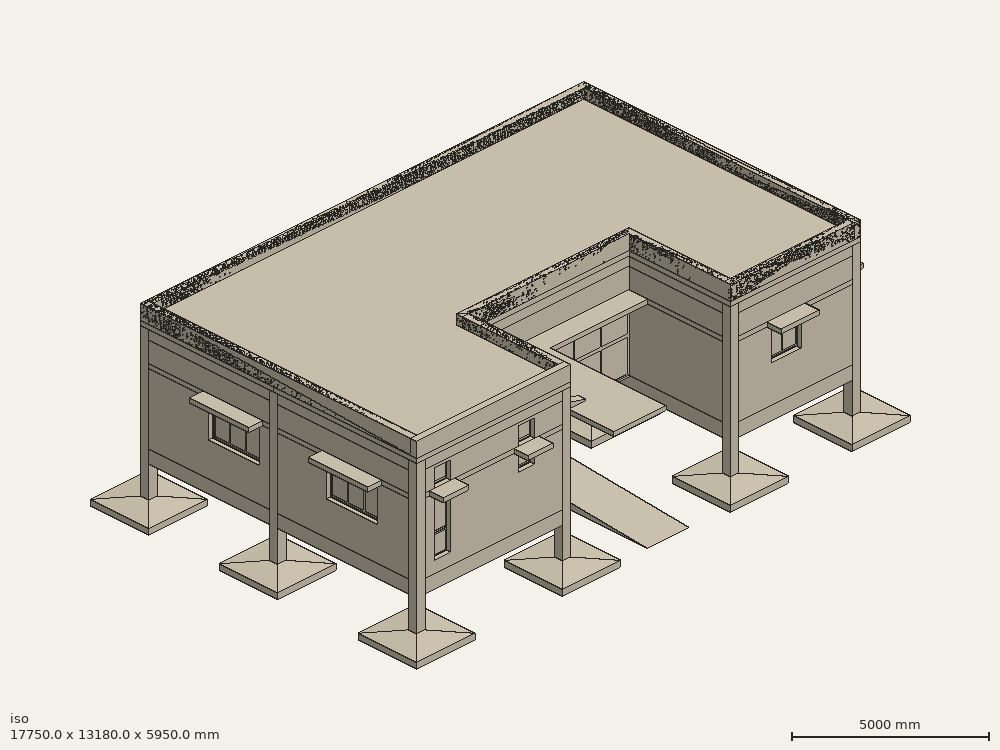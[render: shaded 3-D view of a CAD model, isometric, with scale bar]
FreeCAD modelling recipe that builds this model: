
FCSTD DOCUMENT  (FreeCAD 0.19R19955 (Git))
Label: sLAB sTEEL
License: All rights reserved
LicenseURL: http://en.wikipedia.org/wiki/All_rights_reserved
objects: Part::FeaturePython×230, Sketcher::SketchObject×144, TechDraw::DrawViewDimension×135, TechDraw::DrawViewPart×8, Part::Part2DObjectPython×7, App::FeaturePython×6, App::MaterialObjectPython×6, TechDraw::DrawViewAnnotation×5, TechDraw::DrawViewSymbol×5, App::GeometryPython×4, Spreadsheet::Sheet×3, TechDraw::DrawSVGTemplate×2, TechDraw::DrawPage×2, Part::Wedge×2, Part::Box×2, Part::MultiFuse×2, Part::Feature×1, App::DocumentObjectGroup×1, App::DocumentObjectGroupPython×1
note: 395 computed .brp shape members not serialized (recipe doc carries the construction recipe); baked Part::Feature solids carry a one-line shape summary decoded from their .brp

FEATURE [Part::Feature] Human
  Placement = pos=(500,500,0) rot=(0,0,1;0rad)
  shape: bbox 490.6 x 1.43e-06 x 1712 mm, 1 faces, 0 solids (baked)
FEATURE [Part::Part2DObjectPython] Rectangle  label="Building Outline"  # Draft 2D object (typed FeaturePython)
  Area = 0
  ChamferSize = 0
  Columns = 1
  FilletRadius = 0
  Height = 9930
  Length = 15950
  MakeFace = false
  Rows = 1
FEATURE [App::FeaturePython] Text  label="Building Label"  # WARN: FeaturePython — macro-defined, semantics opaque (R4)
  Placement = pos=(300,-1430,0) rot=(0,0,1;0rad)
  Text = Dispensary
FEATURE [Part::FeaturePython] Axis  label="Vertical Axes"  # WARN: FeaturePython — macro-defined, semantics opaque (R4)
  Angles = [0,0,0,0]
  Distances = [0,5540,5740,4670]
  Length = 10923
  Placement = pos=(0,-546.15,0) rot=(0,0,1;0rad)
  expr: Length = Rectangle.Height * 1.1000000000000001
  expr: .Placement.Base.y = Rectangle.Placement.Base.y - Length * 0.050000000000000003
  expr: .Placement.Base.x = Rectangle.Placement.Base.x
FEATURE [Part::FeaturePython] Axis001  label="Horizontal Axes"  # WARN: FeaturePython — macro-defined, semantics opaque (R4)
  Angles = [0,0,0,0]
  Distances = [0,3650,1500,4780]
  Length = 17545
  Placement = pos=(16580,0,0) rot=(0,0,1;1.5708rad)
  expr: Length = Rectangle.Length * 1.1000000000000001
  expr: .Placement.Base.x = Rectangle.Placement.Base.x + Length * 0.94499999999999995
  expr: .Placement.Base.y = Rectangle.Placement.Base.y
FEATURE [App::FeaturePython] AxisSystem  label="Axes"  # WARN: FeaturePython — macro-defined, semantics opaque (R4)
  Axes = -> [Axis001,Axis]
FEATURE [App::DocumentObjectGroup] App__DocumentObjectGroup  label="Layout"
  Group = -> [Rectangle,Text,Human,AxisSystem]
FEATURE [App::FeaturePython] WPProxy  # WARN: FeaturePython — macro-defined, semantics opaque (R4)
  Placement = pos=(0,0,3500) rot=(0,0,1;0rad)
FEATURE [App::FeaturePython] WPProxy001  # WARN: FeaturePython — macro-defined, semantics opaque (R4)
  Placement = pos=(0,0,3650) rot=(0,0,1;0rad)
FEATURE [App::FeaturePython] WPProxy002  # WARN: FeaturePython — macro-defined, semantics opaque (R4)
  Placement = pos=(0,0,2000) rot=(0,0,1;0rad)
FEATURE [Sketcher::SketchObject] WallTrace
  Placement = pos=(2770,150,0) rot=(0,0,-1;1.5708rad)
  sketch-geometry (1):
    g0: LineSegment StartX=150 StartY=-2470 StartZ=0 EndX=150 EndY=2470 EndZ=0
FEATURE [Sketcher::SketchObject] WallTrace001
  Placement = pos=(2770,150,0) rot=(0,0,-1;1.5708rad)
  sketch-geometry (1):
    g0: LineSegment StartX=150 StartY=8810 StartZ=0 EndX=150 EndY=12880 EndZ=0
FEATURE [Sketcher::SketchObject] WallTrace003
  Placement = pos=(2770,150,0) rot=(0,0,-1;1.5708rad)
  sketch-geometry (1):
    g0: LineSegment StartX=-150 StartY=13180 StartZ=0 EndX=-4850 EndY=13180 EndZ=0
FEATURE [Sketcher::SketchObject] WallTrace004
  Placement = pos=(2770,150,0) rot=(0,0,-1;1.5708rad)
  sketch-geometry (1):
    g0: LineSegment StartX=-5150 StartY=13180 StartZ=0 EndX=-9480 EndY=13180 EndZ=0
FEATURE [Sketcher::SketchObject] WallTrace005
  Placement = pos=(2770,150,0) rot=(0,0,-1;1.5708rad)
  sketch-geometry (1):
    g0: LineSegment StartX=-9780 StartY=12880 StartZ=0 EndX=-9780 EndY=8810 EndZ=0
FEATURE [Sketcher::SketchObject] WallTrace006
  Placement = pos=(2770,150,0) rot=(0,0,-1;1.5708rad)
  sketch-geometry (1):
    g0: LineSegment StartX=-9780 StartY=8510 StartZ=0 EndX=-9780 EndY=2770 EndZ=0
FEATURE [Sketcher::SketchObject] WallTrace007
  Placement = pos=(2770,150,0) rot=(0,0,-1;1.5708rad)
  sketch-geometry (1):
    g0: LineSegment StartX=-9780 StartY=2470 StartZ=0 EndX=-9780 EndY=-2470 EndZ=0
FEATURE [Sketcher::SketchObject] WallTrace008
  Placement = pos=(2770,150,0) rot=(0,0,-1;1.5708rad)
  sketch-geometry (1):
    g0: LineSegment StartX=-9480 StartY=-2770 StartZ=0 EndX=-5150 EndY=-2770 EndZ=0
FEATURE [Sketcher::SketchObject] WallTrace012
  Placement = pos=(5390,2650,0) rot=(0,0,1;0rad)
  sketch-geometry (1):
    g0: LineSegment StartX=150 StartY=-2350 StartZ=0 EndX=150 EndY=1300 EndZ=0
  constraints (2):
    c: DistanceY(g0,g-1) = 2350
    c: DistanceY(g0,g0) = 3650
FEATURE [Sketcher::SketchObject] WallTrace014
  Placement = pos=(11430,2650,0) rot=(0,0,1;0rad)
  sketch-geometry (1):
    g0: LineSegment StartX=-150 StartY=1300 StartZ=0 EndX=-150 EndY=-2350 EndZ=0
  constraints (4):
    c: DistanceX(g0,g-1) = 150
    c: Distance(g0) = 3650
    c: Vertical(g0)
    c: DistanceY(g0,g-1) = 2350
FEATURE [Part::Part2DObjectPython] Rectangle001  # Draft 2D object (typed FeaturePython)
  Area = 2.57642e+07
  ChamferSize = 0
  Columns = 1
  FilletRadius = 0
  Height = 4780
  Length = 5390
  MakeFace = true
  Placement = pos=(5390,9930,3500) rot=(0,0,1;3.14159rad)
  Rows = 1
FEATURE [Part::Part2DObjectPython] Rectangle004  # Draft 2D object (typed FeaturePython)
  Area = 2.88712e+07
  ChamferSize = 0
  Columns = 1
  FilletRadius = 0
  Height = 4780
  Length = 6040
  MakeFace = true
  Placement = pos=(11430,9930,3500) rot=(0,0,1;3.14159rad)
  Rows = 1
FEATURE [Part::Part2DObjectPython] Rectangle005  # Draft 2D object (typed FeaturePython)
  Area = 2.16056e+07
  ChamferSize = 0
  Columns = 1
  FilletRadius = 0
  Height = 4780
  Length = 4520
  MakeFace = true
  Placement = pos=(15950,9930,3500) rot=(0,0,1;3.14159rad)
  Rows = 1
FEATURE [Part::Part2DObjectPython] Rectangle006  # Draft 2D object (typed FeaturePython)
  Area = 2.40505e+07
  ChamferSize = 0
  Columns = 1
  FilletRadius = 0
  Height = 5150
  Length = 4670
  MakeFace = true
  Placement = pos=(15950,5150,3500) rot=(0,0,1;3.14159rad)
  Rows = 1
FEATURE [Part::Part2DObjectPython] Rectangle007  # Draft 2D object (typed FeaturePython)
  Area = 2.8531e+07
  ChamferSize = 0
  Columns = 1
  FilletRadius = 0
  Height = 5150
  Length = 5540
  MakeFace = true
  Placement = pos=(5540,5150,3500) rot=(0,0,1;3.14159rad)
  Rows = 1
FEATURE [Part::Part2DObjectPython] Rectangle008  # Draft 2D object (typed FeaturePython)
  Area = 9.06e+06
  ChamferSize = 0
  Columns = 1
  FilletRadius = 0
  Height = 1500
  Length = 6040
  MakeFace = true
  Placement = pos=(11430,5150,3500) rot=(0,0,1;3.14159rad)
  Rows = 1
FEATURE [Sketcher::SketchObject] Sketch
  Placement = pos=(15950,2650,1600) rot=(0.57735,0.57735,0.57735;2.0944rad)
  sketch-geometry (16):
    g0: LineSegment StartX=-2280 StartY=760 StartZ=0 EndX=-1670 EndY=760 EndZ=0
    g1: LineSegment StartX=-1670 StartY=760 StartZ=0 EndX=-1670 EndY=-1200 EndZ=0
    g2: LineSegment StartX=-1670 StartY=-1200 StartZ=0 EndX=-2280 EndY=-1200 EndZ=0
    g3: LineSegment StartX=-2280 StartY=-1200 StartZ=0 EndX=-2280 EndY=760 EndZ=0
    g4: LineSegment StartX=-2255 StartY=-675 StartZ=0 EndX=-1695 EndY=-675 EndZ=0
    g5: LineSegment StartX=-1695 StartY=-675 StartZ=0 EndX=-1695 EndY=-1175 EndZ=0
    g6: LineSegment StartX=-1695 StartY=-1175 StartZ=0 EndX=-2255 EndY=-1175 EndZ=0
    g7: LineSegment StartX=-2255 StartY=-1175 StartZ=0 EndX=-2255 EndY=-675 EndZ=0
    g8: LineSegment StartX=-2255 StartY=735 StartZ=0 EndX=-1695 EndY=735 EndZ=0
    g9: LineSegment StartX=-1695 StartY=735 StartZ=0 EndX=-1695 EndY=-625 EndZ=0
    g10: LineSegment StartX=-1695 StartY=-625 StartZ=0 EndX=-2255 EndY=-625 EndZ=0
    g11: LineSegment StartX=-2255 StartY=-625 StartZ=0 EndX=-2255 EndY=735 EndZ=0
    g12: LineSegment StartX=-2230 StartY=685 StartZ=0 EndX=-1720 EndY=685 EndZ=0
    g13: LineSegment StartX=-1720 StartY=685 StartZ=0 EndX=-1720 EndY=-575 EndZ=0
    g14: LineSegment StartX=-1720 StartY=-575 StartZ=0 EndX=-2230 EndY=-575 EndZ=0
    g15: LineSegment StartX=-2230 StartY=-575 StartZ=0 EndX=-2230 EndY=685 EndZ=0
  constraints (46):
    c: Coincident(g0,g1)
    c: Coincident(g1,g2)
    c: Coincident(g2,g3)
    c: Coincident(g3,g0)
    c: Horizontal(g0)
    c: Horizontal(g2)
    c: Vertical(g1)
    c: Vertical(g3)
    c: Coincident(g4,g5)
    c: Coincident(g5,g6)
    c: Coincident(g6,g7)
    c: Coincident(g7,g4)
    c: Horizontal(g4)
    c: Horizontal(g6)
    c: Vertical(g5)
    c: Vertical(g7)
    c: Coincident(g8,g9)
    c: Coincident(g9,g10)
    c: Coincident(g10,g11)
    c: Coincident(g11,g8)
    c: Horizontal(g8)
    c: Horizontal(g10)
    c: Vertical(g9)
    c: Vertical(g11)
    c: DistanceY(g1,g5) = 25
    c: DistanceX(g5,g1) = 25
    c: DistanceX(g2,g6) = 25
    c: DistanceY(g1,g1) = 1960
    c: DistanceY(g4,g9) = 50
    c: DistanceX(g4,g10) = 0
    c: DistanceX(g9,g4) = 0
    c: DistanceY(g8,g0) = 25
    c: Coincident(g12,g13)
    c: Coincident(g13,g14)
    c: Coincident(g14,g15)
    c: Coincident(g15,g12)
    c: Horizontal(g12)
    c: Horizontal(g14)
    c: Vertical(g13)
    c: Vertical(g15)
    c: DistanceY(g12,g8) = 50
    c: DistanceY(g9,g13) = 50
    c: DistanceX(g13,g9) = 25
    c: DistanceX(g10,g14) = 25
    c: DistanceX(g0,g0) = 610
    c: DistanceY(g5,g5) = 500
FEATURE [Sketcher::SketchObject] Sketch001
  Placement = pos=(15950,2650,1600) rot=(0.57735,0.57735,0.57735;2.0944rad)
  sketch-geometry (16):
    g0: LineSegment StartX=-2280 StartY=760 StartZ=0 EndX=-1670 EndY=760 EndZ=0
    g1: LineSegment StartX=-1670 StartY=760 StartZ=0 EndX=-1670 EndY=-1200 EndZ=0
    g2: LineSegment StartX=-1670 StartY=-1200 StartZ=0 EndX=-2280 EndY=-1200 EndZ=0
    g3: LineSegment StartX=-2280 StartY=-1200 StartZ=0 EndX=-2280 EndY=760 EndZ=0
    g4: LineSegment StartX=-2255 StartY=-675 StartZ=0 EndX=-1695 EndY=-675 EndZ=0
    g5: LineSegment StartX=-1695 StartY=-675 StartZ=0 EndX=-1695 EndY=-1175 EndZ=0
    g6: LineSegment StartX=-1695 StartY=-1175 StartZ=0 EndX=-2255 EndY=-1175 EndZ=0
    g7: LineSegment StartX=-2255 StartY=-1175 StartZ=0 EndX=-2255 EndY=-675 EndZ=0
    g8: LineSegment StartX=-2255 StartY=735 StartZ=0 EndX=-1695 EndY=735 EndZ=0
    g9: LineSegment StartX=-1695 StartY=735 StartZ=0 EndX=-1695 EndY=-625 EndZ=0
    g10: LineSegment StartX=-1695 StartY=-625 StartZ=0 EndX=-2255 EndY=-625 EndZ=0
    g11: LineSegment StartX=-2255 StartY=-625 StartZ=0 EndX=-2255 EndY=735 EndZ=0
    g12: LineSegment StartX=-2230 StartY=685 StartZ=0 EndX=-1720 EndY=685 EndZ=0
    g13: LineSegment StartX=-1720 StartY=685 StartZ=0 EndX=-1720 EndY=-575 EndZ=0
    g14: LineSegment StartX=-1720 StartY=-575 StartZ=0 EndX=-2230 EndY=-575 EndZ=0
    g15: LineSegment StartX=-2230 StartY=-575 StartZ=0 EndX=-2230 EndY=685 EndZ=0
  constraints (46):
    c: Coincident(g0,g1)
    c: Coincident(g1,g2)
    c: Coincident(g2,g3)
    c: Coincident(g3,g0)
    c: Horizontal(g0)
    c: Horizontal(g2)
    c: Vertical(g1)
    c: Vertical(g3)
    c: Coincident(g4,g5)
    c: Coincident(g5,g6)
    c: Coincident(g6,g7)
    c: Coincident(g7,g4)
    c: Horizontal(g4)
    c: Horizontal(g6)
    c: Vertical(g5)
    c: Vertical(g7)
    c: Coincident(g8,g9)
    c: Coincident(g9,g10)
    c: Coincident(g10,g11)
    c: Coincident(g11,g8)
    c: Horizontal(g8)
    c: Horizontal(g10)
    c: Vertical(g9)
    c: Vertical(g11)
    c: DistanceY(g1,g5) = 25
    c: DistanceX(g5,g1) = 25
    c: DistanceX(g2,g6) = 25
    c: DistanceY(g1,g1) = 1960
    c: DistanceY(g4,g9) = 50
    c: DistanceX(g4,g10) = 0
    c: DistanceX(g9,g4) = 0
    c: DistanceY(g8,g0) = 25
    c: Coincident(g12,g13)
    c: Coincident(g13,g14)
    c: Coincident(g14,g15)
    c: Coincident(g15,g12)
    c: Horizontal(g12)
    c: Horizontal(g14)
    c: Vertical(g13)
    c: Vertical(g15)
    c: DistanceY(g12,g8) = 50
    c: DistanceY(g9,g13) = 50
    c: DistanceX(g13,g9) = 25
    c: DistanceX(g10,g14) = 25
    c: DistanceX(g0,g0) = 610
    c: DistanceY(g5,g5) = 500
FEATURE [Sketcher::SketchObject] Sketch002
  Placement = pos=(15950,2650,1600) rot=(0.57735,0.57735,0.57735;2.0944rad)
  sketch-geometry (16):
    g0: LineSegment StartX=-2280 StartY=760 StartZ=0 EndX=-1670 EndY=760 EndZ=0
    g1: LineSegment StartX=-1670 StartY=760 StartZ=0 EndX=-1670 EndY=-1200 EndZ=0
    g2: LineSegment StartX=-1670 StartY=-1200 StartZ=0 EndX=-2280 EndY=-1200 EndZ=0
    g3: LineSegment StartX=-2280 StartY=-1200 StartZ=0 EndX=-2280 EndY=760 EndZ=0
    g4: LineSegment StartX=-2255 StartY=-675 StartZ=0 EndX=-1695 EndY=-675 EndZ=0
    g5: LineSegment StartX=-1695 StartY=-675 StartZ=0 EndX=-1695 EndY=-1175 EndZ=0
    g6: LineSegment StartX=-1695 StartY=-1175 StartZ=0 EndX=-2255 EndY=-1175 EndZ=0
    g7: LineSegment StartX=-2255 StartY=-1175 StartZ=0 EndX=-2255 EndY=-675 EndZ=0
    g8: LineSegment StartX=-2255 StartY=735 StartZ=0 EndX=-1695 EndY=735 EndZ=0
    g9: LineSegment StartX=-1695 StartY=735 StartZ=0 EndX=-1695 EndY=-625 EndZ=0
    g10: LineSegment StartX=-1695 StartY=-625 StartZ=0 EndX=-2255 EndY=-625 EndZ=0
    g11: LineSegment StartX=-2255 StartY=-625 StartZ=0 EndX=-2255 EndY=735 EndZ=0
    g12: LineSegment StartX=-2230 StartY=685 StartZ=0 EndX=-1720 EndY=685 EndZ=0
    g13: LineSegment StartX=-1720 StartY=685 StartZ=0 EndX=-1720 EndY=-575 EndZ=0
    g14: LineSegment StartX=-1720 StartY=-575 StartZ=0 EndX=-2230 EndY=-575 EndZ=0
    g15: LineSegment StartX=-2230 StartY=-575 StartZ=0 EndX=-2230 EndY=685 EndZ=0
  constraints (46):
    c: Coincident(g0,g1)
    c: Coincident(g1,g2)
    c: Coincident(g2,g3)
    c: Coincident(g3,g0)
    c: Horizontal(g0)
    c: Horizontal(g2)
    c: Vertical(g1)
    c: Vertical(g3)
    c: Coincident(g4,g5)
    c: Coincident(g5,g6)
    c: Coincident(g6,g7)
    c: Coincident(g7,g4)
    c: Horizontal(g4)
    c: Horizontal(g6)
    c: Vertical(g5)
    c: Vertical(g7)
    c: Coincident(g8,g9)
    c: Coincident(g9,g10)
    c: Coincident(g10,g11)
    c: Coincident(g11,g8)
    c: Horizontal(g8)
    c: Horizontal(g10)
    c: Vertical(g9)
    c: Vertical(g11)
    c: DistanceY(g1,g5) = 25
    c: DistanceX(g5,g1) = 25
    c: DistanceX(g2,g6) = 25
    c: DistanceY(g1,g1) = 1960
    c: DistanceY(g4,g9) = 50
    c: DistanceX(g4,g10) = 0
    c: DistanceX(g9,g4) = 0
    c: DistanceY(g8,g0) = 25
    c: Coincident(g12,g13)
    c: Coincident(g13,g14)
    c: Coincident(g14,g15)
    c: Coincident(g15,g12)
    c: Horizontal(g12)
    c: Horizontal(g14)
    c: Vertical(g13)
    c: Vertical(g15)
    c: DistanceY(g12,g8) = 50
    c: DistanceY(g9,g13) = 50
    c: DistanceX(g13,g9) = 25
    c: DistanceX(g10,g14) = 25
    c: DistanceX(g0,g0) = 610
    c: DistanceY(g5,g5) = 500
FEATURE [Sketcher::SketchObject] Sketch003
  Placement = pos=(15950,2650,1600) rot=(0.57735,0.57735,0.57735;2.0944rad)
  sketch-geometry (16):
    g0: LineSegment StartX=-2280 StartY=760 StartZ=0 EndX=-1670 EndY=760 EndZ=0
    g1: LineSegment StartX=-1670 StartY=760 StartZ=0 EndX=-1670 EndY=-1200 EndZ=0
    g2: LineSegment StartX=-1670 StartY=-1200 StartZ=0 EndX=-2280 EndY=-1200 EndZ=0
    g3: LineSegment StartX=-2280 StartY=-1200 StartZ=0 EndX=-2280 EndY=760 EndZ=0
    g4: LineSegment StartX=-2255 StartY=-675 StartZ=0 EndX=-1695 EndY=-675 EndZ=0
    g5: LineSegment StartX=-1695 StartY=-675 StartZ=0 EndX=-1695 EndY=-1175 EndZ=0
    g6: LineSegment StartX=-1695 StartY=-1175 StartZ=0 EndX=-2255 EndY=-1175 EndZ=0
    g7: LineSegment StartX=-2255 StartY=-1175 StartZ=0 EndX=-2255 EndY=-675 EndZ=0
    g8: LineSegment StartX=-2255 StartY=735 StartZ=0 EndX=-1695 EndY=735 EndZ=0
    g9: LineSegment StartX=-1695 StartY=735 StartZ=0 EndX=-1695 EndY=-625 EndZ=0
    g10: LineSegment StartX=-1695 StartY=-625 StartZ=0 EndX=-2255 EndY=-625 EndZ=0
    g11: LineSegment StartX=-2255 StartY=-625 StartZ=0 EndX=-2255 EndY=735 EndZ=0
    g12: LineSegment StartX=-2230 StartY=685 StartZ=0 EndX=-1720 EndY=685 EndZ=0
    g13: LineSegment StartX=-1720 StartY=685 StartZ=0 EndX=-1720 EndY=-575 EndZ=0
    g14: LineSegment StartX=-1720 StartY=-575 StartZ=0 EndX=-2230 EndY=-575 EndZ=0
    g15: LineSegment StartX=-2230 StartY=-575 StartZ=0 EndX=-2230 EndY=685 EndZ=0
  constraints (46):
    c: Coincident(g0,g1)
    c: Coincident(g1,g2)
    c: Coincident(g2,g3)
    c: Coincident(g3,g0)
    c: Horizontal(g0)
    c: Horizontal(g2)
    c: Vertical(g1)
    c: Vertical(g3)
    c: Coincident(g4,g5)
    c: Coincident(g5,g6)
    c: Coincident(g6,g7)
    c: Coincident(g7,g4)
    c: Horizontal(g4)
    c: Horizontal(g6)
    c: Vertical(g5)
    c: Vertical(g7)
    c: Coincident(g8,g9)
    c: Coincident(g9,g10)
    c: Coincident(g10,g11)
    c: Coincident(g11,g8)
    c: Horizontal(g8)
    c: Horizontal(g10)
    c: Vertical(g9)
    c: Vertical(g11)
    c: DistanceY(g1,g5) = 25
    c: DistanceX(g5,g1) = 25
    c: DistanceX(g2,g6) = 25
    c: DistanceY(g1,g1) = 1960
    c: DistanceY(g4,g9) = 50
    c: DistanceX(g4,g10) = 0
    c: DistanceX(g9,g4) = 0
    c: DistanceY(g8,g0) = 25
    c: Coincident(g12,g13)
    c: Coincident(g13,g14)
    c: Coincident(g14,g15)
    c: Coincident(g15,g12)
    c: Horizontal(g12)
    c: Horizontal(g14)
    c: Vertical(g13)
    c: Vertical(g15)
    c: DistanceY(g12,g8) = 50
    c: DistanceY(g9,g13) = 50
    c: DistanceX(g13,g9) = 25
    c: DistanceX(g10,g14) = 25
    c: DistanceX(g0,g0) = 610
    c: DistanceY(g5,g5) = 500
FEATURE [Sketcher::SketchObject] Sketch006
  Placement = pos=(15950,2698.54,1668.9) rot=(0.57735,0.57735,0.57735;2.0944rad)
  sketch-geometry (12):
    g0: LineSegment StartX=-2328.54 StartY=1451.1 StartZ=0 EndX=-1718.54 EndY=1451.1 EndZ=0
    g1: LineSegment StartX=-1718.54 StartY=1451.1 StartZ=0 EndX=-1718.54 EndY=841.103 EndZ=0
    g2: LineSegment StartX=-1718.54 StartY=841.103 StartZ=0 EndX=-2328.54 EndY=841.103 EndZ=0
    g3: LineSegment StartX=-2328.54 StartY=841.103 StartZ=0 EndX=-2328.54 EndY=1451.1 EndZ=0
    g4: LineSegment StartX=-2303.54 StartY=1426.1 StartZ=0 EndX=-1743.54 EndY=1426.1 EndZ=0
    g5: LineSegment StartX=-1743.54 StartY=1426.1 StartZ=0 EndX=-1743.54 EndY=866.103 EndZ=0
    g6: LineSegment StartX=-1743.54 StartY=866.103 StartZ=0 EndX=-2303.54 EndY=866.103 EndZ=0
    g7: LineSegment StartX=-2303.54 StartY=866.103 StartZ=0 EndX=-2303.54 EndY=1426.1 EndZ=0
    g8: LineSegment StartX=-2278.54 StartY=1376.1 StartZ=0 EndX=-1768.54 EndY=1376.1 EndZ=0
    g9: LineSegment StartX=-1768.54 StartY=1376.1 StartZ=0 EndX=-1768.54 EndY=916.103 EndZ=0
    g10: LineSegment StartX=-1768.54 StartY=916.103 StartZ=0 EndX=-2278.54 EndY=916.103 EndZ=0
    g11: LineSegment StartX=-2278.54 StartY=916.103 StartZ=0 EndX=-2278.54 EndY=1376.1 EndZ=0
  constraints (34):
    c: Coincident(g0,g1)
    c: Coincident(g1,g2)
    c: Coincident(g2,g3)
    c: Coincident(g3,g0)
    c: Horizontal(g0)
    c: Horizontal(g2)
    c: Vertical(g1)
    c: Vertical(g3)
    c: Coincident(g4,g5)
    c: Coincident(g5,g6)
    c: Coincident(g6,g7)
    c: Coincident(g7,g4)
    c: Horizontal(g4)
    c: Horizontal(g6)
    c: Vertical(g5)
    c: Vertical(g7)
    c: Coincident(g8,g9)
    c: Coincident(g9,g10)
    c: Coincident(g10,g11)
    c: Coincident(g11,g8)
    c: Horizontal(g8)
    c: Horizontal(g10)
    c: Vertical(g9)
    c: Vertical(g11)
    c: DistanceY(g4,g0) = 25
    c: DistanceY(g1,g5) = 25
    c: DistanceY(g5,g9) = 50
    c: DistanceY(g8,g4) = 50
    c: DistanceY(g1,g1) = 610
    c: DistanceX(g4,g8) = 25
    c: DistanceX(g0,g4) = 25
    c: DistanceX(g8,g4) = 25
    c: DistanceX(g5,g1) = 25
    c: DistanceX(g2,g2) = 610
FEATURE [Sketcher::SketchObject] Sketch007
  Placement = pos=(15950,2698.54,1668.9) rot=(0.57735,0.57735,0.57735;2.0944rad)
  sketch-geometry (12):
    g0: LineSegment StartX=-2328.54 StartY=1451.1 StartZ=0 EndX=-1718.54 EndY=1451.1 EndZ=0
    g1: LineSegment StartX=-1718.54 StartY=1451.1 StartZ=0 EndX=-1718.54 EndY=841.103 EndZ=0
    g2: LineSegment StartX=-1718.54 StartY=841.103 StartZ=0 EndX=-2328.54 EndY=841.103 EndZ=0
    g3: LineSegment StartX=-2328.54 StartY=841.103 StartZ=0 EndX=-2328.54 EndY=1451.1 EndZ=0
    g4: LineSegment StartX=-2303.54 StartY=1426.1 StartZ=0 EndX=-1743.54 EndY=1426.1 EndZ=0
    g5: LineSegment StartX=-1743.54 StartY=1426.1 StartZ=0 EndX=-1743.54 EndY=866.103 EndZ=0
    g6: LineSegment StartX=-1743.54 StartY=866.103 StartZ=0 EndX=-2303.54 EndY=866.103 EndZ=0
    g7: LineSegment StartX=-2303.54 StartY=866.103 StartZ=0 EndX=-2303.54 EndY=1426.1 EndZ=0
    g8: LineSegment StartX=-2278.54 StartY=1376.1 StartZ=0 EndX=-1768.54 EndY=1376.1 EndZ=0
    g9: LineSegment StartX=-1768.54 StartY=1376.1 StartZ=0 EndX=-1768.54 EndY=916.103 EndZ=0
    g10: LineSegment StartX=-1768.54 StartY=916.103 StartZ=0 EndX=-2278.54 EndY=916.103 EndZ=0
    g11: LineSegment StartX=-2278.54 StartY=916.103 StartZ=0 EndX=-2278.54 EndY=1376.1 EndZ=0
  constraints (34):
    c: Coincident(g0,g1)
    c: Coincident(g1,g2)
    c: Coincident(g2,g3)
    c: Coincident(g3,g0)
    c: Horizontal(g0)
    c: Horizontal(g2)
    c: Vertical(g1)
    c: Vertical(g3)
    c: Coincident(g4,g5)
    c: Coincident(g5,g6)
    c: Coincident(g6,g7)
    c: Coincident(g7,g4)
    c: Horizontal(g4)
    c: Horizontal(g6)
    c: Vertical(g5)
    c: Vertical(g7)
    c: Coincident(g8,g9)
    c: Coincident(g9,g10)
    c: Coincident(g10,g11)
    c: Coincident(g11,g8)
    c: Horizontal(g8)
    c: Horizontal(g10)
    c: Vertical(g9)
    c: Vertical(g11)
    c: DistanceY(g4,g0) = 25
    c: DistanceY(g1,g5) = 25
    c: DistanceY(g5,g9) = 50
    c: DistanceY(g8,g4) = 50
    c: DistanceY(g1,g1) = 610
    c: DistanceX(g4,g8) = 25
    c: DistanceX(g0,g4) = 25
    c: DistanceX(g8,g4) = 25
    c: DistanceX(g5,g1) = 25
    c: DistanceX(g2,g2) = 610
FEATURE [Sketcher::SketchObject] Sketch008
  Placement = pos=(15950,2698.54,1668.9) rot=(0.57735,0.57735,0.57735;2.0944rad)
  sketch-geometry (12):
    g0: LineSegment StartX=-2328.54 StartY=1451.1 StartZ=0 EndX=-1718.54 EndY=1451.1 EndZ=0
    g1: LineSegment StartX=-1718.54 StartY=1451.1 StartZ=0 EndX=-1718.54 EndY=841.103 EndZ=0
    g2: LineSegment StartX=-1718.54 StartY=841.103 StartZ=0 EndX=-2328.54 EndY=841.103 EndZ=0
    g3: LineSegment StartX=-2328.54 StartY=841.103 StartZ=0 EndX=-2328.54 EndY=1451.1 EndZ=0
    g4: LineSegment StartX=-2303.54 StartY=1426.1 StartZ=0 EndX=-1743.54 EndY=1426.1 EndZ=0
    g5: LineSegment StartX=-1743.54 StartY=1426.1 StartZ=0 EndX=-1743.54 EndY=866.103 EndZ=0
    g6: LineSegment StartX=-1743.54 StartY=866.103 StartZ=0 EndX=-2303.54 EndY=866.103 EndZ=0
    g7: LineSegment StartX=-2303.54 StartY=866.103 StartZ=0 EndX=-2303.54 EndY=1426.1 EndZ=0
    g8: LineSegment StartX=-2278.54 StartY=1376.1 StartZ=0 EndX=-1768.54 EndY=1376.1 EndZ=0
    g9: LineSegment StartX=-1768.54 StartY=1376.1 StartZ=0 EndX=-1768.54 EndY=916.103 EndZ=0
    g10: LineSegment StartX=-1768.54 StartY=916.103 StartZ=0 EndX=-2278.54 EndY=916.103 EndZ=0
    g11: LineSegment StartX=-2278.54 StartY=916.103 StartZ=0 EndX=-2278.54 EndY=1376.1 EndZ=0
  constraints (34):
    c: Coincident(g0,g1)
    c: Coincident(g1,g2)
    c: Coincident(g2,g3)
    c: Coincident(g3,g0)
    c: Horizontal(g0)
    c: Horizontal(g2)
    c: Vertical(g1)
    c: Vertical(g3)
    c: Coincident(g4,g5)
    c: Coincident(g5,g6)
    c: Coincident(g6,g7)
    c: Coincident(g7,g4)
    c: Horizontal(g4)
    c: Horizontal(g6)
    c: Vertical(g5)
    c: Vertical(g7)
    c: Coincident(g8,g9)
    c: Coincident(g9,g10)
    c: Coincident(g10,g11)
    c: Coincident(g11,g8)
    c: Horizontal(g8)
    c: Horizontal(g10)
    c: Vertical(g9)
    c: Vertical(g11)
    c: DistanceY(g4,g0) = 25
    c: DistanceY(g1,g5) = 25
    c: DistanceY(g5,g9) = 50
    c: DistanceY(g8,g4) = 50
    c: DistanceY(g1,g1) = 610
    c: DistanceX(g4,g8) = 25
    c: DistanceX(g0,g4) = 25
    c: DistanceX(g8,g4) = 25
    c: DistanceX(g5,g1) = 25
    c: DistanceX(g2,g2) = 610
FEATURE [Sketcher::SketchObject] Sketch009
  Placement = pos=(15950,2698.54,1668.9) rot=(0.57735,0.57735,0.57735;2.0944rad)
  sketch-geometry (12):
    g0: LineSegment StartX=-2328.54 StartY=1451.1 StartZ=0 EndX=-1718.54 EndY=1451.1 EndZ=0
    g1: LineSegment StartX=-1718.54 StartY=1451.1 StartZ=0 EndX=-1718.54 EndY=841.103 EndZ=0
    g2: LineSegment StartX=-1718.54 StartY=841.103 StartZ=0 EndX=-2328.54 EndY=841.103 EndZ=0
    g3: LineSegment StartX=-2328.54 StartY=841.103 StartZ=0 EndX=-2328.54 EndY=1451.1 EndZ=0
    g4: LineSegment StartX=-2303.54 StartY=1426.1 StartZ=0 EndX=-1743.54 EndY=1426.1 EndZ=0
    g5: LineSegment StartX=-1743.54 StartY=1426.1 StartZ=0 EndX=-1743.54 EndY=866.103 EndZ=0
    g6: LineSegment StartX=-1743.54 StartY=866.103 StartZ=0 EndX=-2303.54 EndY=866.103 EndZ=0
    g7: LineSegment StartX=-2303.54 StartY=866.103 StartZ=0 EndX=-2303.54 EndY=1426.1 EndZ=0
    g8: LineSegment StartX=-2278.54 StartY=1376.1 StartZ=0 EndX=-1768.54 EndY=1376.1 EndZ=0
    g9: LineSegment StartX=-1768.54 StartY=1376.1 StartZ=0 EndX=-1768.54 EndY=916.103 EndZ=0
    g10: LineSegment StartX=-1768.54 StartY=916.103 StartZ=0 EndX=-2278.54 EndY=916.103 EndZ=0
    g11: LineSegment StartX=-2278.54 StartY=916.103 StartZ=0 EndX=-2278.54 EndY=1376.1 EndZ=0
  constraints (34):
    c: Coincident(g0,g1)
    c: Coincident(g1,g2)
    c: Coincident(g2,g3)
    c: Coincident(g3,g0)
    c: Horizontal(g0)
    c: Horizontal(g2)
    c: Vertical(g1)
    c: Vertical(g3)
    c: Coincident(g4,g5)
    c: Coincident(g5,g6)
    c: Coincident(g6,g7)
    c: Coincident(g7,g4)
    c: Horizontal(g4)
    c: Horizontal(g6)
    c: Vertical(g5)
    c: Vertical(g7)
    c: Coincident(g8,g9)
    c: Coincident(g9,g10)
    c: Coincident(g10,g11)
    c: Coincident(g11,g8)
    c: Horizontal(g8)
    c: Horizontal(g10)
    c: Vertical(g9)
    c: Vertical(g11)
    c: DistanceY(g4,g0) = 25
    c: DistanceY(g1,g5) = 25
    c: DistanceY(g5,g9) = 50
    c: DistanceY(g8,g4) = 50
    c: DistanceY(g1,g1) = 610
    c: DistanceX(g4,g8) = 25
    c: DistanceX(g0,g4) = 25
    c: DistanceX(g8,g4) = 25
    c: DistanceX(g5,g1) = 25
    c: DistanceX(g2,g2) = 610
FEATURE [Sketcher::SketchObject] Sketch011
  Placement = pos=(15950,2724.08,1084.42) rot=(0.57735,0.57735,0.57735;2.0944rad)
  sketch-geometry (4):
    g0: LineSegment StartX=-2504.08 StartY=1425.58 StartZ=0 EndX=-1594.08 EndY=1425.58 EndZ=0
    g1: LineSegment StartX=-1594.08 StartY=1425.58 StartZ=0 EndX=-1594.08 EndY=1275.58 EndZ=0
    g2: LineSegment StartX=-1594.08 StartY=1275.58 StartZ=0 EndX=-2504.08 EndY=1275.58 EndZ=0
    g3: LineSegment StartX=-2504.08 StartY=1275.58 StartZ=0 EndX=-2504.08 EndY=1425.58 EndZ=0
  constraints (10):
    c: Coincident(g0,g1)
    c: Coincident(g1,g2)
    c: Coincident(g2,g3)
    c: Coincident(g3,g0)
    c: Horizontal(g0)
    c: Horizontal(g2)
    c: Vertical(g1)
    c: Vertical(g3)
    c: DistanceY(g1,g1) = 150
    c: DistanceX(g0,g0) = 910
FEATURE [Sketcher::SketchObject] Sketch012
  Placement = pos=(15950,2724.08,1084.42) rot=(0.57735,0.57735,0.57735;2.0944rad)
  sketch-geometry (4):
    g0: LineSegment StartX=-2504.08 StartY=1425.58 StartZ=0 EndX=-1594.08 EndY=1425.58 EndZ=0
    g1: LineSegment StartX=-1594.08 StartY=1425.58 StartZ=0 EndX=-1594.08 EndY=1275.58 EndZ=0
    g2: LineSegment StartX=-1594.08 StartY=1275.58 StartZ=0 EndX=-2504.08 EndY=1275.58 EndZ=0
    g3: LineSegment StartX=-2504.08 StartY=1275.58 StartZ=0 EndX=-2504.08 EndY=1425.58 EndZ=0
  constraints (10):
    c: Coincident(g0,g1)
    c: Coincident(g1,g2)
    c: Coincident(g2,g3)
    c: Coincident(g3,g0)
    c: Horizontal(g0)
    c: Horizontal(g2)
    c: Vertical(g1)
    c: Vertical(g3)
    c: DistanceY(g1,g1) = 150
    c: DistanceX(g0,g0) = 910
FEATURE [Sketcher::SketchObject] Sketch013
  Placement = pos=(15950,2724.08,1084.42) rot=(0.57735,0.57735,0.57735;2.0944rad)
  sketch-geometry (4):
    g0: LineSegment StartX=-2504.08 StartY=1425.58 StartZ=0 EndX=-1594.08 EndY=1425.58 EndZ=0
    g1: LineSegment StartX=-1594.08 StartY=1425.58 StartZ=0 EndX=-1594.08 EndY=1275.58 EndZ=0
    g2: LineSegment StartX=-1594.08 StartY=1275.58 StartZ=0 EndX=-2504.08 EndY=1275.58 EndZ=0
    g3: LineSegment StartX=-2504.08 StartY=1275.58 StartZ=0 EndX=-2504.08 EndY=1425.58 EndZ=0
  constraints (10):
    c: Coincident(g0,g1)
    c: Coincident(g1,g2)
    c: Coincident(g2,g3)
    c: Coincident(g3,g0)
    c: Horizontal(g0)
    c: Horizontal(g2)
    c: Vertical(g1)
    c: Vertical(g3)
    c: DistanceY(g1,g1) = 150
    c: DistanceX(g0,g0) = 910
FEATURE [Sketcher::SketchObject] Sketch014
  Placement = pos=(15950,2724.08,1084.42) rot=(0.57735,0.57735,0.57735;2.0944rad)
  sketch-geometry (4):
    g0: LineSegment StartX=-2504.08 StartY=1425.58 StartZ=0 EndX=-1594.08 EndY=1425.58 EndZ=0
    g1: LineSegment StartX=-1594.08 StartY=1425.58 StartZ=0 EndX=-1594.08 EndY=1275.58 EndZ=0
    g2: LineSegment StartX=-1594.08 StartY=1275.58 StartZ=0 EndX=-2504.08 EndY=1275.58 EndZ=0
    g3: LineSegment StartX=-2504.08 StartY=1275.58 StartZ=0 EndX=-2504.08 EndY=1425.58 EndZ=0
  constraints (10):
    c: Coincident(g0,g1)
    c: Coincident(g1,g2)
    c: Coincident(g2,g3)
    c: Coincident(g3,g0)
    c: Horizontal(g0)
    c: Horizontal(g2)
    c: Vertical(g1)
    c: Vertical(g3)
    c: DistanceY(g1,g1) = 150
    c: DistanceX(g0,g0) = 910
FEATURE [Sketcher::SketchObject] Sketch016
  Placement = pos=(13615,9930,1600) rot=(0,0.707107,0.707107;3.14159rad)
  sketch-geometry (12):
    g0: LineSegment StartX=-1875 StartY=760 StartZ=0 EndX=-1265 EndY=760 EndZ=0
    g1: LineSegment StartX=-1265 StartY=760 StartZ=0 EndX=-1265 EndY=150 EndZ=0
    g2: LineSegment StartX=-1265 StartY=150 StartZ=0 EndX=-1875 EndY=150 EndZ=0
    g3: LineSegment StartX=-1875 StartY=150 StartZ=0 EndX=-1875 EndY=760 EndZ=0
    g4: LineSegment StartX=-1850 StartY=735 StartZ=0 EndX=-1290 EndY=735 EndZ=0
    g5: LineSegment StartX=-1290 StartY=735 StartZ=0 EndX=-1290 EndY=175 EndZ=0
    g6: LineSegment StartX=-1290 StartY=175 StartZ=0 EndX=-1850 EndY=175 EndZ=0
    g7: LineSegment StartX=-1850 StartY=175 StartZ=0 EndX=-1850 EndY=735 EndZ=0
    g8: LineSegment StartX=-1825 StartY=685 StartZ=0 EndX=-1315 EndY=685 EndZ=0
    g9: LineSegment StartX=-1315 StartY=685 StartZ=0 EndX=-1315 EndY=225 EndZ=0
    g10: LineSegment StartX=-1315 StartY=225 StartZ=0 EndX=-1825 EndY=225 EndZ=0
    g11: LineSegment StartX=-1825 StartY=225 StartZ=0 EndX=-1825 EndY=685 EndZ=0
  constraints (34):
    c: Coincident(g0,g1)
    c: Coincident(g1,g2)
    c: Coincident(g2,g3)
    c: Coincident(g3,g0)
    c: Horizontal(g0)
    c: Horizontal(g2)
    c: Vertical(g1)
    c: Vertical(g3)
    c: Coincident(g4,g5)
    c: Coincident(g5,g6)
    c: Coincident(g6,g7)
    c: Coincident(g7,g4)
    c: Horizontal(g4)
    c: Horizontal(g6)
    c: Vertical(g5)
    c: Vertical(g7)
    c: Coincident(g8,g9)
    c: Coincident(g9,g10)
    c: Coincident(g10,g11)
    c: Coincident(g11,g8)
    c: Horizontal(g8)
    c: Horizontal(g10)
    c: Vertical(g9)
    c: Vertical(g11)
    c: DistanceX(g4,g0) = 25
    c: DistanceX(g0,g4) = 25
    c: DistanceX(g4,g8) = 25
    c: DistanceX(g8,g4) = 25
    c: DistanceX(g0,g0) = 610
    c: DistanceY(g4,g0) = 25
    c: DistanceY(g8,g4) = 50
    c: DistanceY(g5,g9) = 50
    c: DistanceY(g1,g5) = 25
    c: DistanceY(g1,g1) = 610
FEATURE [Sketcher::SketchObject] Sketch017
  Placement = pos=(13615,9930,1600) rot=(0,0.707107,0.707107;3.14159rad)
  sketch-geometry (12):
    g0: LineSegment StartX=-1875 StartY=760 StartZ=0 EndX=-1265 EndY=760 EndZ=0
    g1: LineSegment StartX=-1265 StartY=760 StartZ=0 EndX=-1265 EndY=150 EndZ=0
    g2: LineSegment StartX=-1265 StartY=150 StartZ=0 EndX=-1875 EndY=150 EndZ=0
    g3: LineSegment StartX=-1875 StartY=150 StartZ=0 EndX=-1875 EndY=760 EndZ=0
    g4: LineSegment StartX=-1850 StartY=735 StartZ=0 EndX=-1290 EndY=735 EndZ=0
    g5: LineSegment StartX=-1290 StartY=735 StartZ=0 EndX=-1290 EndY=175 EndZ=0
    g6: LineSegment StartX=-1290 StartY=175 StartZ=0 EndX=-1850 EndY=175 EndZ=0
    g7: LineSegment StartX=-1850 StartY=175 StartZ=0 EndX=-1850 EndY=735 EndZ=0
    g8: LineSegment StartX=-1825 StartY=685 StartZ=0 EndX=-1315 EndY=685 EndZ=0
    g9: LineSegment StartX=-1315 StartY=685 StartZ=0 EndX=-1315 EndY=225 EndZ=0
    g10: LineSegment StartX=-1315 StartY=225 StartZ=0 EndX=-1825 EndY=225 EndZ=0
    g11: LineSegment StartX=-1825 StartY=225 StartZ=0 EndX=-1825 EndY=685 EndZ=0
  constraints (34):
    c: Coincident(g0,g1)
    c: Coincident(g1,g2)
    c: Coincident(g2,g3)
    c: Coincident(g3,g0)
    c: Horizontal(g0)
    c: Horizontal(g2)
    c: Vertical(g1)
    c: Vertical(g3)
    c: Coincident(g4,g5)
    c: Coincident(g5,g6)
    c: Coincident(g6,g7)
    c: Coincident(g7,g4)
    c: Horizontal(g4)
    c: Horizontal(g6)
    c: Vertical(g5)
    c: Vertical(g7)
    c: Coincident(g8,g9)
    c: Coincident(g9,g10)
    c: Coincident(g10,g11)
    c: Coincident(g11,g8)
    c: Horizontal(g8)
    c: Horizontal(g10)
    c: Vertical(g9)
    c: Vertical(g11)
    c: DistanceX(g4,g0) = 25
    c: DistanceX(g0,g4) = 25
    c: DistanceX(g4,g8) = 25
    c: DistanceX(g8,g4) = 25
    c: DistanceX(g0,g0) = 610
    c: DistanceY(g4,g0) = 25
    c: DistanceY(g8,g4) = 50
    c: DistanceY(g5,g9) = 50
    c: DistanceY(g1,g5) = 25
    c: DistanceY(g1,g1) = 610
FEATURE [Sketcher::SketchObject] Sketch019
  Placement = pos=(13615.4,9930,1106.51) rot=(-1,0,0;1.5708rad)
  sketch-geometry (12):
    g0: LineSegment StartX=1874.58 StartY=-2013.49 StartZ=0 EndX=1264.58 EndY=-2013.49 EndZ=0
    g1: LineSegment StartX=1264.58 StartY=-2013.49 StartZ=0 EndX=1264.58 EndY=-1403.49 EndZ=0
    g2: LineSegment StartX=1264.58 StartY=-1403.49 StartZ=0 EndX=1874.58 EndY=-1403.49 EndZ=0
    g3: LineSegment StartX=1874.58 StartY=-1403.49 StartZ=0 EndX=1874.58 EndY=-2013.49 EndZ=0
    g4: LineSegment StartX=1849.58 StartY=-1988.49 StartZ=0 EndX=1289.58 EndY=-1988.49 EndZ=0
    g5: LineSegment StartX=1289.58 StartY=-1988.49 StartZ=0 EndX=1289.58 EndY=-1428.49 EndZ=0
    g6: LineSegment StartX=1289.58 StartY=-1428.49 StartZ=0 EndX=1849.58 EndY=-1428.49 EndZ=0
    g7: LineSegment StartX=1849.58 StartY=-1428.49 StartZ=0 EndX=1849.58 EndY=-1988.49 EndZ=0
    g8: LineSegment StartX=1824.58 StartY=-1938.49 StartZ=0 EndX=1314.58 EndY=-1938.49 EndZ=0
    g9: LineSegment StartX=1314.58 StartY=-1938.49 StartZ=0 EndX=1314.58 EndY=-1478.49 EndZ=0
    g10: LineSegment StartX=1314.58 StartY=-1478.49 StartZ=0 EndX=1824.58 EndY=-1478.49 EndZ=0
    g11: LineSegment StartX=1824.58 StartY=-1478.49 StartZ=0 EndX=1824.58 EndY=-1938.49 EndZ=0
  constraints (34):
    c: Coincident(g0,g1)
    c: Coincident(g1,g2)
    c: Coincident(g2,g3)
    c: Coincident(g3,g0)
    c: Horizontal(g0)
    c: Horizontal(g2)
    c: Vertical(g1)
    c: Vertical(g3)
    c: Coincident(g4,g5)
    c: Coincident(g5,g6)
    c: Coincident(g6,g7)
    c: Coincident(g7,g4)
    c: Horizontal(g4)
    c: Horizontal(g6)
    c: Vertical(g5)
    c: Vertical(g7)
    c: Coincident(g8,g9)
    c: Coincident(g9,g10)
    c: Coincident(g10,g11)
    c: Coincident(g11,g8)
    c: Horizontal(g8)
    c: Horizontal(g10)
    c: Vertical(g9)
    c: Vertical(g11)
    c: DistanceY(g1,g1) = 610
    c: DistanceX(g0,g0) = 610
    c: DistanceX(g0,g4) = 25
    c: DistanceX(g6,g2) = 25
    c: DistanceX(g10,g6) = 25
    c: DistanceX(g5,g9) = 25
    c: DistanceY(g9,g5) = 50
    c: DistanceY(g5,g1) = 25
    c: DistanceY(g4,g8) = 50
    c: DistanceY(g0,g4) = 25
FEATURE [Sketcher::SketchObject] Sketch020
  Placement = pos=(13615.4,9930,1106.51) rot=(-1,0,0;1.5708rad)
  sketch-geometry (12):
    g0: LineSegment StartX=1874.58 StartY=-2013.49 StartZ=0 EndX=1264.58 EndY=-2013.49 EndZ=0
    g1: LineSegment StartX=1264.58 StartY=-2013.49 StartZ=0 EndX=1264.58 EndY=-1403.49 EndZ=0
    g2: LineSegment StartX=1264.58 StartY=-1403.49 StartZ=0 EndX=1874.58 EndY=-1403.49 EndZ=0
    g3: LineSegment StartX=1874.58 StartY=-1403.49 StartZ=0 EndX=1874.58 EndY=-2013.49 EndZ=0
    g4: LineSegment StartX=1849.58 StartY=-1988.49 StartZ=0 EndX=1289.58 EndY=-1988.49 EndZ=0
    g5: LineSegment StartX=1289.58 StartY=-1988.49 StartZ=0 EndX=1289.58 EndY=-1428.49 EndZ=0
    g6: LineSegment StartX=1289.58 StartY=-1428.49 StartZ=0 EndX=1849.58 EndY=-1428.49 EndZ=0
    g7: LineSegment StartX=1849.58 StartY=-1428.49 StartZ=0 EndX=1849.58 EndY=-1988.49 EndZ=0
    g8: LineSegment StartX=1824.58 StartY=-1938.49 StartZ=0 EndX=1314.58 EndY=-1938.49 EndZ=0
    g9: LineSegment StartX=1314.58 StartY=-1938.49 StartZ=0 EndX=1314.58 EndY=-1478.49 EndZ=0
    g10: LineSegment StartX=1314.58 StartY=-1478.49 StartZ=0 EndX=1824.58 EndY=-1478.49 EndZ=0
    g11: LineSegment StartX=1824.58 StartY=-1478.49 StartZ=0 EndX=1824.58 EndY=-1938.49 EndZ=0
  constraints (34):
    c: Coincident(g0,g1)
    c: Coincident(g1,g2)
    c: Coincident(g2,g3)
    c: Coincident(g3,g0)
    c: Horizontal(g0)
    c: Horizontal(g2)
    c: Vertical(g1)
    c: Vertical(g3)
    c: Coincident(g4,g5)
    c: Coincident(g5,g6)
    c: Coincident(g6,g7)
    c: Coincident(g7,g4)
    c: Horizontal(g4)
    c: Horizontal(g6)
    c: Vertical(g5)
    c: Vertical(g7)
    c: Coincident(g8,g9)
    c: Coincident(g9,g10)
    c: Coincident(g10,g11)
    c: Coincident(g11,g8)
    c: Horizontal(g8)
    c: Horizontal(g10)
    c: Vertical(g9)
    c: Vertical(g11)
    c: DistanceY(g1,g1) = 610
    c: DistanceX(g0,g0) = 610
    c: DistanceX(g0,g4) = 25
    c: DistanceX(g6,g2) = 25
    c: DistanceX(g10,g6) = 25
    c: DistanceX(g5,g9) = 25
    c: DistanceY(g9,g5) = 50
    c: DistanceY(g5,g1) = 25
    c: DistanceY(g4,g8) = 50
    c: DistanceY(g0,g4) = 25
FEATURE [Sketcher::SketchObject] Sketch022
  Placement = pos=(13615,9930,2435) rot=(0,0.707107,0.707107;3.14159rad)
  sketch-geometry (4):
    g0: LineSegment StartX=-1845 StartY=75 StartZ=0 EndX=-945 EndY=75 EndZ=0
    g1: LineSegment StartX=-945 StartY=75 StartZ=0 EndX=-945 EndY=-75 EndZ=0
    g2: LineSegment StartX=-945 StartY=-75 StartZ=0 EndX=-1845 EndY=-75 EndZ=0
    g3: LineSegment StartX=-1845 StartY=-75 StartZ=0 EndX=-1845 EndY=75 EndZ=0
  constraints (11):
    c: Coincident(g0,g1)
    c: Coincident(g1,g2)
    c: Coincident(g2,g3)
    c: Coincident(g3,g0)
    c: Horizontal(g0)
    c: Horizontal(g2)
    c: Vertical(g1)
    c: Vertical(g3)
    c: DistanceY(g1,g1) = 150
    c: DistanceY(g1,g-1) = 75
    c: DistanceX(g0,g0) = 900
FEATURE [Sketcher::SketchObject] Sketch023
  Placement = pos=(13615,9930,2435) rot=(0,0.707107,0.707107;3.14159rad)
  sketch-geometry (4):
    g0: LineSegment StartX=-1845 StartY=75 StartZ=0 EndX=-945 EndY=75 EndZ=0
    g1: LineSegment StartX=-945 StartY=75 StartZ=0 EndX=-945 EndY=-75 EndZ=0
    g2: LineSegment StartX=-945 StartY=-75 StartZ=0 EndX=-1845 EndY=-75 EndZ=0
    g3: LineSegment StartX=-1845 StartY=-75 StartZ=0 EndX=-1845 EndY=75 EndZ=0
  constraints (11):
    c: Coincident(g0,g1)
    c: Coincident(g1,g2)
    c: Coincident(g2,g3)
    c: Coincident(g3,g0)
    c: Horizontal(g0)
    c: Horizontal(g2)
    c: Vertical(g1)
    c: Vertical(g3)
    c: DistanceY(g1,g1) = 150
    c: DistanceY(g1,g-1) = 75
    c: DistanceX(g0,g0) = 900
FEATURE [Sketcher::SketchObject] WallTrace025
  Placement = pos=(150,2650,0) rot=(0,0,1;0rad)
  sketch-geometry (1):
    g0: LineSegment StartX=-150 StartY=-2350 StartZ=0 EndX=-150 EndY=2350 EndZ=0
FEATURE [Sketcher::SketchObject] Sketch029
  Placement = pos=(-5.71306,2645.54,1600) rot=(-0.576416,0.577817,0.577817;4.18739rad)
  sketch-geometry (4):
    g0: LineSegment StartX=-744.48 StartY=910 StartZ=0 EndX=1395.52 EndY=910 EndZ=0
    g1: LineSegment StartX=1395.52 StartY=910 StartZ=0 EndX=1395.52 EndY=760 EndZ=0
    g2: LineSegment StartX=1395.52 StartY=760 StartZ=0 EndX=-744.48 EndY=760 EndZ=0
    g3: LineSegment StartX=-744.48 StartY=760 StartZ=0 EndX=-744.48 EndY=910 EndZ=0
  constraints (10):
    c: Coincident(g0,g1)
    c: Coincident(g1,g2)
    c: Coincident(g2,g3)
    c: Coincident(g3,g0)
    c: Horizontal(g0)
    c: Horizontal(g2)
    c: Vertical(g1)
    c: Vertical(g3)
    c: DistanceY(g1,g1) = 150
    c: DistanceX(g0,g0) = 2140
FEATURE [Sketcher::SketchObject] Sketch030
  Placement = pos=(-5.71306,2645.54,1600) rot=(-0.576416,0.577817,0.577817;4.18739rad)
  sketch-geometry (20):
    g0: LineSegment StartX=-594.48 StartY=760 StartZ=0 EndX=1245.52 EndY=760 EndZ=0
    g1: LineSegment StartX=1245.52 StartY=760 StartZ=0 EndX=1245.52 EndY=-460 EndZ=0
    g2: LineSegment StartX=1245.52 StartY=-460 StartZ=0 EndX=-594.48 EndY=-460 EndZ=0
    g3: LineSegment StartX=-594.48 StartY=-460 StartZ=0 EndX=-594.48 EndY=760 EndZ=0
    g4: LineSegment StartX=-569.48 StartY=735 StartZ=0 EndX=1220.52 EndY=735 EndZ=0
    g5: LineSegment StartX=1220.52 StartY=735 StartZ=0 EndX=1220.52 EndY=-435 EndZ=0
    g6: LineSegment StartX=1220.52 StartY=-435 StartZ=0 EndX=-569.48 EndY=-435 EndZ=0
    g7: LineSegment StartX=-569.48 StartY=-435 StartZ=0 EndX=-569.48 EndY=735 EndZ=0
    g8: LineSegment StartX=-544.48 StartY=685 StartZ=0 EndX=-6.14714 EndY=685 EndZ=0
    g9: LineSegment StartX=-6.14714 StartY=685 StartZ=0 EndX=-6.14714 EndY=-385 EndZ=0
    g10: LineSegment StartX=-6.14714 StartY=-385 StartZ=0 EndX=-544.48 EndY=-385 EndZ=0
    g11: LineSegment StartX=-544.48 StartY=-385 StartZ=0 EndX=-544.48 EndY=685 EndZ=0
    g12: LineSegment StartX=43.8529 StartY=685 StartZ=0 EndX=582.186 EndY=685 EndZ=0
    g13: LineSegment StartX=582.186 StartY=685 StartZ=0 EndX=582.186 EndY=-385 EndZ=0
    g14: LineSegment StartX=582.186 StartY=-385 StartZ=0 EndX=43.8529 EndY=-385 EndZ=0
    g15: LineSegment StartX=43.8529 StartY=-385 StartZ=0 EndX=43.8529 EndY=685 EndZ=0
    g16: LineSegment StartX=632.186 StartY=685 StartZ=0 EndX=1170.52 EndY=685 EndZ=0
    g17: LineSegment StartX=1170.52 StartY=685 StartZ=0 EndX=1170.52 EndY=-385 EndZ=0
    g18: LineSegment StartX=1170.52 StartY=-385 StartZ=0 EndX=632.186 EndY=-385 EndZ=0
    g19: LineSegment StartX=632.186 StartY=-385 StartZ=0 EndX=632.186 EndY=685 EndZ=0
  constraints (58):
    c: Coincident(g0,g1)
    c: Coincident(g1,g2)
    c: Coincident(g2,g3)
    c: Coincident(g3,g0)
    c: Horizontal(g0)
    c: Horizontal(g2)
    c: Vertical(g1)
    c: Vertical(g3)
    c: DistanceY(g1,g1) = 1220
    c: DistanceX(g0,g0) = 1840
    c: Coincident(g4,g5)
    c: Coincident(g5,g6)
    c: Coincident(g6,g7)
    c: Coincident(g7,g4)
    c: Horizontal(g4)
    c: Horizontal(g6)
    c: Vertical(g5)
    c: Vertical(g7)
    c: Coincident(g8,g9)
    c: Coincident(g9,g10)
    c: Coincident(g10,g11)
    c: Coincident(g11,g8)
    c: Horizontal(g8)
    c: Horizontal(g10)
    c: Vertical(g9)
    c: Vertical(g11)
    c: Coincident(g12,g13)
    c: Coincident(g13,g14)
    c: Coincident(g14,g15)
    c: Coincident(g15,g12)
    c: Horizontal(g12)
    c: Horizontal(g14)
    c: Vertical(g13)
    c: Vertical(g15)
    c: Coincident(g16,g17)
    c: Coincident(g17,g18)
    c: Coincident(g18,g19)
    c: Coincident(g19,g16)
    c: Horizontal(g16)
    c: Horizontal(g18)
    c: Vertical(g17)
    c: Vertical(g19)
    c: DistanceY(g4,g0) = 25
    c: DistanceY(g16,g4) = 50
    c: DistanceY(g16,g12) = 0
    c: DistanceY(g12,g8) = 0
    c: DistanceY(g5,g17) = 50
    c: DistanceY(g1,g5) = 25
    c: Equal(g9,g15)
    c: Equal(g13,g19)
    c: Equal(g16,g12)
    c: Equal(g12,g8)
    c: DistanceX(g0,g4) = 25
    c: DistanceX(g4,g8) = 25
    c: DistanceX(g8,g12) = 50
    c: DistanceX(g12,g16) = 50
    c: DistanceX(g17,g5) = 50
    c: DistanceX(g5,g1) = 25
FEATURE [Sketcher::SketchObject] Sketch043
  Placement = pos=(8410,3650,2435) rot=(1,0,0;1.5708rad)
  expr: Constraints[2] = 5740
  expr: Constraints[3] = 2870
  sketch-geometry (1):
    g0: LineSegment StartX=-2870 StartY=75 StartZ=0 EndX=2870 EndY=75 EndZ=0
  constraints (4):
    c: Horizontal(g0)
    c: DistanceY(g-1,g0) = 75
    c: DistanceX(g0,g0) = 5740
    c: DistanceX(g0,g-1) = 2870
FEATURE [Sketcher::SketchObject] Sketch044
  Placement = pos=(8029.62,4959.98,3650) rot=(1,0,0;3.14159rad)
  sketch-geometry (8):
    g0: LineSegment StartX=-2719.62 StartY=1079.98 StartZ=0 EndX=3480.38 EndY=1079.98 EndZ=0
    g1: LineSegment StartX=3480.38 StartY=1079.98 StartZ=0 EndX=3480.38 EndY=4729.98 EndZ=0
    g2: LineSegment StartX=3480.38 StartY=4729.98 StartZ=0 EndX=7690.38 EndY=4729.98 EndZ=0
    g3: LineSegment StartX=7690.38 StartY=4729.98 StartZ=0 EndX=7690.38 EndY=-4740.02 EndZ=0
    g4: LineSegment StartX=7690.38 StartY=-4740.02 StartZ=0 EndX=-7799.62 EndY=-4740.02 EndZ=0
    g5: LineSegment StartX=-7799.62 StartY=-4740.02 StartZ=0 EndX=-7799.62 EndY=4729.98 EndZ=0
    g6: LineSegment StartX=-7799.62 StartY=4729.98 StartZ=0 EndX=-2719.62 EndY=4729.98 EndZ=0
    g7: LineSegment StartX=-2719.62 StartY=4729.98 StartZ=0 EndX=-2719.62 EndY=1079.98 EndZ=0
  constraints (8):
    c: Coincident(g0,g1)
    c: Coincident(g1,g2)
    c: Coincident(g2,g3)
    c: Coincident(g3,g4)
    c: Coincident(g4,g5)
    c: Coincident(g5,g6)
    c: Coincident(g6,g7)
    c: Coincident(g7,g0)
FEATURE [Sketcher::SketchObject] Sketch046
  Placement = pos=(8029.62,4959.98,3650) rot=(1,0,0;3.14159rad)
  sketch-geometry (8):
    g0: LineSegment StartX=-2719.62 StartY=1079.98 StartZ=0 EndX=3480.38 EndY=1079.98 EndZ=0
    g1: LineSegment StartX=3480.38 StartY=1079.98 StartZ=0 EndX=3480.38 EndY=4729.98 EndZ=0
    g2: LineSegment StartX=3480.38 StartY=4729.98 StartZ=0 EndX=7690.38 EndY=4729.98 EndZ=0
    g3: LineSegment StartX=7690.38 StartY=4729.98 StartZ=0 EndX=7690.38 EndY=-4740.02 EndZ=0
    g4: LineSegment StartX=7690.38 StartY=-4740.02 StartZ=0 EndX=-7799.62 EndY=-4740.02 EndZ=0
    g5: LineSegment StartX=-7799.62 StartY=-4740.02 StartZ=0 EndX=-7799.62 EndY=4729.98 EndZ=0
    g6: LineSegment StartX=-7799.62 StartY=4729.98 StartZ=0 EndX=-2719.62 EndY=4729.98 EndZ=0
    g7: LineSegment StartX=-2719.62 StartY=4729.98 StartZ=0 EndX=-2719.62 EndY=1079.98 EndZ=0
  constraints (8):
    c: Coincident(g0,g1)
    c: Coincident(g1,g2)
    c: Coincident(g2,g3)
    c: Coincident(g3,g4)
    c: Coincident(g4,g5)
    c: Coincident(g5,g6)
    c: Coincident(g6,g7)
    c: Coincident(g7,g0)
FEATURE [Sketcher::SketchObject] Sketch048
  Placement = pos=(8029.62,4959.98,3650) rot=(1,0,0;3.14159rad)
  sketch-geometry (8):
    g0: LineSegment StartX=-2719.62 StartY=1079.98 StartZ=0 EndX=3480.38 EndY=1079.98 EndZ=0
    g1: LineSegment StartX=3480.38 StartY=1079.98 StartZ=0 EndX=3480.38 EndY=4729.98 EndZ=0
    g2: LineSegment StartX=3480.38 StartY=4729.98 StartZ=0 EndX=7690.38 EndY=4729.98 EndZ=0
    g3: LineSegment StartX=7690.38 StartY=4729.98 StartZ=0 EndX=7690.38 EndY=-4740.02 EndZ=0
    g4: LineSegment StartX=7690.38 StartY=-4740.02 StartZ=0 EndX=-7799.62 EndY=-4740.02 EndZ=0
    g5: LineSegment StartX=-7799.62 StartY=-4740.02 StartZ=0 EndX=-7799.62 EndY=4729.98 EndZ=0
    g6: LineSegment StartX=-7799.62 StartY=4729.98 StartZ=0 EndX=-2719.62 EndY=4729.98 EndZ=0
    g7: LineSegment StartX=-2719.62 StartY=4729.98 StartZ=0 EndX=-2719.62 EndY=1079.98 EndZ=0
  constraints (8):
    c: Coincident(g0,g1)
    c: Coincident(g1,g2)
    c: Coincident(g2,g3)
    c: Coincident(g3,g4)
    c: Coincident(g4,g5)
    c: Coincident(g5,g6)
    c: Coincident(g6,g7)
    c: Coincident(g7,g0)
FEATURE [Sketcher::SketchObject] Sketch050
  Placement = pos=(150,7465,0) rot=(0,0,1;0rad)
  sketch-geometry (8):
    g0: LineSegment StartX=150 StartY=2165 StartZ=0 EndX=15500 EndY=2165 EndZ=0
    g1: LineSegment StartX=15500 StartY=2165 StartZ=0 EndX=15500 EndY=-7165 EndZ=0
    g2: LineSegment StartX=15500 StartY=-7165 StartZ=0 EndX=11430 EndY=-7165 EndZ=0
    g3: LineSegment StartX=11430 StartY=-7165 StartZ=0 EndX=11430 EndY=-3815 EndZ=0
    g4: LineSegment StartX=11430 StartY=-3815 StartZ=0 EndX=5090 EndY=-3815 EndZ=0
    g5: LineSegment StartX=5090 StartY=-3815 StartZ=0 EndX=5090 EndY=-7165 EndZ=0
    g6: LineSegment StartX=5090 StartY=-7165 StartZ=0 EndX=150 EndY=-7165 EndZ=0
    g7: LineSegment StartX=150 StartY=-7165 StartZ=0 EndX=150 EndY=2165 EndZ=0
  constraints (10):
    c: Coincident(g0,g1)
    c: Coincident(g1,g2)
    c: Coincident(g2,g3)
    c: Coincident(g3,g4)
    c: Coincident(g4,g5)
    c: Coincident(g5,g6)
    c: Coincident(g6,g7)
    c: Coincident(g7,g0)
    c: Horizontal(g4)
    c: Vertical(g5)
FEATURE [Sketcher::SketchObject] Sketch052
  ExternalGeometry = -> [Axis001]
  Placement = pos=(5540,2125,1180) rot=(0.57735,0.57735,0.57735;2.0944rad)
  sketch-geometry (3):
    g0: LineSegment StartX=-4475 StartY=-1630 StartZ=0 EndX=1525 EndY=-1630 EndZ=0
    g1: LineSegment StartX=1525 StartY=-1630 StartZ=0 EndX=1525 EndY=-1180 EndZ=0
    g2: LineSegment StartX=1525 StartY=-1180 StartZ=0 EndX=-4475 EndY=-1630 EndZ=0
  constraints (8):
    c: Horizontal(g0)
    c: Coincident(g0,g1)
    c: Vertical(g1)
    c: Coincident(g1,g2)
    c: Coincident(g2,g0)
    c: Coincident(g1,g-3)
    c: DistanceY(g1,g1) = 450
    c: DistanceX(g0,g0) = 6000
FEATURE [Sketcher::SketchObject] Sketch057
  Placement = pos=(5447.5,3592.5,100) rot=(0.57735,0.57735,0.57735;2.0944rad)
  sketch-geometry (8):
    g0: LineSegment StartX=-2e-16 StartY=0 StartZ=0 EndX=1000 EndY=0 EndZ=0
    g1: LineSegment StartX=1000 StartY=0 StartZ=0 EndX=1000 EndY=2000 EndZ=0
    g2: LineSegment StartX=1000 StartY=2000 StartZ=0 EndX=0 EndY=2000 EndZ=0
    g3: LineSegment StartX=-2e-16 StartY=2000 StartZ=0 EndX=-2e-16 EndY=0 EndZ=0
    g4: LineSegment StartX=50 StartY=0 StartZ=0 EndX=950 EndY=0 EndZ=0
    g5: LineSegment StartX=950 StartY=0 StartZ=0 EndX=950 EndY=1950 EndZ=0
    g6: LineSegment StartX=950 StartY=1950 StartZ=0 EndX=50 EndY=1950 EndZ=0
    g7: LineSegment StartX=50 StartY=1950 StartZ=0 EndX=50 EndY=0 EndZ=0
  constraints (23):
    c: Coincident(g0,g1)
    c: Coincident(g1,g2)
    c: Coincident(g2,g3)
    c: Coincident(g3,g0)
    c: Horizontal(g0)
    c: Horizontal(g2)
    c: Vertical(g1)
    c: Vertical(g3)
    c: Coincident(g4,g5)
    c: Coincident(g5,g6)
    c: Coincident(g6,g7)
    c: Coincident(g7,g4)
    c: Horizontal(g4)
    c: Horizontal(g6)
    c: Vertical(g5)
    c: Vertical(g7)
    c: DistanceY(g1) = 2000  'Height'
    c: DistanceX(g0) = 1000  'Width'
    c: DistanceY(g6,g2) = 50  'Frame1'
    c: DistanceX(g2,g6) = 50  'Frame2'
    c: DistanceX(g4,g0) = 50  'Frame3'
    c: DistanceY(g0,g4) = 0
    c: Coincident(g0,g-1)
FEATURE [Sketcher::SketchObject] Sketch058
  Placement = pos=(11487.5,3592.5,100) rot=(0.57735,0.57735,0.57735;2.0944rad)
  sketch-geometry (8):
    g0: LineSegment StartX=-2e-16 StartY=0 StartZ=0 EndX=1000 EndY=0 EndZ=0
    g1: LineSegment StartX=1000 StartY=0 StartZ=0 EndX=1000 EndY=2000 EndZ=0
    g2: LineSegment StartX=1000 StartY=2000 StartZ=0 EndX=0 EndY=2000 EndZ=0
    g3: LineSegment StartX=-2e-16 StartY=2000 StartZ=0 EndX=-2e-16 EndY=0 EndZ=0
    g4: LineSegment StartX=50 StartY=0 StartZ=0 EndX=950 EndY=0 EndZ=0
    g5: LineSegment StartX=950 StartY=0 StartZ=0 EndX=950 EndY=1950 EndZ=0
    g6: LineSegment StartX=950 StartY=1950 StartZ=0 EndX=50 EndY=1950 EndZ=0
    g7: LineSegment StartX=50 StartY=1950 StartZ=0 EndX=50 EndY=0 EndZ=0
  constraints (23):
    c: Coincident(g0,g1)
    c: Coincident(g1,g2)
    c: Coincident(g2,g3)
    c: Coincident(g3,g0)
    c: Horizontal(g0)
    c: Horizontal(g2)
    c: Vertical(g1)
    c: Vertical(g3)
    c: Coincident(g4,g5)
    c: Coincident(g5,g6)
    c: Coincident(g6,g7)
    c: Coincident(g7,g4)
    c: Horizontal(g4)
    c: Horizontal(g6)
    c: Vertical(g5)
    c: Vertical(g7)
    c: DistanceY(g1) = 2000  'Height'
    c: DistanceX(g0) = 1000  'Width'
    c: DistanceY(g6,g2) = 50  'Frame1'
    c: DistanceX(g2,g6) = 50  'Frame2'
    c: DistanceX(g4,g0) = 50  'Frame3'
    c: DistanceY(g0,g4) = 0
    c: Coincident(g0,g-1)
FEATURE [Sketcher::SketchObject] Sketch061
  Placement = pos=(5540,5092.5,50) rot=(1,0,0;1.5708rad)
  sketch-geometry (8):
    g0: LineSegment StartX=9e-16 StartY=0 StartZ=0 EndX=1500 EndY=0 EndZ=0
    g1: LineSegment StartX=1500 StartY=0 StartZ=0 EndX=1500 EndY=2000 EndZ=0
    g2: LineSegment StartX=1500 StartY=2000 StartZ=0 EndX=0 EndY=2000 EndZ=0
    g3: LineSegment StartX=9e-16 StartY=2000 StartZ=0 EndX=9e-16 EndY=0 EndZ=0
    g4: LineSegment StartX=50 StartY=-5e-16 StartZ=0 EndX=1450 EndY=-5e-16 EndZ=0
    g5: LineSegment StartX=1450 StartY=-5e-16 StartZ=0 EndX=1450 EndY=1950 EndZ=0
    g6: LineSegment StartX=1450 StartY=1950 StartZ=0 EndX=50 EndY=1950 EndZ=0
    g7: LineSegment StartX=50 StartY=1950 StartZ=0 EndX=50 EndY=0 EndZ=0
  constraints (23):
    c: Coincident(g0,g1)
    c: Coincident(g1,g2)
    c: Coincident(g2,g3)
    c: Coincident(g3,g0)
    c: Horizontal(g0)
    c: Horizontal(g2)
    c: Vertical(g1)
    c: Vertical(g3)
    c: Coincident(g4,g5)
    c: Coincident(g5,g6)
    c: Coincident(g6,g7)
    c: Coincident(g7,g4)
    c: Horizontal(g4)
    c: Horizontal(g6)
    c: Vertical(g5)
    c: Vertical(g7)
    c: DistanceY(g1) = 2000  'Height'
    c: DistanceX(g0) = 1500  'Width'
    c: DistanceY(g6,g2) = 50  'Frame1'
    c: DistanceX(g2,g6) = 50  'Frame2'
    c: DistanceX(g4,g0) = 50  'Frame3'
    c: DistanceY(g0,g4) = 0
    c: Coincident(g0,g-1)
FEATURE [Sketcher::SketchObject] Sketch062
  Placement = pos=(11280,5092.5,50) rot=(1,0,0;1.5708rad)
  sketch-geometry (8):
    g0: LineSegment StartX=7e-16 StartY=0 StartZ=0 EndX=1500 EndY=0 EndZ=0
    g1: LineSegment StartX=1500 StartY=0 StartZ=0 EndX=1500 EndY=2000 EndZ=0
    g2: LineSegment StartX=1500 StartY=2000 StartZ=0 EndX=0 EndY=2000 EndZ=0
    g3: LineSegment StartX=7e-16 StartY=2000 StartZ=0 EndX=7e-16 EndY=0 EndZ=0
    g4: LineSegment StartX=50 StartY=0 StartZ=0 EndX=1450 EndY=0 EndZ=0
    g5: LineSegment StartX=1450 StartY=0 StartZ=0 EndX=1450 EndY=1950 EndZ=0
    g6: LineSegment StartX=1450 StartY=1950 StartZ=0 EndX=50 EndY=1950 EndZ=0
    g7: LineSegment StartX=50 StartY=1950 StartZ=0 EndX=50 EndY=0 EndZ=0
  constraints (23):
    c: Coincident(g0,g1)
    c: Coincident(g1,g2)
    c: Coincident(g2,g3)
    c: Coincident(g3,g0)
    c: Horizontal(g0)
    c: Horizontal(g2)
    c: Vertical(g1)
    c: Vertical(g3)
    c: Coincident(g4,g5)
    c: Coincident(g5,g6)
    c: Coincident(g6,g7)
    c: Coincident(g7,g4)
    c: Horizontal(g4)
    c: Horizontal(g6)
    c: Vertical(g5)
    c: Vertical(g7)
    c: DistanceY(g1) = 2000  'Height'
    c: DistanceX(g0) = 1500  'Width'
    c: DistanceY(g6,g2) = 50  'Frame1'
    c: DistanceX(g2,g6) = 50  'Frame2'
    c: DistanceX(g4,g0) = 50  'Frame3'
    c: DistanceY(g0,g4) = 0
    c: Coincident(g0,g-1)
FEATURE [Sketcher::SketchObject] Sketch063
  Placement = pos=(11430,8280,50) rot=(1,0,0;1.5708rad)
  sketch-geometry (8):
    g0: LineSegment StartX=7e-16 StartY=0 StartZ=0 EndX=1000 EndY=0 EndZ=0
    g1: LineSegment StartX=1000 StartY=0 StartZ=0 EndX=1000 EndY=2000 EndZ=0
    g2: LineSegment StartX=1000 StartY=2000 StartZ=0 EndX=0 EndY=2000 EndZ=0
    g3: LineSegment StartX=7e-16 StartY=2000 StartZ=0 EndX=7e-16 EndY=0 EndZ=0
    g4: LineSegment StartX=50 StartY=0 StartZ=0 EndX=950 EndY=0 EndZ=0
    g5: LineSegment StartX=950 StartY=0 StartZ=0 EndX=950 EndY=1950 EndZ=0
    g6: LineSegment StartX=950 StartY=1950 StartZ=0 EndX=50 EndY=1950 EndZ=0
    g7: LineSegment StartX=50 StartY=1950 StartZ=0 EndX=50 EndY=0 EndZ=0
  constraints (23):
    c: Coincident(g0,g1)
    c: Coincident(g1,g2)
    c: Coincident(g2,g3)
    c: Coincident(g3,g0)
    c: Horizontal(g0)
    c: Horizontal(g2)
    c: Vertical(g1)
    c: Vertical(g3)
    c: Coincident(g4,g5)
    c: Coincident(g5,g6)
    c: Coincident(g6,g7)
    c: Coincident(g7,g4)
    c: Horizontal(g4)
    c: Horizontal(g6)
    c: Vertical(g5)
    c: Vertical(g7)
    c: DistanceY(g1) = 2000  'Height'
    c: DistanceX(g0) = 1000  'Width'
    c: DistanceY(g6,g2) = 50  'Frame1'
    c: DistanceX(g2,g6) = 50  'Frame2'
    c: DistanceX(g4,g0) = 50  'Frame3'
    c: DistanceY(g0,g4) = 0
    c: Coincident(g0,g-1)
FEATURE [Sketcher::SketchObject] Sketch067
  Placement = pos=(11430,8280,50) rot=(1,0,0;1.5708rad)
  sketch-geometry (8):
    g0: LineSegment StartX=0 StartY=0 StartZ=0 EndX=1000 EndY=0 EndZ=0
    g1: LineSegment StartX=1000 StartY=0 StartZ=0 EndX=1000 EndY=2000 EndZ=0
    g2: LineSegment StartX=1000 StartY=2000 StartZ=0 EndX=0 EndY=2000 EndZ=0
    g3: LineSegment StartX=0 StartY=2000 StartZ=0 EndX=0 EndY=0 EndZ=0
    g4: LineSegment StartX=50 StartY=0 StartZ=0 EndX=950 EndY=0 EndZ=0
    g5: LineSegment StartX=950 StartY=0 StartZ=0 EndX=950 EndY=1950 EndZ=0
    g6: LineSegment StartX=950 StartY=1950 StartZ=0 EndX=50 EndY=1950 EndZ=0
    g7: LineSegment StartX=50 StartY=1950 StartZ=0 EndX=50 EndY=0 EndZ=0
  constraints (23):
    c: Coincident(g0,g1)
    c: Coincident(g1,g2)
    c: Coincident(g2,g3)
    c: Coincident(g3,g0)
    c: Horizontal(g0)
    c: Horizontal(g2)
    c: Vertical(g1)
    c: Vertical(g3)
    c: Coincident(g4,g5)
    c: Coincident(g5,g6)
    c: Coincident(g6,g7)
    c: Coincident(g7,g4)
    c: Horizontal(g4)
    c: Horizontal(g6)
    c: Vertical(g5)
    c: Vertical(g7)
    c: DistanceY(g1) = 2000  'Height'
    c: DistanceX(g0) = 1000  'Width'
    c: DistanceY(g6,g2) = 50  'Frame1'
    c: DistanceX(g2,g6) = 50  'Frame2'
    c: DistanceX(g4,g0) = 50  'Frame3'
    c: DistanceY(g0,g4) = 0
    c: Coincident(g0,g-1)
FEATURE [Sketcher::SketchObject] Sketch068
  Placement = pos=(8440,9780,50) rot=(0.57735,-0.57735,-0.57735;2.0944rad)
  sketch-geometry (8):
    g0: LineSegment StartX=0 StartY=0 StartZ=0 EndX=1000 EndY=0 EndZ=0
    g1: LineSegment StartX=1000 StartY=0 StartZ=0 EndX=1000 EndY=2000 EndZ=0
    g2: LineSegment StartX=1000 StartY=2000 StartZ=0 EndX=0 EndY=2000 EndZ=0
    g3: LineSegment StartX=0 StartY=2000 StartZ=0 EndX=0 EndY=0 EndZ=0
    g4: LineSegment StartX=50 StartY=0 StartZ=0 EndX=950 EndY=0 EndZ=0
    g5: LineSegment StartX=950 StartY=0 StartZ=0 EndX=950 EndY=1950 EndZ=0
    g6: LineSegment StartX=950 StartY=1950 StartZ=0 EndX=50 EndY=1950 EndZ=0
    g7: LineSegment StartX=50 StartY=1950 StartZ=0 EndX=50 EndY=0 EndZ=0
  constraints (23):
    c: Coincident(g0,g1)
    c: Coincident(g1,g2)
    c: Coincident(g2,g3)
    c: Coincident(g3,g0)
    c: Horizontal(g0)
    c: Horizontal(g2)
    c: Vertical(g1)
    c: Vertical(g3)
    c: Coincident(g4,g5)
    c: Coincident(g5,g6)
    c: Coincident(g6,g7)
    c: Coincident(g7,g4)
    c: Horizontal(g4)
    c: Horizontal(g6)
    c: Vertical(g5)
    c: Vertical(g7)
    c: DistanceY(g1) = 2000  'Height'
    c: DistanceX(g0) = 1000  'Width'
    c: DistanceY(g6,g2) = 50  'Frame1'
    c: DistanceX(g2,g6) = 50  'Frame2'
    c: DistanceX(g4,g0) = 50  'Frame3'
    c: DistanceY(g0,g4) = 0
    c: Coincident(g0,g-1)
FEATURE [Sketcher::SketchObject] Sketch071
  Placement = pos=(150,7465,50) rot=(1,0,0;1.5708rad)
  sketch-geometry (8):
    g0: LineSegment StartX=0 StartY=0 StartZ=0 EndX=1000 EndY=0 EndZ=0
    g1: LineSegment StartX=1000 StartY=0 StartZ=0 EndX=1000 EndY=2000 EndZ=0
    g2: LineSegment StartX=1000 StartY=2000 StartZ=0 EndX=0 EndY=2000 EndZ=0
    g3: LineSegment StartX=0 StartY=2000 StartZ=0 EndX=0 EndY=0 EndZ=0
    g4: LineSegment StartX=50 StartY=0 StartZ=0 EndX=950 EndY=0 EndZ=0
    g5: LineSegment StartX=950 StartY=0 StartZ=0 EndX=950 EndY=1950 EndZ=0
    g6: LineSegment StartX=950 StartY=1950 StartZ=0 EndX=50 EndY=1950 EndZ=0
    g7: LineSegment StartX=50 StartY=1950 StartZ=0 EndX=50 EndY=0 EndZ=0
  constraints (23):
    c: Coincident(g0,g1)
    c: Coincident(g1,g2)
    c: Coincident(g2,g3)
    c: Coincident(g3,g0)
    c: Horizontal(g0)
    c: Horizontal(g2)
    c: Vertical(g1)
    c: Vertical(g3)
    c: Coincident(g4,g5)
    c: Coincident(g5,g6)
    c: Coincident(g6,g7)
    c: Coincident(g7,g4)
    c: Horizontal(g4)
    c: Horizontal(g6)
    c: Vertical(g5)
    c: Vertical(g7)
    c: DistanceY(g1) = 2000  'Height'
    c: DistanceX(g0) = 1000  'Width'
    c: DistanceY(g6,g2) = 50  'Frame1'
    c: DistanceX(g2,g6) = 50  'Frame2'
    c: DistanceX(g4,g0) = 50  'Frame3'
    c: DistanceY(g0,g4) = 0
    c: Coincident(g0,g-1)
FEATURE [App::MaterialObjectPython] Material  label="Concrete"  # material (typed FeaturePython)
  Description = M25
  Material = AuthorAndLicense=Concrete-Generic,CardName=Concrete-Generic,Color=(0.5137254901960784, 0.5137254901960784, 0.5137254901960784),+12 more (map truncated)
  ProductURL = https://en.wikipedia.org/wiki/Concrete
  StandardCode = IS 456
  Transparency = 0
FEATURE [Part::FeaturePython] Structure  label="C001"  # Arch/BIM 24 (typed FeaturePython)
  FaceMaker = 0
  Height = 5000
  HorizontalArea = 90000
  IfcData = IfcUID=1m_X0nFnDFh8hDn94Hsyc5,+2 more (map truncated)
  IfcType = 24
  Length = 300
  Material = -> Material
  MoveBase = false
  MoveWithHost = false
  Nodes = (2) [(5.55112e-16,1.51582e-15,0),(5.55112e-16,1.51582e-15,5000)]
  NodesOffset = 0
  Normal = (0,0,0)
  PerimeterLength = 1200
  Placement = pos=(150,150,-1500) rot=(0,0,1;0rad)
  PredefinedType = 0
  Tag = MainColumn
  VerticalArea = 6000000
  Width = 300
FEATURE [Part::FeaturePython] Structure002  label="C003"  # Arch/BIM 24 (typed FeaturePython)
  FaceMaker = 0
  Height = 5000
  HorizontalArea = 90000
  IfcData = IfcUID=3w7QIDLsb3bxg5wlayDCsQ,+2 more (map truncated)
  IfcType = 24
  Length = 300
  Material = -> Material
  MoveBase = false
  MoveWithHost = false
  Nodes = (2) [(5.55112e-16,1.51582e-15,0),(5.55112e-16,1.51582e-15,5000)]
  NodesOffset = 0
  Normal = (0,0,0)
  PerimeterLength = 1200
  Placement = pos=(11430,150,-1500) rot=(0,0,1;0rad)
  PredefinedType = 0
  Tag = MainColumn
  VerticalArea = 6000000
  Width = 300
FEATURE [Part::FeaturePython] Structure003  label="C004"  # Arch/BIM 24 (typed FeaturePython)
  FaceMaker = 0
  Height = 5000
  HorizontalArea = 90000
  IfcData = IfcUID=3lkIpvjITA5eDn9n7jCXE$,+2 more (map truncated)
  IfcType = 24
  Length = 300
  Material = -> Material
  MoveBase = false
  MoveWithHost = false
  Nodes = (2) [(5.55112e-16,1.51582e-15,0),(5.55112e-16,1.51582e-15,5000)]
  NodesOffset = 0
  Normal = (0,0,0)
  PerimeterLength = 1200
  Placement = pos=(15800,150,-1500) rot=(0,0,1;0rad)
  PredefinedType = 0
  Tag = MainColumn
  VerticalArea = 6000000
  Width = 300
FEATURE [Part::FeaturePython] Structure004  label="C005"  # Arch/BIM 24 (typed FeaturePython)
  FaceMaker = 0
  Height = 5000
  HorizontalArea = 90000
  IfcData = IfcUID=0fNj7OO3X7FeWjxRgEZT8p,+2 more (map truncated)
  IfcType = 24
  Length = 300
  Material = -> Material
  MoveBase = false
  MoveWithHost = false
  Nodes = (2) [(5.55112e-16,1.51582e-15,0),(5.55112e-16,1.51582e-15,5000)]
  NodesOffset = 0
  Normal = (0,0,0)
  PerimeterLength = 1200
  Placement = pos=(150,5150,-1500) rot=(0,0,1;0rad)
  PredefinedType = 0
  Tag = MainColumn
  VerticalArea = 6000000
  Width = 300
FEATURE [Part::FeaturePython] Structure005  label="C006"  # Arch/BIM 24 (typed FeaturePython)
  FaceMaker = 0
  Height = 5000
  HorizontalArea = 90000
  IfcData = IfcUID=0e1xj0fk522gAtdobQW9WU,+2 more (map truncated)
  IfcType = 24
  Length = 300
  Material = -> Material
  MoveBase = false
  MoveWithHost = false
  Nodes = (2) [(5.55112e-16,1.51582e-15,0),(5.55112e-16,1.51582e-15,5000)]
  NodesOffset = 0
  Normal = (0,0,0)
  PerimeterLength = 1200
  Placement = pos=(5390,5150,-1500) rot=(0,0,1;0rad)
  PredefinedType = 0
  Tag = MainColumn
  VerticalArea = 6000000
  Width = 300
FEATURE [Part::FeaturePython] Structure006  label="C007"  # Arch/BIM 24 (typed FeaturePython)
  FaceMaker = 0
  Height = 5000
  HorizontalArea = 90000
  IfcData = IfcUID=0vmOcy6Lb3MR$eWdCddtfJ,+2 more (map truncated)
  IfcType = 24
  Length = 300
  Material = -> Material
  MoveBase = false
  MoveWithHost = false
  Nodes = (2) [(5.55112e-16,1.51582e-15,0),(5.55112e-16,1.51582e-15,5000)]
  NodesOffset = 0
  Normal = (0,0,0)
  PerimeterLength = 1200
  Placement = pos=(11430,5150,-1500) rot=(0,0,1;0rad)
  PredefinedType = 0
  Tag = MainColumn
  VerticalArea = 6000000
  Width = 300
FEATURE [Part::FeaturePython] Structure007  label="C008"  # Arch/BIM 24 (typed FeaturePython)
  FaceMaker = 0
  Height = 5000
  HorizontalArea = 90000
  IfcData = IfcUID=087WrWsTv19OWhBUrYYNzf,+2 more (map truncated)
  IfcType = 24
  Length = 300
  Material = -> Material
  MoveBase = false
  MoveWithHost = false
  Nodes = (2) [(5.55112e-16,1.51582e-15,0),(5.55112e-16,1.51582e-15,5000)]
  NodesOffset = 0
  Normal = (0,0,0)
  PerimeterLength = 1200
  Placement = pos=(15800,5150,-1500) rot=(0,0,1;0rad)
  PredefinedType = 0
  Tag = MainColumn
  VerticalArea = 6000000
  Width = 300
FEATURE [Part::FeaturePython] Structure008  label="C009"  # Arch/BIM 24 (typed FeaturePython)
  FaceMaker = 0
  Height = 5000
  HorizontalArea = 90000
  IfcData = IfcUID=2ixL7psnH8bOQLPPMpQV2L,+2 more (map truncated)
  IfcType = 24
  Length = 300
  Material = -> Material
  MoveBase = false
  MoveWithHost = false
  Nodes = (2) [(5.55112e-16,1.51582e-15,0),(5.55112e-16,1.51582e-15,5000)]
  NodesOffset = 0
  Normal = (0,0,0)
  PerimeterLength = 1200
  Placement = pos=(150,9780,-1500) rot=(0,0,1;0rad)
  PredefinedType = 0
  Tag = MainColumn
  VerticalArea = 6000000
  Width = 300
FEATURE [Part::FeaturePython] Structure009  label="C010"  # Arch/BIM 24 (typed FeaturePython)
  FaceMaker = 0
  Height = 5000
  HorizontalArea = 90000
  IfcData = IfcUID=19FEiLFFzCWwFLdoHSNORm,+2 more (map truncated)
  IfcType = 24
  Length = 300
  Material = -> Material
  MoveBase = false
  MoveWithHost = false
  Nodes = (2) [(5.55112e-16,1.51582e-15,0),(5.55112e-16,1.51582e-15,5000)]
  NodesOffset = 0
  Normal = (0,0,0)
  PerimeterLength = 1200
  Placement = pos=(5390,9780,-1500) rot=(0,0,1;0rad)
  PredefinedType = 0
  Tag = MainColumn
  VerticalArea = 6000000
  Width = 300
FEATURE [Part::FeaturePython] Structure010  label="C011"  # Arch/BIM 24 (typed FeaturePython)
  FaceMaker = 0
  Height = 5000
  HorizontalArea = 90000
  IfcData = IfcUID=1sU7xLurvC$wLmqRnOk3OG,+2 more (map truncated)
  IfcType = 24
  Length = 300
  Material = -> Material
  MoveBase = false
  MoveWithHost = false
  Nodes = (2) [(5.55112e-16,1.51582e-15,0),(5.55112e-16,1.51582e-15,5000)]
  NodesOffset = 0
  Normal = (0,0,0)
  PerimeterLength = 1200
  Placement = pos=(11430,9780,-1500) rot=(0,0,1;0rad)
  PredefinedType = 0
  Tag = MainColumn
  VerticalArea = 6000000
  Width = 300
FEATURE [Part::FeaturePython] Structure011  label="C012"  # Arch/BIM 24 (typed FeaturePython)
  FaceMaker = 0
  Height = 5000
  HorizontalArea = 90000
  IfcData = IfcUID=2OUNty8YH088kKsCNHqGBU,+2 more (map truncated)
  IfcType = 24
  Length = 300
  Material = -> Material
  MoveBase = false
  MoveWithHost = false
  Nodes = (2) [(5.55112e-16,1.51582e-15,0),(5.55112e-16,1.51582e-15,5000)]
  NodesOffset = 0
  Normal = (0,0,0)
  PerimeterLength = 1200
  Placement = pos=(15800,9780,-1500) rot=(0,0,1;0rad)
  PredefinedType = 0
  Tag = MainColumn
  VerticalArea = 6000000
  Width = 300
FEATURE [Part::FeaturePython] Structure012  label="B001"  # Arch/BIM 7 (typed FeaturePython)
  FaceMaker = 0
  Height = 450
  HorizontalArea = 1.482e+06
  IfcData = IfcUID=1qs2AddGDDi81Uv3uIkJ$M,+2 more (map truncated)
  IfcType = 7
  Length = 4940
  Material = -> Material
  MoveBase = false
  MoveWithHost = false
  Nodes = (2) [(-4.93038e-32,0,-2.22045e-16),(-4.93038e-32,0,4940)]
  NodesOffset = 0
  Normal = (0,0,0)
  PerimeterLength = 10480
  Placement = pos=(300,150,-225) rot=(0,0,1;0rad)
  PredefinedType = 0
  Tag = PlinthBeam
  VerticalArea = 4716000
  Width = 300
FEATURE [Part::FeaturePython] Structure013  label="B002"  # Arch/BIM 7 (typed FeaturePython)
  FaceMaker = 0
  Height = 450
  HorizontalArea = 1.41e+06
  IfcData = IfcUID=1MIi1yvLr8D86B_OSU4zFz,+2 more (map truncated)
  IfcType = 7
  Length = 4700
  Material = -> Material
  MoveBase = false
  MoveWithHost = false
  Nodes = (2) [(-4.93038e-32,0,-2.22045e-16),(-4.93038e-32,0,4700)]
  NodesOffset = 0
  Normal = (0,0,0)
  PerimeterLength = 10000
  Placement = pos=(150,300,-225) rot=(0,0,1;1.5708rad)
  PredefinedType = 0
  Tag = PlinthBeam
  VerticalArea = 4500000
  Width = 300
FEATURE [Part::FeaturePython] Structure014  label="B003"  # Arch/BIM 7 (typed FeaturePython)
  FaceMaker = 0
  Height = 450
  HorizontalArea = 1.299e+06
  IfcData = IfcUID=0QDjfnwT56Buk59xA7narx,+2 more (map truncated)
  IfcType = 7
  Length = 4330
  Material = -> Material
  MoveBase = false
  MoveWithHost = false
  Nodes = (2) [(-4.93038e-32,0,-2.22045e-16),(-4.93038e-32,0,4330)]
  NodesOffset = 0
  Normal = (0,0,0)
  PerimeterLength = 9260
  Placement = pos=(150,5300,-225) rot=(0,0,1;1.5708rad)
  PredefinedType = 0
  Tag = PlinthBeam
  VerticalArea = 4.167e+06
  Width = 300
FEATURE [Part::FeaturePython] Structure015  label="B004"  # Arch/BIM 7 (typed FeaturePython)
  FaceMaker = 0
  Height = 450
  HorizontalArea = 1.482e+06
  IfcData = IfcUID=1zzSxlcRnFzxLAy4e0VxbR,+2 more (map truncated)
  IfcType = 7
  Length = 4940
  Material = -> Material
  MoveBase = false
  MoveWithHost = false
  Nodes = (2) [(-4.93038e-32,0,-2.22045e-16),(-4.93038e-32,0,4940)]
  NodesOffset = 0
  Normal = (0,0,0)
  PerimeterLength = 10480
  Placement = pos=(300,9780,-225) rot=(0,0,1;0rad)
  PredefinedType = 0
  Tag = PlinthBeam
  VerticalArea = 4716000
  Width = 300
FEATURE [Part::FeaturePython] Structure016  label="B005"  # Arch/BIM 7 (typed FeaturePython)
  FaceMaker = 0
  Height = 450
  HorizontalArea = 1.722e+06
  IfcData = IfcUID=2kcY64zRL8tOhsehlhSt3$,+2 more (map truncated)
  IfcType = 7
  Length = 5740
  Material = -> Material
  MoveBase = false
  MoveWithHost = false
  Nodes = (2) [(-4.93038e-32,0,-2.22045e-16),(-4.93038e-32,0,5740)]
  NodesOffset = 0
  Normal = (0,0,0)
  PerimeterLength = 12080
  Placement = pos=(5540,9780,-225) rot=(0,0,1;0rad)
  PredefinedType = 0
  Tag = PlinthBeam
  VerticalArea = 5.436e+06
  Width = 300
FEATURE [Part::FeaturePython] Structure017  label="B006"  # Arch/BIM 7 (typed FeaturePython)
  FaceMaker = 0
  Height = 450
  HorizontalArea = 1.221e+06
  IfcData = IfcUID=0DFc_b7Qz9veay2Hi60C9S,+2 more (map truncated)
  IfcType = 7
  Length = 4070
  Material = -> Material
  MoveBase = false
  MoveWithHost = false
  Nodes = (2) [(-4.93038e-32,0,-2.22045e-16),(-4.93038e-32,0,4070)]
  NodesOffset = 0
  Normal = (0,0,0)
  PerimeterLength = 8740
  Placement = pos=(11580,9780,-225) rot=(0,0,1;0rad)
  PredefinedType = 0
  Tag = PlinthBeam
  VerticalArea = 3.933e+06
  Width = 300
FEATURE [Part::FeaturePython] Structure018  label="B007"  # Arch/BIM 7 (typed FeaturePython)
  FaceMaker = 0
  Height = 450
  HorizontalArea = 1.299e+06
  IfcData = IfcUID=3G$EjQTKfDDv5lsCjURFez,+2 more (map truncated)
  IfcType = 7
  Length = 4330
  Material = -> Material
  MoveBase = false
  MoveWithHost = false
  Nodes = (2) [(-4.93038e-32,0,-2.22045e-16),(-4.93038e-32,0,4330)]
  NodesOffset = 0
  Normal = (0,0,0)
  PerimeterLength = 9260
  Placement = pos=(15800,9630,-225) rot=(0,0,-1;1.5708rad)
  PredefinedType = 0
  Tag = PlinthBeam
  VerticalArea = 4.167e+06
  Width = 300
FEATURE [Part::FeaturePython] Structure019  label="B008"  # Arch/BIM 7 (typed FeaturePython)
  FaceMaker = 0
  Height = 450
  HorizontalArea = 1.41e+06
  IfcData = IfcUID=3NUbyKniPE7Q$iR7$t5lXc,+2 more (map truncated)
  IfcType = 7
  Length = 4700
  Material = -> Material
  MoveBase = false
  MoveWithHost = false
  Nodes = (2) [(-4.93038e-32,0,-2.22045e-16),(-4.93038e-32,0,4700)]
  NodesOffset = 0
  Normal = (0,0,0)
  PerimeterLength = 10000
  Placement = pos=(15800,5000,-225) rot=(0,0,-1;1.5708rad)
  PredefinedType = 0
  Tag = PlinthBeam
  VerticalArea = 4500000
  Width = 300
FEATURE [Part::FeaturePython] Structure020  label="B009"  # Arch/BIM 7 (typed FeaturePython)
  FaceMaker = 0
  Height = 450
  HorizontalArea = 1.221e+06
  IfcData = IfcUID=0j3QRqLE12vRaNSgcwHSKg,+2 more (map truncated)
  IfcType = 7
  Length = 4070
  Material = -> Material
  MoveBase = false
  MoveWithHost = false
  Nodes = (2) [(-4.93038e-32,0,-2.22045e-16),(-4.93038e-32,0,4070)]
  NodesOffset = 0
  Normal = (0,0,0)
  PerimeterLength = 8740
  Placement = pos=(15650,150,-225) rot=(0,0,1;3.14159rad)
  PredefinedType = 0
  Tag = PlinthBeam
  VerticalArea = 3.933e+06
  Width = 300
FEATURE [Part::FeaturePython] Structure021  label="B010"  # Arch/BIM 7 (typed FeaturePython)
  FaceMaker = 0
  Height = 450
  HorizontalArea = 1.41e+06
  IfcData = IfcUID=0eo3ECMEz4yOnEn2LJYkmH,+2 more (map truncated)
  IfcType = 7
  Length = 4700
  Material = -> Material
  MoveBase = false
  MoveWithHost = false
  Nodes = (2) [(-4.93038e-32,0,-2.22045e-16),(-4.93038e-32,0,4700)]
  NodesOffset = 0
  Normal = (0,0,0)
  PerimeterLength = 10000
  Placement = pos=(11430,300,-225) rot=(0,0,1;1.5708rad)
  PredefinedType = 0
  Tag = PlinthBeam
  VerticalArea = 4500000
  Width = 300
FEATURE [Part::FeaturePython] Structure022  label="B011"  # Arch/BIM 7 (typed FeaturePython)
  FaceMaker = 0
  Height = 450
  HorizontalArea = 1.41e+06
  IfcData = IfcUID=1dj5_9RyLCWxh7UwfjgK2G,+2 more (map truncated)
  IfcType = 7
  Length = 4700
  Material = -> Material
  MoveBase = false
  MoveWithHost = false
  Nodes = (2) [(-4.93038e-32,0,-2.22045e-16),(-4.93038e-32,0,4700)]
  NodesOffset = 0
  Normal = (0,0,0)
  PerimeterLength = 10000
  Placement = pos=(5390,300,-225) rot=(0,0,1;1.5708rad)
  PredefinedType = 0
  Tag = PlinthBeam
  VerticalArea = 4500000
  Width = 300
FEATURE [Part::FeaturePython] Structure024  label="B013"  # Arch/BIM 7 (typed FeaturePython)
  FaceMaker = 0
  Height = 450
  HorizontalArea = 1.482e+06
  IfcData = IfcUID=2riZ2vtyL6GxfEjAGlC8Sx,+2 more (map truncated)
  IfcType = 7
  Length = 4940
  Material = -> Material
  MoveBase = false
  MoveWithHost = false
  Nodes = (2) [(-4.93038e-32,0,-2.22045e-16),(-4.93038e-32,0,4940)]
  NodesOffset = 0
  Normal = (0,0,0)
  PerimeterLength = 10480
  Placement = pos=(300,5150,-225) rot=(0,0,1;0rad)
  PredefinedType = 0
  Tag = PlinthBeam
  VerticalArea = 4716000
  Width = 300
FEATURE [Part::FeaturePython] Structure025  label="B014"  # Arch/BIM 7 (typed FeaturePython)
  FaceMaker = 0
  Height = 450
  HorizontalArea = 1.299e+06
  IfcData = IfcUID=1EYFQhewf5qPdCEF2yUPTq,+2 more (map truncated)
  IfcType = 7
  Length = 4330
  Material = -> Material
  MoveBase = false
  MoveWithHost = false
  Nodes = (2) [(-4.93038e-32,0,-2.22045e-16),(-4.93038e-32,0,4330)]
  NodesOffset = 0
  Normal = (0,0,0)
  PerimeterLength = 9260
  Placement = pos=(5390,9630,-225) rot=(0,0,-1;1.5708rad)
  PredefinedType = 0
  Tag = PlinthBeam
  VerticalArea = 4.167e+06
  Width = 300
FEATURE [Part::FeaturePython] Structure026  label="B015"  # Arch/BIM 7 (typed FeaturePython)
  FaceMaker = 0
  Height = 450
  HorizontalArea = 1.299e+06
  IfcData = IfcUID=1zVd09HBv2UuaciIbFChvD,+2 more (map truncated)
  IfcType = 7
  Length = 4330
  Material = -> Material
  MoveBase = false
  MoveWithHost = false
  Nodes = (2) [(-4.93038e-32,0,-2.22045e-16),(-4.93038e-32,0,4330)]
  NodesOffset = 0
  Normal = (0,0,0)
  PerimeterLength = 9260
  Placement = pos=(11430,9630,-225) rot=(0,0,-1;1.5708rad)
  PredefinedType = 0
  Tag = PlinthBeam
  VerticalArea = 4.167e+06
  Width = 300
FEATURE [Part::FeaturePython] Structure027  label="B016"  # Arch/BIM 7 (typed FeaturePython)
  FaceMaker = 0
  Height = 450
  HorizontalArea = 1.221e+06
  IfcData = IfcUID=0$aVNt64r6wge39pnK5Rxy,+2 more (map truncated)
  IfcType = 7
  Length = 4070
  Material = -> Material
  MoveBase = false
  MoveWithHost = false
  Nodes = (2) [(-4.93038e-32,0,-2.22045e-16),(-4.93038e-32,0,4070)]
  NodesOffset = 0
  Normal = (0,0,0)
  PerimeterLength = 8740
  Placement = pos=(11580,5150,-225) rot=(0,0,1;0rad)
  PredefinedType = 0
  Tag = PlinthBeam
  VerticalArea = 3.933e+06
  Width = 300
FEATURE [Part::FeaturePython] Structure028  label="B101"  # Arch/BIM 7 (typed FeaturePython)
  FaceMaker = 0
  Height = 300
  HorizontalArea = 1.482e+06
  IfcData = IfcUID=3TRDrQVU58qQ5uO9Mp4rVE,+2 more (map truncated)
  IfcType = 7
  Length = 4940
  Material = -> Material
  MoveBase = false
  MoveWithHost = false
  Nodes = (2) [(1.2326e-31,-1.51582e-15,5.55112e-16),(1.2326e-31,-1.51582e-15,4940)]
  NodesOffset = 0
  Normal = (0,0,0)
  PerimeterLength = 10480
  Placement = pos=(300,150,3350) rot=(0,0,1;0rad)
  PredefinedType = 0
  Tag = RoofBeam
  VerticalArea = 3.144e+06
  Width = 300
FEATURE [Part::FeaturePython] Structure029  label="B102"  # Arch/BIM 7 (typed FeaturePython)
  FaceMaker = 0
  Height = 300
  HorizontalArea = 1.41e+06
  IfcData = IfcUID=0jZjxhYcrAxu1$8xtpmGLn,+2 more (map truncated)
  IfcType = 7
  Length = 4700
  Material = -> Material
  MoveBase = false
  MoveWithHost = false
  Nodes = (2) [(1.2326e-31,-1.51582e-15,5.55112e-16),(1.2326e-31,-1.51582e-15,4700)]
  NodesOffset = 0
  Normal = (0,0,0)
  PerimeterLength = 10000
  Placement = pos=(5390,300,3350) rot=(0,0,1;1.5708rad)
  PredefinedType = 0
  Tag = RoofBeam
  VerticalArea = 3000000
  Width = 300
FEATURE [Part::FeaturePython] Structure030  label="B103"  # Arch/BIM 7 (typed FeaturePython)
  FaceMaker = 0
  Height = 300
  HorizontalArea = 1.722e+06
  IfcData = IfcUID=3P00ZggMvD_Rb2srvlo6J3,+2 more (map truncated)
  IfcType = 7
  Length = 5740
  Material = -> Material
  MoveBase = false
  MoveWithHost = false
  Nodes = (2) [(1.2326e-31,-1.51582e-15,5.55112e-16),(1.2326e-31,-1.51582e-15,5740)]
  NodesOffset = 0
  Normal = (0,0,0)
  PerimeterLength = 12080
  Placement = pos=(5540,5150,3350) rot=(0,0,1;0rad)
  PredefinedType = 0
  Tag = RoofBeam
  VerticalArea = 3624000
  Width = 300
FEATURE [Part::FeaturePython] Structure031  label="B104"  # Arch/BIM 7 (typed FeaturePython)
  FaceMaker = 0
  Height = 300
  HorizontalArea = 1.41e+06
  IfcData = IfcUID=1RrkA2d2P0Uf4wevZIInFn,+2 more (map truncated)
  IfcType = 7
  Length = 4700
  Material = -> Material
  MoveBase = false
  MoveWithHost = false
  Nodes = (2) [(1.2326e-31,-1.51582e-15,5.55112e-16),(1.2326e-31,-1.51582e-15,4700)]
  NodesOffset = 0
  Normal = (0,0,0)
  PerimeterLength = 10000
  Placement = pos=(11430,5000,3350) rot=(0,0,-1;1.5708rad)
  PredefinedType = 0
  Tag = RoofBeam
  VerticalArea = 3000000
  Width = 300
FEATURE [Part::FeaturePython] Structure032  label="B105"  # Arch/BIM 7 (typed FeaturePython)
  FaceMaker = 0
  Height = 300
  HorizontalArea = 1.221e+06
  IfcData = IfcUID=06lwKBMgf1NAxtCpxb8mVZ,+2 more (map truncated)
  IfcType = 7
  Length = 4070
  Material = -> Material
  MoveBase = false
  MoveWithHost = false
  Nodes = (2) [(1.2326e-31,-1.51582e-15,5.55112e-16),(1.2326e-31,-1.51582e-15,4070)]
  NodesOffset = 0
  Normal = (0,0,0)
  PerimeterLength = 8740
  Placement = pos=(11580,150,3350) rot=(0,0,1;0rad)
  PredefinedType = 0
  Tag = RoofBeam
  VerticalArea = 2.622e+06
  Width = 300
FEATURE [Part::FeaturePython] Structure033  label="B106"  # Arch/BIM 7 (typed FeaturePython)
  FaceMaker = 0
  Height = 300
  HorizontalArea = 1.41e+06
  IfcData = IfcUID=3m2drC2Cj3T9e_05ymUP7m,+2 more (map truncated)
  IfcType = 7
  Length = 4700
  Material = -> Material
  MoveBase = false
  MoveWithHost = false
  Nodes = (2) [(1.2326e-31,-1.51582e-15,5.55112e-16),(1.2326e-31,-1.51582e-15,4700)]
  NodesOffset = 0
  Normal = (0,0,0)
  PerimeterLength = 10000
  Placement = pos=(15800,300,3350) rot=(0,0,1;1.5708rad)
  PredefinedType = 0
  Tag = RoofBeam
  VerticalArea = 3000000
  Width = 300
FEATURE [Part::FeaturePython] Structure034  label="B107"  # Arch/BIM 7 (typed FeaturePython)
  FaceMaker = 0
  Height = 300
  HorizontalArea = 1.299e+06
  IfcData = IfcUID=2kD2r2rHnDrhJQHHYXML8F,+2 more (map truncated)
  IfcType = 7
  Length = 4330
  Material = -> Material
  MoveBase = false
  MoveWithHost = false
  Nodes = (2) [(1.2326e-31,-1.51582e-15,5.55112e-16),(1.2326e-31,-1.51582e-15,4330)]
  NodesOffset = 0
  Normal = (0,0,0)
  PerimeterLength = 9260
  Placement = pos=(15800,5300,3350) rot=(0,0,1;1.5708rad)
  PredefinedType = 0
  Tag = RoofBeam
  VerticalArea = 2.778e+06
  Width = 300
FEATURE [Part::FeaturePython] Structure035  label="B108"  # Arch/BIM 7 (typed FeaturePython)
  FaceMaker = 0
  Height = 300
  HorizontalArea = 1.221e+06
  IfcData = IfcUID=0HBAcwwFL9BfhTFOQm_0_v,+2 more (map truncated)
  IfcType = 7
  Length = 4070
  Material = -> Material
  MoveBase = false
  MoveWithHost = false
  Nodes = (2) [(1.2326e-31,-1.51582e-15,5.55112e-16),(1.2326e-31,-1.51582e-15,4070)]
  NodesOffset = 0
  Normal = (0,0,0)
  PerimeterLength = 8740
  Placement = pos=(15650,9780,3350) rot=(0,0,1;3.14159rad)
  PredefinedType = 0
  Tag = RoofBeam
  VerticalArea = 2.622e+06
  Width = 300
FEATURE [Part::FeaturePython] Structure036  label="B109"  # Arch/BIM 7 (typed FeaturePython)
  FaceMaker = 0
  Height = 300
  HorizontalArea = 1.722e+06
  IfcData = IfcUID=2hcQ$JzFbAHex9o2qXS0XD,+2 more (map truncated)
  IfcType = 7
  Length = 5740
  Material = -> Material
  MoveBase = false
  MoveWithHost = false
  Nodes = (2) [(1.2326e-31,-1.51582e-15,5.55112e-16),(1.2326e-31,-1.51582e-15,5740)]
  NodesOffset = 0
  Normal = (0,0,0)
  PerimeterLength = 12080
  Placement = pos=(11280,9780,3350) rot=(0,0,1;3.14159rad)
  PredefinedType = 0
  Tag = RoofBeam
  VerticalArea = 3624000
  Width = 300
FEATURE [Part::FeaturePython] Structure037  label="B110"  # Arch/BIM 7 (typed FeaturePython)
  FaceMaker = 0
  Height = 300
  HorizontalArea = 1.482e+06
  IfcData = IfcUID=1fMbdgu8v6J9OBZvKdVImw,+2 more (map truncated)
  IfcType = 7
  Length = 4940
  Material = -> Material
  MoveBase = false
  MoveWithHost = false
  Nodes = (2) [(1.2326e-31,-1.51582e-15,5.55112e-16),(1.2326e-31,-1.51582e-15,4940)]
  NodesOffset = 0
  Normal = (0,0,0)
  PerimeterLength = 10480
  Placement = pos=(5240,9780,3350) rot=(0,0,1;3.14159rad)
  PredefinedType = 0
  Tag = RoofBeam
  VerticalArea = 3.144e+06
  Width = 300
FEATURE [Part::FeaturePython] Structure038  label="B111"  # Arch/BIM 7 (typed FeaturePython)
  FaceMaker = 0
  Height = 300
  HorizontalArea = 1.299e+06
  IfcData = IfcUID=0Jt3HB3kPEYvg1Hsle9OVr,+2 more (map truncated)
  IfcType = 7
  Length = 4330
  Material = -> Material
  MoveBase = false
  MoveWithHost = false
  Nodes = (2) [(1.2326e-31,-1.51582e-15,5.55112e-16),(1.2326e-31,-1.51582e-15,4330)]
  NodesOffset = 0
  Normal = (0,0,0)
  PerimeterLength = 9260
  Placement = pos=(150,9630,3350) rot=(0,0,-1;1.5708rad)
  PredefinedType = 0
  Tag = RoofBeam
  VerticalArea = 2.778e+06
  Width = 300
FEATURE [Part::FeaturePython] Structure040  label="B113"  # Arch/BIM 7 (typed FeaturePython)
  FaceMaker = 0
  Height = 300
  HorizontalArea = 1.482e+06
  IfcData = IfcUID=3DXtJ3EtfEvw0Rg_v3Fvas,+2 more (map truncated)
  IfcType = 7
  Length = 4940
  Material = -> Material
  MoveBase = false
  MoveWithHost = false
  Nodes = (2) [(1.2326e-31,-1.51582e-15,5.55112e-16),(1.2326e-31,-1.51582e-15,4940)]
  NodesOffset = 0
  Normal = (0,0,0)
  PerimeterLength = 10480
  Placement = pos=(5240,5150,3350) rot=(0,0,1;3.14159rad)
  PredefinedType = 0
  Tag = RoofBeam
  VerticalArea = 3.144e+06
  Width = 300
FEATURE [Part::FeaturePython] Structure041  label="B114"  # Arch/BIM 7 (typed FeaturePython)
  FaceMaker = 0
  Height = 300
  HorizontalArea = 1.299e+06
  IfcData = IfcUID=0TT7eXFAHBMBDn7_QOjYQh,+2 more (map truncated)
  IfcType = 7
  Length = 4330
  Material = -> Material
  MoveBase = false
  MoveWithHost = false
  Nodes = (2) [(1.2326e-31,-1.51582e-15,5.55112e-16),(1.2326e-31,-1.51582e-15,4330)]
  NodesOffset = 0
  Normal = (0,0,0)
  PerimeterLength = 9260
  Placement = pos=(5390,9630,3350) rot=(0,0,-1;1.5708rad)
  PredefinedType = 0
  Tag = RoofBeam
  VerticalArea = 2.778e+06
  Width = 300
FEATURE [Part::FeaturePython] Structure042  label="B115"  # Arch/BIM 7 (typed FeaturePython)
  FaceMaker = 0
  Height = 300
  HorizontalArea = 1.299e+06
  IfcData = IfcUID=1s$V0cw1P89xbMo$aSzw$q,+2 more (map truncated)
  IfcType = 7
  Length = 4330
  Material = -> Material
  MoveBase = false
  MoveWithHost = false
  Nodes = (2) [(1.2326e-31,-1.51582e-15,5.55112e-16),(1.2326e-31,-1.51582e-15,4330)]
  NodesOffset = 0
  Normal = (0,0,0)
  PerimeterLength = 9260
  Placement = pos=(11430,9630,3350) rot=(0,0,-1;1.5708rad)
  PredefinedType = 0
  Tag = RoofBeam
  VerticalArea = 2.778e+06
  Width = 300
FEATURE [Part::FeaturePython] Structure043  label="B116"  # Arch/BIM 7 (typed FeaturePython)
  FaceMaker = 0
  Height = 300
  HorizontalArea = 1.221e+06
  IfcData = IfcUID=2rXbw$CbX6IhQvw70gj5Uq,+2 more (map truncated)
  IfcType = 7
  Length = 4070
  Material = -> Material
  MoveBase = false
  MoveWithHost = false
  Nodes = (2) [(1.2326e-31,-1.51582e-15,5.55112e-16),(1.2326e-31,-1.51582e-15,4070)]
  NodesOffset = 0
  Normal = (0,0,0)
  PerimeterLength = 8740
  Placement = pos=(15650,5150,3350) rot=(0,0,1;3.14159rad)
  PredefinedType = 0
  Tag = RoofBeam
  VerticalArea = 2.622e+06
  Width = 300
FEATURE [Part::FeaturePython] Structure044  label="B117"  # Arch/BIM 7 (typed FeaturePython)
  FaceMaker = 0
  Height = 300
  HorizontalArea = 1.722e+06
  IfcData = IfcUID=37PX4aN5DCPeqNQOwXE6yW,+2 more (map truncated)
  IfcType = 7
  Length = 5740
  Material = -> Material
  MoveBase = false
  MoveWithHost = false
  Nodes = (2) [(1.2326e-31,-1.51582e-15,5.55112e-16),(1.2326e-31,-1.51582e-15,5740)]
  NodesOffset = 0
  Normal = (0,0,0)
  PerimeterLength = 12080
  Placement = pos=(5540,3800,3350) rot=(0,0,1;0rad)
  PredefinedType = 0
  Tag = RoofBeam
  VerticalArea = 3624000
  Width = 300
FEATURE [Part::FeaturePython] Structure045  label="B017"  # Arch/BIM 7 (typed FeaturePython)
  FaceMaker = 0
  Height = 450
  HorizontalArea = 1.722e+06
  IfcData = IfcUID=0F8Fga21r0bwVCANd$Q5o6,+2 more (map truncated)
  IfcType = 7
  Length = 5740
  Material = -> Material
  MoveBase = false
  MoveWithHost = false
  Nodes = (2) [(-4.93038e-32,0,-2.22045e-16),(-4.93038e-32,0,5740)]
  NodesOffset = 0
  Normal = (0,0,0)
  PerimeterLength = 12080
  Placement = pos=(5540,5150,-225) rot=(0,0,1;0rad)
  PredefinedType = 0
  Tag = PlinthBeam
  VerticalArea = 5.436e+06
  Width = 300
FEATURE [Part::FeaturePython] Structure046  label="BL001"  # Arch/BIM 7 (typed FeaturePython)
  FaceMaker = 0
  Height = 150
  HorizontalArea = 1.482e+06
  IfcData = IfcUID=1MidrtGLj4qAdk8efhrE$X,+2 more (map truncated)
  IfcType = 7
  Length = 4940
  Material = -> Material
  MoveBase = false
  MoveWithHost = false
  Nodes = (2) [(6.16298e-32,-1.51582e-15,2.77556e-16),(6.16298e-32,-1.51582e-15,4940)]
  NodesOffset = 0
  Normal = (0,0,0)
  PerimeterLength = 10480
  Placement = pos=(300,150,2435) rot=(0,0,1;0rad)
  PredefinedType = 3
  Tag = LintelBeam
  VerticalArea = 1.572e+06
  Width = 300
FEATURE [Part::FeaturePython] Structure047  label="BL002"  # Arch/BIM 7 (typed FeaturePython)
  FaceMaker = 0
  Height = 150
  HorizontalArea = 1.221e+06
  IfcData = IfcUID=1zAQlwqor0QgIjsD5lTylX,+2 more (map truncated)
  IfcType = 7
  Length = 4070
  Material = -> Material
  MoveBase = false
  MoveWithHost = false
  Nodes = (2) [(6.16298e-32,-1.51582e-15,2.77556e-16),(6.16298e-32,-1.51582e-15,4070)]
  NodesOffset = 0
  Normal = (0,0,0)
  PerimeterLength = 8740
  Placement = pos=(11580,150,2435) rot=(0,0,1;0rad)
  PredefinedType = 3
  Tag = LintelBeam
  VerticalArea = 1.311e+06
  Width = 300
FEATURE [Part::FeaturePython] Structure048  label="BL003"  # Arch/BIM 7 (typed FeaturePython)
  FaceMaker = 0
  Height = 150
  HorizontalArea = 1.41e+06
  IfcData = IfcUID=1buFuNJwPBTvz$5KGdvSQt,+2 more (map truncated)
  IfcType = 7
  Length = 4700
  Material = -> Material
  MoveBase = false
  MoveWithHost = false
  Nodes = (2) [(6.16298e-32,-1.51582e-15,2.77556e-16),(6.16298e-32,-1.51582e-15,4700)]
  NodesOffset = 0
  Normal = (0,0,0)
  PerimeterLength = 10000
  Placement = pos=(15800,300,2435) rot=(0,0,1;1.5708rad)
  PredefinedType = 3
  Tag = LintelBeam
  VerticalArea = 1.5e+06
  Width = 300
FEATURE [Part::FeaturePython] Structure049  label="BL004"  # Arch/BIM 7 (typed FeaturePython)
  FaceMaker = 0
  Height = 150
  HorizontalArea = 1.299e+06
  IfcData = IfcUID=1jDGUEr$D3fvP4J36OiVo_,+2 more (map truncated)
  IfcType = 7
  Length = 4330
  Material = -> Material
  MoveBase = false
  MoveWithHost = false
  Nodes = (2) [(6.16298e-32,-1.51582e-15,2.77556e-16),(6.16298e-32,-1.51582e-15,4330)]
  NodesOffset = 0
  Normal = (0,0,0)
  PerimeterLength = 9260
  Placement = pos=(15800,5300,2435) rot=(0,0,1;1.5708rad)
  PredefinedType = 3
  Tag = LintelBeam
  VerticalArea = 1389000
  Width = 300
FEATURE [Part::FeaturePython] Structure050  label="BL005"  # Arch/BIM 7 (typed FeaturePython)
  FaceMaker = 0
  Height = 150
  HorizontalArea = 1.221e+06
  IfcData = IfcUID=3QM1scwiv2s88bUJMVvsyY,+2 more (map truncated)
  IfcType = 7
  Length = 4070
  Material = -> Material
  MoveBase = false
  MoveWithHost = false
  Nodes = (2) [(6.16298e-32,-1.51582e-15,2.77556e-16),(6.16298e-32,-1.51582e-15,4070)]
  NodesOffset = 0
  Normal = (0,0,0)
  PerimeterLength = 8740
  Placement = pos=(15650,9780,2435) rot=(0,0,1;3.14159rad)
  PredefinedType = 3
  Tag = LintelBeam
  VerticalArea = 1.311e+06
  Width = 300
FEATURE [Part::FeaturePython] Structure051  label="BL006"  # Arch/BIM 7 (typed FeaturePython)
  FaceMaker = 0
  Height = 150
  HorizontalArea = 1.722e+06
  IfcData = IfcUID=18MBPuoXbAhBu$W6MtE_n0,+2 more (map truncated)
  IfcType = 7
  Length = 5740
  Material = -> Material
  MoveBase = false
  MoveWithHost = false
  Nodes = (2) [(6.16298e-32,-1.51582e-15,2.77556e-16),(6.16298e-32,-1.51582e-15,5740)]
  NodesOffset = 0
  Normal = (0,0,0)
  PerimeterLength = 12080
  Placement = pos=(11280,9780,2435) rot=(0,0,1;3.14159rad)
  PredefinedType = 3
  Tag = LintelBeam
  VerticalArea = 1.812e+06
  Width = 300
FEATURE [Part::FeaturePython] Structure052  label="BL007"  # Arch/BIM 7 (typed FeaturePython)
  FaceMaker = 0
  Height = 150
  HorizontalArea = 1.482e+06
  IfcData = IfcUID=3I4nRSbmbCKArvivUJ03Md,+2 more (map truncated)
  IfcType = 7
  Length = 4940
  Material = -> Material
  MoveBase = false
  MoveWithHost = false
  Nodes = (2) [(6.16298e-32,-1.51582e-15,2.77556e-16),(6.16298e-32,-1.51582e-15,4940)]
  NodesOffset = 0
  Normal = (0,0,0)
  PerimeterLength = 10480
  Placement = pos=(5240,9780,2435) rot=(0,0,1;3.14159rad)
  PredefinedType = 3
  Tag = LintelBeam
  VerticalArea = 1.572e+06
  Width = 300
FEATURE [Part::FeaturePython] Structure053  label="BL008"  # Arch/BIM 7 (typed FeaturePython)
  FaceMaker = 0
  Height = 150
  HorizontalArea = 1.299e+06
  IfcData = IfcUID=0VLmkA1F9AJhCwRJSUpmFd,+2 more (map truncated)
  IfcType = 7
  Length = 4330
  Material = -> Material
  MoveBase = false
  MoveWithHost = false
  Nodes = (2) [(6.16298e-32,-1.51582e-15,2.77556e-16),(6.16298e-32,-1.51582e-15,4330)]
  NodesOffset = 0
  Normal = (0,0,0)
  PerimeterLength = 9260
  Placement = pos=(150,9630,2435) rot=(0,0,-1;1.5708rad)
  PredefinedType = 3
  Tag = LintelBeam
  VerticalArea = 1389000
  Width = 300
FEATURE [Part::FeaturePython] Structure054  label="BL009"  # Arch/BIM 7 (typed FeaturePython)
  FaceMaker = 0
  Height = 150
  HorizontalArea = 1.41e+06
  IfcData = IfcUID=0uxjtJjx10vQzqxgh$pQ2y,+2 more (map truncated)
  IfcType = 7
  Length = 4700
  Material = -> Material
  MoveBase = false
  MoveWithHost = false
  Nodes = (2) [(6.16298e-32,-1.51582e-15,2.77556e-16),(6.16298e-32,-1.51582e-15,4700)]
  NodesOffset = 0
  Normal = (0,0,0)
  PerimeterLength = 10000
  Placement = pos=(150,5000,2435) rot=(0,0,-1;1.5708rad)
  PredefinedType = 3
  Tag = LintelBeam
  VerticalArea = 1.5e+06
  Width = 300
FEATURE [Part::FeaturePython] Structure055  label="BL010"  # Arch/BIM 7 (typed FeaturePython)
  FaceMaker = 0
  Height = 150
  HorizontalArea = 1.005e+06
  IfcData = IfcUID=1vMLdgOPfBEf0j9kRCz2WW,+2 more (map truncated)
  IfcType = 7
  Length = 3350
  Material = -> Material
  MoveBase = false
  MoveWithHost = false
  Nodes = (2) [(6.16298e-32,-1.51582e-15,2.77556e-16),(6.16298e-32,-1.51582e-15,3350)]
  NodesOffset = 0
  Normal = (0,0,0)
  PerimeterLength = 7300
  Placement = pos=(5390,300,2435) rot=(0,0,1;1.5708rad)
  PredefinedType = 3
  Tag = LintelBeam
  VerticalArea = 1.095e+06
  Width = 300
FEATURE [Part::FeaturePython] Structure056  label="BL011"  # Arch/BIM 7 (typed FeaturePython)
  FaceMaker = 0
  Height = 150
  HorizontalArea = 1.005e+06
  IfcData = IfcUID=0S7v0cW3n9zv9sehygqIl7,+2 more (map truncated)
  IfcType = 7
  Length = 3350
  Material = -> Material
  MoveBase = false
  MoveWithHost = false
  Nodes = (2) [(6.16298e-32,-1.51582e-15,2.77556e-16),(6.16298e-32,-1.51582e-15,3350)]
  NodesOffset = 0
  Normal = (0,0,0)
  PerimeterLength = 7300
  Placement = pos=(11430,300,2435) rot=(0,0,1;1.5708rad)
  PredefinedType = 3
  Tag = LintelBeam
  VerticalArea = 1.095e+06
  Width = 300
FEATURE [Part::FeaturePython] Structure057  label="BL012"  # Arch/BIM 7 (typed FeaturePython)
  FaceMaker = 0
  Height = 150
  HorizontalArea = 1.902e+06
  IfcData = IfcUID=3cvUSY2HX6q8aklW9w6X9y,+2 more (map truncated)
  IfcType = 7
  Length = 6340
  Material = -> Material
  MoveBase = false
  MoveWithHost = false
  Nodes = (2) [(6.16298e-32,-1.51582e-15,2.77556e-16),(6.16298e-32,-1.51582e-15,6340)]
  NodesOffset = 0
  Normal = (0,0,0)
  PerimeterLength = 13280
  Placement = pos=(11580,3800,2435) rot=(0,0,1;3.14159rad)
  PredefinedType = 3
  Tag = LintelBeam
  VerticalArea = 1.992e+06
  Width = 300
FEATURE [Part::FeaturePython] Structure001  label="C002"  # Arch/BIM 24 (typed FeaturePython)
  FaceMaker = 0
  Height = 5000
  HorizontalArea = 90000
  IfcData = IfcUID=2nTSQfP357fPcX7VKl91nF,+2 more (map truncated)
  IfcType = 24
  Length = 300
  Material = -> Material
  MoveBase = false
  MoveWithHost = false
  Nodes = (2) [(5.55112e-16,1.51582e-15,0),(5.55112e-16,1.51582e-15,5000)]
  NodesOffset = 0
  Normal = (0,0,0)
  PerimeterLength = 1200
  Placement = pos=(5390,150,-1500) rot=(0,0,1;0rad)
  PredefinedType = 0
  Tag = MainColumn
  VerticalArea = 6000000
  Width = 300
FEATURE [Part::FeaturePython] Structure058  label="S101"  # Arch/BIM 118 (typed FeaturePython)
  Base = -> Rectangle001
  FaceMaker = 0
  Height = 150
  HorizontalArea = 2.57642e+07
  IfcData = IfcUID=2joUZhKTr2kBb8aWqJxzTH,+2 more (map truncated)
  IfcType = 118
  Length = 0
  Material = -> Material
  MoveBase = false
  MoveWithHost = false
  Nodes = (4) [(9.09495e-13,-5150,3500),(-5390,-5150,3500),(-5390,-9930,3500),(1.81899e-12,-9930,3500)]
  NodesOffset = 0
  Normal = (0,0,0)
  PerimeterLength = 20340
  PredefinedType = 1
  Tag = MainSlab
  VerticalArea = 3.051e+06
  Width = 300
FEATURE [Part::FeaturePython] Structure060  label="S102"  # Arch/BIM 118 (typed FeaturePython)
  Base = -> Rectangle004
  FaceMaker = 0
  Height = 150
  HorizontalArea = 2.88712e+07
  IfcData = IfcUID=3DUgepDbf5QBtaB9OqMqNx,+2 more (map truncated)
  IfcType = 118
  Length = 0
  Material = -> Material
  MoveBase = false
  MoveWithHost = false
  Nodes = (4) [(-5390,-5150,3500),(-11430,-5150,3500),(-11430,-9930,3500),(-5390,-9930,3500)]
  NodesOffset = 0
  Normal = (0,0,0)
  PerimeterLength = 21640
  PredefinedType = 1
  Tag = MainSlab
  VerticalArea = 3.246e+06
  Width = 300
FEATURE [Part::FeaturePython] Structure063  label="S104"  # Arch/BIM 118 (typed FeaturePython)
  Base = -> Rectangle005
  FaceMaker = 0
  Height = 150
  HorizontalArea = 2.16056e+07
  IfcData = IfcUID=1KTD9ZuxLENQbuf$6R5_eC,+2 more (map truncated)
  IfcType = 118
  Length = 0
  Material = -> Material
  MoveBase = false
  MoveWithHost = false
  Nodes = (4) [(-11430,-5150,3500),(-15950,-5150,3500),(-15950,-9930,3500),(-11430,-9930,3500)]
  NodesOffset = 0
  Normal = (0,0,0)
  PerimeterLength = 18600
  PredefinedType = 1
  Tag = MainSlab
  VerticalArea = 2.79e+06
  Width = 300
FEATURE [Part::FeaturePython] Structure065  label="S106"  # Arch/BIM 118 (typed FeaturePython)
  Base = -> Rectangle008
  FaceMaker = 0
  Height = 150
  HorizontalArea = 9.06e+06
  IfcData = IfcUID=3G6ln4CwrFJ9VBS8sB2oUE,+2 more (map truncated)
  IfcType = 118
  Length = 0
  Material = -> Material
  MoveBase = false
  MoveWithHost = false
  Nodes = (4) [(-5390,-3650,3500),(-11430,-3650,3500),(-11430,-5150,3500),(-5390,-5150,3500)]
  NodesOffset = 0
  Normal = (0,0,0)
  PerimeterLength = 15080
  PredefinedType = 1
  Tag = MainSlab
  VerticalArea = 2262000
  Width = 300
FEATURE [Part::FeaturePython] Structure062  label="S103"  # Arch/BIM 118 (typed FeaturePython)
  Base = -> Rectangle006
  FaceMaker = 0
  Height = 150
  HorizontalArea = 2.38255e+07
  IfcData = IfcUID=2aj0EV4jT3G8rBuLo_V_OR,+2 more (map truncated)
  IfcType = 118
  Length = 0
  Material = -> Material
  MoveBase = false
  MoveWithHost = false
  Nodes = (4) [(-11280,2.72848e-12,3500),(-15950,1.81899e-12,3500),(-15950,-5150,3500),(-11280,-5150,3500)]
  NodesOffset = 0
  Normal = (0,0,0)
  PerimeterLength = 19640
  PredefinedType = 1
  Subtractions = -> [Structure065]
  Tag = MainSlab
  VerticalArea = 2.946e+06
  Width = 300
FEATURE [Part::FeaturePython] Structure064  label="S105"  # Arch/BIM 118 (typed FeaturePython)
  Base = -> Rectangle007
  FaceMaker = 0
  Height = 150
  HorizontalArea = 2.8306e+07
  IfcData = IfcUID=3rzNMi0c574fSXV4DFg_H9,+2 more (map truncated)
  IfcType = 118
  Length = 0
  Material = -> Material
  MoveBase = false
  MoveWithHost = false
  Nodes = (4) [(-9.09495e-13,2.72848e-12,3500),(-5540,1.81899e-12,3500),(-5540,-5150,3500),(0,-5150,3500)]
  NodesOffset = 0
  Normal = (0,0,0)
  PerimeterLength = 21380
  PredefinedType = 1
  Subtractions = -> [Structure065]
  Tag = MainSlab
  VerticalArea = 3.207e+06
  Width = 300
FEATURE [Part::FeaturePython] Structure066  label="B112"  # Arch/BIM 7 (typed FeaturePython)
  FaceMaker = 0
  Height = 300
  HorizontalArea = 1.41e+06
  IfcData = IfcUID=07qgcpkHr4QBmNRWrOP1j7,+2 more (map truncated)
  IfcType = 7
  Length = 4700
  Material = -> Material
  MoveBase = false
  MoveWithHost = false
  Nodes = (2) [(1.2326e-31,-1.51582e-15,5.55112e-16),(1.2326e-31,-1.51582e-15,4700)]
  NodesOffset = 0
  Normal = (0,0,0)
  PerimeterLength = 10000
  Placement = pos=(150,300,3350) rot=(0,0,1;1.5708rad)
  PredefinedType = 0
  Tag = RoofBeam
  VerticalArea = 3000000
  Width = 300
FEATURE [Sketcher::SketchObject] Sketch005
  ExternalGeometry = -> [Structure048]
  Placement = pos=(15950,2698.54,1668.9) rot=(0.57735,0.57735,0.57735;2.0944rad)
  sketch-geometry (12):
    g0: LineSegment StartX=-2328.54 StartY=1451.1 StartZ=0 EndX=-1718.54 EndY=1451.1 EndZ=0
    g1: LineSegment StartX=-1718.54 StartY=1451.1 StartZ=0 EndX=-1718.54 EndY=841.103 EndZ=0
    g2: LineSegment StartX=-1718.54 StartY=841.103 StartZ=0 EndX=-2328.54 EndY=841.103 EndZ=0
    g3: LineSegment StartX=-2328.54 StartY=841.103 StartZ=0 EndX=-2328.54 EndY=1451.1 EndZ=0
    g4: LineSegment StartX=-2303.54 StartY=1426.1 StartZ=0 EndX=-1743.54 EndY=1426.1 EndZ=0
    g5: LineSegment StartX=-1743.54 StartY=1426.1 StartZ=0 EndX=-1743.54 EndY=866.103 EndZ=0
    g6: LineSegment StartX=-1743.54 StartY=866.103 StartZ=0 EndX=-2303.54 EndY=866.103 EndZ=0
    g7: LineSegment StartX=-2303.54 StartY=866.103 StartZ=0 EndX=-2303.54 EndY=1426.1 EndZ=0
    g8: LineSegment StartX=-2278.54 StartY=1376.1 StartZ=0 EndX=-1768.54 EndY=1376.1 EndZ=0
    g9: LineSegment StartX=-1768.54 StartY=1376.1 StartZ=0 EndX=-1768.54 EndY=916.103 EndZ=0
    g10: LineSegment StartX=-1768.54 StartY=916.103 StartZ=0 EndX=-2278.54 EndY=916.103 EndZ=0
    g11: LineSegment StartX=-2278.54 StartY=916.103 StartZ=0 EndX=-2278.54 EndY=1376.1 EndZ=0
  constraints (36):
    c: Coincident(g0,g1)
    c: Coincident(g1,g2)
    c: Coincident(g2,g3)
    c: Coincident(g3,g0)
    c: Horizontal(g0)
    c: Horizontal(g2)
    c: Vertical(g1)
    c: Vertical(g3)
    c: Coincident(g4,g5)
    c: Coincident(g5,g6)
    c: Coincident(g6,g7)
    c: Coincident(g7,g4)
    c: Horizontal(g4)
    c: Horizontal(g6)
    c: Vertical(g5)
    c: Vertical(g7)
    c: Coincident(g8,g9)
    c: Coincident(g9,g10)
    c: Coincident(g10,g11)
    c: Coincident(g11,g8)
    c: Horizontal(g8)
    c: Horizontal(g10)
    c: Vertical(g9)
    c: Vertical(g11)
    c: DistanceY(g4,g0) = 25
    c: DistanceY(g1,g5) = 25
    c: DistanceY(g5,g9) = 50
    c: DistanceY(g8,g4) = 50
    c: DistanceY(g1,g1) = 610
    c: DistanceX(g4,g8) = 25
    c: DistanceX(g0,g4) = 25
    c: DistanceX(g8,g4) = 25
    c: DistanceX(g5,g1) = 25
    c: DistanceX(g2,g2) = 610
    c: DistanceX(g-3,g2) = 70
    c: DistanceY(g2,g-3) = 0
FEATURE [Sketcher::SketchObject] Sketch010
  ExternalGeometry = -> [Structure048]
  Placement = pos=(15950,2724.08,1084.42) rot=(0.57735,0.57735,0.57735;2.0944rad)
  sketch-geometry (4):
    g0: LineSegment StartX=-2504.08 StartY=1425.58 StartZ=0 EndX=-1594.08 EndY=1425.58 EndZ=0
    g1: LineSegment StartX=-1594.08 StartY=1425.58 StartZ=0 EndX=-1594.08 EndY=1275.58 EndZ=0
    g2: LineSegment StartX=-1594.08 StartY=1275.58 StartZ=0 EndX=-2504.08 EndY=1275.58 EndZ=0
    g3: LineSegment StartX=-2504.08 StartY=1275.58 StartZ=0 EndX=-2504.08 EndY=1425.58 EndZ=0
  constraints (12):
    c: Coincident(g0,g1)
    c: Coincident(g1,g2)
    c: Coincident(g2,g3)
    c: Coincident(g3,g0)
    c: Horizontal(g0)
    c: Horizontal(g2)
    c: Vertical(g1)
    c: Vertical(g3)
    c: DistanceY(g1,g1) = 150
    c: DistanceX(g0,g0) = 910
    c: DistanceX(g0,g-3) = 80
    c: DistanceY(g-3,g0) = 0
FEATURE [Part::FeaturePython] Structure067  label="SS001"  # Arch/BIM 118 (typed FeaturePython)
  Base = -> Sketch010
  FaceMaker = 0
  Height = 500
  HorizontalArea = 455000
  IfcData = IfcUID=3BAwbaasf3AeWGpSjQgSAF,+2 more (map truncated)
  IfcType = 118
  Length = 0
  Material = -> Material
  MoveBase = false
  MoveWithHost = false
  Nodes = (2) [(15950,675,2435),(15950,675,2945)]
  NodesOffset = 0
  Normal = (0,0,0)
  PerimeterLength = 2820
  Placement = pos=(500,170,0) rot=(0,0,1;0rad)
  PredefinedType = 4
  Tag = SunShades
  VerticalArea = 423000
  Width = 300
FEATURE [Part::FeaturePython] Structure068  label="SS002"  # Arch/BIM 118 (typed FeaturePython)
  Base = -> Sketch011
  FaceMaker = 0
  Height = 500
  HorizontalArea = 455000
  IfcData = IfcUID=1UMxU8C0T0igiPK1lg6w7i,+2 more (map truncated)
  IfcType = 118
  Length = 0
  Material = -> Material
  MoveBase = false
  MoveWithHost = false
  Nodes = (2) [(15950,675,2435),(15950,675,2945)]
  NodesOffset = 0
  Normal = (0,0,0)
  PerimeterLength = 2820
  Placement = pos=(500,1810,0) rot=(0,0,1;0rad)
  PredefinedType = 4
  Tag = SunShades
  VerticalArea = 423000
  Width = 300
FEATURE [Part::FeaturePython] Structure070  label="SS003"  # Arch/BIM 118 (typed FeaturePython)
  Base = -> Sketch012
  FaceMaker = 0
  Height = 500
  HorizontalArea = 455000
  IfcData = IfcUID=2ClYmNpIz8ruWcqY5KIBJs,+2 more (map truncated)
  IfcType = 118
  Length = 0
  Material = -> Material
  MoveBase = false
  MoveWithHost = false
  Nodes = (2) [(15950,675,2435),(15950,675,2945)]
  NodesOffset = 0
  Normal = (0,0,0)
  PerimeterLength = 2820
  Placement = pos=(500,3650,0) rot=(0,0,1;0rad)
  PredefinedType = 4
  Tag = SunShades
  VerticalArea = 423000
  Width = 300
FEATURE [Part::FeaturePython] Structure072  label="SS004"  # Arch/BIM 118 (typed FeaturePython)
  Base = -> Sketch013
  FaceMaker = 0
  Height = 500
  HorizontalArea = 455000
  IfcData = IfcUID=0dHyzsZyj2$RfebVbj05j8,+2 more (map truncated)
  IfcType = 118
  Length = 0
  Material = -> Material
  MoveBase = false
  MoveWithHost = false
  Nodes = (2) [(15950,675,2435),(15950,675,2945)]
  NodesOffset = 0
  Normal = (0,0,0)
  PerimeterLength = 2820
  Placement = pos=(500,5440,0) rot=(0,0,1;0rad)
  PredefinedType = 4
  Tag = SunShades
  VerticalArea = 423000
  Width = 300
FEATURE [Part::FeaturePython] Structure074  label="SS005"  # Arch/BIM 118 (typed FeaturePython)
  Base = -> Sketch014
  FaceMaker = 0
  Height = 500
  HorizontalArea = 455000
  IfcData = IfcUID=3HZ3SaWTTADuYAnxVIg4KS,+2 more (map truncated)
  IfcType = 118
  Length = 0
  Material = -> Material
  MoveBase = false
  MoveWithHost = false
  Nodes = (2) [(15950,675,2435),(15950,675,2935)]
  NodesOffset = 0
  Normal = (0,0,0)
  PerimeterLength = 2820
  Placement = pos=(500,7200,1) rot=(0,0,1;0rad)
  PredefinedType = 4
  Tag = SunShades
  VerticalArea = 423000
  Width = 300
FEATURE [Sketcher::SketchObject] Sketch015
  ExternalGeometry = -> [Structure017]
  Placement = pos=(13615,9930,1600) rot=(0,0.707107,0.707107;3.14159rad)
  sketch-geometry (12):
    g0: LineSegment StartX=-1875 StartY=760 StartZ=0 EndX=-1265 EndY=760 EndZ=0
    g1: LineSegment StartX=-1265 StartY=760 StartZ=0 EndX=-1265 EndY=150 EndZ=0
    g2: LineSegment StartX=-1265 StartY=150 StartZ=0 EndX=-1875 EndY=150 EndZ=0
    g3: LineSegment StartX=-1875 StartY=150 StartZ=0 EndX=-1875 EndY=760 EndZ=0
    g4: LineSegment StartX=-1850 StartY=735 StartZ=0 EndX=-1290 EndY=735 EndZ=0
    g5: LineSegment StartX=-1290 StartY=735 StartZ=0 EndX=-1290 EndY=175 EndZ=0
    g6: LineSegment StartX=-1290 StartY=175 StartZ=0 EndX=-1850 EndY=175 EndZ=0
    g7: LineSegment StartX=-1850 StartY=175 StartZ=0 EndX=-1850 EndY=735 EndZ=0
    g8: LineSegment StartX=-1825 StartY=685 StartZ=0 EndX=-1315 EndY=685 EndZ=0
    g9: LineSegment StartX=-1315 StartY=685 StartZ=0 EndX=-1315 EndY=225 EndZ=0
    g10: LineSegment StartX=-1315 StartY=225 StartZ=0 EndX=-1825 EndY=225 EndZ=0
    g11: LineSegment StartX=-1825 StartY=225 StartZ=0 EndX=-1825 EndY=685 EndZ=0
  constraints (36):
    c: Coincident(g0,g1)
    c: Coincident(g1,g2)
    c: Coincident(g2,g3)
    c: Coincident(g3,g0)
    c: Horizontal(g0)
    c: Horizontal(g2)
    c: Vertical(g1)
    c: Vertical(g3)
    c: Coincident(g4,g5)
    c: Coincident(g5,g6)
    c: Coincident(g6,g7)
    c: Coincident(g7,g4)
    c: Horizontal(g4)
    c: Horizontal(g6)
    c: Vertical(g5)
    c: Vertical(g7)
    c: Coincident(g8,g9)
    c: Coincident(g9,g10)
    c: Coincident(g10,g11)
    c: Coincident(g11,g8)
    c: Horizontal(g8)
    c: Horizontal(g10)
    c: Vertical(g9)
    c: Vertical(g11)
    c: DistanceX(g4,g0) = 25
    c: DistanceX(g0,g4) = 25
    c: DistanceX(g4,g8) = 25
    c: DistanceX(g8,g4) = 25
    c: DistanceX(g0,g0) = 610
    c: DistanceY(g4,g0) = 25
    c: DistanceY(g8,g4) = 50
    c: DistanceY(g5,g9) = 50
    c: DistanceY(g1,g5) = 25
    c: DistanceY(g1,g1) = 610
    c: DistanceY(g-3,g2) = 1750
    c: DistanceX(g-3,g2) = 160
FEATURE [Sketcher::SketchObject] Sketch018
  ExternalGeometry = -> [Structure050]
  Placement = pos=(13615.4,9930,1106.51) rot=(-1,0,0;1.5708rad)
  sketch-geometry (12):
    g0: LineSegment StartX=1874.58 StartY=-2013.49 StartZ=0 EndX=1264.58 EndY=-2013.49 EndZ=0
    g1: LineSegment StartX=1264.58 StartY=-2013.49 StartZ=0 EndX=1264.58 EndY=-1403.49 EndZ=0
    g2: LineSegment StartX=1264.58 StartY=-1403.49 StartZ=0 EndX=1874.58 EndY=-1403.49 EndZ=0
    g3: LineSegment StartX=1874.58 StartY=-1403.49 StartZ=0 EndX=1874.58 EndY=-2013.49 EndZ=0
    g4: LineSegment StartX=1849.58 StartY=-1988.49 StartZ=0 EndX=1289.58 EndY=-1988.49 EndZ=0
    g5: LineSegment StartX=1289.58 StartY=-1988.49 StartZ=0 EndX=1289.58 EndY=-1428.49 EndZ=0
    g6: LineSegment StartX=1289.58 StartY=-1428.49 StartZ=0 EndX=1849.58 EndY=-1428.49 EndZ=0
    g7: LineSegment StartX=1849.58 StartY=-1428.49 StartZ=0 EndX=1849.58 EndY=-1988.49 EndZ=0
    g8: LineSegment StartX=1824.58 StartY=-1938.49 StartZ=0 EndX=1314.58 EndY=-1938.49 EndZ=0
    g9: LineSegment StartX=1314.58 StartY=-1938.49 StartZ=0 EndX=1314.58 EndY=-1478.49 EndZ=0
    g10: LineSegment StartX=1314.58 StartY=-1478.49 StartZ=0 EndX=1824.58 EndY=-1478.49 EndZ=0
    g11: LineSegment StartX=1824.58 StartY=-1478.49 StartZ=0 EndX=1824.58 EndY=-1938.49 EndZ=0
  constraints (36):
    c: Coincident(g0,g1)
    c: Coincident(g1,g2)
    c: Coincident(g2,g3)
    c: Coincident(g3,g0)
    c: Horizontal(g0)
    c: Horizontal(g2)
    c: Vertical(g1)
    c: Vertical(g3)
    c: Coincident(g4,g5)
    c: Coincident(g5,g6)
    c: Coincident(g6,g7)
    c: Coincident(g7,g4)
    c: Horizontal(g4)
    c: Horizontal(g6)
    c: Vertical(g5)
    c: Vertical(g7)
    c: Coincident(g8,g9)
    c: Coincident(g9,g10)
    c: Coincident(g10,g11)
    c: Coincident(g11,g8)
    c: Horizontal(g8)
    c: Horizontal(g10)
    c: Vertical(g9)
    c: Vertical(g11)
    c: DistanceY(g1,g1) = 610
    c: DistanceX(g0,g0) = 610
    c: DistanceX(g0,g4) = 25
    c: DistanceX(g6,g2) = 25
    c: DistanceX(g10,g6) = 25
    c: DistanceX(g5,g9) = 25
    c: DistanceY(g9,g5) = 50
    c: DistanceY(g5,g1) = 25
    c: DistanceY(g4,g8) = 50
    c: DistanceY(g0,g4) = 25
    c: DistanceY(g2,g-3) = 0
    c: DistanceX(g2,g-3) = 160
FEATURE [Sketcher::SketchObject] Sketch021
  ExternalGeometry = -> [Structure035]
  Placement = pos=(13615,9930,2435) rot=(0,0.707107,0.707107;3.14159rad)
  sketch-geometry (4):
    g0: LineSegment StartX=-1845 StartY=75 StartZ=0 EndX=-945 EndY=75 EndZ=0
    g1: LineSegment StartX=-945 StartY=75 StartZ=0 EndX=-945 EndY=-75 EndZ=0
    g2: LineSegment StartX=-945 StartY=-75 StartZ=0 EndX=-1845 EndY=-75 EndZ=0
    g3: LineSegment StartX=-1845 StartY=-75 StartZ=0 EndX=-1845 EndY=75 EndZ=0
  constraints (12):
    c: Coincident(g0,g1)
    c: Coincident(g1,g2)
    c: Coincident(g2,g3)
    c: Coincident(g3,g0)
    c: Horizontal(g0)
    c: Horizontal(g2)
    c: Vertical(g1)
    c: Vertical(g3)
    c: DistanceY(g1,g1) = 150
    c: DistanceY(g1,g-1) = 75
    c: DistanceX(g0,g0) = 900
    c: DistanceX(g-3,g0) = 190
FEATURE [Part::FeaturePython] Structure075  label="SS006"  # Arch/BIM 118 (typed FeaturePython)
  Base = -> Sketch021
  FaceMaker = 0
  Height = 500
  HorizontalArea = 450000
  IfcData = IfcUID=1gH9DugarELuvCiCYF$vS9,+2 more (map truncated)
  IfcType = 118
  Length = 0
  Material = -> Material
  MoveBase = false
  MoveWithHost = false
  Nodes = (2) [(15010,9930,2435),(15010,9930,1935)]
  NodesOffset = 0
  Normal = (0,0,0)
  PerimeterLength = 2800
  Placement = pos=(1,500,0) rot=(0,0,1;0rad)
  PredefinedType = 4
  Tag = SunShades
  VerticalArea = 420000
  Width = 300
FEATURE [Part::FeaturePython] Structure076  label="SS007"  # Arch/BIM 118 (typed FeaturePython)
  Base = -> Sketch022
  FaceMaker = 0
  Height = 500
  HorizontalArea = 450000
  IfcData = IfcUID=3GgPqCG_X1PhCb7zkX2iYh,+2 more (map truncated)
  IfcType = 118
  Length = 0
  Material = -> Material
  MoveBase = false
  MoveWithHost = false
  Nodes = (2) [(15010,9930,2435),(15010,9930,1935)]
  NodesOffset = 0
  Normal = (0,0,0)
  PerimeterLength = 2800
  Placement = pos=(-2980,500,0) rot=(0,0,1;0rad)
  PredefinedType = 4
  Tag = SunShades
  VerticalArea = 420000
  Width = 300
FEATURE [Part::FeaturePython] Structure078  label="SS008"  # Arch/BIM 118 (typed FeaturePython)
  Base = -> Sketch023
  FaceMaker = 0
  Height = 500
  HorizontalArea = 450000
  IfcData = IfcUID=2ICFRbnSPFcAExe8xEBq45,+2 more (map truncated)
  IfcType = 118
  Length = 0
  Material = -> Material
  MoveBase = false
  MoveWithHost = false
  Nodes = (2) [(15010,9930,2435),(15010,9930,2935)]
  NodesOffset = 0
  Normal = (0,0,0)
  PerimeterLength = 2800
  Placement = pos=(-12780,500,0) rot=(0,0,1;0rad)
  PredefinedType = 4
  Tag = SunShades
  VerticalArea = 420000
  Width = 300
FEATURE [Sketcher::SketchObject] Sketch024
  ExternalGeometry = -> [Axis001,Structure051]
  Placement = pos=(8410,9930,1180) rot=(0,0.707107,0.707107;3.14159rad)
  sketch-geometry (20):
    g0: LineSegment StartX=-1970 StartY=1180 StartZ=0 EndX=-150 EndY=1180 EndZ=0
    g1: LineSegment StartX=-150 StartY=1180 StartZ=0 EndX=-150 EndY=70 EndZ=0
    g2: LineSegment StartX=-150 StartY=70 StartZ=0 EndX=-1970 EndY=70 EndZ=0
    g3: LineSegment StartX=-1970 StartY=70 StartZ=0 EndX=-1970 EndY=1180 EndZ=0
    g4: LineSegment StartX=-1945 StartY=1155 StartZ=0 EndX=-200 EndY=1155 EndZ=0
    g5: LineSegment StartX=-200 StartY=1155 StartZ=0 EndX=-200 EndY=95 EndZ=0
    g6: LineSegment StartX=-200 StartY=95 StartZ=0 EndX=-1945 EndY=95 EndZ=0
    g7: LineSegment StartX=-1945 StartY=95 StartZ=0 EndX=-1945 EndY=1155 EndZ=0
    g8: LineSegment StartX=-1920 StartY=1105 StartZ=0 EndX=-1388.33 EndY=1105 EndZ=0
    g9: LineSegment StartX=-1388.33 StartY=1105 StartZ=0 EndX=-1388.33 EndY=145 EndZ=0
    g10: LineSegment StartX=-1388.33 StartY=145 StartZ=0 EndX=-1920 EndY=145 EndZ=0
    g11: LineSegment StartX=-1920 StartY=145 StartZ=0 EndX=-1920 EndY=1105 EndZ=0
    g12: LineSegment StartX=-1338.33 StartY=1105 StartZ=0 EndX=-806.667 EndY=1105 EndZ=0
    g13: LineSegment StartX=-806.667 StartY=1105 StartZ=0 EndX=-806.667 EndY=145 EndZ=0
    g14: LineSegment StartX=-806.667 StartY=145 StartZ=0 EndX=-1338.33 EndY=145 EndZ=0
    g15: LineSegment StartX=-1338.33 StartY=145 StartZ=0 EndX=-1338.33 EndY=1105 EndZ=0
    g16: LineSegment StartX=-756.667 StartY=1105 StartZ=0 EndX=-225 EndY=1105 EndZ=0
    g17: LineSegment StartX=-225 StartY=1105 StartZ=0 EndX=-225 EndY=145 EndZ=0
    g18: LineSegment StartX=-225 StartY=145 StartZ=0 EndX=-756.667 EndY=145 EndZ=0
    g19: LineSegment StartX=-756.667 StartY=145 StartZ=0 EndX=-756.667 EndY=1105 EndZ=0
  constraints (60):
    c: Coincident(g0,g1)
    c: Coincident(g1,g2)
    c: Coincident(g2,g3)
    c: Coincident(g3,g0)
    c: Horizontal(g0)
    c: Horizontal(g2)
    c: Vertical(g1)
    c: Vertical(g3)
    c: Coincident(g4,g5)
    c: Coincident(g5,g6)
    c: Coincident(g6,g7)
    c: Coincident(g7,g4)
    c: Horizontal(g4)
    c: Horizontal(g6)
    c: Vertical(g5)
    c: Vertical(g7)
    c: Coincident(g8,g9)
    c: Coincident(g9,g10)
    c: Coincident(g10,g11)
    c: Coincident(g11,g8)
    c: Horizontal(g8)
    c: Horizontal(g10)
    c: Vertical(g9)
    c: Vertical(g11)
    c: Coincident(g12,g13)
    c: Coincident(g13,g14)
    c: Coincident(g14,g15)
    c: Coincident(g15,g12)
    c: Horizontal(g12)
    c: Horizontal(g14)
    c: Vertical(g13)
    c: Vertical(g15)
    c: Coincident(g16,g17)
    c: Coincident(g17,g18)
    c: Coincident(g18,g19)
    c: Coincident(g19,g16)
    c: Horizontal(g16)
    c: Horizontal(g18)
    c: Vertical(g17)
    c: Vertical(g19)
    c: Equal(g8,g12)
    c: Equal(g12,g16)
    c: Equal(g19,g13)
    c: Equal(g15,g9)
    c: DistanceY(g4,g0) = 25
    c: DistanceY(g1,g5) = 25
    c: DistanceY(g5,g17) = 50
    c: DistanceY(g16,g4) = 50
    c: DistanceX(g0,g4) = 25
    c: DistanceX(g6,g10) = 25
    c: DistanceX(g9,g14) = 50
    c: DistanceX(g13,g18) = 50
    c: DistanceY(g18,g13) = 0
    c: DistanceY(g14,g9) = 0
    c: DistanceX(g17,g5) = 25
    c: DistanceX(g5,g1) = 50
    c: DistanceX(g0,g0) = 1820
    c: DistanceX(g-4,g0) = 900
    c: DistanceY(g0,g-4) = 0
    c: DistanceY(g3,g3) = 1110
FEATURE [Sketcher::SketchObject] Sketch025
  ExternalGeometry = -> [Structure051]
  Placement = pos=(8410,9930,1180) rot=(0,0.707107,0.707107;3.14159rad)
  sketch-geometry (24):
    g0: LineSegment StartX=80 StartY=1180 StartZ=0 EndX=2530 EndY=1180 EndZ=0
    g1: LineSegment StartX=2530 StartY=1180 StartZ=0 EndX=2530 EndY=70 EndZ=0
    g2: LineSegment StartX=2530 StartY=70 StartZ=0 EndX=80 EndY=70 EndZ=0
    g3: LineSegment StartX=80 StartY=70 StartZ=0 EndX=80 EndY=1180 EndZ=0
    g4: LineSegment StartX=105 StartY=1155 StartZ=0 EndX=2505 EndY=1155 EndZ=0
    g5: LineSegment StartX=2505 StartY=1155 StartZ=0 EndX=2505 EndY=95 EndZ=0
    g6: LineSegment StartX=2505 StartY=95 StartZ=0 EndX=105 EndY=95 EndZ=0
    g7: LineSegment StartX=105 StartY=95 StartZ=0 EndX=105 EndY=1155 EndZ=0
    g8: LineSegment StartX=130 StartY=1105 StartZ=0 EndX=680 EndY=1105 EndZ=0
    g9: LineSegment StartX=680 StartY=1105 StartZ=0 EndX=680 EndY=145 EndZ=0
    g10: LineSegment StartX=680 StartY=145 StartZ=0 EndX=130 EndY=145 EndZ=0
    g11: LineSegment StartX=130 StartY=145 StartZ=0 EndX=130 EndY=1105 EndZ=0
    g12: LineSegment StartX=730 StartY=1105 StartZ=0 EndX=1280 EndY=1105 EndZ=0
    g13: LineSegment StartX=1280 StartY=1105 StartZ=0 EndX=1280 EndY=145 EndZ=0
    g14: LineSegment StartX=1280 StartY=145 StartZ=0 EndX=730 EndY=145 EndZ=0
    g15: LineSegment StartX=730 StartY=145 StartZ=0 EndX=730 EndY=1105 EndZ=0
    g16: LineSegment StartX=1330 StartY=1105 StartZ=0 EndX=1880 EndY=1105 EndZ=0
    g17: LineSegment StartX=1880 StartY=1105 StartZ=0 EndX=1880 EndY=145 EndZ=0
    g18: LineSegment StartX=1880 StartY=145 StartZ=0 EndX=1330 EndY=145 EndZ=0
    g19: LineSegment StartX=1330 StartY=145 StartZ=0 EndX=1330 EndY=1105 EndZ=0
    g20: LineSegment StartX=1930 StartY=1105 StartZ=0 EndX=2480 EndY=1105 EndZ=0
    g21: LineSegment StartX=2480 StartY=1105 StartZ=0 EndX=2480 EndY=145 EndZ=0
    g22: LineSegment StartX=2480 StartY=145 StartZ=0 EndX=1930 EndY=145 EndZ=0
    g23: LineSegment StartX=1930 StartY=145 StartZ=0 EndX=1930 EndY=1105 EndZ=0
  constraints (72):
    c: Coincident(g0,g1)
    c: Coincident(g1,g2)
    c: Coincident(g2,g3)
    c: Coincident(g3,g0)
    c: Horizontal(g0)
    c: Horizontal(g2)
    c: Vertical(g1)
    c: Vertical(g3)
    c: DistanceY(g-3,g0) = 0
    c: DistanceX(g-3,g0) = 2950
    c: Coincident(g4,g5)
    c: Coincident(g5,g6)
    c: Coincident(g6,g7)
    c: Coincident(g7,g4)
    c: Horizontal(g4)
    c: Horizontal(g6)
    c: Vertical(g5)
    c: Vertical(g7)
    c: Coincident(g8,g9)
    c: Coincident(g9,g10)
    c: Coincident(g10,g11)
    c: Coincident(g11,g8)
    c: Horizontal(g8)
    c: Horizontal(g10)
    c: Vertical(g9)
    c: Vertical(g11)
    c: Coincident(g12,g13)
    c: Coincident(g13,g14)
    c: Coincident(g14,g15)
    c: Coincident(g15,g12)
    c: Horizontal(g12)
    c: Horizontal(g14)
    c: Vertical(g13)
    c: Vertical(g15)
    c: Coincident(g16,g17)
    c: Coincident(g17,g18)
    c: Coincident(g18,g19)
    c: Coincident(g19,g16)
    c: Horizontal(g16)
    c: Horizontal(g18)
    c: Vertical(g17)
    c: Vertical(g19)
    c: Coincident(g20,g21)
    c: Coincident(g21,g22)
    c: Coincident(g22,g23)
    c: Coincident(g23,g20)
    c: Horizontal(g20)
    c: Horizontal(g22)
    c: Vertical(g21)
    c: Vertical(g23)
    c: Equal(g8,g12)
    c: Equal(g12,g16)
    c: Equal(g16,g20)
    c: Equal(g23,g17)
    c: Equal(g19,g13)
    c: Equal(g15,g9)
    c: DistanceY(g4,g0) = 25
    c: DistanceY(g8,g4) = 50
    c: DistanceY(g12,g8) = 0
    c: DistanceY(g16,g12) = 0
    c: DistanceY(g20,g16) = 0
    c: DistanceY(g2,g6) = 25
    c: DistanceY(g6,g10) = 50
    c: DistanceY(g3,g3) = 1110
    c: DistanceX(g2,g6) = 25
    c: DistanceX(g6,g10) = 25
    c: DistanceX(g2,g2) = 2450
    c: DistanceX(g21,g5) = 25
    c: DistanceX(g5,g1) = 25
    c: DistanceX(g17,g22) = 50
    c: DistanceX(g13,g18) = 50
    c: DistanceX(g9,g14) = 50
FEATURE [Sketcher::SketchObject] Sketch026
  ExternalGeometry = -> [Structure051]
  Placement = pos=(8410,9930,1180) rot=(0,0.707107,0.707107;3.14159rad)
  sketch-geometry (4):
    g0: LineSegment StartX=-2120 StartY=1330 StartZ=0 EndX=2680 EndY=1330 EndZ=0
    g1: LineSegment StartX=2680 StartY=1330 StartZ=0 EndX=2680 EndY=1180 EndZ=0
    g2: LineSegment StartX=2680 StartY=1180 StartZ=0 EndX=-2120 EndY=1180 EndZ=0
    g3: LineSegment StartX=-2120 StartY=1180 StartZ=0 EndX=-2120 EndY=1330 EndZ=0
  constraints (12):
    c: Coincident(g0,g1)
    c: Coincident(g1,g2)
    c: Coincident(g2,g3)
    c: Coincident(g3,g0)
    c: Horizontal(g0)
    c: Horizontal(g2)
    c: Vertical(g1)
    c: Vertical(g3)
    c: DistanceY(g3,g3) = 150
    c: DistanceY(g-3,g0) = 150
    c: DistanceX(g0,g0) = 4800
    c: DistanceX(g-3,g2) = 750
FEATURE [Part::FeaturePython] Structure080  label="SS009"  # Arch/BIM 118 (typed FeaturePython)
  Base = -> Sketch026
  FaceMaker = 0
  Height = 500
  HorizontalArea = 2.4e+06
  IfcData = IfcUID=0zLJdpvaH33utOc$yvoD5A,+2 more (map truncated)
  IfcType = 118
  Length = 0
  Material = -> Material
  MoveBase = false
  MoveWithHost = false
  Nodes = (2) [(8130,9930,2435),(8130,9930,1935)]
  NodesOffset = 0
  Normal = (0,0,0)
  PerimeterLength = 10600
  Placement = pos=(0,500,0) rot=(0,0,1;0rad)
  PredefinedType = 4
  Tag = SunShades
  VerticalArea = 1590000
  Width = 300
FEATURE [Sketcher::SketchObject] Sketch027
  ExternalGeometry = -> [Structure013]
  Placement = pos=(-5.71306,2645.54,1600) rot=(-0.576416,0.577817,0.577817;4.18739rad)
  sketch-geometry (20):
    g0: LineSegment StartX=-594.48 StartY=760 StartZ=0 EndX=1245.52 EndY=760 EndZ=0
    g1: LineSegment StartX=1245.52 StartY=760 StartZ=0 EndX=1245.52 EndY=-460 EndZ=0
    g2: LineSegment StartX=1245.52 StartY=-460 StartZ=0 EndX=-594.48 EndY=-460 EndZ=0
    g3: LineSegment StartX=-594.48 StartY=-460 StartZ=0 EndX=-594.48 EndY=760 EndZ=0
    g4: LineSegment StartX=-569.48 StartY=735 StartZ=0 EndX=1220.52 EndY=735 EndZ=0
    g5: LineSegment StartX=1220.52 StartY=735 StartZ=0 EndX=1220.52 EndY=-435 EndZ=0
    g6: LineSegment StartX=1220.52 StartY=-435 StartZ=0 EndX=-569.48 EndY=-435 EndZ=0
    g7: LineSegment StartX=-569.48 StartY=-435 StartZ=0 EndX=-569.48 EndY=735 EndZ=0
    g8: LineSegment StartX=-544.48 StartY=685 StartZ=0 EndX=-6.14714 EndY=685 EndZ=0
    g9: LineSegment StartX=-6.14714 StartY=685 StartZ=0 EndX=-6.14714 EndY=-385 EndZ=0
    g10: LineSegment StartX=-6.14714 StartY=-385 StartZ=0 EndX=-544.48 EndY=-385 EndZ=0
    g11: LineSegment StartX=-544.48 StartY=-385 StartZ=0 EndX=-544.48 EndY=685 EndZ=0
    g12: LineSegment StartX=43.8529 StartY=685 StartZ=0 EndX=582.186 EndY=685 EndZ=0
    g13: LineSegment StartX=582.186 StartY=685 StartZ=0 EndX=582.186 EndY=-385 EndZ=0
    g14: LineSegment StartX=582.186 StartY=-385 StartZ=0 EndX=43.8529 EndY=-385 EndZ=0
    g15: LineSegment StartX=43.8529 StartY=-385 StartZ=0 EndX=43.8529 EndY=685 EndZ=0
    g16: LineSegment StartX=632.186 StartY=685 StartZ=0 EndX=1170.52 EndY=685 EndZ=0
    g17: LineSegment StartX=1170.52 StartY=685 StartZ=0 EndX=1170.52 EndY=-385 EndZ=0
    g18: LineSegment StartX=1170.52 StartY=-385 StartZ=0 EndX=632.186 EndY=-385 EndZ=0
    g19: LineSegment StartX=632.186 StartY=-385 StartZ=0 EndX=632.186 EndY=685 EndZ=0
  constraints (60):
    c: Coincident(g0,g1)
    c: Coincident(g1,g2)
    c: Coincident(g2,g3)
    c: Coincident(g3,g0)
    c: Horizontal(g0)
    c: Horizontal(g2)
    c: Vertical(g1)
    c: Vertical(g3)
    c: DistanceY(g-3,g0) = 2360
    c: DistanceY(g1,g1) = 1220
    c: DistanceX(g1,g-3) = 1100
    c: DistanceX(g0,g0) = 1840
    c: Coincident(g4,g5)
    c: Coincident(g5,g6)
    c: Coincident(g6,g7)
    c: Coincident(g7,g4)
    c: Horizontal(g4)
    c: Horizontal(g6)
    c: Vertical(g5)
    c: Vertical(g7)
    c: Coincident(g8,g9)
    c: Coincident(g9,g10)
    c: Coincident(g10,g11)
    c: Coincident(g11,g8)
    c: Horizontal(g8)
    c: Horizontal(g10)
    c: Vertical(g9)
    c: Vertical(g11)
    c: Coincident(g12,g13)
    c: Coincident(g13,g14)
    c: Coincident(g14,g15)
    c: Coincident(g15,g12)
    c: Horizontal(g12)
    c: Horizontal(g14)
    c: Vertical(g13)
    c: Vertical(g15)
    c: Coincident(g16,g17)
    c: Coincident(g17,g18)
    c: Coincident(g18,g19)
    c: Coincident(g19,g16)
    c: Horizontal(g16)
    c: Horizontal(g18)
    c: Vertical(g17)
    c: Vertical(g19)
    c: DistanceY(g4,g0) = 25
    c: DistanceY(g16,g4) = 50
    c: DistanceY(g16,g12) = 0
    c: DistanceY(g12,g8) = 0
    c: DistanceY(g5,g17) = 50
    c: DistanceY(g1,g5) = 25
    c: Equal(g9,g15)
    c: Equal(g13,g19)
    c: Equal(g16,g12)
    c: Equal(g12,g8)
    c: DistanceX(g0,g4) = 25
    c: DistanceX(g4,g8) = 25
    c: DistanceX(g8,g12) = 50
    c: DistanceX(g12,g16) = 50
    c: DistanceX(g17,g5) = 50
    c: DistanceX(g5,g1) = 25
FEATURE [Sketcher::SketchObject] Sketch028
  ExternalGeometry = -> [Structure013]
  Placement = pos=(-5.71306,2645.54,1600) rot=(-0.576416,0.577817,0.577817;4.18739rad)
  sketch-geometry (4):
    g0: LineSegment StartX=-744.48 StartY=910 StartZ=0 EndX=1395.52 EndY=910 EndZ=0
    g1: LineSegment StartX=1395.52 StartY=910 StartZ=0 EndX=1395.52 EndY=760 EndZ=0
    g2: LineSegment StartX=1395.52 StartY=760 StartZ=0 EndX=-744.48 EndY=760 EndZ=0
    g3: LineSegment StartX=-744.48 StartY=760 StartZ=0 EndX=-744.48 EndY=910 EndZ=0
  constraints (12):
    c: Coincident(g0,g1)
    c: Coincident(g1,g2)
    c: Coincident(g2,g3)
    c: Coincident(g3,g0)
    c: Horizontal(g0)
    c: Horizontal(g2)
    c: Vertical(g1)
    c: Vertical(g3)
    c: DistanceY(g1,g1) = 150
    c: DistanceX(g0,g0) = 2140
    c: DistanceX(g2,g-3) = 3090
    c: DistanceY(g-3,g1) = 2360
FEATURE [Part::FeaturePython] Structure081  label="SS010"  # Arch/BIM 118 (typed FeaturePython)
  Base = -> Sketch028
  FaceMaker = 0
  Height = 500
  HorizontalArea = 1.07e+06
  IfcData = IfcUID=2$0ClTCO94QBRuUQ9$PwwG,+2 more (map truncated)
  IfcType = 118
  Length = 0
  Material = -> Material
  MoveBase = false
  MoveWithHost = false
  Nodes = (2) [(-6.50293,2320.02,2435),(-6.50293,2320.02,1935)]
  NodesOffset = 0
  Normal = (0,0,0)
  PerimeterLength = 5280
  Placement = pos=(-500,0,0) rot=(0,0,1;0rad)
  PredefinedType = 4
  Tag = SunShades
  VerticalArea = 792000
  Width = 300
FEATURE [Part::FeaturePython] Structure083  label="SS011"  # Arch/BIM 118 (typed FeaturePython)
  Base = -> Sketch029
  FaceMaker = 0
  Height = 500
  HorizontalArea = 1.07e+06
  IfcData = IfcUID=1O45g0yN94UxK1slbtZn0g,+2 more (map truncated)
  IfcType = 118
  Length = 0
  Material = -> Material
  MoveBase = false
  MoveWithHost = false
  Nodes = (2) [(-6.50293,2320.02,2435),(-6.50293,2320.02,1935)]
  NodesOffset = 0
  Normal = (0,0,0)
  PerimeterLength = 5280
  Placement = pos=(-500,4280,0) rot=(0,0,1;0rad)
  PredefinedType = 4
  Tag = SunShades
  VerticalArea = 792000
  Width = 300
FEATURE [Sketcher::SketchObject] Sketch031
  ExternalGeometry = -> [Structure012]
  Placement = pos=(2770,3.07e-12,1600) rot=(1,0,0;1.5708rad)
  sketch-geometry (16):
    g0: LineSegment StartX=-2310 StartY=760 StartZ=0 EndX=-1700 EndY=760 EndZ=0
    g1: LineSegment StartX=-1700 StartY=760 StartZ=0 EndX=-1700 EndY=-1200 EndZ=0
    g2: LineSegment StartX=-1700 StartY=-1200 StartZ=0 EndX=-2310 EndY=-1200 EndZ=0
    g3: LineSegment StartX=-2310 StartY=-1200 StartZ=0 EndX=-2310 EndY=760 EndZ=0
    g4: LineSegment StartX=-2285 StartY=735 StartZ=0 EndX=-1725 EndY=735 EndZ=0
    g5: LineSegment StartX=-1725 StartY=735 StartZ=0 EndX=-1725 EndY=-525 EndZ=0
    g6: LineSegment StartX=-1725 StartY=-525 StartZ=0 EndX=-2285 EndY=-525 EndZ=0
    g7: LineSegment StartX=-2285 StartY=-525 StartZ=0 EndX=-2285 EndY=735 EndZ=0
    g8: LineSegment StartX=-2285 StartY=-575 StartZ=0 EndX=-1725 EndY=-575 EndZ=0
    g9: LineSegment StartX=-1725 StartY=-575 StartZ=0 EndX=-1725 EndY=-1175 EndZ=0
    g10: LineSegment StartX=-1725 StartY=-1175 StartZ=0 EndX=-2285 EndY=-1175 EndZ=0
    g11: LineSegment StartX=-2285 StartY=-1175 StartZ=0 EndX=-2285 EndY=-575 EndZ=0
    g12: LineSegment StartX=-2260 StartY=685 StartZ=0 EndX=-1750 EndY=685 EndZ=0
    g13: LineSegment StartX=-1750 StartY=685 StartZ=0 EndX=-1750 EndY=-475 EndZ=0
    g14: LineSegment StartX=-1750 StartY=-475 StartZ=0 EndX=-2260 EndY=-475 EndZ=0
    g15: LineSegment StartX=-2260 StartY=-475 StartZ=0 EndX=-2260 EndY=685 EndZ=0
  constraints (48):
    c: Coincident(g0,g1)
    c: Coincident(g1,g2)
    c: Coincident(g2,g3)
    c: Coincident(g3,g0)
    c: Horizontal(g0)
    c: Horizontal(g2)
    c: Vertical(g1)
    c: Vertical(g3)
    c: Coincident(g4,g5)
    c: Coincident(g5,g6)
    c: Coincident(g6,g7)
    c: Coincident(g7,g4)
    c: Horizontal(g4)
    c: Horizontal(g6)
    c: Vertical(g5)
    c: Vertical(g7)
    c: Coincident(g8,g9)
    c: Coincident(g9,g10)
    c: Coincident(g10,g11)
    c: Coincident(g11,g8)
    c: Horizontal(g8)
    c: Horizontal(g10)
    c: Vertical(g9)
    c: Vertical(g11)
    c: Coincident(g12,g13)
    c: Coincident(g13,g14)
    c: Coincident(g14,g15)
    c: Coincident(g15,g12)
    c: Horizontal(g12)
    c: Horizontal(g14)
    c: Vertical(g13)
    c: Vertical(g15)
    c: DistanceY(g1,g1) = 1960
    c: DistanceY(g12,g4) = 50
    c: DistanceY(g5,g13) = 50
    c: DistanceY(g8,g5) = 50
    c: DistanceY(g1,g9) = 25
    c: DistanceX(g9,g1) = 25
    c: DistanceX(g5,g8) = 0
    c: DistanceX(g13,g5) = 25
    c: DistanceX(g2,g10) = 25
    c: DistanceX(g8,g6) = 0
    c: DistanceX(g6,g14) = 25
    c: DistanceX(g0,g0) = 610
    c: DistanceY(g9,g9) = 600
    c: DistanceY(g4,g0) = 25
    c: DistanceX(g-3,g2) = 160
    c: DistanceY(g-3,g2) = 400
FEATURE [Sketcher::SketchObject] Sketch032
  ExternalGeometry = -> [Structure046]
  Placement = pos=(2770,3.07e-12,1600) rot=(1,0,0;1.5708rad)
  sketch-geometry (12):
    g0: LineSegment StartX=-2310 StartY=1520 StartZ=0 EndX=-1700 EndY=1520 EndZ=0
    g1: LineSegment StartX=-1700 StartY=1520 StartZ=0 EndX=-1700 EndY=910 EndZ=0
    g2: LineSegment StartX=-1700 StartY=910 StartZ=0 EndX=-2310 EndY=910 EndZ=0
    g3: LineSegment StartX=-2310 StartY=910 StartZ=0 EndX=-2310 EndY=1520 EndZ=0
    g4: LineSegment StartX=-2285 StartY=1495 StartZ=0 EndX=-1725 EndY=1495 EndZ=0
    g5: LineSegment StartX=-1725 StartY=1495 StartZ=0 EndX=-1725 EndY=935 EndZ=0
    g6: LineSegment StartX=-1725 StartY=935 StartZ=0 EndX=-2285 EndY=935 EndZ=0
    g7: LineSegment StartX=-2285 StartY=935 StartZ=0 EndX=-2285 EndY=1495 EndZ=0
    g8: LineSegment StartX=-2260 StartY=1445 StartZ=0 EndX=-1750 EndY=1445 EndZ=0
    g9: LineSegment StartX=-1750 StartY=1445 StartZ=0 EndX=-1750 EndY=985 EndZ=0
    g10: LineSegment StartX=-1750 StartY=985 StartZ=0 EndX=-2260 EndY=985 EndZ=0
    g11: LineSegment StartX=-2260 StartY=985 StartZ=0 EndX=-2260 EndY=1445 EndZ=0
  constraints (36):
    c: Coincident(g0,g1)
    c: Coincident(g1,g2)
    c: Coincident(g2,g3)
    c: Coincident(g3,g0)
    c: Horizontal(g0)
    c: Horizontal(g2)
    c: Vertical(g1)
    c: Vertical(g3)
    c: Coincident(g4,g5)
    c: Coincident(g5,g6)
    c: Coincident(g6,g7)
    c: Coincident(g7,g4)
    c: Horizontal(g4)
    c: Horizontal(g6)
    c: Vertical(g5)
    c: Vertical(g7)
    c: Coincident(g8,g9)
    c: Coincident(g9,g10)
    c: Coincident(g10,g11)
    c: Coincident(g11,g8)
    c: Horizontal(g8)
    c: Horizontal(g10)
    c: Vertical(g9)
    c: Vertical(g11)
    c: DistanceX(g0,g0) = 610
    c: DistanceY(g1,g1) = 610
    c: DistanceY(g4,g0) = 25
    c: DistanceY(g2,g6) = 25
    c: DistanceY(g6,g10) = 50
    c: DistanceY(g8,g4) = 50
    c: DistanceX(g4,g8) = 25
    c: DistanceX(g0,g4) = 25
    c: DistanceX(g5,g1) = 25
    c: DistanceX(g9,g5) = 25
    c: DistanceX(g-3,g2) = 160
    c: DistanceY(g-3,g2) = 0
FEATURE [Sketcher::SketchObject] Sketch033
  ExternalGeometry = -> [Structure046]
  Placement = pos=(2770,3.07e-12,1600) rot=(1,0,0;1.5708rad)
  sketch-geometry (4):
    g0: LineSegment StartX=-2460 StartY=910 StartZ=0 EndX=-1560 EndY=910 EndZ=0
    g1: LineSegment StartX=-1560 StartY=910 StartZ=0 EndX=-1560 EndY=760 EndZ=0
    g2: LineSegment StartX=-1560 StartY=760 StartZ=0 EndX=-2460 EndY=760 EndZ=0
    g3: LineSegment StartX=-2460 StartY=760 StartZ=0 EndX=-2460 EndY=910 EndZ=0
  constraints (12):
    c: Coincident(g0,g1)
    c: Coincident(g1,g2)
    c: Coincident(g2,g3)
    c: Coincident(g3,g0)
    c: Horizontal(g0)
    c: Horizontal(g2)
    c: Vertical(g1)
    c: Vertical(g3)
    c: DistanceY(g1,g1) = 150
    c: DistanceX(g2,g2) = 900
    c: DistanceX(g-3,g2) = 10
    c: DistanceY(g-3,g0) = 0
FEATURE [Sketcher::SketchObject] Sketch034
  ExternalGeometry = -> [Structure046]
  Placement = pos=(2770,3.07e-12,1600) rot=(1,0,0;1.5708rad)
  sketch-geometry (12):
    g0: LineSegment StartX=870 StartY=760 StartZ=0 EndX=1480 EndY=760 EndZ=0
    g1: LineSegment StartX=1480 StartY=760 StartZ=0 EndX=1480 EndY=150 EndZ=0
    g2: LineSegment StartX=1480 StartY=150 StartZ=0 EndX=870 EndY=150 EndZ=0
    g3: LineSegment StartX=870 StartY=150 StartZ=0 EndX=870 EndY=760 EndZ=0
    g4: LineSegment StartX=895 StartY=735 StartZ=0 EndX=1455 EndY=735 EndZ=0
    g5: LineSegment StartX=1455 StartY=735 StartZ=0 EndX=1455 EndY=175 EndZ=0
    g6: LineSegment StartX=1455 StartY=175 StartZ=0 EndX=895 EndY=175 EndZ=0
    g7: LineSegment StartX=895 StartY=175 StartZ=0 EndX=895 EndY=735 EndZ=0
    g8: LineSegment StartX=920 StartY=685 StartZ=0 EndX=1430 EndY=685 EndZ=0
    g9: LineSegment StartX=1430 StartY=685 StartZ=0 EndX=1430 EndY=225 EndZ=0
    g10: LineSegment StartX=1430 StartY=225 StartZ=0 EndX=920 EndY=225 EndZ=0
    g11: LineSegment StartX=920 StartY=225 StartZ=0 EndX=920 EndY=685 EndZ=0
  constraints (36):
    c: Coincident(g0,g1)
    c: Coincident(g1,g2)
    c: Coincident(g2,g3)
    c: Coincident(g3,g0)
    c: Horizontal(g0)
    c: Horizontal(g2)
    c: Vertical(g1)
    c: Vertical(g3)
    c: Coincident(g4,g5)
    c: Coincident(g5,g6)
    c: Coincident(g6,g7)
    c: Coincident(g7,g4)
    c: Horizontal(g4)
    c: Horizontal(g6)
    c: Vertical(g5)
    c: Vertical(g7)
    c: Coincident(g8,g9)
    c: Coincident(g9,g10)
    c: Coincident(g10,g11)
    c: Coincident(g11,g8)
    c: Horizontal(g8)
    c: Horizontal(g10)
    c: Vertical(g9)
    c: Vertical(g11)
    c: DistanceX(g4,g0) = 25
    c: DistanceX(g2,g6) = 25
    c: DistanceX(g6,g10) = 25
    c: DistanceX(g9,g5) = 25
    c: DistanceX(g0,g0) = 610
    c: DistanceY(g4,g0) = 25
    c: DistanceY(g8,g4) = 50
    c: DistanceY(g5,g9) = 50
    c: DistanceY(g1,g5) = 25
    c: DistanceY(g1,g1) = 610
    c: DistanceY(g0,g-3) = 150
    c: DistanceX(g0,g-3) = 990
FEATURE [Sketcher::SketchObject] Sketch035
  ExternalGeometry = -> [Structure046]
  Placement = pos=(2770,3.07e-12,1600) rot=(1,0,0;1.5708rad)
  sketch-geometry (12):
    g0: LineSegment StartX=870 StartY=1520 StartZ=0 EndX=1480 EndY=1520 EndZ=0
    g1: LineSegment StartX=1480 StartY=1520 StartZ=0 EndX=1480 EndY=910 EndZ=0
    g2: LineSegment StartX=1480 StartY=910 StartZ=0 EndX=870 EndY=910 EndZ=0
    g3: LineSegment StartX=870 StartY=910 StartZ=0 EndX=870 EndY=1520 EndZ=0
    g4: LineSegment StartX=895 StartY=1495 StartZ=0 EndX=1455 EndY=1495 EndZ=0
    g5: LineSegment StartX=1455 StartY=1495 StartZ=0 EndX=1455 EndY=935 EndZ=0
    g6: LineSegment StartX=1455 StartY=935 StartZ=0 EndX=895 EndY=935 EndZ=0
    g7: LineSegment StartX=895 StartY=935 StartZ=0 EndX=895 EndY=1495 EndZ=0
    g8: LineSegment StartX=920 StartY=1445 StartZ=0 EndX=1430 EndY=1445 EndZ=0
    g9: LineSegment StartX=1430 StartY=1445 StartZ=0 EndX=1430 EndY=985 EndZ=0
    g10: LineSegment StartX=1430 StartY=985 StartZ=0 EndX=920 EndY=985 EndZ=0
    g11: LineSegment StartX=920 StartY=985 StartZ=0 EndX=920 EndY=1445 EndZ=0
  constraints (36):
    c: Coincident(g0,g1)
    c: Coincident(g1,g2)
    c: Coincident(g2,g3)
    c: Coincident(g3,g0)
    c: Horizontal(g0)
    c: Horizontal(g2)
    c: Vertical(g1)
    c: Vertical(g3)
    c: Coincident(g4,g5)
    c: Coincident(g5,g6)
    c: Coincident(g6,g7)
    c: Coincident(g7,g4)
    c: Horizontal(g4)
    c: Horizontal(g6)
    c: Vertical(g5)
    c: Vertical(g7)
    c: Coincident(g8,g9)
    c: Coincident(g9,g10)
    c: Coincident(g10,g11)
    c: Coincident(g11,g8)
    c: Horizontal(g8)
    c: Horizontal(g10)
    c: Vertical(g9)
    c: Vertical(g11)
    c: DistanceY(g4,g0) = 25
    c: DistanceY(g8,g4) = 50
    c: DistanceY(g5,g9) = 50
    c: DistanceY(g1,g5) = 25
    c: DistanceY(g1,g1) = 610
    c: DistanceX(g2,g6) = 25
    c: DistanceX(g6,g10) = 25
    c: DistanceX(g8,g4) = 25
    c: DistanceX(g4,g0) = 25
    c: DistanceX(g0,g0) = 610
    c: DistanceX(g1,g-3) = 990
    c: DistanceY(g-3,g1) = 0
FEATURE [Sketcher::SketchObject] Sketch036
  ExternalGeometry = -> [Structure046]
  Placement = pos=(2770,3.07e-12,1600) rot=(1,0,0;1.5708rad)
  sketch-geometry (4):
    g0: LineSegment StartX=730 StartY=910 StartZ=0 EndX=1630 EndY=910 EndZ=0
    g1: LineSegment StartX=1630 StartY=910 StartZ=0 EndX=1630 EndY=760 EndZ=0
    g2: LineSegment StartX=1630 StartY=760 StartZ=0 EndX=730 EndY=760 EndZ=0
    g3: LineSegment StartX=730 StartY=760 StartZ=0 EndX=730 EndY=910 EndZ=0
  constraints (12):
    c: Coincident(g0,g1)
    c: Coincident(g1,g2)
    c: Coincident(g2,g3)
    c: Coincident(g3,g0)
    c: Horizontal(g0)
    c: Horizontal(g2)
    c: Vertical(g1)
    c: Vertical(g3)
    c: DistanceY(g1,g1) = 150
    c: DistanceX(g0,g0) = 900
    c: DistanceY(g0,g-3) = 0
    c: DistanceX(g0,g-3) = 840
FEATURE [Part::FeaturePython] Structure084  label="SS012"  # Arch/BIM 118 (typed FeaturePython)
  Base = -> Sketch033
  FaceMaker = 0
  Height = 500
  HorizontalArea = 450000
  IfcData = IfcUID=3agCsdrxXCnO0NjdYCMPSd,+2 more (map truncated)
  IfcType = 118
  Length = 0
  Material = -> Material
  MoveBase = false
  MoveWithHost = false
  Nodes = (2) [(760,2.72017e-12,2435),(760,2.77568e-12,1935)]
  NodesOffset = 0
  Normal = (0,0,0)
  PerimeterLength = 2800
  Placement = pos=(160,-500,0) rot=(0,0,1;0rad)
  PredefinedType = 4
  Tag = SunShades
  VerticalArea = 420000
  Width = 300
FEATURE [Part::FeaturePython] Structure085  label="SS013"  # Arch/BIM 118 (typed FeaturePython)
  Base = -> Sketch036
  FaceMaker = 0
  Height = 500
  HorizontalArea = 450000
  IfcData = IfcUID=2or7rOazr5I8EMWRv_2NlN,+2 more (map truncated)
  IfcType = 118
  Length = 0
  Material = -> Material
  MoveBase = false
  MoveWithHost = false
  Nodes = (2) [(3950,2.71081e-12,2435),(3950,2.76632e-12,1935)]
  NodesOffset = 0
  Normal = (0,0,0)
  PerimeterLength = 2800
  Placement = pos=(0,-500,0) rot=(0,0,1;0rad)
  PredefinedType = 4
  Tag = SunShades
  VerticalArea = 420000
  Width = 300
FEATURE [Sketcher::SketchObject] Sketch037
  ExternalGeometry = -> [Structure020]
  Placement = pos=(13615,2.531e-12,1600) rot=(1,0,0;1.5708rad)
  sketch-geometry (16):
    g0: LineSegment StartX=-865 StartY=760 StartZ=0 EndX=205 EndY=760 EndZ=0
    g1: LineSegment StartX=205 StartY=760 StartZ=0 EndX=205 EndY=-350 EndZ=0
    g2: LineSegment StartX=205 StartY=-350 StartZ=0 EndX=-865 EndY=-350 EndZ=0
    g3: LineSegment StartX=-865 StartY=-350 StartZ=0 EndX=-865 EndY=760 EndZ=0
    g4: LineSegment StartX=-840 StartY=735 StartZ=0 EndX=180 EndY=735 EndZ=0
    g5: LineSegment StartX=180 StartY=735 StartZ=0 EndX=180 EndY=-325 EndZ=0
    g6: LineSegment StartX=180 StartY=-325 StartZ=0 EndX=-840 EndY=-325 EndZ=0
    g7: LineSegment StartX=-840 StartY=-325 StartZ=0 EndX=-840 EndY=735 EndZ=0
    g8: LineSegment StartX=-815 StartY=685 StartZ=0 EndX=-355 EndY=685 EndZ=0
    g9: LineSegment StartX=-355 StartY=685 StartZ=0 EndX=-355 EndY=-275 EndZ=0
    g10: LineSegment StartX=-355 StartY=-275 StartZ=0 EndX=-815 EndY=-275 EndZ=0
    g11: LineSegment StartX=-815 StartY=-275 StartZ=0 EndX=-815 EndY=685 EndZ=0
    g12: LineSegment StartX=-305 StartY=685 StartZ=0 EndX=155 EndY=685 EndZ=0
    g13: LineSegment StartX=155 StartY=685 StartZ=0 EndX=155 EndY=-275 EndZ=0
    g14: LineSegment StartX=155 StartY=-275 StartZ=0 EndX=-305 EndY=-275 EndZ=0
    g15: LineSegment StartX=-305 StartY=-275 StartZ=0 EndX=-305 EndY=685 EndZ=0
  constraints (48):
    c: Coincident(g0,g1)
    c: Coincident(g1,g2)
    c: Coincident(g2,g3)
    c: Coincident(g3,g0)
    c: Horizontal(g0)
    c: Horizontal(g2)
    c: Vertical(g1)
    c: Vertical(g3)
    c: Coincident(g4,g5)
    c: Coincident(g5,g6)
    c: Coincident(g6,g7)
    c: Coincident(g7,g4)
    c: Horizontal(g4)
    c: Horizontal(g6)
    c: Vertical(g5)
    c: Vertical(g7)
    c: Coincident(g8,g9)
    c: Coincident(g9,g10)
    c: Coincident(g10,g11)
    c: Coincident(g11,g8)
    c: Horizontal(g8)
    c: Horizontal(g10)
    c: Vertical(g9)
    c: Vertical(g11)
    c: Coincident(g12,g13)
    c: Coincident(g13,g14)
    c: Coincident(g14,g15)
    c: Coincident(g15,g12)
    c: Horizontal(g12)
    c: Horizontal(g14)
    c: Vertical(g13)
    c: Vertical(g15)
    c: DistanceX(g0,g0) = 1070
    c: DistanceX(g4,g8) = 25
    c: DistanceX(g12,g4) = 25
    c: DistanceY(g8,g4) = 50
    c: DistanceY(g6,g10) = 50
    c: DistanceY(g9,g14) = 0
    c: Equal(g10,g14)
    c: DistanceX(g9,g14) = 50
    c: DistanceX(g5,g1) = 25
    c: DistanceX(g2,g6) = 25
    c: DistanceY(g4,g0) = 25
    c: DistanceY(g12,g4) = 50
    c: DistanceY(g1,g5) = 25
    c: DistanceX(g1,g-3) = 1830
    c: DistanceY(g-3,g0) = 2360
    c: DistanceY(g1,g1) = 1110
FEATURE [Sketcher::SketchObject] Sketch038
  ExternalGeometry = -> [Structure047]
  Placement = pos=(13615,2.531e-12,1600) rot=(1,0,0;1.5708rad)
  sketch-geometry (4):
    g0: LineSegment StartX=-1015 StartY=910 StartZ=0 EndX=355 EndY=910 EndZ=0
    g1: LineSegment StartX=355 StartY=910 StartZ=0 EndX=355 EndY=760 EndZ=0
    g2: LineSegment StartX=355 StartY=760 StartZ=0 EndX=-1015 EndY=760 EndZ=0
    g3: LineSegment StartX=-1015 StartY=760 StartZ=0 EndX=-1015 EndY=910 EndZ=0
  constraints (12):
    c: Coincident(g0,g1)
    c: Coincident(g1,g2)
    c: Coincident(g2,g3)
    c: Coincident(g3,g0)
    c: Horizontal(g0)
    c: Horizontal(g2)
    c: Vertical(g1)
    c: Vertical(g3)
    c: DistanceY(g3,g3) = 150
    c: DistanceX(g0,g0) = 1370
    c: DistanceY(g-3,g0) = 0
    c: DistanceX(g-3,g0) = 1020
FEATURE [Part::FeaturePython] Structure086  label="SS014"  # Arch/BIM 118 (typed FeaturePython)
  Base = -> Sketch038
  FaceMaker = 0
  Height = 500
  HorizontalArea = 685000
  IfcData = IfcUID=00CE6mkCjDpQ_ZuKUMeKs0,+2 more (map truncated)
  IfcType = 118
  Length = 0
  Material = -> Material
  MoveBase = false
  MoveWithHost = false
  Nodes = (2) [(13285,2.17573e-12,2435),(13285,2.23124e-12,1935)]
  NodesOffset = 0
  Normal = (0,0,0)
  PerimeterLength = 3740
  Placement = pos=(0,-500,0) rot=(0,0,1;0rad)
  PredefinedType = 4
  Tag = SunShades
  VerticalArea = 561000
  Width = 300
FEATURE [Sketcher::SketchObject] Sketch040
  ExternalGeometry = -> [Structure045]
  Placement = pos=(8410,3650,2435) rot=(1,0,0;1.5708rad)
  sketch-geometry (12):
    g0: LineSegment StartX=-2870 StartY=-75 StartZ=0 EndX=-2370 EndY=-75 EndZ=0
    g1: LineSegment StartX=-2370 StartY=-75 StartZ=0 EndX=-2370 EndY=-2435 EndZ=0
    g2: LineSegment StartX=-2370 StartY=-2435 StartZ=0 EndX=-2870 EndY=-2435 EndZ=0
    g3: LineSegment StartX=-2870 StartY=-2435 StartZ=0 EndX=-2870 EndY=-75 EndZ=0
    g4: LineSegment StartX=-2820 StartY=-125 StartZ=0 EndX=-2420 EndY=-125 EndZ=0
    g5: LineSegment StartX=-2420 StartY=-125 StartZ=0 EndX=-2420 EndY=-1205 EndZ=0
    g6: LineSegment StartX=-2420 StartY=-1205 StartZ=0 EndX=-2820 EndY=-1205 EndZ=0
    g7: LineSegment StartX=-2820 StartY=-1205 StartZ=0 EndX=-2820 EndY=-125 EndZ=0
    g8: LineSegment StartX=-2820 StartY=-1305 StartZ=0 EndX=-2420 EndY=-1305 EndZ=0
    g9: LineSegment StartX=-2420 StartY=-1305 StartZ=0 EndX=-2420 EndY=-2385 EndZ=0
    g10: LineSegment StartX=-2420 StartY=-2385 StartZ=0 EndX=-2820 EndY=-2385 EndZ=0
    g11: LineSegment StartX=-2820 StartY=-2385 StartZ=0 EndX=-2820 EndY=-1305 EndZ=0
  constraints (35):
    c: Coincident(g0,g1)
    c: Coincident(g1,g2)
    c: Coincident(g2,g3)
    c: Coincident(g3,g0)
    c: Horizontal(g0)
    c: Horizontal(g2)
    c: Vertical(g1)
    c: Vertical(g3)
    c: Coincident(g4,g5)
    c: Coincident(g5,g6)
    c: Coincident(g6,g7)
    c: Coincident(g7,g4)
    c: Horizontal(g4)
    c: Horizontal(g6)
    c: Vertical(g5)
    c: Vertical(g7)
    c: Coincident(g8,g9)
    c: Coincident(g9,g10)
    c: Coincident(g10,g11)
    c: Coincident(g11,g8)
    c: Horizontal(g8)
    c: Vertical(g9)
    c: Vertical(g11)
    c: Equal(g5,g9)
    c: Equal(g8,g6)
    c: DistanceX(g4,g0) = 50
    c: DistanceX(g2,g10) = 50
    c: DistanceX(g8,g5) = 0
    c: DistanceY(g4,g0) = 50
    c: DistanceY(g1,g1) = 2360
    c: DistanceY(g8,g6) = 100
    c: DistanceY(g1,g9) = 50
    c: Equal(g7,g11)
    c: Coincident(g2,g-3)
    c: DistanceX(g2,g2) = 500
FEATURE [Sketcher::SketchObject] Sketch041
  ExternalGeometry = -> [Structure045]
  Placement = pos=(8410,3650,2435) rot=(1,0,0;1.5708rad)
  sketch-geometry (24):
    g0: LineSegment StartX=-2370 StartY=-75 StartZ=0 EndX=-1070 EndY=-75 EndZ=0
    g1: LineSegment StartX=-1070 StartY=-75 StartZ=0 EndX=-1070 EndY=-2435 EndZ=0
    g2: LineSegment StartX=-1070 StartY=-2435 StartZ=0 EndX=-2370 EndY=-2435 EndZ=0
    g3: LineSegment StartX=-2370 StartY=-2435 StartZ=0 EndX=-2370 EndY=-75 EndZ=0
    g4: LineSegment StartX=-2320 StartY=-125 StartZ=0 EndX=-1120 EndY=-125 EndZ=0
    g5: LineSegment StartX=-1120 StartY=-125 StartZ=0 EndX=-1120 EndY=-2435 EndZ=0
    g6: LineSegment StartX=-1120 StartY=-2435 StartZ=0 EndX=-2320 EndY=-2435 EndZ=0
    g7: LineSegment StartX=-2320 StartY=-2435 StartZ=0 EndX=-2320 EndY=-125 EndZ=0
    g8: LineSegment StartX=-2270 StartY=-225 StartZ=0 EndX=-1770 EndY=-225 EndZ=0
    g9: LineSegment StartX=-1770 StartY=-225 StartZ=0 EndX=-1770 EndY=-1230 EndZ=0
    g10: LineSegment StartX=-1770 StartY=-1230 StartZ=0 EndX=-2270 EndY=-1230 EndZ=0
    g11: LineSegment StartX=-2270 StartY=-1230 StartZ=0 EndX=-2270 EndY=-225 EndZ=0
    g12: LineSegment StartX=-2270 StartY=-1330 StartZ=0 EndX=-1770 EndY=-1330 EndZ=0
    g13: LineSegment StartX=-1770 StartY=-1330 StartZ=0 EndX=-1770 EndY=-2335 EndZ=0
    g14: LineSegment StartX=-1770 StartY=-2335 StartZ=0 EndX=-2270 EndY=-2335 EndZ=0
    g15: LineSegment StartX=-2270 StartY=-2335 StartZ=0 EndX=-2270 EndY=-1330 EndZ=0
    g16: LineSegment StartX=-1670 StartY=-1330 StartZ=0 EndX=-1170 EndY=-1330 EndZ=0
    g17: LineSegment StartX=-1170 StartY=-1330 StartZ=0 EndX=-1170 EndY=-2335 EndZ=0
    g18: LineSegment StartX=-1170 StartY=-2335 StartZ=0 EndX=-1670 EndY=-2335 EndZ=0
    g19: LineSegment StartX=-1670 StartY=-2335 StartZ=0 EndX=-1670 EndY=-1330 EndZ=0
    g20: LineSegment StartX=-1670 StartY=-225 StartZ=0 EndX=-1170 EndY=-225 EndZ=0
    g21: LineSegment StartX=-1170 StartY=-225 StartZ=0 EndX=-1170 EndY=-1230 EndZ=0
    g22: LineSegment StartX=-1170 StartY=-1230 StartZ=0 EndX=-1670 EndY=-1230 EndZ=0
    g23: LineSegment StartX=-1670 StartY=-1230 StartZ=0 EndX=-1670 EndY=-225 EndZ=0
  constraints (72):
    c: Coincident(g0,g1)
    c: Coincident(g1,g2)
    c: Coincident(g2,g3)
    c: Coincident(g3,g0)
    c: Horizontal(g0)
    c: Horizontal(g2)
    c: Vertical(g1)
    c: Vertical(g3)
    c: Coincident(g4,g5)
    c: Coincident(g5,g6)
    c: Coincident(g6,g7)
    c: Coincident(g7,g4)
    c: Horizontal(g4)
    c: Horizontal(g6)
    c: Vertical(g5)
    c: Vertical(g7)
    c: Coincident(g8,g9)
    c: Coincident(g9,g10)
    c: Coincident(g10,g11)
    c: Coincident(g11,g8)
    c: Horizontal(g8)
    c: Horizontal(g10)
    c: Vertical(g9)
    c: Vertical(g11)
    c: Coincident(g12,g13)
    c: Coincident(g13,g14)
    c: Coincident(g14,g15)
    c: Coincident(g15,g12)
    c: Horizontal(g12)
    c: Horizontal(g14)
    c: Vertical(g13)
    c: Vertical(g15)
    c: Coincident(g16,g17)
    c: Coincident(g17,g18)
    c: Coincident(g18,g19)
    c: Coincident(g19,g16)
    c: Horizontal(g16)
    c: Horizontal(g18)
    c: Vertical(g17)
    c: Vertical(g19)
    c: Coincident(g20,g21)
    c: Coincident(g21,g22)
    c: Coincident(g22,g23)
    c: Coincident(g23,g20)
    c: Horizontal(g20)
    c: Horizontal(g22)
    c: Vertical(g21)
    c: Vertical(g23)
    c: DistanceY(g8,g4) = 100
    c: DistanceY(g4,g0) = 50
    c: DistanceY(g20,g4) = 100
    c: DistanceY(g2,g6) = 0
    c: DistanceY(g6,g14) = 100
    c: DistanceY(g13,g18) = 0
    c: DistanceY(g12,g10) = 100
    c: Equal(g9,g23)
    c: Equal(g13,g19)
    c: Equal(g19,g23)
    c: Equal(g10,g12)
    c: Equal(g22,g12)
    c: DistanceX(g9,g22) = 100
    c: DistanceX(g12,g9) = 0
    c: DistanceX(g22,g16) = 0
    c: DistanceX(g6,g14) = 50
    c: DistanceX(g2,g6) = 50
    c: DistanceX(g17,g5) = 50
    c: DistanceX(g5,g1) = 50
    c: DistanceX(g21,g16) = 0
    c: DistanceY(g1,g1) = 2360
    c: DistanceY(g2,g-3) = 0
    c: DistanceX(g-3,g2) = 500
    c: DistanceX(g0,g0) = 1300
FEATURE [Part::FeaturePython] Structure101  label="C013"  # Arch/BIM 24 (typed FeaturePython)
  FaceMaker = 0
  Height = 5000
  HorizontalArea = 90000
  IfcData = IfcUID=2F5ytiBMf8sxp0X56oiqUB,+2 more (map truncated)
  IfcType = 24
  Length = 300
  Material = -> Material
  MoveBase = false
  MoveWithHost = false
  Nodes = (2) [(5.55112e-16,1.51582e-15,0),(5.55112e-16,1.51582e-15,5000)]
  NodesOffset = 0
  Normal = (0,0,0)
  PerimeterLength = 1200
  Placement = pos=(11430,5150,-1500) rot=(0,0,1;0rad)
  PredefinedType = 0
  VerticalArea = 6000000
  Width = 300
FEATURE [Part::FeaturePython] Structure102  label="C014"  # Arch/BIM 24 (typed FeaturePython)
  FaceMaker = 0
  Height = 5000
  HorizontalArea = 90000
  IfcData = IfcUID=2UlXUGwxrE$hzs8VWFkPi_,+2 more (map truncated)
  IfcType = 24
  Length = 300
  Material = -> Material
  MoveBase = false
  MoveWithHost = false
  Nodes = (2) [(5.55112e-16,1.51582e-15,0),(5.55112e-16,1.51582e-15,5000)]
  NodesOffset = 0
  Normal = (0,0,0)
  PerimeterLength = 1200
  Placement = pos=(5390,5150,-1500) rot=(0,0,1;0rad)
  PredefinedType = 0
  VerticalArea = 6000000
  Width = 300
FEATURE [Part::FeaturePython] Structure104  label="B119"  # Arch/BIM 7 (typed FeaturePython)
  FaceMaker = 0
  Height = 450
  HorizontalArea = 1.41e+06
  IfcData = IfcUID=26egLidy9FXA8fIYYZf8F2,+2 more (map truncated)
  IfcType = 7
  Length = 4700
  Material = -> Material
  MoveBase = false
  MoveWithHost = false
  Nodes = (2) [(-4.93038e-32,0,-2.22045e-16),(-4.93038e-32,0,4700)]
  NodesOffset = 0
  Normal = (0,0,0)
  PerimeterLength = 10000
  Placement = pos=(11430,300,-225) rot=(0,0,1;1.5708rad)
  PredefinedType = 0
  VerticalArea = 4500000
  Width = 300
FEATURE [Part::FeaturePython] Structure107  label="B122"  # Arch/BIM 7 (typed FeaturePython)
  FaceMaker = 0
  Height = 450
  HorizontalArea = 1.41e+06
  IfcData = IfcUID=0O4HMTYL9E0OuSUfEDbJYr,+2 more (map truncated)
  IfcType = 7
  Length = 4700
  Material = -> Material
  MoveBase = false
  MoveWithHost = false
  Nodes = (2) [(-4.93038e-32,0,-2.22045e-16),(-4.93038e-32,0,4700)]
  NodesOffset = 0
  Normal = (0,0,0)
  PerimeterLength = 10000
  Placement = pos=(5390,300,-225) rot=(0,0,1;1.5708rad)
  PredefinedType = 0
  VerticalArea = 4500000
  Width = 300
FEATURE [Part::FeaturePython] Structure108  label="B123"  # Arch/BIM 7 (typed FeaturePython)
  FaceMaker = 0
  Height = 450
  HorizontalArea = 1.482e+06
  IfcData = IfcUID=1ga8oLsDr2fw1lmAxqPDj4,+2 more (map truncated)
  IfcType = 7
  Length = 4940
  Material = -> Material
  MoveBase = false
  MoveWithHost = false
  Nodes = (2) [(-4.93038e-32,0,-2.22045e-16),(-4.93038e-32,0,4940)]
  NodesOffset = 0
  Normal = (0,0,0)
  PerimeterLength = 10480
  Placement = pos=(300,5150,-225) rot=(0,0,1;0rad)
  PredefinedType = 0
  VerticalArea = 4716000
  Width = 300
FEATURE [Part::FeaturePython] Structure110  label="B125"  # Arch/BIM 7 (typed FeaturePython)
  FaceMaker = 0
  Height = 450
  HorizontalArea = 1.299e+06
  IfcData = IfcUID=0h6Joy0l52POMmYk4hvn2h,+2 more (map truncated)
  IfcType = 7
  Length = 4330
  Material = -> Material
  MoveBase = false
  MoveWithHost = false
  Nodes = (2) [(-4.93038e-32,0,-2.22045e-16),(-4.93038e-32,0,4330)]
  NodesOffset = 0
  Normal = (0,0,0)
  PerimeterLength = 9260
  Placement = pos=(11430,9630,-225) rot=(0,0,-1;1.5708rad)
  PredefinedType = 0
  VerticalArea = 4.167e+06
  Width = 300
FEATURE [Part::FeaturePython] Structure111  label="B126"  # Arch/BIM 7 (typed FeaturePython)
  FaceMaker = 0
  Height = 450
  HorizontalArea = 1.221e+06
  IfcData = IfcUID=2$HofyK1b85RcR1Q6RpbOM,+2 more (map truncated)
  IfcType = 7
  Length = 4070
  Material = -> Material
  MoveBase = false
  MoveWithHost = false
  Nodes = (2) [(-4.93038e-32,0,-2.22045e-16),(-4.93038e-32,0,4070)]
  NodesOffset = 0
  Normal = (0,0,0)
  PerimeterLength = 8740
  Placement = pos=(11580,5150,-225) rot=(0,0,1;0rad)
  PredefinedType = 0
  VerticalArea = 3.933e+06
  Width = 300
FEATURE [Part::FeaturePython] Structure112  label="B127"  # Arch/BIM 7 (typed FeaturePython)
  FaceMaker = 0
  Height = 450
  HorizontalArea = 1.299e+06
  IfcData = IfcUID=2DsWzYmn10JBJaBx2iY9mU,+2 more (map truncated)
  IfcType = 7
  Length = 4330
  Material = -> Material
  MoveBase = false
  MoveWithHost = false
  Nodes = (2) [(-4.93038e-32,0,-2.22045e-16),(-4.93038e-32,0,4330)]
  NodesOffset = 0
  Normal = (0,0,0)
  PerimeterLength = 9260
  Placement = pos=(5390,9630,-225) rot=(0,0,-1;1.5708rad)
  PredefinedType = 0
  VerticalArea = 4.167e+06
  Width = 300
FEATURE [Part::FeaturePython] Structure113  label="B128"  # Arch/BIM 7 (typed FeaturePython)
  FaceMaker = 0
  Height = 450
  HorizontalArea = 1.722e+06
  IfcData = IfcUID=1gZYNi6KX3curW$XNQj7mG,+2 more (map truncated)
  IfcType = 7
  Length = 5740
  Material = -> Material
  MoveBase = false
  MoveWithHost = false
  Nodes = (2) [(-4.93038e-32,0,-2.22045e-16),(-4.93038e-32,0,5740)]
  NodesOffset = 0
  Normal = (0,0,0)
  PerimeterLength = 12080
  Placement = pos=(5540,5150,-225) rot=(0,0,1;0rad)
  PredefinedType = 0
  VerticalArea = 5.436e+06
  Width = 300
FEATURE [Part::FeaturePython] Structure119  label="Ramp"  # Arch/BIM 108 (typed FeaturePython)
  Base = -> Sketch052
  FaceMaker = 0
  Height = 1500
  HorizontalArea = 0
  IfcData = IfcUID=24Yg8xy$n6KxfLENMuftgK,+2 more (map truncated)
  IfcType = 108
  Length = 0
  Material = -> Material
  MoveBase = false
  MoveWithHost = false
  Nodes = (2) [(5540,1650,-300),(5540,1650,1200)]
  NodesOffset = 0
  Normal = (0,0,0)
  PerimeterLength = 13500
  Placement = pos=(400,0,0) rot=(0,0,1;0rad)
  PredefinedType = 0
  VerticalArea = 3375000
  Width = 300
FEATURE [Sketcher::SketchObject] Sketch054
  ExternalGeometry = -> [Structure001]
  Placement = pos=(5390,0,1000) rot=(1,0,0;1.5708rad)
  sketch-geometry (4):
    g0: LineSegment StartX=-80 StartY=1360 StartZ=0 EndX=-80 EndY=1860 EndZ=0
    g1: LineSegment StartX=-80 StartY=1860 StartZ=0 EndX=1120 EndY=1560 EndZ=0
    g2: LineSegment StartX=1120 StartY=1560 StartZ=0 EndX=1120 EndY=1360 EndZ=0
    g3: LineSegment StartX=1120 StartY=1360 StartZ=0 EndX=-80 EndY=1360 EndZ=0
  constraints (12):
    c: Vertical(g0)
    c: Coincident(g0,g1)
    c: Coincident(g1,g2)
    c: Coincident(g2,g3)
    c: Coincident(g3,g0)
    c: Horizontal(g3)
    c: Vertical(g2)
    c: DistanceY(g2,g2) = 200
    c: DistanceX(g3,g3) = 1200
    c: DistanceY(g0,g0) = 500
    c: DistanceY(g-3,g0) = 3860
    c: DistanceX(g-3,g0) = -230
FEATURE [Part::FeaturePython] Structure121  label="Cantilever Beam"  # Arch/BIM 7 (typed FeaturePython)
  Base = -> Sketch054
  FaceMaker = 0
  Height = 260
  HorizontalArea = 0
  IfcData = IfcUID=3lVKRYntH4rvVg$ixQQYMQ,+2 more (map truncated)
  IfcType = 7
  Length = 0
  Material = -> Material
  MoveBase = false
  MoveWithHost = false
  Nodes = (2) [(5824.29,-2.22045e-13,2545.71),(5824.29,-1.93179e-13,2285.71)]
  NodesOffset = 0
  Normal = (0,0,0)
  PerimeterLength = 2660
  Placement = pos=(0,430,0) rot=(0,0,1;0rad)
  PredefinedType = 0
  Subtractions = -> [Structure055]
  Tag = Cantilever
  VerticalArea = 1022000
  Width = 300
FEATURE [Sketcher::SketchObject] Sketch056
  ExternalGeometry = -> [Structure022,Structure013,Structure016,Structure017]
  Placement = pos=(5390,7465,0) rot=(0,0,1;3.14159rad)
  sketch-geometry (9):
    g0: LineSegment StartX=0 StartY=3872.5 StartZ=0 EndX=4090 EndY=3872.5 EndZ=0
    g1: LineSegment StartX=0 StartY=0 StartZ=0 EndX=5240 EndY=0 EndZ=0
    g2: LineSegment StartX=-3050 StartY=2315 StartZ=0 EndX=-3050 EndY=-2315 EndZ=0
    g3: LineSegment StartX=-10410 StartY=-815 StartZ=0 EndX=-6040 EndY=-815 EndZ=0
    g4: LineSegment StartX=0 StartY=3872.5 StartZ=0 EndX=0 EndY=-2315 EndZ=0
    g5: LineSegment StartX=2500 StartY=6165 StartZ=0 EndX=2500 EndY=3872.5 EndZ=0
    g6: LineSegment StartX=-8225 StartY=-815 StartZ=0 EndX=-8225 EndY=-2315 EndZ=0
    g7: LineSegment StartX=-10410 StartY=2315 StartZ=0 EndX=0 EndY=2315 EndZ=0
    g8: LineSegment StartX=-6040 StartY=-2315 StartZ=0 EndX=-6040 EndY=3872.5 EndZ=0
  constraints (34):
    c: Horizontal(g0)
    c: DistanceX(g0,g-3) = 150
    c: DistanceY(g-3,g0) = 1407.5
    c: Coincident(g1,g-1)
    c: PointOnObject(g1,g-1)
    c: DistanceX(g-4,g1) = 150
    c: Vertical(g2)
    c: DistanceX(g2,g-3) = 2900
    c: DistanceY(g1,g2) = 2315
    c: DistanceY(g2,g1) = 2315
    c: Horizontal(g3)
    c: DistanceX(g3,g-5) = 150
    c: DistanceX(g3,g-6) = 150
    c: DistanceY(g-5,g3) = 1350
    c: Coincident(g4,g0)
    c: PointOnObject(g4,g-2)
    c: PointOnObject(g5,g0)
    c: Vertical(g5)
    c: PointOnObject(g6,g3)
    c: Vertical(g6)
    c: PointOnObject(g7,g4)
    c: Horizontal(g7)
    c: Vertical(g8)
    c: DistanceX(g7,g3) = 0
    c: DistanceY(g0,g8) = 0
    c: DistanceX(g0,g5) = 2500
    c: DistanceY(g7,g-3) = 150
    c: DistanceY(g4,g8) = 0
    c: DistanceY(g6,g8) = 0
    c: DistanceY(g8,g-5) = 150
    c: DistanceX(g6,g3) = 2185
    c: DistanceX(g8,g-5) = 150
    c: DistanceY(g5,g-7) = 1000
    c: DistanceX(g0,g-4) = 1000
FEATURE [App::MaterialObjectPython] Material001  label="Wood"  # material (typed FeaturePython)
  Description = A standard construction wood
  Material = AuthorAndLicense=Wood-Generic,CardName=Wood-Generic,Color=(0.5058823529411764, 0.25098039215686274, 0.0),Density=700 kg/m^3,+9 more (map truncated)
  ProductURL = https://en.wikipedia.org/wiki/Wood
  Transparency = 0
FEATURE [Part::FeaturePython] Window026  # Arch/BIM 170 (typed FeaturePython)
  Area = 0
  Base = -> Sketch040
  Frame = 0
  Height = 0
  HoleDepth = 0
  HoleWire = 0
  HorizontalArea = 0
  IfcData = IfcUID=21FxfVf9j1EgtyFw_5Mlb0,+2 more (map truncated)
  IfcType = 170
  LouvreSpacing = 0
  LouvreWidth = 0
  Material = -> Material001
  MoveBase = false
  MoveWithHost = true
  Normal = (0,1,-2e-16)
  Opening = 0
  OverallHeight = 0
  OverallWidth = 0
  PartitioningType = 0
  PerimeterLength = 0
  PredefinedType = 0
  Preset = 0
  SymbolElevation = false
  SymbolPlan = false
  VerticalArea = 0
  Width = 0
  WindowParts = Default | Frame | Wire0,Wire1,Wire2 | 50.0 | 0.0 | g1 | Glass panel | Wire1 | 5.0 | 10.0 | g2 | Glass panel | Wire2 | 5.0 | 10.0
  expr: OverallHeight = .Height.Value
  expr: OverallWidth = .Width.Value
FEATURE [Part::FeaturePython] Window027  label="Door_Main"  # Arch/BIM 41 (typed FeaturePython)
  Area = 0
  Base = -> Sketch041
  Frame = 0
  Height = 0
  HoleDepth = 0
  HoleWire = 0
  HorizontalArea = 0
  IfcData = IfcUID=01zPN4nnf1JfsNShT9JZzB,+2 more (map truncated)
  IfcType = 41
  LouvreSpacing = 0
  LouvreWidth = 0
  Material = -> Material001
  MoveBase = false
  MoveWithHost = true
  Normal = (0,1,-2e-16)
  Opening = 0
  OperationType = 7
  OverallHeight = 0
  OverallWidth = 0
  PerimeterLength = 0
  PredefinedType = 0
  Preset = 0
  SymbolElevation = false
  SymbolPlan = false
  VerticalArea = 0
  Width = 0
  WindowParts = f1 | Frame | Wire0,Wire1 | 50.0 | 0.0 | f2 | Frame | Wire1,Wire2,Wire3,Wire4,Wire5 | 30.0 | 10.0 | g1 | Glass panel | Wire2 | 5.0 | 15.0 | g2 | Glass panel | Wire3 | 5.0 | 15.0 | g3 | Glass panel | Wire4 | 5.0 | 15.0 | g4 | Glass panel | Wire5 | 5.0 | 15.0
  expr: OverallHeight = .Height.Value
  expr: OverallWidth = .Width.Value
FEATURE [Part::FeaturePython] Window030  label="Door002"  # Arch/BIM 41 (typed FeaturePython)
  Area = 3000000
  Base = -> Sketch061
  Frame = 50
  Height = 2000
  HoleDepth = 0
  HoleWire = 0
  HorizontalArea = 0
  Hosts = -> [Structure025]
  IfcData = IfcUID=3txhQ965zBkPHs6$wknd$W,+2 more (map truncated)
  IfcType = 41
  LouvreSpacing = 0
  LouvreWidth = 0
  Material = -> Material001
  MoveBase = false
  MoveWithHost = true
  Normal = (-1e-16,1,2e-16)
  Opening = 0
  OperationType = 0
  OverallHeight = 2000
  OverallWidth = 1500
  PerimeterLength = 0
  Placement = pos=(500,0,0) rot=(0,0,1;0rad)
  PredefinedType = 0
  Preset = 6
  SymbolElevation = false
  SymbolPlan = false
  VerticalArea = 0
  Width = 1500
  WindowParts = OuterFrame | Frame | Wire0,Wire1 | 50.0+V | 0.0+V | Door | Glass panel | Wire1 | 5.0 | 10.0+V
  expr: OverallHeight = .Height.Value
  expr: OverallWidth = .Width.Value
FEATURE [Part::FeaturePython] Window034  label="Door006"  # Arch/BIM 41 (typed FeaturePython)
  Area = 2000000
  Base = -> Sketch067
  Frame = 50
  Height = 2000
  HoleDepth = 0
  HoleWire = 0
  HorizontalArea = 0
  IfcData = IfcUID=2HTdm2dJX4jBVrvwG0awmP,+2 more (map truncated)
  IfcType = 41
  LouvreSpacing = 0
  LouvreWidth = 0
  Material = -> Material001
  MoveBase = false
  MoveWithHost = true
  Normal = (0,1,-2e-16)
  Opening = 0
  OperationType = 0
  OverallHeight = 2000
  OverallWidth = 1000
  PerimeterLength = 0
  Placement = pos=(3000,-50,0) rot=(0,0,1;0rad)
  PredefinedType = 0
  Preset = 6
  SymbolElevation = false
  SymbolPlan = false
  VerticalArea = 0
  Width = 1000
  WindowParts = OuterFrame | Frame | Wire0,Wire1 | 50.0+V | 0.0+V | Door | Solid panel | Wire1 | 5.0 | 10.0+V
  expr: OverallWidth = .Width.Value
  expr: OverallHeight = .Height.Value
FEATURE [App::MaterialObjectPython] Material002  label="Brick Massonary"  # material (typed FeaturePython)
  Description = Reinforcement inside concrete for reinforcement material examples, from fib examples, 0.84 x 0.75 x 500 MPa = 315 MPa (https://forum.freecadweb.org/viewtopic.php?f=18&t=33106&start=200#p311705)
  Material = AuthorAndLicense=Reinforcement-FIB-B500,CardName=Reinforcement-FIB-B500,Color=(0.8313725490196079, 0.0392156862745098, 0.0392156862745098),+10 more (map truncated)
  Transparency = 0
FEATURE [Part::FeaturePython] Wall  label="W001"  # Arch/BIM 166 (typed FeaturePython)
  Align = 1
  Area = 15808000
  Base = -> WallTrace
  BlockHeight = 76
  BlockLength = 228
  CountBroken = 215
  CountEntire = 508
  Face = 0
  Height = 3200
  HorizontalArea = 0
  IfcData = IfcUID=0Iuc33rj5CDhXNsDZVpb$k,+2 more (map truncated)
  IfcType = 166
  Joint = 10
  Length = 4940
  MakeBlocks = false
  Material = -> Material002
  MoveBase = false
  MoveWithHost = false
  Normal = (0,0,1)
  OffsetFirst = 114
  OffsetSecond = 0
  PerimeterLength = 0
  PredefinedType = 0
  Subtractions = -> [Structure046]
  VerticalArea = 0
  Width = 230
FEATURE [Part::FeaturePython] Wall001  label="W002"  # Arch/BIM 166 (typed FeaturePython)
  Align = 1
  Area = 13024000
  Base = -> WallTrace001
  BlockHeight = 76
  BlockLength = 228
  CountBroken = 147
  CountEntire = 473
  Face = 0
  Height = 3200
  HorizontalArea = 1.8722e+06
  IfcData = IfcUID=05vapYtHbFN96aaLN5kylk,+2 more (map truncated)
  IfcType = 166
  Joint = 10
  Length = 4070
  MakeBlocks = false
  Material = -> Material002
  MoveBase = false
  MoveWithHost = false
  Normal = (0,0,1)
  OffsetFirst = 114
  OffsetSecond = 0
  PerimeterLength = 0
  PredefinedType = 0
  Subtractions = -> [Structure047]
  VerticalArea = 24365200
  Width = 230
FEATURE [Part::FeaturePython] Wall002  label="W003"  # Arch/BIM 166 (typed FeaturePython)
  Align = 1
  Area = 15040000
  Base = -> WallTrace003
  BlockHeight = 76
  BlockLength = 228
  CountBroken = 290
  CountEntire = 316
  Face = 0
  Height = 3200
  HorizontalArea = 0
  IfcData = IfcUID=2MccvPPwf32u1LM8zJLOkZ,+2 more (map truncated)
  IfcType = 166
  Joint = 10
  Length = 4700
  MakeBlocks = false
  Material = -> Material002
  MoveBase = false
  MoveWithHost = false
  Normal = (0,0,1)
  OffsetFirst = 114
  OffsetSecond = 0
  PerimeterLength = 0
  PredefinedType = 0
  Subtractions = -> [Structure048]
  VerticalArea = 0
  Width = 230
FEATURE [Part::FeaturePython] Wall003  label="W004"  # Arch/BIM 166 (typed FeaturePython)
  Align = 1
  Area = 13856000
  Base = -> WallTrace004
  BlockHeight = 76
  BlockLength = 228
  CountBroken = 200
  CountEntire = 448
  Face = 0
  Height = 3200
  HorizontalArea = 0
  IfcData = IfcUID=0SEP4GGi17PxyzPFV7UtYJ,+2 more (map truncated)
  IfcType = 166
  Joint = 10
  Length = 4330
  MakeBlocks = false
  Material = -> Material002
  MoveBase = false
  MoveWithHost = false
  Normal = (0,0,1)
  OffsetFirst = 114
  OffsetSecond = 0
  PerimeterLength = 0
  PredefinedType = 0
  Subtractions = -> [Structure049]
  VerticalArea = 0
  Width = 230
FEATURE [Part::FeaturePython] Wall005  label="W006"  # Arch/BIM 166 (typed FeaturePython)
  Align = 1
  Area = 18368000
  Base = -> WallTrace006
  BlockHeight = 76
  BlockLength = 228
  CountBroken = 195
  CountEntire = 522
  Face = 0
  Height = 3200
  HorizontalArea = 2.6404e+06
  IfcData = IfcUID=35kFBDyj51k9$CSriaklV9,+2 more (map truncated)
  IfcType = 166
  Joint = 10
  Length = 5740
  MakeBlocks = false
  Material = -> Material002
  MoveBase = false
  MoveWithHost = false
  Normal = (0,0,1)
  OffsetFirst = 114
  OffsetSecond = 0
  PerimeterLength = 0
  PredefinedType = 0
  Subtractions = -> [Structure051]
  VerticalArea = 27958800
  Width = 230
FEATURE [Part::FeaturePython] Wall006  label="W007"  # Arch/BIM 166 (typed FeaturePython)
  Align = 1
  Area = 1.5808e+07
  Base = -> WallTrace007
  BlockHeight = 76
  BlockLength = 228
  CountBroken = 161
  CountEntire = 614
  Face = 0
  Height = 3200
  HorizontalArea = 2.2724e+06
  IfcData = IfcUID=1cWHg871jEtgY0EttTH$We,+2 more (map truncated)
  IfcType = 166
  Joint = 10
  Length = 4940
  MakeBlocks = false
  Material = -> Material002
  MoveBase = false
  MoveWithHost = false
  Normal = (0,0,1)
  OffsetFirst = 114
  OffsetSecond = 0
  PerimeterLength = 0
  PredefinedType = 0
  Subtractions = -> [Structure052]
  VerticalArea = 3.06098e+07
  Width = 230
FEATURE [Part::FeaturePython] Wall007  label="W008"  # Arch/BIM 166 (typed FeaturePython)
  Align = 1
  Area = 13856000
  Base = -> WallTrace008
  BlockHeight = 76
  BlockLength = 228
  CountBroken = 153
  CountEntire = 452
  Face = 0
  Height = 3200
  HorizontalArea = 1.9918e+06
  IfcData = IfcUID=3rSJteeYz4KvHn7D_3AGMp,+2 more (map truncated)
  IfcType = 166
  Joint = 10
  Length = 4330
  MakeBlocks = false
  Material = -> Material002
  MoveBase = false
  MoveWithHost = false
  Normal = (0,0,1)
  OffsetFirst = 114
  OffsetSecond = 0
  PerimeterLength = 0
  PredefinedType = 0
  Subtractions = -> [Structure053]
  VerticalArea = 2.38876e+07
  Width = 230
FEATURE [Part::FeaturePython] Wall009  label="W010"  # Arch/BIM 166 (typed FeaturePython)
  Align = 1
  Area = 11680000
  Base = -> WallTrace012
  BlockHeight = 76
  BlockLength = 228
  CountBroken = 122
  CountEntire = 470
  Face = 0
  Height = 3200
  HorizontalArea = 1679000
  IfcData = IfcUID=1ksKarJwr3if1ua0A02gqY,+2 more (map truncated)
  IfcType = 166
  Joint = 10
  Length = 3650
  MakeBlocks = false
  Material = -> Material002
  MoveBase = false
  MoveWithHost = false
  Normal = (0,0,1)
  OffsetFirst = 114
  OffsetSecond = 0
  PerimeterLength = 0
  PredefinedType = 0
  Subtractions = -> [Structure055,Structure057,Structure121]
  VerticalArea = 2.36487e+07
  Width = 230
FEATURE [Part::FeaturePython] Wall011  label="W011"  # Arch/BIM 166 (typed FeaturePython)
  Align = 1
  Area = 11680000
  Base = -> WallTrace014
  BlockHeight = 76
  BlockLength = 228
  CountBroken = 116
  CountEntire = 476
  Face = 0
  Height = 3200
  HorizontalArea = 1.679e+06
  IfcData = IfcUID=3FvVaLwef90fDN$sGXz$KF,+2 more (map truncated)
  IfcType = 166
  Joint = 10
  Length = 3650
  MakeBlocks = false
  Material = -> Material002
  MoveBase = false
  MoveWithHost = false
  Normal = (0,0,1)
  OffsetFirst = 114
  OffsetSecond = 0
  PerimeterLength = 0
  PredefinedType = 0
  Subtractions = -> [Structure056,Structure057]
  VerticalArea = 2.3668e+07
  Width = 230
FEATURE [Part::FeaturePython] Window  label="W1"  # Arch/BIM 170 (typed FeaturePython)
  Area = 0
  Base = -> Sketch
  Frame = 0
  Height = 0
  HoleDepth = 0
  HoleWire = 0
  HorizontalArea = 0
  Hosts = -> [Wall002]
  IfcData = IfcUID=1zRywYm0z3PB1t2DguVqE3,+2 more (map truncated)
  IfcType = 170
  LouvreSpacing = 0
  LouvreWidth = 0
  Material = -> Material001
  MoveBase = false
  MoveWithHost = true
  Normal = (-1,-2e-16,2e-16)
  Opening = 0
  OverallHeight = 0
  OverallWidth = 0
  PartitioningType = 0
  PerimeterLength = 0
  Placement = pos=(0,160,0) rot=(0,0,1;0rad)
  PredefinedType = 0
  Preset = 0
  SymbolElevation = false
  SymbolPlan = false
  VerticalArea = 0
  Width = 0
  WindowParts = w1 | Frame | Wire0,Wire1,Wire2 | 50.0 | 150.0 | W2 | Frame | Wire3,Wire2 | 30.0 | 160.0 | g1 | Glass panel | Wire3 | 5.0 | 165.0 | g2 | Glass panel | Wire1 | 5.0 | 165.0
  expr: OverallHeight = .Height.Value
  expr: OverallWidth = .Width.Value
FEATURE [Part::FeaturePython] Window001  label="W2"  # Arch/BIM 170 (typed FeaturePython)
  Area = 0
  Base = -> Sketch001
  Frame = 0
  Height = 0
  HoleDepth = 0
  HoleWire = 0
  HorizontalArea = 0
  Hosts = -> [Wall002]
  IfcData = IfcUID=2PgqGHWm93GvTqmF3H4ub9,+2 more (map truncated)
  IfcType = 170
  LouvreSpacing = 0
  LouvreWidth = 0
  Material = -> Material001
  MoveBase = false
  MoveWithHost = true
  Normal = (-1,-2e-16,2e-16)
  Opening = 0
  OverallHeight = 0
  OverallWidth = 0
  PartitioningType = 0
  PerimeterLength = 0
  Placement = pos=(0,1810,0) rot=(0,0,1;0rad)
  PredefinedType = 0
  Preset = 0
  SymbolElevation = false
  SymbolPlan = false
  VerticalArea = 0
  Width = 0
  WindowParts = w1 | Frame | Wire0,Wire1,Wire2 | 50.0 | 150.0 | W2 | Frame | Wire3,Wire2 | 30.0 | 160.0 | g1 | Glass panel | Wire3 | 5.0 | 165.0 | g2 | Glass panel | Wire1 | 5.0 | 165.0
  expr: OverallWidth = .Width.Value
  expr: OverallHeight = .Height.Value
FEATURE [Part::FeaturePython] Window002  label="W3"  # Arch/BIM 170 (typed FeaturePython)
  Area = 0
  Base = -> Sketch002
  Frame = 0
  Height = 0
  HoleDepth = 0
  HoleWire = 0
  HorizontalArea = 0
  Hosts = -> [Wall002]
  IfcData = IfcUID=398FkjKQX3uQ1xmljl8ZPI,+2 more (map truncated)
  IfcType = 170
  LouvreSpacing = 0
  LouvreWidth = 0
  Material = -> Material001
  MoveBase = false
  MoveWithHost = true
  Normal = (-1,-2e-16,2e-16)
  Opening = 0
  OverallHeight = 0
  OverallWidth = 0
  PartitioningType = 0
  PerimeterLength = 0
  Placement = pos=(0,3650,0) rot=(0,0,1;0rad)
  PredefinedType = 0
  Preset = 0
  SymbolElevation = false
  SymbolPlan = false
  VerticalArea = 0
  Width = 0
  WindowParts = w1 | Frame | Wire0,Wire1,Wire2 | 50.0 | 150.0 | W2 | Frame | Wire3,Wire2 | 30.0 | 160.0 | g1 | Glass panel | Wire3 | 5.0 | 165.0 | g2 | Glass panel | Wire1 | 5.0 | 165.0
  expr: OverallWidth = .Width.Value
  expr: OverallHeight = .Height.Value
FEATURE [Part::FeaturePython] Window003  label="W4"  # Arch/BIM 170 (typed FeaturePython)
  Area = 0
  Base = -> Sketch003
  Frame = 0
  Height = 0
  HoleDepth = 0
  HoleWire = 0
  HorizontalArea = 0
  Hosts = -> [Wall003]
  IfcData = IfcUID=2uTSPhbrTEMxMwdwP$cYH9,+2 more (map truncated)
  IfcType = 170
  LouvreSpacing = 0
  LouvreWidth = 0
  Material = -> Material001
  MoveBase = false
  MoveWithHost = true
  Normal = (-1,-2e-16,2e-16)
  Opening = 0
  OverallHeight = 0
  OverallWidth = 0
  PartitioningType = 0
  PerimeterLength = 0
  Placement = pos=(0,5440,0) rot=(0,0,1;0rad)
  PredefinedType = 0
  Preset = 0
  SymbolElevation = false
  SymbolPlan = false
  VerticalArea = 0
  Width = 0
  WindowParts = w1 | Frame | Wire0,Wire1,Wire2 | 50.0 | 150.0 | W2 | Frame | Wire3,Wire2 | 30.0 | 160.0 | g1 | Glass panel | Wire3 | 5.0 | 165.0 | g2 | Glass panel | Wire1 | 5.0 | 165.0
  expr: OverallWidth = .Width.Value
  expr: OverallHeight = .Height.Value
FEATURE [Sketcher::SketchObject] Sketch004
  ExternalGeometry = -> [Wall002]
  Placement = pos=(15950,2650,1600) rot=(0.57735,0.57735,0.57735;2.0944rad)
  sketch-geometry (12):
    g0: LineSegment StartX=4920 StartY=760 StartZ=0 EndX=5530 EndY=760 EndZ=0
    g1: LineSegment StartX=5530 StartY=760 StartZ=0 EndX=5530 EndY=150 EndZ=0
    g2: LineSegment StartX=5530 StartY=150 StartZ=0 EndX=4920 EndY=150 EndZ=0
    g3: LineSegment StartX=4920 StartY=150 StartZ=0 EndX=4920 EndY=760 EndZ=0
    g4: LineSegment StartX=4945 StartY=735 StartZ=0 EndX=5505 EndY=735 EndZ=0
    g5: LineSegment StartX=5505 StartY=735 StartZ=0 EndX=5505 EndY=175 EndZ=0
    g6: LineSegment StartX=5505 StartY=175 StartZ=0 EndX=4945 EndY=175 EndZ=0
    g7: LineSegment StartX=4945 StartY=175 StartZ=0 EndX=4945 EndY=735 EndZ=0
    g8: LineSegment StartX=4970 StartY=685 StartZ=0 EndX=5480 EndY=685 EndZ=0
    g9: LineSegment StartX=5480 StartY=685 StartZ=0 EndX=5480 EndY=225 EndZ=0
    g10: LineSegment StartX=5480 StartY=225 StartZ=0 EndX=4970 EndY=225 EndZ=0
    g11: LineSegment StartX=4970 StartY=225 StartZ=0 EndX=4970 EndY=685 EndZ=0
  constraints (36):
    c: Coincident(g0,g1)
    c: Coincident(g1,g2)
    c: Coincident(g2,g3)
    c: Coincident(g3,g0)
    c: Horizontal(g0)
    c: Horizontal(g2)
    c: Vertical(g1)
    c: Vertical(g3)
    c: Coincident(g4,g5)
    c: Coincident(g5,g6)
    c: Coincident(g6,g7)
    c: Coincident(g7,g4)
    c: Horizontal(g4)
    c: Horizontal(g6)
    c: Vertical(g5)
    c: Vertical(g7)
    c: Coincident(g8,g9)
    c: Coincident(g9,g10)
    c: Coincident(g10,g11)
    c: Coincident(g11,g8)
    c: Horizontal(g8)
    c: Horizontal(g10)
    c: Vertical(g9)
    c: Vertical(g11)
    c: DistanceX(g0,g4) = 25
    c: DistanceX(g4,g0) = 25
    c: DistanceX(g8,g4) = 25
    c: DistanceX(g6,g10) = 25
    c: DistanceX(g2,g2) = 610
    c: DistanceY(g8,g4) = 50
    c: DistanceY(g4,g0) = 25
    c: DistanceY(g5,g9) = 50
    c: DistanceY(g1,g5) = 25
    c: DistanceY(g1,g1) = 610
    c: DistanceY(g-4,g2) = 1750
    c: DistanceX(g-3,g2) = 2940
FEATURE [Part::FeaturePython] Window004  label="W5"  # Arch/BIM 170 (typed FeaturePython)
  Area = 0
  Base = -> Sketch004
  Frame = 0
  Height = 0
  HoleDepth = 0
  HoleWire = 0
  HorizontalArea = 0
  Hosts = -> [Wall003]
  IfcData = IfcUID=21VaAW3m53hBiCXBpSxfnO,+2 more (map truncated)
  IfcType = 170
  LouvreSpacing = 0
  LouvreWidth = 0
  Material = -> Material001
  MoveBase = false
  MoveWithHost = true
  Normal = (-1,-2e-16,2e-16)
  Opening = 0
  OverallHeight = 0
  OverallWidth = 0
  PartitioningType = 0
  PerimeterLength = 0
  Placement = pos=(0,0,1) rot=(0,0,1;0rad)
  PredefinedType = 0
  Preset = 0
  SymbolElevation = false
  SymbolPlan = false
  VerticalArea = 0
  Width = 0
  WindowParts = f1 | Frame | Wire0,Wire1 | 50.0 | 150.0 | f2 | Frame | Wire1,Wire2 | 30.0 | 160.0 | g | Glass panel | Wire2 | 5.0 | 165.0
  expr: OverallHeight = .Height.Value
  expr: OverallWidth = .Width.Value
FEATURE [Part::FeaturePython] Window005  label="W6"  # Arch/BIM 170 (typed FeaturePython)
  Area = 0
  Base = -> Sketch005
  Frame = 0
  Height = 0
  HoleDepth = 0
  HoleWire = 0
  HorizontalArea = 0
  Hosts = -> [Wall002]
  IfcData = IfcUID=34ZSqvoNH6FQuXlkQ2PM_x,+2 more (map truncated)
  IfcType = 170
  LouvreSpacing = 0
  LouvreWidth = 0
  Material = -> Material001
  MoveBase = false
  MoveWithHost = true
  Normal = (-1,0,0)
  Opening = 0
  OverallHeight = 0
  OverallWidth = 0
  PartitioningType = 0
  PerimeterLength = 0
  Placement = pos=(0,170,0) rot=(0,0,1;0rad)
  PredefinedType = 0
  Preset = 0
  SymbolElevation = false
  SymbolPlan = false
  VerticalArea = 0
  Width = 0
  WindowParts = f1 | Frame | Wire0,Wire1 | 50.0 | 150.0 | f2 | Frame | Wire1,Wire2 | 30.0 | 160.0 | g | Glass panel | Wire2 | 5.0 | 165.0
  expr: OverallHeight = .Height.Value
  expr: OverallWidth = .Width.Value
FEATURE [Part::FeaturePython] Window006  label="W7"  # Arch/BIM 170 (typed FeaturePython)
  Area = 0
  Base = -> Sketch006
  Frame = 0
  Height = 0
  HoleDepth = 0
  HoleWire = 0
  HorizontalArea = 0
  Hosts = -> [Wall002]
  IfcData = IfcUID=0fexrAN3f9suWX40s0ms7O,+2 more (map truncated)
  IfcType = 170
  LouvreSpacing = 0
  LouvreWidth = 0
  Material = -> Material001
  MoveBase = false
  MoveWithHost = true
  Normal = (-1,0,0)
  Opening = 0
  OverallHeight = 0
  OverallWidth = 0
  PartitioningType = 0
  PerimeterLength = 0
  Placement = pos=(0,1810,0) rot=(0,0,1;0rad)
  PredefinedType = 0
  Preset = 0
  SymbolElevation = false
  SymbolPlan = false
  VerticalArea = 0
  Width = 0
  WindowParts = f1 | Frame | Wire0,Wire1 | 50.0 | 150.0 | f2 | Frame | Wire1,Wire2 | 30.0 | 160.0 | g | Glass panel | Wire2 | 5.0 | 165.0
  expr: OverallWidth = .Width.Value
  expr: OverallHeight = .Height.Value
FEATURE [Part::FeaturePython] Window007  label="W8"  # Arch/BIM 170 (typed FeaturePython)
  Area = 0
  Base = -> Sketch007
  Frame = 0
  Height = 0
  HoleDepth = 0
  HoleWire = 0
  HorizontalArea = 0
  Hosts = -> [Wall002]
  IfcData = IfcUID=1$oxyoNTbFnPgu5866942o,+2 more (map truncated)
  IfcType = 170
  LouvreSpacing = 0
  LouvreWidth = 0
  Material = -> Material001
  MoveBase = false
  MoveWithHost = true
  Normal = (-1,0,0)
  Opening = 0
  OverallHeight = 0
  OverallWidth = 0
  PartitioningType = 0
  PerimeterLength = 0
  Placement = pos=(0,3650,0) rot=(0,0,1;0rad)
  PredefinedType = 0
  Preset = 0
  SymbolElevation = false
  SymbolPlan = false
  VerticalArea = 0
  Width = 0
  WindowParts = f1 | Frame | Wire0,Wire1 | 50.0 | 150.0 | f2 | Frame | Wire1,Wire2 | 30.0 | 160.0 | g | Glass panel | Wire2 | 5.0 | 165.0
  expr: OverallWidth = .Width.Value
  expr: OverallHeight = .Height.Value
FEATURE [Part::FeaturePython] Window008  label="W9"  # Arch/BIM 170 (typed FeaturePython)
  Area = 0
  Base = -> Sketch008
  Frame = 0
  Height = 0
  HoleDepth = 0
  HoleWire = 0
  HorizontalArea = 0
  Hosts = -> [Wall003]
  IfcData = IfcUID=3AL2uB76T7dvjXNTAVk3ye,+2 more (map truncated)
  IfcType = 170
  LouvreSpacing = 0
  LouvreWidth = 0
  Material = -> Material001
  MoveBase = false
  MoveWithHost = true
  Normal = (-1,0,0)
  Opening = 0
  OverallHeight = 0
  OverallWidth = 0
  PartitioningType = 0
  PerimeterLength = 0
  Placement = pos=(0,5440,0) rot=(0,0,1;0rad)
  PredefinedType = 0
  Preset = 0
  SymbolElevation = false
  SymbolPlan = false
  VerticalArea = 0
  Width = 0
  WindowParts = f1 | Frame | Wire0,Wire1 | 50.0 | 150.0 | f2 | Frame | Wire1,Wire2 | 30.0 | 160.0 | g | Glass panel | Wire2 | 5.0 | 165.0
  expr: OverallWidth = .Width.Value
  expr: OverallHeight = .Height.Value
FEATURE [Part::FeaturePython] Window009  label="W10"  # Arch/BIM 170 (typed FeaturePython)
  Area = 0
  Base = -> Sketch009
  Frame = 0
  Height = 0
  HoleDepth = 0
  HoleWire = 0
  HorizontalArea = 0
  Hosts = -> [Wall003]
  IfcData = IfcUID=2EcN_tIeL0NgLO93hgdrKW,+2 more (map truncated)
  IfcType = 170
  LouvreSpacing = 0
  LouvreWidth = 0
  Material = -> Material001
  MoveBase = false
  MoveWithHost = true
  Normal = (-1,0,0)
  Opening = 0
  OverallHeight = 0
  OverallWidth = 0
  PartitioningType = 0
  PerimeterLength = 0
  Placement = pos=(0,7200,0) rot=(0,0,1;0rad)
  PredefinedType = 0
  Preset = 0
  SymbolElevation = false
  SymbolPlan = false
  VerticalArea = 0
  Width = 0
  WindowParts = f1 | Frame | Wire0,Wire1 | 50.0 | 150.0 | f2 | Frame | Wire1,Wire2 | 30.0 | 160.0 | g | Glass panel | Wire2 | 5.0 | 165.0
  expr: OverallWidth = .Width.Value
  expr: OverallHeight = .Height.Value
FEATURE [Part::FeaturePython] Window012  # Arch/BIM 170 (typed FeaturePython)
  Area = 0
  Base = -> Sketch017
  Frame = 0
  Height = 0
  HoleDepth = 0
  HoleWire = 0
  HorizontalArea = 0
  Hosts = -> [Wall006]
  IfcData = IfcUID=1KJC8ckAn1dvsPDybGtpcJ,+2 more (map truncated)
  IfcType = 170
  LouvreSpacing = 0
  LouvreWidth = 0
  Material = -> Material001
  MoveBase = false
  MoveWithHost = true
  Normal = (3e-16,-1,2e-16)
  Opening = 0
  OverallHeight = 0
  OverallWidth = 0
  PartitioningType = 0
  PerimeterLength = 0
  Placement = pos=(-12960,0,0) rot=(0,0,1;0rad)
  PredefinedType = 0
  Preset = 0
  SymbolElevation = false
  SymbolPlan = false
  VerticalArea = 0
  Width = 0
  WindowParts = f1 | Frame | Wire0,Wire1 | 50.0 | 150.0 | f2 | Frame | Wire1,Wire2 | 30.0 | 160.0 | g1 | Glass panel | Wire2 | 5.0 | 165.0
  expr: OverallHeight = .Height.Value
  expr: OverallWidth = .Width.Value
FEATURE [Part::FeaturePython] Window015  # Arch/BIM 170 (typed FeaturePython)
  Area = 0
  Base = -> Sketch020
  Frame = 0
  Height = 0
  HoleDepth = 0
  HoleWire = 0
  HorizontalArea = 0
  Hosts = -> [Wall006]
  IfcData = IfcUID=2VkMOxZ9L4ORedmuo0nIe_,+2 more (map truncated)
  IfcType = 170
  LouvreSpacing = 0
  LouvreWidth = 0
  Material = -> Material001
  MoveBase = false
  MoveWithHost = true
  Normal = (2e-16,-1,-2e-16)
  Opening = 0
  OverallHeight = 0
  OverallWidth = 0
  PartitioningType = 0
  PerimeterLength = 0
  Placement = pos=(-12960,0,0) rot=(0,0,1;0rad)
  PredefinedType = 0
  Preset = 0
  SymbolElevation = false
  SymbolPlan = false
  VerticalArea = 0
  Width = 0
  WindowParts = f1 | Frame | Wire0,Wire1 | 50.0 | 150.0 | f2 | Frame | Wire1,Wire2 | 30.0 | 160.0 | g1 | Glass panel | Wire2 | 5.0 | 165.0
  expr: OverallWidth = .Width.Value
  expr: OverallHeight = .Height.Value
FEATURE [Part::FeaturePython] Wall004  label="W005"  # Arch/BIM 166 (typed FeaturePython)
  Align = 1
  Area = 13024000
  Base = -> WallTrace005
  BlockHeight = 76
  BlockLength = 228
  CountBroken = 178
  CountEntire = 446
  Face = 0
  Height = 3200
  HorizontalArea = 0
  IfcData = IfcUID=3w4By6$qX4sO9zr26qYiW4,+2 more (map truncated)
  IfcType = 166
  Joint = 10
  Length = 4070
  MakeBlocks = false
  Material = -> Material002
  MoveBase = false
  MoveWithHost = false
  Normal = (0,0,1)
  OffsetFirst = 114
  OffsetSecond = 0
  PerimeterLength = 0
  PredefinedType = 0
  Subtractions = -> [Structure050]
  VerticalArea = 0
  Width = 230
FEATURE [Part::FeaturePython] Window010  label="Window"  # Arch/BIM 170 (typed FeaturePython)
  Area = 0
  Base = -> Sketch015
  Frame = 0
  Height = 0
  HoleDepth = 0
  HoleWire = 0
  HorizontalArea = 0
  Hosts = -> [Wall004]
  IfcData = IfcUID=1WldOLUfnDFR$v_hoqhyHx,+2 more (map truncated)
  IfcType = 170
  LouvreSpacing = 0
  LouvreWidth = 0
  Material = -> Material001
  MoveBase = false
  MoveWithHost = true
  Normal = (3e-16,-1,2e-16)
  Opening = 0
  OverallHeight = 0
  OverallWidth = 0
  PartitioningType = 0
  PerimeterLength = 0
  Placement = pos=(-170,0,0) rot=(0,0,1;0rad)
  PredefinedType = 0
  Preset = 0
  SymbolElevation = false
  SymbolPlan = false
  VerticalArea = 0
  Width = 0
  WindowParts = f1 | Frame | Wire0,Wire1 | 50.0 | 150.0 | f2 | Frame | Wire1,Wire2 | 30.0 | 160.0 | g1 | Glass panel | Wire2 | 5.0 | 165.0
  expr: OverallWidth = .Width.Value
  expr: OverallHeight = .Height.Value
FEATURE [Part::FeaturePython] Window011  # Arch/BIM 170 (typed FeaturePython)
  Area = 0
  Base = -> Sketch016
  Frame = 0
  Height = 0
  HoleDepth = 0
  HoleWire = 0
  HorizontalArea = 0
  Hosts = -> [Wall004]
  IfcData = IfcUID=2vP0x8ghn46wIpjJ6zkW$A,+2 more (map truncated)
  IfcType = 170
  LouvreSpacing = 0
  LouvreWidth = 0
  Material = -> Material001
  MoveBase = false
  MoveWithHost = true
  Normal = (3e-16,-1,2e-16)
  Opening = 0
  OverallHeight = 0
  OverallWidth = 0
  PartitioningType = 0
  PerimeterLength = 0
  Placement = pos=(-3150,0,0) rot=(0,0,1;0rad)
  PredefinedType = 0
  Preset = 0
  SymbolElevation = false
  SymbolPlan = false
  VerticalArea = 0
  Width = 0
  WindowParts = f1 | Frame | Wire0,Wire1 | 50.0 | 150.0 | f2 | Frame | Wire1,Wire2 | 30.0 | 160.0 | g1 | Glass panel | Wire2 | 5.0 | 165.0
  expr: OverallHeight = .Height.Value
  expr: OverallWidth = .Width.Value
FEATURE [Part::FeaturePython] Window013  # Arch/BIM 170 (typed FeaturePython)
  Area = 0
  Base = -> Sketch018
  Frame = 0
  Height = 0
  HoleDepth = 0
  HoleWire = 0
  HorizontalArea = 0
  Hosts = -> [Wall004]
  IfcData = IfcUID=2zGq_SVs58s8EskkEZvdql,+2 more (map truncated)
  IfcType = 170
  LouvreSpacing = 0
  LouvreWidth = 0
  Material = -> Material001
  MoveBase = false
  MoveWithHost = true
  Normal = (2e-16,-1,-2e-16)
  Opening = 0
  OverallHeight = 0
  OverallWidth = 0
  PartitioningType = 0
  PerimeterLength = 0
  Placement = pos=(-170,0,0) rot=(0,0,1;0rad)
  PredefinedType = 0
  Preset = 0
  SymbolElevation = false
  SymbolPlan = false
  VerticalArea = 0
  Width = 0
  WindowParts = f1 | Frame | Wire0,Wire1 | 50.0 | 150.0 | f2 | Frame | Wire1,Wire2 | 30.0 | 160.0 | g1 | Glass panel | Wire2 | 5.0 | 165.0
  expr: OverallHeight = .Height.Value
  expr: OverallWidth = .Width.Value
FEATURE [Part::FeaturePython] Window014  # Arch/BIM 170 (typed FeaturePython)
  Area = 0
  Base = -> Sketch019
  Frame = 0
  Height = 0
  HoleDepth = 0
  HoleWire = 0
  HorizontalArea = 0
  Hosts = -> [Wall004]
  IfcData = IfcUID=0WPmzYGfXCUgvvMuO5E0pA,+2 more (map truncated)
  IfcType = 170
  LouvreSpacing = 0
  LouvreWidth = 0
  Material = -> Material001
  MoveBase = false
  MoveWithHost = true
  Normal = (2e-16,-1,-2e-16)
  Opening = 0
  OverallHeight = 0
  OverallWidth = 0
  PartitioningType = 0
  PerimeterLength = 0
  Placement = pos=(-3150,0,0) rot=(0,0,1;0rad)
  PredefinedType = 0
  Preset = 0
  SymbolElevation = false
  SymbolPlan = false
  VerticalArea = 0
  Width = 0
  WindowParts = f1 | Frame | Wire0,Wire1 | 50.0 | 150.0 | f2 | Frame | Wire1,Wire2 | 30.0 | 160.0 | g1 | Glass panel | Wire2 | 5.0 | 165.0
  expr: OverallWidth = .Width.Value
  expr: OverallHeight = .Height.Value
FEATURE [Part::FeaturePython] Window016  # Arch/BIM 170 (typed FeaturePython)
  Area = 0
  Base = -> Sketch024
  Frame = 0
  Height = 0
  HoleDepth = 0
  HoleWire = 0
  HorizontalArea = 0
  Hosts = -> [Wall005]
  IfcData = IfcUID=3s1v0SRT13PO5wVlq9Ck7I,+2 more (map truncated)
  IfcType = 170
  LouvreSpacing = 0
  LouvreWidth = 0
  Material = -> Material001
  MoveBase = false
  MoveWithHost = true
  Normal = (1e-16,-1,2e-16)
  Opening = 0
  OverallHeight = 0
  OverallWidth = 0
  PartitioningType = 0
  PerimeterLength = 0
  PredefinedType = 0
  Preset = 0
  SymbolElevation = false
  SymbolPlan = false
  VerticalArea = 0
  Width = 0
  WindowParts = f1 | Frame | Wire0,Wire1 | 50.0 | 150.0 | f2 | Frame | Wire1,Wire2,Wire3,Wire4 | 30.0 | 160.0 | g1 | Glass panel | Wire2 | 5.0 | 165.0 | g2 | Glass panel | Wire3 | 5.0 | 165.0 | g3 | Glass panel | Wire4 | 5.0 | 165.0
  expr: OverallWidth = .Width.Value
  expr: OverallHeight = .Height.Value
FEATURE [Part::FeaturePython] Window017  # Arch/BIM 170 (typed FeaturePython)
  Area = 0
  Base = -> Sketch025
  Frame = 0
  Height = 0
  HoleDepth = 0
  HoleWire = 0
  HorizontalArea = 0
  Hosts = -> [Wall005]
  IfcData = IfcUID=0JR6JKINv9lB5PTD0QwM2r,+2 more (map truncated)
  IfcType = 170
  LouvreSpacing = 0
  LouvreWidth = 0
  Material = -> Material001
  MoveBase = false
  MoveWithHost = true
  Normal = (1e-16,-1,2e-16)
  Opening = 0
  OverallHeight = 0
  OverallWidth = 0
  PartitioningType = 0
  PerimeterLength = 0
  PredefinedType = 0
  Preset = 0
  SymbolElevation = false
  SymbolPlan = false
  VerticalArea = 0
  Width = 0
  WindowParts = f1 | Frame | Wire0,Wire1 | 50.0 | 150.0 | f2 | Frame | Wire1,Wire2,Wire3,Wire4,Wire5 | 30.0 | 160.0 | g1 | Glass panel | Wire2 | 5.0 | 165.0 | g2 | Glass panel | Wire3 | 5.0 | 165.0 | g3 | Glass panel | Wire4 | 5.0 | 165.0 | g4 | Glass panel | Wire5 | 5.0 | 165.0
  expr: OverallWidth = .Width.Value
  expr: OverallHeight = .Height.Value
FEATURE [Part::FeaturePython] Wall020  label="W009"  # Arch/BIM 166 (typed FeaturePython)
  Align = 0
  Area = 15040000
  Base = -> WallTrace025
  BlockHeight = 76
  BlockLength = 228
  CountBroken = 156
  CountEntire = 511
  Face = 0
  Height = 3200
  HorizontalArea = 2.162e+06
  IfcData = IfcUID=1jTVARHb1Cj9Dwtbb90rKD,+2 more (map truncated)
  IfcType = 166
  Joint = 10
  Length = 4700
  MakeBlocks = false
  Material = -> Material002
  MoveBase = false
  MoveWithHost = false
  Normal = (0,0,1)
  OffsetFirst = 114
  OffsetSecond = 0
  PerimeterLength = 0
  PredefinedType = 0
  Subtractions = -> [Structure054]
  VerticalArea = 2.61446e+07
  Width = 230
FEATURE [Part::FeaturePython] Window018  # Arch/BIM 170 (typed FeaturePython)
  Area = 0
  Base = -> Sketch027
  Frame = 0
  Height = 0
  HoleDepth = 0
  HoleWire = 0
  HorizontalArea = 0
  Hosts = -> [Wall020]
  IfcData = IfcUID=3nG0_jSKTBi943alEXYSuR,+2 more (map truncated)
  IfcType = 170
  LouvreSpacing = 0
  LouvreWidth = 0
  Material = -> Material001
  MoveBase = false
  MoveWithHost = true
  Normal = (0.999997,-0.00242648,-1e-16)
  Opening = 0
  OverallHeight = 0
  OverallWidth = 0
  PartitioningType = 0
  PerimeterLength = 0
  PredefinedType = 0
  Preset = 0
  SymbolElevation = false
  SymbolPlan = false
  VerticalArea = 0
  Width = 0
  WindowParts = <same value as first occurrence — deduplicated (x3 in doc)>
  expr: OverallWidth = .Width.Value
  expr: OverallHeight = .Height.Value
FEATURE [Part::FeaturePython] Window019  # Arch/BIM 170 (typed FeaturePython)
  Area = 0
  Base = -> Sketch030
  Frame = 0
  Height = 0
  HoleDepth = 0
  HoleWire = 0
  HorizontalArea = 0
  Hosts = -> [Wall007]
  IfcData = IfcUID=2iDCtfe9L6ue4WzkUab12F,+2 more (map truncated)
  IfcType = 170
  LouvreSpacing = 0
  LouvreWidth = 0
  Material = -> Material001
  MoveBase = false
  MoveWithHost = true
  Normal = (0.999997,-0.00242648,-1e-16)
  Opening = 0
  OverallHeight = 0
  OverallWidth = 0
  PartitioningType = 0
  PerimeterLength = 0
  Placement = pos=(0,4250,0) rot=(0,0,1;0rad)
  PredefinedType = 0
  Preset = 0
  SymbolElevation = false
  SymbolPlan = false
  VerticalArea = 0
  Width = 0
  WindowParts = <same value as first occurrence — deduplicated (x3 in doc)>
  expr: OverallHeight = .Height.Value
  expr: OverallWidth = .Width.Value
FEATURE [Part::FeaturePython] Window020  # Arch/BIM 170 (typed FeaturePython)
  Area = 0
  Base = -> Sketch035
  Frame = 0
  Height = 0
  HoleDepth = 0
  HoleWire = 0
  HorizontalArea = 0
  Hosts = -> [Wall]
  IfcData = IfcUID=0Sy_E0t1n3eAyV1eD$_I8p,+2 more (map truncated)
  IfcType = 170
  LouvreSpacing = 0
  LouvreWidth = 0
  Material = -> Material001
  MoveBase = false
  MoveWithHost = true
  Normal = (0,1,-2e-16)
  Opening = 0
  OverallHeight = 0
  OverallWidth = 0
  PartitioningType = 0
  PerimeterLength = 0
  PredefinedType = 0
  Preset = 0
  SymbolElevation = false
  SymbolPlan = false
  VerticalArea = 0
  Width = 0
  WindowParts = f1 | Frame | Wire0,Wire1 | 50.0 | 150.0 | f2 | Frame | Wire1,Wire2 | 30.0 | 160.0 | g1 | Glass panel | Wire2 | 5.0 | 165.0
  expr: OverallWidth = .Width.Value
  expr: OverallHeight = .Height.Value
FEATURE [Part::FeaturePython] Window021  # Arch/BIM 170 (typed FeaturePython)
  Area = 0
  Base = -> Sketch031
  Frame = 0
  Height = 0
  HoleDepth = 0
  HoleWire = 0
  HorizontalArea = 0
  Hosts = -> [Wall]
  IfcData = IfcUID=0E4929nITBjerxpPftKP4Y,+2 more (map truncated)
  IfcType = 170
  LouvreSpacing = 0
  LouvreWidth = 0
  Material = -> Material001
  MoveBase = false
  MoveWithHost = true
  Normal = (0,1,-2e-16)
  Opening = 0
  OverallHeight = 0
  OverallWidth = 0
  PartitioningType = 0
  PerimeterLength = 0
  Placement = pos=(160,0,0) rot=(0,0,1;0rad)
  PredefinedType = 0
  Preset = 0
  SymbolElevation = false
  SymbolPlan = false
  VerticalArea = 0
  Width = 0
  WindowParts = f1 | Frame | Wire1,Wire0,Wire2 | 50.0 | 150.0 | g1 | Glass panel | Wire2 | 5.0 | 165.0 | f2 | Solid panel | Wire1,Wire3 | 30.0 | 160.0 | g2 | Glass panel | Wire3 | 5.0 | 165.0
  expr: OverallWidth = .Width.Value
  expr: OverallHeight = .Height.Value
FEATURE [Part::FeaturePython] Window022  # Arch/BIM 170 (typed FeaturePython)
  Area = 0
  Base = -> Sketch032
  Frame = 0
  Height = 0
  HoleDepth = 0
  HoleWire = 0
  HorizontalArea = 0
  Hosts = -> [Wall]
  IfcData = IfcUID=0kPftwJun1ygH$Mc8a1lti,+2 more (map truncated)
  IfcType = 170
  LouvreSpacing = 0
  LouvreWidth = 0
  Material = -> Material001
  MoveBase = false
  MoveWithHost = true
  Normal = (0,1,-2e-16)
  Opening = 0
  OverallHeight = 0
  OverallWidth = 0
  PartitioningType = 0
  PerimeterLength = 0
  Placement = pos=(160,0,0) rot=(0,0,1;0rad)
  PredefinedType = 0
  Preset = 0
  SymbolElevation = false
  SymbolPlan = false
  VerticalArea = 0
  Width = 0
  WindowParts = f1 | Frame | Wire0,Wire1 | 50.0 | 150.0 | f2 | Frame | Wire1,Wire2 | 30.0 | 160.0 | g1 | Glass panel | Wire2 | 5.0 | 165.0
  expr: OverallWidth = .Width.Value
  expr: OverallHeight = .Height.Value
FEATURE [Part::FeaturePython] Window023  # Arch/BIM 170 (typed FeaturePython)
  Area = 0
  Base = -> Sketch034
  Frame = 0
  Height = 0
  HoleDepth = 0
  HoleWire = 0
  HorizontalArea = 0
  Hosts = -> [Wall]
  IfcData = IfcUID=2upP021Qz1Qx7VQVns5myl,+2 more (map truncated)
  IfcType = 170
  LouvreSpacing = 0
  LouvreWidth = 0
  Material = -> Material001
  MoveBase = false
  MoveWithHost = true
  Normal = (0,1,-2e-16)
  Opening = 0
  OverallHeight = 0
  OverallWidth = 0
  PartitioningType = 0
  PerimeterLength = 0
  PredefinedType = 0
  Preset = 0
  SymbolElevation = false
  SymbolPlan = false
  VerticalArea = 0
  Width = 0
  WindowParts = f1 | Frame | Wire0,Wire1 | 50.0 | 150.0 | f2 | Frame | Wire1,Wire2 | 30.0 | 160.0 | g1 | Glass panel | Wire2 | 5.0 | 165.0
  expr: OverallWidth = .Width.Value
  expr: OverallHeight = .Height.Value
FEATURE [Part::FeaturePython] Window024  # Arch/BIM 170 (typed FeaturePython)
  Area = 0
  Base = -> Sketch037
  Frame = 0
  Height = 0
  HoleDepth = 0
  HoleWire = 0
  HorizontalArea = 0
  Hosts = -> [Wall001]
  IfcData = IfcUID=11nSfX0ZvChQj0zQR5$gdv,+2 more (map truncated)
  IfcType = 170
  LouvreSpacing = 0
  LouvreWidth = 0
  Material = -> Material001
  MoveBase = false
  MoveWithHost = true
  Normal = (0,1,-2e-16)
  Opening = 0
  OverallHeight = 0
  OverallWidth = 0
  PartitioningType = 0
  PerimeterLength = 0
  PredefinedType = 0
  Preset = 0
  SymbolElevation = false
  SymbolPlan = false
  VerticalArea = 0
  Width = 0
  WindowParts = f1 | Frame | Wire0,Wire1 | 50.0 | 150.0 | f2 | Frame | Wire1,Wire2,Wire3 | 30.0 | 160.0 | g1 | Glass panel | Wire3 | 5.0 | 165.0 | g2 | Glass panel | Wire2 | 5.0 | 165.0
  expr: OverallWidth = .Width.Value
  expr: OverallHeight = .Height.Value
FEATURE [Sketcher::SketchObject] Sketch039
  ExternalGeometry = -> [Structure045,Structure056,Wall009]
  Placement = pos=(8410,3650,2435) rot=(1,0,0;1.5708rad)
  sketch-geometry (36):
    g0: LineSegment StartX=-1070 StartY=-75 StartZ=0 EndX=2870 EndY=-75 EndZ=0
    g1: LineSegment StartX=2870 StartY=-75 StartZ=0 EndX=2870 EndY=-2435 EndZ=0
    g2: LineSegment StartX=2870 StartY=-2435 StartZ=0 EndX=-1070 EndY=-2435 EndZ=0
    g3: LineSegment StartX=-1070 StartY=-2435 StartZ=0 EndX=-1070 EndY=-75 EndZ=0
    g4: LineSegment StartX=-1020 StartY=-125 StartZ=0 EndX=-97.5 EndY=-125 EndZ=0
    g5: LineSegment StartX=-97.5 StartY=-125 StartZ=0 EndX=-97.5 EndY=-1205 EndZ=0
    g6: LineSegment StartX=-97.5 StartY=-1205 StartZ=0 EndX=-1020 EndY=-1205 EndZ=0
    g7: LineSegment StartX=-1020 StartY=-1205 StartZ=0 EndX=-1020 EndY=-125 EndZ=0
    g8: LineSegment StartX=-1020 StartY=-1305 StartZ=0 EndX=-97.5 EndY=-1305 EndZ=0
    g9: LineSegment StartX=-97.5 StartY=-1305 StartZ=0 EndX=-97.5 EndY=-2385 EndZ=0
    g10: LineSegment StartX=-97.5 StartY=-2385 StartZ=0 EndX=-1020 EndY=-2385 EndZ=0
    g11: LineSegment StartX=-1020 StartY=-2385 StartZ=0 EndX=-1020 EndY=-1305 EndZ=0
    g12: LineSegment StartX=-47.5 StartY=-125 StartZ=0 EndX=875 EndY=-125 EndZ=0
    g13: LineSegment StartX=875 StartY=-125 StartZ=0 EndX=875 EndY=-1205 EndZ=0
    g14: LineSegment StartX=875 StartY=-1205 StartZ=0 EndX=-47.5 EndY=-1205 EndZ=0
    g15: LineSegment StartX=-47.5 StartY=-1205 StartZ=0 EndX=-47.5 EndY=-125 EndZ=0
    g16: LineSegment StartX=-47.5 StartY=-1305 StartZ=0 EndX=875 EndY=-1305 EndZ=0
    g17: LineSegment StartX=875 StartY=-1305 StartZ=0 EndX=875 EndY=-2385 EndZ=0
    g18: LineSegment StartX=875 StartY=-2385 StartZ=0 EndX=-47.5 EndY=-2385 EndZ=0
    g19: LineSegment StartX=-47.5 StartY=-2385 StartZ=0 EndX=-47.5 EndY=-1305 EndZ=0
    g20: LineSegment StartX=925 StartY=-125 StartZ=0 EndX=1847.5 EndY=-125 EndZ=0
    g21: LineSegment StartX=1847.5 StartY=-125 StartZ=0 EndX=1847.5 EndY=-1205 EndZ=0
    g22: LineSegment StartX=1847.5 StartY=-1205 StartZ=0 EndX=925 EndY=-1205 EndZ=0
    g23: LineSegment StartX=925 StartY=-1205 StartZ=0 EndX=925 EndY=-125 EndZ=0
    g24: LineSegment StartX=1897.5 StartY=-125 StartZ=0 EndX=2820 EndY=-125 EndZ=0
    g25: LineSegment StartX=2820 StartY=-125 StartZ=0 EndX=2820 EndY=-1205 EndZ=0
    g26: LineSegment StartX=2820 StartY=-1205 StartZ=0 EndX=1897.5 EndY=-1205 EndZ=0
    g27: LineSegment StartX=1897.5 StartY=-1205 StartZ=0 EndX=1897.5 EndY=-125 EndZ=0
    g28: LineSegment StartX=925 StartY=-1305 StartZ=0 EndX=1847.5 EndY=-1305 EndZ=0
    g29: LineSegment StartX=1847.5 StartY=-1305 StartZ=0 EndX=1847.5 EndY=-2385 EndZ=0
    g30: LineSegment StartX=1847.5 StartY=-2385 StartZ=0 EndX=925 EndY=-2385 EndZ=0
    g31: LineSegment StartX=925 StartY=-2385 StartZ=0 EndX=925 EndY=-1305 EndZ=0
    g32: LineSegment StartX=1897.5 StartY=-1305 StartZ=0 EndX=2820 EndY=-1305 EndZ=0
    g33: LineSegment StartX=2820 StartY=-1305 StartZ=0 EndX=2820 EndY=-2385 EndZ=0
    g34: LineSegment StartX=2820 StartY=-2385 StartZ=0 EndX=1897.5 EndY=-2385 EndZ=0
    g35: LineSegment StartX=1897.5 StartY=-2385 StartZ=0 EndX=1897.5 EndY=-1305 EndZ=0
  constraints (107):
    c: Coincident(g0,g1)
    c: Coincident(g1,g2)
    c: Coincident(g2,g3)
    c: Coincident(g3,g0)
    c: Horizontal(g0)
    c: Horizontal(g2)
    c: Vertical(g1)
    c: Vertical(g3)
    c: Coincident(g4,g5)
    c: Coincident(g5,g6)
    c: Coincident(g6,g7)
    c: Coincident(g7,g4)
    c: Horizontal(g4)
    c: Horizontal(g6)
    c: Vertical(g5)
    c: Vertical(g7)
    c: Coincident(g8,g9)
    c: Coincident(g9,g10)
    c: Coincident(g10,g11)
    c: Coincident(g11,g8)
    c: Horizontal(g8)
    c: Horizontal(g10)
    c: Vertical(g9)
    c: Vertical(g11)
    c: Coincident(g12,g13)
    c: Coincident(g13,g14)
    c: Coincident(g14,g15)
    c: Coincident(g15,g12)
    c: Horizontal(g12)
    c: Horizontal(g14)
    c: Vertical(g13)
    c: Vertical(g15)
    c: Coincident(g16,g17)
    c: Coincident(g17,g18)
    c: Coincident(g18,g19)
    c: Coincident(g19,g16)
    c: Horizontal(g16)
    c: Horizontal(g18)
    c: Vertical(g17)
    c: Vertical(g19)
    c: Coincident(g20,g21)
    c: Coincident(g21,g22)
    c: Coincident(g22,g23)
    c: Coincident(g23,g20)
    c: Horizontal(g20)
    c: Horizontal(g22)
    c: Vertical(g21)
    c: Vertical(g23)
    c: Coincident(g24,g25)
    c: Coincident(g25,g26)
    c: Coincident(g26,g27)
    c: Coincident(g27,g24)
    c: Horizontal(g24)
    c: Horizontal(g26)
    c: Vertical(g25)
    c: Vertical(g27)
    c: Coincident(g28,g29)
    c: Coincident(g29,g30)
    c: Coincident(g30,g31)
    c: Coincident(g31,g28)
    c: Horizontal(g28)
    c: Horizontal(g30)
    c: Vertical(g29)
    c: Vertical(g31)
    c: Coincident(g32,g33)
    c: Coincident(g33,g34)
    c: Coincident(g34,g35)
    c: Coincident(g35,g32)
    c: Horizontal(g32)
    c: Horizontal(g34)
    c: Vertical(g33)
    c: Vertical(g35)
    c: Equal(g21,g27)
    c: Equal(g27,g35)
    c: Equal(g31,g17)
    c: Equal(g9,g19)
    c: Equal(g29,g35)
    c: Equal(g6,g8)
    c: Equal(g16,g14)
    c: Equal(g22,g28)
    c: Equal(g26,g32)
    c: Equal(g32,g28)
    c: Equal(g28,g16)
    c: Equal(g8,g16)
    c: DistanceY(g12,g4) = 0
    c: DistanceY(g12,g20) = 0
    c: DistanceY(g20,g24) = 0
    c: DistanceY(g8,g5) = 100
    c: DistanceY(g8,g16) = 0
    c: DistanceY(g28,g16) = 0
    c: DistanceY(g28,g32) = 0
    c: DistanceX(g28,g21) = 0
    c: DistanceX(g32,g26) = 0
    c: DistanceX(g16,g13) = 0
    c: DistanceX(g8,g5) = 0
    c: DistanceY(g5,g14) = 0
    c: DistanceY(g13,g22) = 0
    c: DistanceY(g1,g1) = 2360
    c: DistanceX(g2,g2) = 3940
    c: DistanceX(g33,g1) = 50
    c: DistanceX(g2,g10) = 50
    c: DistanceY(g4,g0) = 50
    c: DistanceY(g2,g10) = 50
    c: DistanceX(g17,g30) = 50
    c: DistanceX(g29,g34) = 50
    c: DistanceX(g9,g18) = 50
    c: Coincident(g1,g-3)
FEATURE [Part::FeaturePython] Window025  # Arch/BIM 170 (typed FeaturePython)
  Area = 0
  Base = -> Sketch039
  Frame = 0
  Height = 0
  HoleDepth = 0
  HoleWire = 0
  HorizontalArea = 0
  IfcData = IfcUID=0Au5zBddr5xBdKOpKCrvuN,+2 more (map truncated)
  IfcType = 170
  LouvreSpacing = 0
  LouvreWidth = 0
  Material = -> Material001
  MoveBase = false
  MoveWithHost = true
  Normal = (0,1,-2e-16)
  Opening = 0
  OverallHeight = 0
  OverallWidth = 0
  PartitioningType = 0
  PerimeterLength = 0
  PredefinedType = 0
  Preset = 0
  SymbolElevation = false
  SymbolPlan = false
  VerticalArea = 0
  Width = 0
  WindowParts = Default | Frame | Wire0,Wire1,Wire2,Wire3,Wire4,Wire5,Wire6,Wire7,Wire8 | 50.0 | 0.0 | g1 | Glass panel | Wire1 | 10.0 | 5.0 | g2 | Glass panel | Wire2 | 5.0 | 10.0 | g3 | Glass panel | Wire3 | 5.0 | 10.0 | g4 | Glass panel | Wire4 | 5.0 | 10.0 | g5 | Glass panel | Wire5 | 5.0 | 10.0 | g6 | Glass panel | Wire6 | 5.0 | 10.0 | g7 | Glass panel | Wire7 | 5.0 | 10.0 | g8 | Glass panel | Wire8 | 5.0 | 10.0
  expr: OverallWidth = .Width.Value
  expr: OverallHeight = .Height.Value
FEATURE [Part::FeaturePython] Wall022  label="W012"  # Arch/BIM 166 (typed FeaturePython)
  Align = 1
  Area = 3960600
  Base = -> Sketch043
  BlockHeight = 76
  BlockLength = 228
  CountBroken = 41
  CountEntire = 184
  Face = 0
  Height = 690
  HorizontalArea = 1320200
  IfcData = IfcUID=3ihu4mZA15n9c8oTGvR1WD,+2 more (map truncated)
  IfcType = 166
  Joint = 10
  Length = 5740
  MakeBlocks = false
  Material = -> Material002
  MoveBase = false
  MoveWithHost = false
  Normal = (0,0,0)
  OffsetFirst = 114
  OffsetSecond = 0
  PerimeterLength = 11940
  PredefinedType = 0
  VerticalArea = 8238600
  Width = 230
  expr: Height = 3500 - 2360 - 150 - 300
FEATURE [Sketcher::SketchObject] Sketch049
  ExternalGeometry = -> [Structure015,Structure017,Structure012,Structure020,Wall009,Wall011]
  Placement = pos=(150,7465,0) rot=(0,0,1;0rad)
  sketch-geometry (8):
    g0: LineSegment StartX=150 StartY=2165 StartZ=0 EndX=15500 EndY=2165 EndZ=0
    g1: LineSegment StartX=15500 StartY=2165 StartZ=0 EndX=15500 EndY=-7165 EndZ=0
    g2: LineSegment StartX=15500 StartY=-7165 StartZ=0 EndX=11430 EndY=-7165 EndZ=0
    g3: LineSegment StartX=11430 StartY=-7165 StartZ=0 EndX=11430 EndY=-3457.5 EndZ=0
    g4: LineSegment StartX=11430 StartY=-3457.5 StartZ=0 EndX=5090 EndY=-3457.5 EndZ=0
    g5: LineSegment StartX=5090 StartY=-3457.5 StartZ=0 EndX=5090 EndY=-7165 EndZ=0
    g6: LineSegment StartX=5090 StartY=-7165 StartZ=0 EndX=150 EndY=-7165 EndZ=0
    g7: LineSegment StartX=150 StartY=-7165 StartZ=0 EndX=150 EndY=2165 EndZ=0
  constraints (18):
    c: Coincident(g-3,g0)
    c: Coincident(g0,g-4)
    c: Coincident(g0,g1)
    c: Coincident(g1,g-6)
    c: Coincident(g1,g2)
    c: Coincident(g2,g-6)
    c: Coincident(g2,g3)
    c: Coincident(g3,g4)
    c: Coincident(g4,g5)
    c: Coincident(g5,g-5)
    c: Coincident(g5,g6)
    c: Coincident(g6,g-5)
    c: Coincident(g6,g7)
    c: Coincident(g7,g0)
    c: Horizontal(g4)
    c: Vertical(g5)
    c: DistanceX(g-8,g3) = 70
    c: DistanceY(g-7,g4) = 57.5
FEATURE [Sketcher::SketchObject] Sketch051
  ExternalGeometry = -> [Wall007,Wall020,Wall009,Wall011,Wall002,Wall004]
  Placement = pos=(13615,9815,0) rot=(0.707107,-0.707107,0;3.14159rad)
  sketch-geometry (8):
    g0: LineSegment StartX=115 StartY=-2105 StartZ=0 EndX=115 EndY=13385 EndZ=0
    g1: LineSegment StartX=115 StartY=13385 StartZ=0 EndX=9585 EndY=13385 EndZ=0
    g2: LineSegment StartX=9585 StartY=13385 StartZ=0 EndX=9585 EndY=8305 EndZ=0
    g3: LineSegment StartX=9585 StartY=8305 StartZ=0 EndX=6165 EndY=8305 EndZ=0
    g4: LineSegment StartX=6165 StartY=8305 StartZ=0 EndX=6165 EndY=2105 EndZ=0
    g5: LineSegment StartX=6165 StartY=2105 StartZ=0 EndX=9585 EndY=2105 EndZ=0
    g6: LineSegment StartX=9585 StartY=2105 StartZ=0 EndX=9585 EndY=-2105 EndZ=0
    g7: LineSegment StartX=9585 StartY=-2105 StartZ=0 EndX=115 EndY=-2105 EndZ=0
  constraints (24):
    c: Vertical(g0)
    c: Coincident(g0,g1)
    c: Horizontal(g1)
    c: Coincident(g1,g2)
    c: Vertical(g2)
    c: Coincident(g2,g3)
    c: Horizontal(g3)
    c: Coincident(g3,g4)
    c: Vertical(g4)
    c: Coincident(g4,g5)
    c: Horizontal(g5)
    c: Coincident(g5,g6)
    c: Vertical(g6)
    c: Coincident(g6,g7)
    c: Coincident(g7,g0)
    c: Horizontal(g7)
    c: DistanceX(g0,g-8) = 0
    c: DistanceY(g0,g-8) = 70
    c: DistanceX(g-6,g5) = 70
    c: DistanceY(g-6,g5) = 0
    c: DistanceX(g-6,g4) = 300
    c: DistanceY(g3,g-5) = 0
    c: DistanceX(g-5,g2) = 70
    c: DistanceY(g-4,g1) = 0
FEATURE [Sketcher::SketchObject] Sketch053
  ExternalGeometry = -> [Structure057,Wall009]
  Placement = pos=(5390,1975,2360) rot=(0,1,0;3.14159rad)
  sketch-geometry (8):
    g0: LineSegment StartX=-150 StartY=1675 StartZ=0 EndX=-5890 EndY=1675 EndZ=0
    g1: LineSegment StartX=-5890 StartY=1675 StartZ=0 EndX=-5890 EndY=995 EndZ=0
    g2: LineSegment StartX=-5890 StartY=995 StartZ=0 EndX=-2390 EndY=995 EndZ=0
    g3: LineSegment StartX=-2390 StartY=995 StartZ=0 EndX=-2390 EndY=-3155 EndZ=0
    g4: LineSegment StartX=-2390 StartY=-3155 StartZ=0 EndX=-520 EndY=-3155 EndZ=0
    g5: LineSegment StartX=-520 StartY=-3155 StartZ=0 EndX=-520 EndY=995 EndZ=0
    g6: LineSegment StartX=-520 StartY=995 StartZ=0 EndX=-150 EndY=995 EndZ=0
    g7: LineSegment StartX=-150 StartY=995 StartZ=0 EndX=-150 EndY=1675 EndZ=0
  constraints (24):
    c: Horizontal(g0)
    c: Coincident(g0,g1)
    c: Vertical(g1)
    c: Coincident(g1,g2)
    c: Horizontal(g2)
    c: Coincident(g2,g3)
    c: Vertical(g3)
    c: Coincident(g3,g4)
    c: Horizontal(g4)
    c: Coincident(g4,g5)
    c: Vertical(g5)
    c: Coincident(g5,g6)
    c: Coincident(g6,g7)
    c: Coincident(g7,g0)
    c: Vertical(g7)
    c: Equal(g7,g1)
    c: Equal(g3,g5)
    c: DistanceY(g7,g7) = 680
    c: DistanceY(g5,g5) = 4150
    c: DistanceX(g2,g2) = 3500
    c: DistanceX(g4,g4) = 1870
    c: DistanceX(g0,g0) = 5740
    c: DistanceX(g0,g-4) = 0
    c: DistanceY(g-4,g0) = 3350
FEATURE [Part::FeaturePython] Structure120  label="OuterBeamCumSlab"  # Arch/BIM 118 (typed FeaturePython)
  Base = -> Sketch053
  FaceMaker = 0
  Height = 150
  HorizontalArea = 11663700
  IfcData = IfcUID=2EOo39T3990fX3YSUNgM9o,+2 more (map truncated)
  IfcType = 118
  Length = 0
  Material = -> Material
  MoveBase = false
  MoveWithHost = false
  Nodes = (8) [(5540,3650,2360),(11280,3650,2360),(11280,2970,2360),(7780,2970,2360),(7780,-1180,2360),(5910,-1180,2360),(5910,2970,2360),(5540,2970,2360)]
  NodesOffset = 0
  Normal = (0,0,0)
  PerimeterLength = 21140
  Placement = pos=(9.09e-13,9.09e-13,150) rot=(0,0,1;0rad)
  PredefinedType = 4
  Tag = Archi
  VerticalArea = 3171000
  Width = 300
FEATURE [Part::FeaturePython] Wall023  label="Partition_walls"  # Arch/BIM 166 (typed FeaturePython)
  Align = 2
  Area = 157176250
  Base = -> Sketch056
  BlockHeight = 0
  BlockLength = 0
  CountBroken = 0
  CountEntire = 0
  Face = 0
  Height = 3500
  HorizontalArea = 0
  IfcData = IfcUID=0AozOKA5v99uvgwsZASWNS,+2 more (map truncated)
  IfcType = 166
  Joint = 0
  Length = 44907.5
  MakeBlocks = false
  Material = -> Material002
  MoveBase = false
  MoveWithHost = false
  Normal = (0,0,0)
  OffsetFirst = 0
  OffsetSecond = 0
  PerimeterLength = 0
  PredefinedType = 0
  Subtractions = -> [Structure029,Structure055,Structure005,Structure041,Structure038,Structure053,Structure009,Structure051,Structure036,Structure030,Structure006,Structure035,Structure010,Structure050,Structure034,Structure049,Structure007,Structure048,Structure031,Structure043,Structure042,Structure057,Structure056,Window030,Window034]
  VerticalArea = 0
  Width = 115
FEATURE [App::GeometryPython] BuildingPart001  label="Level 0"  # Arch/BIM 14 (typed FeaturePython)
  Area = 318320850
  CompositionType = 0
  Elevation = 0
  Group = -> [Structure028,Structure029,Structure030,Structure031,Structure032,Structure033,Structure034,Structure035,Structure036,Structure037,Structure038,Structure066,Structure040,Structure041,Structure042,Structure043,Structure044,Structure046,Structure047,Structure048,Structure049,Structure050,Structure051,Structure052,Structure053,Structure054,Structure055,Structure056,Structure057,Structure,Structure001,+42 more]
  Height = 3500
  HeightPropagate = true
  IfcData = IfcUID=2$8jNcgnr3VvLHJeePoEF$,+2 more (map truncated)
  IfcType = 14
  LevelOffset = 0
  LongName = Floor
  expr: Elevation = .Placement.Base.z
FEATURE [Part::FeaturePython] Window028  label="Door"  # Arch/BIM 41 (typed FeaturePython)
  Area = 2000000
  Base = -> Sketch057
  Frame = 50
  Height = 2000
  HoleDepth = 0
  HoleWire = 0
  HorizontalArea = 0
  Hosts = -> [Wall023]
  IfcData = IfcUID=2uW1r6xjnCxB4Zasa2OEhv,+2 more (map truncated)
  IfcType = 41
  LouvreSpacing = 0
  LouvreWidth = 0
  Material = -> Material001
  MoveBase = false
  MoveWithHost = true
  Normal = (-1,0,0)
  Opening = 0
  OperationType = 0
  OverallHeight = 2000
  OverallWidth = 1000
  PerimeterLength = 0
  Placement = pos=(0,350,0) rot=(0,0,1;0rad)
  PredefinedType = 0
  Preset = 6
  SymbolElevation = false
  SymbolPlan = false
  VerticalArea = 0
  Width = 1000
  WindowParts = OuterFrame | Frame | Wire0,Wire1 | 50.0+V | 0.0+V | Door | Glass panel | Wire1 | 5.0 | 10.0+V
  expr: OverallHeight = .Height.Value
  expr: OverallWidth = .Width.Value
FEATURE [Part::FeaturePython] Window029  label="Door001"  # Arch/BIM 41 (typed FeaturePython)
  Area = 2000000
  Base = -> Sketch058
  Frame = 50
  Height = 2000
  HoleDepth = 0
  HoleWire = 0
  HorizontalArea = 0
  Hosts = -> [Wall023]
  IfcData = IfcUID=2P_eaBFNzD4QRUdIN4kvHx,+2 more (map truncated)
  IfcType = 41
  LouvreSpacing = 0
  LouvreWidth = 0
  Material = -> Material001
  MoveBase = false
  MoveWithHost = true
  Normal = (-1,0,0)
  Opening = 0
  OperationType = 0
  OverallHeight = 2000
  OverallWidth = 1000
  PerimeterLength = 0
  Placement = pos=(0,350,0) rot=(0,0,1;0rad)
  PredefinedType = 0
  Preset = 6
  SymbolElevation = false
  SymbolPlan = false
  VerticalArea = 0
  Width = 1000
  WindowParts = OuterFrame | Frame | Wire0,Wire1 | 50.0+V | 0.0+V | Door | Glass panel | Wire1 | 5.0 | 10.0+V
  expr: OverallHeight = .Height.Value
  expr: OverallWidth = .Width.Value
FEATURE [Part::FeaturePython] Window031  label="Door003"  # Arch/BIM 41 (typed FeaturePython)
  Area = 3000000
  Base = -> Sketch062
  Frame = 50
  Height = 2000
  HoleDepth = 0
  HoleWire = 0
  HorizontalArea = 0
  Hosts = -> [Wall023]
  IfcData = IfcUID=1Ba8QdpKT9xREZOjDP1rxY,+2 more (map truncated)
  IfcType = 41
  LouvreSpacing = 0
  LouvreWidth = 0
  Material = -> Material001
  MoveBase = false
  MoveWithHost = true
  Normal = (0,1,-2e-16)
  Opening = 0
  OperationType = 0
  OverallHeight = 2000
  OverallWidth = 1500
  PerimeterLength = 0
  Placement = pos=(500,0,0) rot=(0,0,1;0rad)
  PredefinedType = 0
  Preset = 6
  SymbolElevation = false
  SymbolPlan = false
  VerticalArea = 0
  Width = 1500
  WindowParts = OuterFrame | Frame | Wire0,Wire1 | 50.0+V | 0.0+V | Door | Glass panel | Wire1 | 5.0 | 10.0+V
  expr: OverallHeight = .Height.Value
  expr: OverallWidth = .Width.Value
FEATURE [Part::FeaturePython] Window032  label="Door004"  # Arch/BIM 41 (typed FeaturePython)
  Area = 2000000
  Base = -> Sketch063
  Frame = 50
  Height = 2000
  HoleDepth = 0
  HoleWire = 0
  HorizontalArea = 0
  Hosts = -> [Wall023]
  IfcData = IfcUID=18xaHiOGDDtOafn_7s4cj$,+2 more (map truncated)
  IfcType = 41
  LouvreSpacing = 0
  LouvreWidth = 0
  Material = -> Material001
  MoveBase = false
  MoveWithHost = true
  Normal = (0,1,-2e-16)
  Opening = 0
  OperationType = 0
  OverallHeight = 2000
  OverallWidth = 1000
  PerimeterLength = 0
  Placement = pos=(150,0,0) rot=(0,0,1;0rad)
  PredefinedType = 0
  Preset = 6
  SymbolElevation = false
  SymbolPlan = false
  VerticalArea = 0
  Width = 1000
  WindowParts = OuterFrame | Frame | Wire0,Wire1 | 50.0+V | 0.0+V | Door | Solid panel | Wire1 | 5.0 | 10.0+V
  expr: OverallHeight = .Height.Value
  expr: OverallWidth = .Width.Value
FEATURE [Part::FeaturePython] Window035  label="Door007"  # Arch/BIM 41 (typed FeaturePython)
  Area = 2000000
  Base = -> Sketch068
  Frame = 50
  Height = 2000
  HoleDepth = 0
  HoleWire = 0
  HorizontalArea = 0
  Hosts = -> [Wall023]
  IfcData = IfcUID=2_AvIQfW50CAmwKQc5pWJ7,+2 more (map truncated)
  IfcType = 41
  LouvreSpacing = 0
  LouvreWidth = 0
  Material = -> Material001
  MoveBase = false
  MoveWithHost = true
  Normal = (1,0,0)
  Opening = 0
  OperationType = 0
  OverallHeight = 2000
  OverallWidth = 1000
  PerimeterLength = 0
  Placement = pos=(0,-3400,0) rot=(0,0,1;0rad)
  PredefinedType = 0
  Preset = 6
  SymbolElevation = false
  SymbolPlan = false
  VerticalArea = 0
  Width = 1000
  WindowParts = OuterFrame | Frame | Wire0,Wire1 | 50.0+V | 0.0+V | Door | Glass panel | Wire1 | 5.0 | 10.0+V
  expr: OverallWidth = .Width.Value
  expr: OverallHeight = .Height.Value
FEATURE [Part::FeaturePython] Window036  label="Door008"  # Arch/BIM 41 (typed FeaturePython)
  Area = 2000000
  Base = -> Sketch071
  Frame = 50
  Height = 2000
  HoleDepth = 0
  HoleWire = 0
  HorizontalArea = 0
  Hosts = -> [Wall023]
  IfcData = IfcUID=3HAS_VHP90SR2hZvpO_iQs,+2 more (map truncated)
  IfcType = 41
  LouvreSpacing = 0
  LouvreWidth = 0
  Material = -> Material001
  MoveBase = false
  MoveWithHost = true
  Normal = (0,1,-2e-16)
  Opening = 0
  OperationType = 0
  OverallHeight = 2000
  OverallWidth = 1000
  PerimeterLength = 0
  Placement = pos=(150,-50,0) rot=(0,0,1;0rad)
  PredefinedType = 0
  Preset = 6
  SymbolElevation = false
  SymbolPlan = false
  VerticalArea = 0
  Width = 1000
  WindowParts = OuterFrame | Frame | Wire0,Wire1 | 40.0+V | 0.0+V | Door | Glass panel | Wire1 | 5.0 | 10.0+V
  expr: OverallHeight = .Height.Value
  expr: OverallWidth = .Width.Value
FEATURE [App::MaterialObjectPython] Material003  label="Ceramic Tiles"  # material (typed FeaturePython)
  Description = Floor Finishes
  Material = Color=(0.9568627450980393, 0.9568627450980393, 0.9568627450980393),Description=Floor Finishes,+5 more (map truncated)
  Transparency = 0
FEATURE [Part::FeaturePython] Structure099  label="Roof_Floor_Finish"  # Arch/BIM 118 (typed FeaturePython)
  Base = -> Sketch048
  FaceMaker = 0
  Height = 50
  HorizontalArea = 124060300
  IfcData = IfcUID=1aQsbPTjb6nf_w6LDeNGdM,+2 more (map truncated)
  IfcType = 118
  Length = 0
  Material = -> Material003
  MoveBase = false
  MoveWithHost = false
  Nodes = (8) [(5310,3880,3650),(11510,3880,3650),(11510,230,3650),(15720,230,3650),(15720,9700,3650),(230,9700,3650),(230,230,3650),(5310,230,3650)]
  NodesOffset = 0
  Normal = (0,0,0)
  PerimeterLength = 57220
  Placement = pos=(0,0,125) rot=(0,0,1;0rad)
  PredefinedType = 0
  Tag = Roof
  VerticalArea = 2861000
  Width = 300
FEATURE [Part::FeaturePython] Structure118  label="Floor_Floor_Finish"  # Arch/BIM 118 (typed FeaturePython)
  Base = -> Sketch051
  FaceMaker = 0
  Height = 50
  HorizontalArea = 0
  IfcData = IfcUID=0eOSciMx1BuQl10YBUzhUa,+2 more (map truncated)
  IfcType = 118
  Length = 0
  Material = -> Material003
  MoveBase = false
  MoveWithHost = false
  Nodes = (8) [(15720,9700,0),(230,9700,0),(230,230,0),(5310,230,0),(5310,3650,0),(11510,3650,0),(11510,230,0),(15720,230,0)]
  NodesOffset = 0
  Normal = (0,0,0)
  PerimeterLength = 0
  PredefinedType = 0
  Subtractions = -> [Wall009,Wall011,Structure005,Structure009,Structure010,Structure006,Structure008,Structure007,Structure,Structure002,Structure003,Structure004,Structure011]
  Tag = FloorLayers
  VerticalArea = 0
  Width = 300
FEATURE [App::MaterialObjectPython] Material004  label="Lean Concrete"  # material (typed FeaturePython)
  Description = Lean Concrete
  Material = AuthorAndLicense=Concrete-Generic,CardName=Concrete-Generic,Color=(0.20392156862745098, 0.20392156862745098, 0.20392156862745098),+11 more (map truncated)
  ProductURL = https://en.wikipedia.org/wiki/Concrete
  Transparency = 0
FEATURE [Part::FeaturePython] Structure093  label="Roof_Lean_Conc"  # Arch/BIM 118 (typed FeaturePython)
  Base = -> Sketch046
  FaceMaker = 0
  Height = 50
  HorizontalArea = 124060300
  IfcData = IfcUID=0msAnLerHFBvQPrJzmGYCR,+2 more (map truncated)
  IfcType = 118
  Length = 0
  Material = -> Material004
  MoveBase = false
  MoveWithHost = false
  Nodes = (8) [(5310,3880,3650),(11510,3880,3650),(11510,230,3650),(15720,230,3650),(15720,9700,3650),(230,9700,3650),(230,230,3650),(5310,230,3650)]
  NodesOffset = 0
  Normal = (0,0,0)
  PerimeterLength = 57220
  Placement = pos=(0,0,75) rot=(0,0,1;0rad)
  PredefinedType = 0
  Tag = Roof
  VerticalArea = 2861000
  Width = 300
FEATURE [Part::FeaturePython] Structure117  label="Floor_Lean_Conc"  # Arch/BIM 118 (typed FeaturePython)
  Base = -> Sketch050
  FaceMaker = 0
  Height = 50
  HorizontalArea = 0
  IfcData = IfcUID=1JAsfsU$b6dAxgO5DMs1IZ,+2 more (map truncated)
  IfcType = 118
  Length = 0
  Material = -> Material004
  MoveBase = false
  MoveWithHost = false
  Nodes = (2) [(7899.26,5485.63,0),(7899.26,5485.63,-75)]
  NodesOffset = 0
  Normal = (0,0,0)
  PerimeterLength = 0
  PredefinedType = 0
  Subtractions = -> [Structure102,Structure101,Structure107,Structure108,Structure112,Structure104,Structure111,Structure110,Structure113]
  Tag = FloorLayers
  VerticalArea = 0
  Width = 300
FEATURE [App::MaterialObjectPython] Material005  label="Brick Blast"  # material (typed FeaturePython)
  Description = Brick Blast
  Material = Color=(0.5607843137254902, 0.023529411764705882, 0.023529411764705882),Description=Brick Blast,+4 more (map truncated)
  Transparency = 0
FEATURE [Part::FeaturePython] Structure087  label="Roof_Brick_Bast"  # Arch/BIM 118 (typed FeaturePython)
  Base = -> Sketch044
  FaceMaker = 0
  Height = 75
  HorizontalArea = 124060300
  IfcData = IfcUID=2gluSVvwrFSg4cLgdUTff_,+2 more (map truncated)
  IfcType = 118
  Length = 0
  Material = -> Material005
  MoveBase = false
  MoveWithHost = false
  Nodes = (8) [(5310,3880,3650),(11510,3880,3650),(11510,230,3650),(15720,230,3650),(15720,9700,3650),(230,9700,3650),(230,230,3650),(5310,230,3650)]
  NodesOffset = 0
  Normal = (0,0,0)
  PerimeterLength = 57220
  PredefinedType = 0
  Tag = Roof
  VerticalArea = 4291500
  Width = 300
FEATURE [Part::FeaturePython] Structure100  label="Floor_Brick_Blast"  # Arch/BIM 118 (typed FeaturePython)
  Base = -> Sketch049
  FaceMaker = 0
  Height = 75
  HorizontalArea = 0
  IfcData = IfcUID=1r47atV9973QAexYuabytB,+2 more (map truncated)
  IfcType = 118
  Length = 0
  Material = -> Material005
  MoveBase = false
  MoveWithHost = false
  Nodes = (2) [(7899.26,5485.63,0),(7899.26,5485.63,-75)]
  NodesOffset = 0
  Normal = (0,0,0)
  PerimeterLength = 0
  Placement = pos=(0,0,-50) rot=(0,0,1;0rad)
  PredefinedType = 0
  Subtractions = -> [Structure005,Structure006,Structure022,Structure024,Structure025,Structure021,Structure027,Structure026,Structure045]
  Tag = FloorLayers
  VerticalArea = 0
  Width = 300
FEATURE [App::DocumentObjectGroupPython] MaterialContainer  label="Materials"  # scripted group (container) (typed FeaturePython)
  Group = -> [Material,Material001,Material002,Material003,Material004,Material005]
FEATURE [Spreadsheet::Sheet] Result
  cells = A1=Walls; A2=Label; B2=Height; C2=Width; D2=Length; E2=Area; F2=BlockHeight; G2=BlockLength; H2=($CountEntire * 2); I2=($CountBroken * 2); A3=W001; B3=3200.00 mm; C3=230.00 mm; D3=4940.00 mm; E3=15.81 m^2; F3=76.00 mm; G3=228.00 mm; H3='1016; I3='430; A4=W002; B4=3200.00 mm; C4=230.00 mm; D4=4070.00 mm; E4=13.02 m^2; F4=76.00 mm; G4=228.00 mm; H4='946; I4='294; A5=W003; B5=3200.00 mm; C5=230.00 mm; D5=4700.00 mm; E5=15.04 m^2; F5=76.00 mm; G5=228.00 mm; H5='632; I5='580; A6=W004; B6=3200.00 mm; C6=230.00 mm; D6=4330.00 mm; E6=13.86 m^2; F6=76.00 mm; G6=228.00 mm; H6='896; I6='400; A7=W006; B7=3200.00 mm; C7=230.00 mm; D7=5740.00 mm; E7=18.37 m^2; F7=76.00 mm; G7=228.00 mm; H7='1044; I7='390; A8=W007; B8=3200.00 mm; C8=230.00 mm; D8=4940.00 mm; E8=15.81 m^2; F8=76.00 mm; G8=228.00 mm; H8='1228; I8='322; A9=W008; B9=3200.00 mm; C9=230.00 mm; D9=4330.00 mm; E9=13.86 m^2; F9=76.00 mm; G9=228.00 mm; H9='904; I9='306; A10=W010; B10=3200.00 mm; C10=230.00 mm; D10=3650.00 mm; E10=11.68 m^2; F10=76.00 mm; G10=228.00 mm; H10='940; I10='244; A11=W011; B11=3200.00 mm; C11=230.00 mm; D11=3650.00 mm; E11=11.68 m^2; F11=76.00 mm; G11=228.00 mm; H11='952; I11='232; A12=W005; B12=3200.00 mm; C12=230.00 mm; D12=4070.00 mm; E12=13.02 m^2; F12=76.00 mm; G12=228.00 mm; H12='892; I12='356; A13=W009; B13=3200.00 mm; C13=230.00 mm; D13=4700.00 mm; E13=15.04 m^2; F13=76.00 mm; G13=228.00 mm; H13='1022; I13='312; A14=W012; B14=690.00 mm; C14=230.00 mm; D14=5740.00 mm; E14=3.96 m^2; F14=76.00 mm; G14=228.00 mm; H14='368; I14='82; A15=Partition_walls; B15=3500.00 mm; C15=115.00 mm; D15=44.91 m; E15=157.18 m^2; F15=0.00 mm; G15=0.00 mm; H15='0; I15='0; A16=Perapit_W101; B16=500.00 mm; C16=230.00 mm; D16=5540.00 mm; E16=2.77 m^2; F16=76.00 mm; G16=228.00 mm; H16='590; I16='144; A17=Perapit_W102; B17=500.00 mm; C17=230.00 mm; D17=9700.00 mm; E17=4.85 m^2; F17=76.00 mm; G17=228.00 mm; H17='390; I17='102; A18=Perapit_W103; B18=500.00 mm; C18=230.00 mm; D18=15.72 m; E18=7.86 m^2; F18=76.00 mm; G18=228.00 mm; H18='650; I18='154; A19=Perapit_W104; B19=500.00 mm; C19=230.00 mm; D19=9700.00 mm; E19=4.85 m^2; F19=76.00 mm; G19=228.00 mm; H19='390; I19='102; A20=Perapit_W105; B20=500.00 mm; C20=230.00 mm; D20=4440.00 mm; E20=2.22 m^2; F20=76.00 mm; G20=228.00 mm; H20='170; I20='58; A21=Perapit_W106; B21=500.00 mm; C21=230.00 mm; D21=3420.00 mm; E21=1.71 m^2; F21=76.00 mm; G21=228.00 mm; H21='130; I21='50; A22=Perapit_W107; B22=500.00 mm; C22=230.00 mm; D22=3420.00 mm; E22=1.71 m^2; F22=76.00 mm; G22=228.00 mm; H22='130; I22='50; A23=Perapit_W108; B23=500.00 mm; C23=230.00 mm; D23=6200.00 mm; E23=3.10 m^2; F23=76.00 mm; G23=228.00 mm; H23='250; I23='74; A26=Total walls area and Brick Count; +443 more cells
FEATURE [App::FeaturePython] Report  # WARN: FeaturePython — macro-defined, semantics opaque (R4)
  Result = -> Result
  SkipComputing = false
FEATURE [Sketcher::SketchObject] WallTrace026
  Placement = pos=(0,0,3650) rot=(0,0,1;0rad)
  sketch-geometry (1):
    g0: LineSegment StartX=5540 StartY=0 StartZ=0 EndX=0 EndY=0 EndZ=0
FEATURE [Sketcher::SketchObject] WallTrace027
  Placement = pos=(0,0,3650) rot=(0,0,1;0rad)
  sketch-geometry (1):
    g0: LineSegment StartX=0 StartY=230 StartZ=0 EndX=0 EndY=9930 EndZ=0
FEATURE [Part::FeaturePython] Wall026  label="Perapit_W102"  # Arch/BIM 166 (typed FeaturePython)
  Align = 0
  Area = 4850000
  Base = -> WallTrace027
  BlockHeight = 76
  BlockLength = 228
  CountBroken = 51
  CountEntire = 195
  Face = 0
  Height = 500
  HorizontalArea = 2231000
  IfcData = IfcUID=2Q1jTEa293xPozuet5qOHJ,+2 more (map truncated)
  IfcType = 166
  Joint = 10
  Length = 9700
  MakeBlocks = false
  Material = -> Material002
  MoveBase = false
  MoveWithHost = false
  Normal = (0,0,1)
  OffsetFirst = 0
  OffsetSecond = 0
  PerimeterLength = 19860
  PredefinedType = 0
  VerticalArea = 9930000
  Width = 230
FEATURE [Sketcher::SketchObject] WallTrace028
  Placement = pos=(0,0,3650) rot=(0,0,1;0rad)
  sketch-geometry (1):
    g0: LineSegment StartX=230 StartY=9930 StartZ=0 EndX=15950 EndY=9930 EndZ=0
FEATURE [Part::FeaturePython] Wall027  label="Perapit_W103"  # Arch/BIM 166 (typed FeaturePython)
  Align = 0
  Area = 7860000
  Base = -> WallTrace028
  BlockHeight = 76
  BlockLength = 228
  CountBroken = 77
  CountEntire = 325
  Face = 0
  Height = 500
  HorizontalArea = 3.6156e+06
  IfcData = IfcUID=1zkIF0_fvCORJMTXvOMfvv,+2 more (map truncated)
  IfcType = 166
  Joint = 10
  Length = 15720
  MakeBlocks = false
  Material = -> Material002
  MoveBase = false
  MoveWithHost = false
  Normal = (0,0,1)
  OffsetFirst = 0
  OffsetSecond = 0
  PerimeterLength = 31900
  PredefinedType = 0
  VerticalArea = 1.595e+07
  Width = 230
FEATURE [Sketcher::SketchObject] WallTrace029
  Placement = pos=(0,0,3650) rot=(0,0,1;0rad)
  sketch-geometry (1):
    g0: LineSegment StartX=15950 StartY=9700 StartZ=0 EndX=15950 EndY=0 EndZ=0
FEATURE [Part::FeaturePython] Wall028  label="Perapit_W104"  # Arch/BIM 166 (typed FeaturePython)
  Align = 0
  Area = 4850000
  Base = -> WallTrace029
  BlockHeight = 76
  BlockLength = 228
  CountBroken = 51
  CountEntire = 195
  Face = 0
  Height = 500
  HorizontalArea = 2231000
  IfcData = IfcUID=3fAjNsZTzC4vMYj3t3cYjj,+2 more (map truncated)
  IfcType = 166
  Joint = 10
  Length = 9700
  MakeBlocks = false
  Material = -> Material002
  MoveBase = false
  MoveWithHost = false
  Normal = (0,0,1)
  OffsetFirst = 0
  OffsetSecond = 0
  PerimeterLength = 19860
  PredefinedType = 0
  VerticalArea = 9930000
  Width = 230
FEATURE [Sketcher::SketchObject] WallTrace030
  Placement = pos=(0,0,3650) rot=(0,0,1;0rad)
  sketch-geometry (1):
    g0: LineSegment StartX=15720 StartY=0 StartZ=0 EndX=11280 EndY=0 EndZ=0
FEATURE [Part::FeaturePython] Wall029  label="Perapit_W105"  # Arch/BIM 166 (typed FeaturePython)
  Align = 0
  Area = 2220000
  Base = -> WallTrace030
  BlockHeight = 76
  BlockLength = 228
  CountBroken = 29
  CountEntire = 85
  Face = 0
  Height = 500
  HorizontalArea = 1021200
  IfcData = IfcUID=1k75SJIvH8NwHh5wPnW_BG,+2 more (map truncated)
  IfcType = 166
  Joint = 10
  Length = 4440
  MakeBlocks = false
  Material = -> Material002
  MoveBase = false
  MoveWithHost = false
  Normal = (0,0,1)
  OffsetFirst = 0
  OffsetSecond = 0
  PerimeterLength = 9340
  PredefinedType = 0
  VerticalArea = 4670000
  Width = 230
FEATURE [Sketcher::SketchObject] WallTrace031
  Placement = pos=(0,0,3650) rot=(0,0,1;0rad)
  sketch-geometry (1):
    g0: LineSegment StartX=11280 StartY=230 StartZ=0 EndX=11280 EndY=3650 EndZ=0
FEATURE [Part::FeaturePython] Wall030  label="Perapit_W106"  # Arch/BIM 166 (typed FeaturePython)
  Align = 0
  Area = 1710000
  Base = -> WallTrace031
  BlockHeight = 76
  BlockLength = 228
  CountBroken = 25
  CountEntire = 65
  Face = 0
  Height = 500
  HorizontalArea = 786600
  IfcData = IfcUID=3EMluLc6HFM9HE4NiRRg2y,+2 more (map truncated)
  IfcType = 166
  Joint = 10
  Length = 3420
  MakeBlocks = false
  Material = -> Material002
  MoveBase = false
  MoveWithHost = false
  Normal = (0,0,1)
  OffsetFirst = 0
  OffsetSecond = 0
  PerimeterLength = 7300
  PredefinedType = 0
  VerticalArea = 3.65e+06
  Width = 230
FEATURE [Sketcher::SketchObject] WallTrace032
  Placement = pos=(0,0,3650) rot=(0,0,1;0rad)
  sketch-geometry (1):
    g0: LineSegment StartX=5540 StartY=230 StartZ=0 EndX=5540 EndY=3650 EndZ=0
FEATURE [Part::FeaturePython] Wall031  label="Perapit_W107"  # Arch/BIM 166 (typed FeaturePython)
  Align = 1
  Area = 1710000
  Base = -> WallTrace032
  BlockHeight = 76
  BlockLength = 228
  CountBroken = 25
  CountEntire = 65
  Face = 0
  Height = 500
  HorizontalArea = 786600
  IfcData = IfcUID=0xSpMgRU16_BfXwxCfoehY,+2 more (map truncated)
  IfcType = 166
  Joint = 10
  Length = 3420
  MakeBlocks = false
  Material = -> Material002
  MoveBase = false
  MoveWithHost = false
  Normal = (0,0,1)
  OffsetFirst = 0
  OffsetSecond = 0
  PerimeterLength = 7300
  PredefinedType = 0
  VerticalArea = 3.65e+06
  Width = 230
FEATURE [Sketcher::SketchObject] WallTrace033
  Placement = pos=(0,0,3650) rot=(0,0,1;0rad)
  sketch-geometry (1):
    g0: LineSegment StartX=11510 StartY=3650 StartZ=0 EndX=5310 EndY=3650 EndZ=0
FEATURE [Part::FeaturePython] Wall032  label="Perapit_W108"  # Arch/BIM 166 (typed FeaturePython)
  Align = 0
  Area = 3100000
  Base = -> WallTrace033
  BlockHeight = 76
  BlockLength = 228
  CountBroken = 37
  CountEntire = 125
  Face = 0
  Height = 500
  HorizontalArea = 1.426e+06
  IfcData = IfcUID=0YVWsHcw50qvpe87eWxs7r,+2 more (map truncated)
  IfcType = 166
  Joint = 10
  Length = 6200
  MakeBlocks = false
  Material = -> Material002
  MoveBase = false
  MoveWithHost = false
  Normal = (0,0,1)
  OffsetFirst = 0
  OffsetSecond = 0
  PerimeterLength = 12860
  PredefinedType = 0
  VerticalArea = 6.43e+06
  Width = 230
FEATURE [Part::FeaturePython] Wall024  label="Perapit_W101"  # Arch/BIM 166 (typed FeaturePython)
  Additions = -> [Wall026,Wall027,Wall028,Wall029,Wall030,Wall031,Wall032]
  Align = 0
  Area = 2770000
  Base = -> WallTrace026
  BlockHeight = 76
  BlockLength = 228
  CountBroken = 72
  CountEntire = 295
  Face = 0
  Height = 500
  HorizontalArea = 1.33722e+07
  IfcData = IfcUID=3iamIUEvXCMPLsst43VFoZ,+2 more (map truncated)
  IfcType = 166
  Joint = 10
  Length = 5540
  MakeBlocks = false
  Material = -> Material002
  MoveBase = false
  MoveWithHost = false
  Normal = (0,0,1)
  OffsetFirst = 0
  OffsetSecond = 0
  PerimeterLength = 59060
  PredefinedType = 0
  VerticalArea = 58140000
  Width = 230
FEATURE [App::GeometryPython] BuildingPart002  label="Level 1"  # Arch/BIM 14 (typed FeaturePython)
  Area = 2770000
  CompositionType = 0
  Elevation = 3500
  Group = -> [Wall024,Structure087,Structure099,Structure093,Structure058,Structure060,Structure062,Structure063,Structure064,WPProxy001,Structure065]
  Height = 3500
  HeightPropagate = true
  IfcData = IfcUID=1EfhMSwu582AAWXj9gamfu,+2 more (map truncated)
  IfcType = 14
  LevelOffset = 0
  LongName = Floor
  Placement = pos=(0,0,3500) rot=(0,0,1;0rad)
  expr: Elevation = .Placement.Base.z
FEATURE [TechDraw::DrawSVGTemplate] Template
  EditableTexts = AUTHOR_NAME=Karanvir Singh Sohal,DN=1,DRAWING_TITLE=GNDEC dispensary,FC-DATE=30/03/2020,FC-REV=REV A,FC-SC=1:0.02,FC-SH=1,FC-SI=A0,+6 more (map truncated)
  Height = 841
  Orientation = 1
  Width = 1189
FEATURE [TechDraw::DrawViewPart] View004  label="top"
  CoarseView = true
  Direction = (0,0,1)
  Focus = 100
  HardHidden = false
  IsoCount = 0
  IsoHidden = false
  IsoVisible = false
  LockPosition = true
  Perspective = false
  Rotation = 180
  Scale = 0.02
  ScaleType = 0
  SeamHidden = false
  SeamVisible = true
  SmoothHidden = false
  SmoothVisible = true
  Source = -> [Wall024,Structure087,Structure099,Structure083,Structure081,Structure084,Structure085,Structure120,Structure121,Structure086,Structure067,Structure068,Structure070,Structure072,Structure074,Structure075,Structure076,Structure080,Structure078]
  X = 600
  XDirection = (-1,0,0)
  Y = 650
FEATURE [TechDraw::DrawViewDimension] Dimension
  Arbitrary = false
  FormatSpec = %.2f
  Inverted = false
  LockPosition = true
  MeasureType = 1
  OverTolerance = 0
  References2D = -> [View004]
  Rotation = 0
  ScaleType = 0
  TheoreticalExact = false
  Type = 1
  UnderTolerance = 0
  X = 4.28358
  Y = 140
FEATURE [TechDraw::DrawViewDimension] Dimension001
  Arbitrary = false
  FormatSpec = %.2f
  Inverted = false
  LockPosition = true
  MeasureType = 1
  OverTolerance = 0
  References2D = -> [View004]
  Rotation = 0
  ScaleType = 0
  TheoreticalExact = false
  Type = 2
  UnderTolerance = 0
  X = -190
  Y = 1.4201
FEATURE [TechDraw::DrawViewDimension] Dimension002
  Arbitrary = false
  FormatSpec = %.2f
  Inverted = false
  LockPosition = true
  MeasureType = 1
  OverTolerance = 0
  References2D = -> [View004]
  Rotation = 0
  ScaleType = 0
  TheoreticalExact = false
  Type = 2
  UnderTolerance = 0
  X = 56.3217
  Y = -64.2244
FEATURE [TechDraw::DrawViewDimension] Dimension003
  Arbitrary = false
  FormatSpec = %.2f
  Inverted = false
  LockPosition = true
  MeasureType = 1
  OverTolerance = 0
  References2D = -> [View004]
  Rotation = 0
  ScaleType = 0
  TheoreticalExact = false
  Type = 1
  UnderTolerance = 0
  X = 31.191
  Y = -24.8756
FEATURE [TechDraw::DrawViewDimension] Dimension004
  Arbitrary = false
  FormatSpec = %.2f
  Inverted = false
  LockPosition = true
  MeasureType = 1
  OverTolerance = 0
  References2D = -> [View004]
  Rotation = 0
  ScaleType = 0
  TheoreticalExact = false
  Type = 2
  UnderTolerance = 0
  X = 0.577364
  Y = -74.0517
FEATURE [TechDraw::DrawViewDimension] Dimension005
  Arbitrary = false
  FormatSpec = %.2f
  Inverted = false
  LockPosition = true
  MeasureType = 1
  OverTolerance = 0
  References2D = -> [View004]
  Rotation = 0
  ScaleType = 0
  TheoreticalExact = false
  Type = 1
  UnderTolerance = 0
  X = -22.509
  Y = -108
FEATURE [TechDraw::DrawViewDimension] Dimension006
  Arbitrary = false
  FormatSpec = %.2f
  Inverted = false
  LockPosition = true
  MeasureType = 1
  OverTolerance = 0
  References2D = -> [View004]
  Rotation = 0
  ScaleType = 0
  TheoreticalExact = false
  Type = 2
  UnderTolerance = 0
  X = -36.2743
  Y = -55.3517
FEATURE [TechDraw::DrawViewDimension] Dimension007
  Arbitrary = false
  FormatSpec = %.2f
  Inverted = false
  LockPosition = true
  MeasureType = 1
  OverTolerance = 0
  References2D = -> [View004]
  Rotation = 0
  ScaleType = 0
  TheoreticalExact = false
  Type = 2
  UnderTolerance = 0
  X = -27.5641
  Y = -68.6892
FEATURE [TechDraw::DrawViewDimension] Dimension008
  Arbitrary = false
  FormatSpec = %.2f
  Inverted = false
  LockPosition = true
  MeasureType = 1
  OverTolerance = 0
  References2D = -> [View004]
  Rotation = 0
  ScaleType = 0
  TheoreticalExact = false
  Type = 1
  UnderTolerance = 0
  X = -13.6874
  Y = -86.0932
FEATURE [TechDraw::DrawViewDimension] Dimension009
  Arbitrary = false
  FormatSpec = %.2f
  Inverted = false
  LockPosition = true
  MeasureType = 1
  OverTolerance = 0
  References2D = -> [View004]
  Rotation = 0
  ScaleType = 0
  TheoreticalExact = false
  Type = 1
  UnderTolerance = 0
  X = -62.4545
  Y = -38.0347
FEATURE [TechDraw::DrawViewDimension] Dimension010
  Arbitrary = false
  FormatSpec = %.2f
  Inverted = false
  LockPosition = true
  MeasureType = 1
  OverTolerance = 0
  References2D = -> [View004]
  Rotation = 0
  ScaleType = 0
  TheoreticalExact = false
  Type = 2
  UnderTolerance = 0
  X = -65.0579
  Y = -26.3
FEATURE [TechDraw::DrawViewDimension] Dimension011
  Arbitrary = false
  FormatSpec = %.2f
  Inverted = false
  LockPosition = true
  MeasureType = 1
  OverTolerance = 0
  References2D = -> [View004]
  Rotation = 0
  ScaleType = 0
  TheoreticalExact = false
  Type = 2
  UnderTolerance = 0
  X = 144.664
  Y = -110.659
FEATURE [TechDraw::DrawViewDimension] Dimension012
  Arbitrary = false
  FormatSpec = %.2f
  Inverted = false
  LockPosition = true
  MeasureType = 1
  OverTolerance = 0
  References2D = -> [View004]
  Rotation = 0
  ScaleType = 0
  TheoreticalExact = false
  Type = 1
  UnderTolerance = 0
  X = 177.622
  Y = -98.1802
FEATURE [TechDraw::DrawViewDimension] Dimension014
  Arbitrary = false
  FormatSpec = %.2f
  Inverted = false
  LockPosition = true
  MeasureType = 1
  OverTolerance = 0
  References2D = -> [View004]
  Rotation = 0
  ScaleType = 0
  TheoreticalExact = false
  Type = 1
  UnderTolerance = 0
  X = 106.291
  Y = -108
FEATURE [TechDraw::DrawViewDimension] Dimension015
  Arbitrary = false
  FormatSpec = %.2f
  Inverted = false
  LockPosition = true
  MeasureType = 1
  OverTolerance = 0
  References2D = -> [View004]
  Rotation = 0
  ScaleType = 0
  TheoreticalExact = false
  Type = 1
  UnderTolerance = 0
  X = 5
  Y = 130
FEATURE [TechDraw::DrawViewDimension] Dimension016
  Arbitrary = false
  FormatSpec = %.2f
  Inverted = false
  LockPosition = true
  MeasureType = 1
  OverTolerance = 0
  References2D = -> [View004]
  Rotation = 0
  ScaleType = 0
  TheoreticalExact = false
  Type = 2
  UnderTolerance = 0
  X = 176.248
  Y = -42.0787
FEATURE [TechDraw::DrawViewDimension] Dimension017
  Arbitrary = false
  FormatSpec = %.2f
  Inverted = false
  LockPosition = true
  MeasureType = 1
  OverTolerance = 0
  References2D = -> [View004]
  Rotation = 0
  ScaleType = 0
  TheoreticalExact = false
  Type = 0
  UnderTolerance = 0
  X = -99.9784
  Y = -125
FEATURE [TechDraw::DrawViewDimension] Dimension018
  Arbitrary = false
  FormatSpec = %.2f
  Inverted = false
  LockPosition = true
  MeasureType = 1
  OverTolerance = 0
  References2D = -> [View004]
  Rotation = 0
  ScaleType = 0
  TheoreticalExact = false
  Type = 1
  UnderTolerance = 0
  X = 116.058
  Y = -125
FEATURE [TechDraw::DrawViewDimension] Dimension019
  Arbitrary = false
  FormatSpec = %.2f
  Inverted = false
  LockPosition = true
  MeasureType = 1
  OverTolerance = 0
  References2D = -> [View004]
  Rotation = 0
  ScaleType = 0
  TheoreticalExact = false
  Type = 1
  UnderTolerance = 0
  X = 10.5184
  Y = -125
FEATURE [TechDraw::DrawViewDimension] Dimension020
  Arbitrary = false
  FormatSpec = %.2f
  Inverted = false
  LockPosition = true
  MeasureType = 1
  OverTolerance = 0
  References2D = -> [View004]
  Rotation = 0
  ScaleType = 0
  TheoreticalExact = false
  Type = 2
  UnderTolerance = 0
  X = -180
  Y = 39.5004
FEATURE [TechDraw::DrawViewDimension] Dimension021
  Arbitrary = false
  FormatSpec = %.2f
  Inverted = false
  LockPosition = true
  MeasureType = 1
  OverTolerance = 0
  References2D = -> [View004]
  Rotation = 0
  ScaleType = 0
  TheoreticalExact = false
  Type = 2
  UnderTolerance = 0
  X = -180
  Y = -44.5865
FEATURE [TechDraw::DrawViewAnnotation] Annotation
  Font = MS Shell Dlg 2
  LineSpace = 80
  LockPosition = false
  MaxWidth = -1
  Rotation = 0
  ScaleType = 0
  Text = Top Plan
  TextSize = 5
  TextStyle = 0
  X = 608.442
  Y = 509.766
FEATURE [TechDraw::DrawViewAnnotation] Annotation001
  Font = MS Shell Dlg 2
  LineSpace = 80
  LockPosition = false
  MaxWidth = -1
  Rotation = 0
  ScaleType = 0
  Text = Right Elevation(Hostel Side)
  TextSize = 5
  TextStyle = 0
  X = 1022.19
  Y = 326.511
FEATURE [TechDraw::DrawViewAnnotation] Annotation002
  Font = MS Shell Dlg 2
  LineSpace = 80
  LockPosition = false
  MaxWidth = -1
  Rotation = 0
  ScaleType = 0
  Text = Front Elevation
  TextSize = 5
  TextStyle = 0
  X = 614.332
  Y = 327.374
FEATURE [TechDraw::DrawViewAnnotation] Annotation003
  Font = MS Shell Dlg 2
  LineSpace = 80
  LockPosition = false
  MaxWidth = -1
  Rotation = 0
  ScaleType = 0
  Text = Back Elevation
  TextSize = 5
  TextStyle = 0
  X = 608.139
  Y = 128.625
FEATURE [TechDraw::DrawViewAnnotation] Annotation004
  Font = MS Shell Dlg 2
  LineSpace = 80
  LockPosition = false
  MaxWidth = -1
  Rotation = 0
  ScaleType = 0
  Text = Left Elevation(Basket Ball Court Side
  TextSize = 5
  TextStyle = 0
  X = 191.118
  Y = 323.978
FEATURE [TechDraw::DrawViewSymbol] ActiveView
  LockPosition = false
  Rotation = 0
  ScaleType = 2
  Symbol = <blob: 1147200 chars omitted>
  X = 1005.68
  Y = 206.459
FEATURE [TechDraw::DrawViewSymbol] ActiveView001
  LockPosition = false
  Rotation = 0
  ScaleType = 2
  Symbol = <blob: 1031860 chars omitted>
  X = 202.091
  Y = 202.704
FEATURE [TechDraw::DrawViewSymbol] ActiveView002
  LockPosition = false
  Rotation = 0
  Scale = 1.3
  ScaleType = 2
  Symbol = <blob: 1103573 chars omitted>
  X = 1033.85
  Y = 664.582
FEATURE [TechDraw::DrawViewSymbol] ActiveView003
  LockPosition = false
  Rotation = 0
  Scale = 1.1
  ScaleType = 2
  Symbol = <blob: 1146448 chars omitted>
  X = 611.398
  Y = 76.9077
FEATURE [TechDraw::DrawViewSymbol] ActiveView004
  LockPosition = false
  Rotation = 0
  Scale = 1.3
  ScaleType = 2
  Symbol = <blob: 1102418 chars omitted>
  X = 224.622
  Y = 673.97
FEATURE [TechDraw::DrawSVGTemplate] Template001
  EditableTexts = AUTHOR_NAME=Karanvir Singh Sohal,DN=2,DRAWING_TITLE=GNDEC dispensary,FC-DATE=30/03/2020,FC-REV=REV A,FC-SC=1:0.02,FC-SH=1,FC-SI=A0,PN=1,+2 more (map truncated)
  Height = 841
  Orientation = 1
  Width = 1189
FEATURE [TechDraw::DrawViewPart] View005
  CoarseView = true
  Direction = (0,0,1)
  Focus = 100
  HardHidden = false
  IsoCount = 0
  IsoHidden = false
  IsoVisible = false
  LockPosition = true
  Perspective = false
  Rotation = 0
  Scale = 0.03
  ScaleType = 2
  SeamHidden = false
  SeamVisible = false
  SmoothHidden = false
  SmoothVisible = true
  Source = -> [Structure009,Structure011,Structure010,Structure008,Structure007,Structure006,Structure005,Structure004,Structure003,Structure002,Structure,Structure001]
  X = 450
  XDirection = (1,0,0)
  Y = 500
FEATURE [TechDraw::DrawViewPart] View006
  CoarseView = true
  Direction = (0,-1,0)
  Focus = 100
  HardHidden = false
  IsoCount = 0
  IsoHidden = false
  IsoVisible = false
  LockPosition = true
  Perspective = false
  Rotation = 0
  Scale = 0.03
  ScaleType = 0
  SeamHidden = false
  SeamVisible = false
  SmoothHidden = false
  SmoothVisible = true
  Source = -> [Structure001,Structure002,Structure003,Structure004,Structure005,Structure006,Structure007,Structure008,Structure009,Structure010,Structure011,Structure028,Structure029,Structure030,Structure031,Structure032,Structure033,Structure034,Structure035,Structure037,Structure036,Structure038,Structure066,Structure040,Structure041,Structure042,Structure043,Structure044,Structure047,Structure046,+27 more]
  X = 450
  XDirection = (1,0,0)
  Y = 150
FEATURE [TechDraw::DrawViewPart] View007
  CoarseView = true
  Direction = (1,0,0)
  Focus = 100
  HardHidden = false
  IsoCount = 0
  IsoHidden = false
  IsoVisible = false
  LockPosition = true
  Perspective = false
  Rotation = 90
  Scale = 0.03
  ScaleType = 0
  SeamHidden = false
  SeamVisible = false
  SmoothHidden = false
  SmoothVisible = true
  Source = -> [Structure001,Structure002,Structure003,Structure004,Structure005,Structure006,Structure007,Structure008,Structure009,Structure010,Structure011,Structure028,Structure029,Structure030,Structure031,Structure032,Structure033,Structure034,Structure035,Structure037,Structure036,Structure038,Structure066,Structure040,Structure041,Structure042,Structure043,Structure044,Structure047,Structure046,+27 more]
  X = 900
  XDirection = (0,1,0)
  Y = 500
FEATURE [TechDraw::DrawViewDimension] Dimension101
  Arbitrary = true
  FormatSpec = 2400
  Inverted = false
  LockPosition = true
  MeasureType = 1
  OverTolerance = 0
  References2D = -> [View005]
  Rotation = 0
  ScaleType = 0
  TheoreticalExact = false
  Type = 1
  UnderTolerance = 0
  X = -233.879
  Y = -96.4718
FEATURE [TechDraw::DrawViewDimension] Dimension102
  Arbitrary = false
  FormatSpec = %.2f
  Inverted = false
  LockPosition = true
  MeasureType = 1
  OverTolerance = 0
  References2D = -> [View005]
  Rotation = 0
  ScaleType = 0
  TheoreticalExact = false
  Type = 2
  UnderTolerance = 0
  X = -194.9
  Y = -145.306
FEATURE [TechDraw::DrawViewDimension] Dimension103
  Arbitrary = false
  FormatSpec = %.2f
  Inverted = false
  LockPosition = true
  MeasureType = 1
  OverTolerance = 0
  References2D = -> [View005]
  Rotation = 0
  ScaleType = 0
  TheoreticalExact = false
  Type = 1
  UnderTolerance = 0
  X = -77.55
  Y = -41.5503
FEATURE [TechDraw::DrawViewDimension] Dimension104
  Arbitrary = false
  FormatSpec = %.2f
  Inverted = false
  LockPosition = true
  MeasureType = 1
  OverTolerance = 0
  References2D = -> [View005]
  Rotation = 0
  ScaleType = 0
  TheoreticalExact = false
  Type = 2
  UnderTolerance = 0
  X = -30.9133
  Y = 6.01367
FEATURE [TechDraw::DrawViewDimension] Dimension105
  Arbitrary = false
  FormatSpec = %.2f
  Inverted = false
  LockPosition = true
  MeasureType = 1
  OverTolerance = 0
  References2D = -> [View006]
  Rotation = 0
  ScaleType = 0
  TheoreticalExact = false
  Type = 1
  UnderTolerance = 0
  X = -234.75
  Y = -87
FEATURE [TechDraw::DrawViewDimension] Dimension106
  Arbitrary = false
  FormatSpec = %.2f
  Inverted = false
  LockPosition = true
  MeasureType = 1
  OverTolerance = 0
  References2D = -> [View006]
  Rotation = 0
  ScaleType = 0
  TheoreticalExact = false
  Type = 1
  UnderTolerance = 0
  X = -77.55
  Y = -87
FEATURE [TechDraw::DrawViewDimension] Dimension107
  Arbitrary = false
  FormatSpec = %.2f
  Inverted = false
  LockPosition = true
  MeasureType = 1
  OverTolerance = 0
  References2D = -> [View006]
  Rotation = 0
  ScaleType = 0
  TheoreticalExact = false
  Type = 1
  UnderTolerance = 0
  X = 103.65
  Y = -87
FEATURE [TechDraw::DrawViewDimension] Dimension108
  Arbitrary = false
  FormatSpec = %.2f
  Inverted = false
  LockPosition = true
  MeasureType = 1
  OverTolerance = 0
  References2D = -> [View006]
  Rotation = 0
  ScaleType = 0
  TheoreticalExact = false
  Type = 1
  UnderTolerance = 0
  X = 234.75
  Y = -87
FEATURE [TechDraw::DrawViewDimension] Dimension109
  Arbitrary = false
  FormatSpec = %.2f
  Inverted = false
  LockPosition = true
  MeasureType = 1
  OverTolerance = 0
  References2D = -> [View006]
  Rotation = 0
  ScaleType = 0
  TheoreticalExact = false
  Type = 2
  UnderTolerance = 0
  X = -280
  Y = 10.5245
FEATURE [TechDraw::DrawViewDimension] Dimension110
  Arbitrary = false
  FormatSpec = %.2f
  Inverted = false
  LockPosition = true
  MeasureType = 1
  OverTolerance = 0
  References2D = -> [View006]
  Rotation = 0
  ScaleType = 0
  TheoreticalExact = false
  Type = 2
  UnderTolerance = 0
  X = -280
  Y = -75
FEATURE [TechDraw::DrawViewDimension] Dimension111
  Arbitrary = false
  FormatSpec = %.2f
  Inverted = false
  LockPosition = true
  MeasureType = 1
  OverTolerance = 0
  References2D = -> [View006]
  Rotation = 0
  ScaleType = 0
  TheoreticalExact = false
  Type = 2
  UnderTolerance = 0
  X = -190
  Y = -70.5303
FEATURE [TechDraw::DrawViewDimension] Dimension112
  Arbitrary = false
  FormatSpec = %.2f
  Inverted = false
  LockPosition = true
  MeasureType = 1
  OverTolerance = 0
  References2D = -> [View006]
  Rotation = 0
  ScaleType = 0
  TheoreticalExact = false
  Type = 2
  UnderTolerance = 0
  X = -190
  Y = -50.8601
FEATURE [TechDraw::DrawViewDimension] Dimension113
  Arbitrary = false
  FormatSpec = %.2f
  Inverted = false
  LockPosition = true
  MeasureType = 1
  OverTolerance = 0
  References2D = -> [View006]
  Rotation = 0
  ScaleType = 0
  TheoreticalExact = false
  Type = 2
  UnderTolerance = 0
  X = -190
  Y = -28.6567
FEATURE [TechDraw::DrawViewDimension] Dimension114
  Arbitrary = false
  FormatSpec = %.2f
  Inverted = false
  LockPosition = true
  MeasureType = 1
  OverTolerance = 0
  References2D = -> [View006]
  Rotation = 0
  ScaleType = 0
  TheoreticalExact = false
  Type = 2
  UnderTolerance = 0
  X = -190
  Y = 12.9
FEATURE [TechDraw::DrawViewDimension] Dimension115
  Arbitrary = false
  FormatSpec = %.2f
  Inverted = false
  LockPosition = true
  MeasureType = 1
  OverTolerance = 0
  References2D = -> [View006]
  Rotation = 0
  ScaleType = 0
  TheoreticalExact = false
  Type = 2
  UnderTolerance = 0
  X = -200.784
  Y = 41.0499
FEATURE [TechDraw::DrawViewDimension] Dimension116
  Arbitrary = false
  FormatSpec = %.2f
  Inverted = false
  LockPosition = true
  MeasureType = 1
  OverTolerance = 0
  References2D = -> [View006]
  Rotation = 0
  ScaleType = 0
  TheoreticalExact = false
  Type = 2
  UnderTolerance = 0
  X = -190.257
  Y = 63.9203
FEATURE [TechDraw::DrawViewDimension] Dimension117
  Arbitrary = false
  FormatSpec = %.2f
  Inverted = false
  LockPosition = true
  MeasureType = 1
  OverTolerance = 0
  References2D = -> [View006]
  Rotation = 0
  ScaleType = 0
  TheoreticalExact = false
  Type = 2
  UnderTolerance = 0
  X = -201.297
  Y = 91.0944
FEATURE [TechDraw::DrawViewDimension] Dimension118
  Arbitrary = false
  FormatSpec = %.2f
  Inverted = false
  LockPosition = true
  MeasureType = 1
  OverTolerance = 0
  References2D = -> [View006]
  Rotation = 0
  ScaleType = 0
  TheoreticalExact = false
  Type = 2
  UnderTolerance = 0
  X = -190
  Y = -87.8576
FEATURE [TechDraw::DrawViewDimension] Dimension119
  Arbitrary = false
  FormatSpec = %.2f
  Inverted = false
  LockPosition = true
  MeasureType = 1
  OverTolerance = 0
  References2D = -> [View007]
  Rotation = 0
  ScaleType = 0
  TheoreticalExact = false
  Type = 2
  UnderTolerance = 0
  X = 87
  Y = -144.45
FEATURE [TechDraw::DrawViewDimension] Dimension120
  Arbitrary = false
  FormatSpec = %.2f
  Inverted = false
  LockPosition = true
  MeasureType = 1
  OverTolerance = 0
  References2D = -> [View007]
  Rotation = 0
  ScaleType = 0
  TheoreticalExact = false
  Type = 2
  UnderTolerance = 0
  X = 87
  Y = 5.55
FEATURE [TechDraw::DrawViewDimension] Dimension121
  Arbitrary = false
  FormatSpec = %.2f
  Inverted = false
  LockPosition = true
  MeasureType = 1
  OverTolerance = 0
  References2D = -> [View007]
  Rotation = 0
  ScaleType = 0
  TheoreticalExact = false
  Type = 2
  UnderTolerance = 0
  X = 87
  Y = 144.45
FEATURE [TechDraw::DrawViewDimension] Dimension122
  Arbitrary = false
  FormatSpec = %.2f
  Inverted = false
  LockPosition = true
  MeasureType = 1
  OverTolerance = 0
  References2D = -> [View007]
  Rotation = 0
  ScaleType = 0
  TheoreticalExact = false
  Type = 2
  UnderTolerance = 0
  X = -29.5262
  Y = 132.368
FEATURE [TechDraw::DrawViewDimension] Dimension123
  Arbitrary = false
  FormatSpec = %.2f
  Inverted = false
  LockPosition = true
  MeasureType = 1
  OverTolerance = 0
  References2D = -> [View007]
  Rotation = 0
  ScaleType = 0
  TheoreticalExact = false
  Type = 2
  UnderTolerance = 0
  X = -29.7631
  Y = -7.24234
FEATURE [TechDraw::DrawViewDimension] Dimension124
  Arbitrary = false
  FormatSpec = %.2f
  Inverted = false
  LockPosition = true
  MeasureType = 1
  OverTolerance = 0
  References2D = -> [View007]
  Rotation = 0
  ScaleType = 0
  TheoreticalExact = false
  Type = 2
  UnderTolerance = 0
  X = -30
  Y = -156.283
FEATURE [TechDraw::DrawViewDimension] Dimension125
  Arbitrary = false
  FormatSpec = %.2f
  Inverted = false
  LockPosition = true
  MeasureType = 1
  OverTolerance = 0
  References2D = -> [View005]
  Rotation = 0
  ScaleType = 0
  TheoreticalExact = false
  Type = 1
  UnderTolerance = 0
  X = -231.219
  Y = 200
FEATURE [TechDraw::DrawViewDimension] Dimension126
  Arbitrary = false
  FormatSpec = %.2f
  Inverted = false
  LockPosition = true
  MeasureType = 1
  OverTolerance = 0
  References2D = -> [View005]
  Rotation = 0
  ScaleType = 0
  TheoreticalExact = false
  Type = 1
  UnderTolerance = 0
  X = -156.15
  Y = 200
FEATURE [TechDraw::DrawViewDimension] Dimension127
  Arbitrary = false
  FormatSpec = %.2f
  Inverted = false
  LockPosition = true
  MeasureType = 1
  OverTolerance = 0
  References2D = -> [View005]
  Rotation = 0
  ScaleType = 0
  TheoreticalExact = false
  Type = 1
  UnderTolerance = 0
  X = 13.05
  Y = 200
FEATURE [TechDraw::DrawViewDimension] Dimension128
  Arbitrary = false
  FormatSpec = %.2f
  Inverted = false
  LockPosition = true
  MeasureType = 1
  OverTolerance = 0
  References2D = -> [View005]
  Rotation = 0
  ScaleType = 0
  TheoreticalExact = false
  Type = 1
  UnderTolerance = 0
  X = 169.2
  Y = 200
FEATURE [TechDraw::DrawViewDimension] Dimension129
  Arbitrary = false
  FormatSpec = %.2f
  Inverted = false
  LockPosition = true
  MeasureType = 1
  OverTolerance = 0
  References2D = -> [View005]
  Rotation = 0
  ScaleType = 0
  TheoreticalExact = false
  Type = 1
  UnderTolerance = 0
  X = -77.55
  Y = 200
FEATURE [TechDraw::DrawViewDimension] Dimension130
  Arbitrary = false
  FormatSpec = %.2f
  Inverted = false
  LockPosition = true
  MeasureType = 1
  OverTolerance = 0
  References2D = -> [View005]
  Rotation = 0
  ScaleType = 0
  TheoreticalExact = false
  Type = 1
  UnderTolerance = 0
  X = 103.65
  Y = 200
FEATURE [TechDraw::DrawViewDimension] Dimension131
  Arbitrary = false
  FormatSpec = %.2f
  Inverted = false
  LockPosition = true
  MeasureType = 1
  OverTolerance = 0
  References2D = -> [View005]
  Rotation = 0
  ScaleType = 0
  TheoreticalExact = false
  Type = 1
  UnderTolerance = 0
  X = 234.75
  Y = 200
FEATURE [TechDraw::DrawViewDimension] Dimension132
  Arbitrary = false
  FormatSpec = %.2f
  Inverted = false
  LockPosition = true
  MeasureType = 1
  OverTolerance = 0
  References2D = -> [View005]
  Rotation = 0
  ScaleType = 0
  TheoreticalExact = false
  Type = 2
  UnderTolerance = 0
  X = 151.813
  Y = 5.55
FEATURE [TechDraw::DrawViewDimension] Dimension133
  Arbitrary = false
  FormatSpec = %.2f
  Inverted = false
  LockPosition = true
  MeasureType = 1
  OverTolerance = 0
  References2D = -> [View005]
  Rotation = 0
  ScaleType = 0
  TheoreticalExact = false
  Type = 1
  UnderTolerance = 0
  X = 103.65
  Y = -41.7322
FEATURE [TechDraw::DrawViewDimension] Dimension134
  Arbitrary = false
  FormatSpec = %.2f
  Inverted = false
  LockPosition = true
  MeasureType = 1
  OverTolerance = 0
  References2D = -> [View005]
  Rotation = 0
  ScaleType = 0
  TheoreticalExact = false
  Type = 2
  UnderTolerance = 0
  X = 285
  Y = 144.45
FEATURE [TechDraw::DrawViewDimension] Dimension135
  Arbitrary = false
  FormatSpec = %.2f
  Inverted = false
  LockPosition = true
  MeasureType = 1
  OverTolerance = 0
  References2D = -> [View005]
  Rotation = 0
  ScaleType = 0
  TheoreticalExact = false
  Type = 2
  UnderTolerance = 0
  X = 285
  Y = 75
FEATURE [TechDraw::DrawViewDimension] Dimension136
  Arbitrary = false
  FormatSpec = %.2f
  Inverted = false
  LockPosition = true
  MeasureType = 1
  OverTolerance = 0
  References2D = -> [View005]
  Rotation = 0
  ScaleType = 0
  TheoreticalExact = false
  Type = 2
  UnderTolerance = 0
  X = 285
  Y = 5.55
FEATURE [TechDraw::DrawViewDimension] Dimension137
  Arbitrary = false
  FormatSpec = %.2f
  Inverted = false
  LockPosition = true
  MeasureType = 1
  OverTolerance = 0
  References2D = -> [View005]
  Rotation = 0
  ScaleType = 0
  TheoreticalExact = false
  Type = 2
  UnderTolerance = 0
  X = 285
  Y = -69.45
FEATURE [TechDraw::DrawViewDimension] Dimension138
  Arbitrary = false
  FormatSpec = %.2f
  Inverted = false
  LockPosition = true
  MeasureType = 1
  OverTolerance = 0
  References2D = -> [View005]
  Rotation = 0
  ScaleType = 0
  TheoreticalExact = false
  Type = 2
  UnderTolerance = 0
  X = 285
  Y = -144.45
FEATURE [TechDraw::DrawPage] Page001  label="Footing"
  KeepUpdated = true
  NextBalloonIndex = 1
  ProjectionType = 1
  Template = -> Template001
  Views = -> [View005,View006,View007,Dimension101,Dimension102,Dimension103,Dimension104,Dimension105,Dimension106,Dimension107,Dimension108,Dimension109,Dimension110,Dimension111,Dimension112,Dimension113,Dimension114,Dimension115,Dimension116,Dimension117,Dimension118,Dimension119,Dimension120,Dimension121,Dimension122,Dimension123,Dimension124,Dimension125,Dimension126,Dimension127,Dimension128,+10 more]
FEATURE [Part::Wedge] Wedge001
  AttacherType = Attacher::AttachEngine3D
  Placement = pos=(-900,1200,-1600) rot=(1,0,0;1.5708rad)
  X2max = 1200
  X2min = 900
  Xmax = 2100
  Xmin = 0
  Ymax = 100
  Ymin = 0
  Z2max = 1200
  Z2min = 900
  Zmax = 2100
  Zmin = 0
FEATURE [Part::Box] Box  label="Cube"
  AttacherType = Attacher::AttachEngine3D
  Height = 200
  Length = 2100
  Placement = pos=(-900,-900,-1800) rot=(0,0,1;0rad)
  Width = 2100
FEATURE [Part::MultiFuse] Fusion
  Shapes = -> [Wedge001,Box]
FEATURE [Part::FeaturePython] Structure122  label="Footing001"  # Arch/BIM 77 (typed FeaturePython)
  Base = -> Fusion
  FaceMaker = 0
  Height = 200
  HorizontalArea = 4.41e+06
  IfcData = attributes={"GlobalId": {"name": "GlobalId", "type": "IfcGloballyUniqueId", "is_enum": false, "enum_values": []}, "Description": {"... (+532 chars omitted),+1 more (map truncated)
  IfcType = 77
  Length = 0
  Material = -> Material
  MoveBase = false
  MoveWithHost = false
  NodesOffset = 0
  Normal = (0,0,0)
  PerimeterLength = 0
  PredefinedType = 5
  Tag = IsolatedFooting
  VerticalArea = 1680000
  Width = 100
FEATURE [Part::FeaturePython] Structure123  label="Footing002"  # Arch/BIM 77 (typed FeaturePython)
  Base = -> Fusion
  FaceMaker = 0
  Height = 200
  HorizontalArea = 4410000
  IfcData = attributes={"GlobalId": {"name": "GlobalId", "type": "IfcGloballyUniqueId", "is_enum": false, "enum_values": []}, "Description": {"... (+532 chars omitted),+1 more (map truncated)
  IfcType = 77
  Length = 0
  Material = -> Material
  MoveBase = false
  MoveWithHost = false
  NodesOffset = 0
  Normal = (0,0,0)
  PerimeterLength = 0
  Placement = pos=(0,5000,1.1369e-12) rot=(0,0,1;0rad)
  PredefinedType = 5
  Tag = IsolatedFooting
  VerticalArea = 1.68e+06
  Width = 100
FEATURE [Part::FeaturePython] Structure124  label="Footing003"  # Arch/BIM 77 (typed FeaturePython)
  Base = -> Fusion
  FaceMaker = 0
  Height = 200
  HorizontalArea = 4410000
  IfcData = attributes={"GlobalId": {"name": "GlobalId", "type": "IfcGloballyUniqueId", "is_enum": false, "enum_values": []}, "Description": {"... (+532 chars omitted),+1 more (map truncated)
  IfcType = 77
  Length = 0
  Material = -> Material
  MoveBase = false
  MoveWithHost = false
  NodesOffset = 0
  Normal = (0,0,0)
  PerimeterLength = 0
  Placement = pos=(0,9630,2.046e-12) rot=(0,0,1;0rad)
  PredefinedType = 5
  Tag = IsolatedFooting
  VerticalArea = 1.68e+06
  Width = 100
FEATURE [Part::FeaturePython] Structure125  label="Footing004"  # Arch/BIM 77 (typed FeaturePython)
  Base = -> Fusion
  FaceMaker = 0
  Height = 200
  HorizontalArea = 4410000
  IfcData = attributes={"GlobalId": {"name": "GlobalId", "type": "IfcGloballyUniqueId", "is_enum": false, "enum_values": []}, "Description": {"... (+532 chars omitted),+1 more (map truncated)
  IfcType = 77
  Length = 0
  Material = -> Material
  MoveBase = false
  MoveWithHost = false
  NodesOffset = 0
  Normal = (0,0,0)
  PerimeterLength = 0
  Placement = pos=(5240,0,0) rot=(0,0,1;0rad)
  PredefinedType = 5
  Tag = IsolatedFooting
  VerticalArea = 1.68e+06
  Width = 100
FEATURE [Part::FeaturePython] Structure126  label="Footing005"  # Arch/BIM 77 (typed FeaturePython)
  Base = -> Fusion
  FaceMaker = 0
  Height = 200
  HorizontalArea = 4410000
  IfcData = attributes={"GlobalId": {"name": "GlobalId", "type": "IfcGloballyUniqueId", "is_enum": false, "enum_values": []}, "Description": {"... (+532 chars omitted),+1 more (map truncated)
  IfcType = 77
  Length = 0
  Material = -> Material
  MoveBase = false
  MoveWithHost = false
  NodesOffset = 0
  Normal = (0,0,0)
  PerimeterLength = 0
  Placement = pos=(5240,9630,2.046e-12) rot=(0,0,1;0rad)
  PredefinedType = 5
  Tag = IsolatedFooting
  VerticalArea = 1.68e+06
  Width = 100
FEATURE [Part::FeaturePython] Structure127  label="Footing006"  # Arch/BIM 77 (typed FeaturePython)
  Base = -> Fusion
  FaceMaker = 0
  Height = 200
  HorizontalArea = 4410000
  IfcData = attributes={"GlobalId": {"name": "GlobalId", "type": "IfcGloballyUniqueId", "is_enum": false, "enum_values": []}, "Description": {"... (+532 chars omitted),+1 more (map truncated)
  IfcType = 77
  Length = 0
  Material = -> Material
  MoveBase = false
  MoveWithHost = false
  NodesOffset = 0
  Normal = (0,0,0)
  PerimeterLength = 0
  Placement = pos=(11280,0,0) rot=(0,0,1;0rad)
  PredefinedType = 5
  Tag = IsolatedFooting
  VerticalArea = 1.68e+06
  Width = 100
FEATURE [Part::FeaturePython] Structure128  label="Footing007"  # Arch/BIM 77 (typed FeaturePython)
  Base = -> Fusion
  FaceMaker = 0
  Height = 200
  HorizontalArea = 4410000
  IfcData = attributes={"GlobalId": {"name": "GlobalId", "type": "IfcGloballyUniqueId", "is_enum": false, "enum_values": []}, "Description": {"... (+532 chars omitted),+1 more (map truncated)
  IfcType = 77
  Length = 0
  Material = -> Material
  MoveBase = false
  MoveWithHost = false
  NodesOffset = 0
  Normal = (0,0,0)
  PerimeterLength = 0
  Placement = pos=(11280,9630,2.046e-12) rot=(0,0,1;0rad)
  PredefinedType = 5
  Tag = IsolatedFooting
  VerticalArea = 1.68e+06
  Width = 100
FEATURE [Part::FeaturePython] Structure129  label="Footing008"  # Arch/BIM 77 (typed FeaturePython)
  Base = -> Fusion
  FaceMaker = 0
  Height = 200
  HorizontalArea = 4410000
  IfcData = attributes={"GlobalId": {"name": "GlobalId", "type": "IfcGloballyUniqueId", "is_enum": false, "enum_values": []}, "Description": {"... (+532 chars omitted),+1 more (map truncated)
  IfcType = 77
  Length = 0
  Material = -> Material
  MoveBase = false
  MoveWithHost = false
  NodesOffset = 0
  Normal = (0,0,0)
  PerimeterLength = 0
  Placement = pos=(15650,-1.08e-12,0) rot=(0,0,1;0rad)
  PredefinedType = 5
  Tag = IsolatedFooting
  VerticalArea = 1.68e+06
  Width = 100
FEATURE [Part::FeaturePython] Structure130  label="Footing009"  # Arch/BIM 77 (typed FeaturePython)
  Base = -> Fusion
  FaceMaker = 0
  Height = 200
  HorizontalArea = 4410000
  IfcData = attributes={"GlobalId": {"name": "GlobalId", "type": "IfcGloballyUniqueId", "is_enum": false, "enum_values": []}, "Description": {"... (+532 chars omitted),+1 more (map truncated)
  IfcType = 77
  Length = 0
  Material = -> Material
  MoveBase = false
  MoveWithHost = false
  NodesOffset = 0
  Normal = (0,0,0)
  PerimeterLength = 0
  Placement = pos=(15650,5000,1.1369e-12) rot=(0,0,1;0rad)
  PredefinedType = 5
  Tag = IsolatedFooting
  VerticalArea = 1.68e+06
  Width = 100
FEATURE [Part::FeaturePython] Structure131  label="Footing010"  # Arch/BIM 77 (typed FeaturePython)
  Base = -> Fusion
  FaceMaker = 0
  Height = 200
  HorizontalArea = 4410000
  IfcData = attributes={"GlobalId": {"name": "GlobalId", "type": "IfcGloballyUniqueId", "is_enum": false, "enum_values": []}, "Description": {"... (+532 chars omitted),+1 more (map truncated)
  IfcType = 77
  Length = 0
  Material = -> Material
  MoveBase = false
  MoveWithHost = false
  NodesOffset = 0
  Normal = (0,0,0)
  PerimeterLength = 0
  Placement = pos=(15650,9630,2.046e-12) rot=(0,0,1;0rad)
  PredefinedType = 5
  Tag = IsolatedFooting
  VerticalArea = 1.68e+06
  Width = 100
FEATURE [Part::Wedge] Wedge
  AttacherType = Attacher::AttachEngine3D
  Placement = pos=(4140,6400,-1600) rot=(1,0,0;1.5708rad)
  X2max = 1400
  X2min = 1100
  Xmax = 2500
  Xmin = 0
  Ymax = 100
  Ymin = 0
  Z2max = 1400
  Z2min = 1100
  Zmax = 2500
  Zmin = 0
FEATURE [Part::Box] Box001  label="Cube001"
  AttacherType = Attacher::AttachEngine3D
  Height = 200
  Length = 2500
  Placement = pos=(4140,3900,-1800) rot=(0,0,1;0rad)
  Width = 2500
FEATURE [Part::MultiFuse] Fusion001
  Shapes = -> [Wedge,Box001]
FEATURE [Part::FeaturePython] Structure132  label="Footing011"  # Arch/BIM 77 (typed FeaturePython)
  Base = -> Fusion001
  FaceMaker = 0
  Height = 200
  HorizontalArea = 6250000
  IfcData = attributes={"GlobalId": {"name": "GlobalId", "type": "IfcGloballyUniqueId", "is_enum": false, "enum_values": []}, "Description": {"... (+532 chars omitted),+1 more (map truncated)
  IfcType = 77
  Length = 0
  Material = -> Material
  MoveBase = false
  MoveWithHost = false
  NodesOffset = 0
  Normal = (0,0,0)
  PerimeterLength = 0
  PredefinedType = 5
  Tag = IsolatedFooting
  VerticalArea = 2e+06
  Width = 100
FEATURE [Part::FeaturePython] Structure133  label="Footing012"  # Arch/BIM 77 (typed FeaturePython)
  Base = -> Fusion001
  FaceMaker = 0
  Height = 200
  HorizontalArea = 6250000
  IfcData = attributes={"GlobalId": {"name": "GlobalId", "type": "IfcGloballyUniqueId", "is_enum": false, "enum_values": []}, "Description": {"... (+532 chars omitted),+1 more (map truncated)
  IfcType = 77
  Length = 0
  Material = -> Material
  MoveBase = false
  MoveWithHost = false
  NodesOffset = 0
  Normal = (0,0,0)
  PerimeterLength = 0
  Placement = pos=(6040,0,0) rot=(0,0,1;0rad)
  PredefinedType = 5
  Tag = IsolatedFooting
  VerticalArea = 2e+06
  Width = 100
FEATURE [App::GeometryPython] BuildingPart003  label="Level -1"  # Arch/BIM 14 (typed FeaturePython)
  Area = 0
  CompositionType = 0
  Elevation = -1500
  Group = -> [Structure012,Structure013,Structure014,Structure015,Structure016,Structure017,Structure018,Structure019,Structure020,Structure021,Structure022,Structure024,Structure025,Structure026,Structure027,Structure045,Structure100,Structure118,Structure117,Structure119,WPProxy002,Structure122,Structure123,Structure124,Structure125,Structure126,Structure127,Structure128,Structure129,Structure130,+3 more]
  Height = 3500
  HeightPropagate = true
  IfcData = IfcUID=3bCgYqOxHFHwDNueoVtF$4,+2 more (map truncated)
  IfcType = 14
  LevelOffset = 0
  LongName = Floor
  Placement = pos=(0,0,-1500) rot=(0,0,1;0rad)
  expr: Elevation = .Placement.Base.z
FEATURE [App::GeometryPython] BuildingPart  label="Dispensary"  # Arch/BIM 10 (typed FeaturePython)
  Area = 321090850
  BuildingType = 121
  CompositionType = 0
  ElevationOfRefHeight = 0
  ElevationOfTerrain = 0
  Group = -> [App__DocumentObjectGroup,BuildingPart003,BuildingPart001,BuildingPart002]
  Height = 0
  HeightPropagate = true
  IfcData = IfcUID=2SuarbfS19wPLqEiYPNat2,+2 more (map truncated)
  IfcType = 10
  LevelOffset = 0
  LongName = Building
FEATURE [TechDraw::DrawViewPart] View  label="Right"
  CoarseView = true
  Direction = (1,0,0)
  Focus = 100
  HardHidden = false
  IsoCount = 0
  IsoHidden = false
  IsoVisible = false
  LockPosition = true
  Perspective = false
  Rotation = 0
  Scale = 0.02
  ScaleType = 2
  SeamHidden = false
  SeamVisible = true
  SmoothHidden = false
  SmoothVisible = true
  Source = -> [BuildingPart]
  X = 1000
  XDirection = (0,1,0)
  Y = 400
FEATURE [TechDraw::DrawViewPart] View001  label="Back"
  CoarseView = true
  Direction = (0,1,0)
  Focus = 100
  HardHidden = false
  IsoCount = 0
  IsoHidden = false
  IsoVisible = false
  LockPosition = true
  Perspective = false
  Rotation = 0
  Scale = 0.02
  ScaleType = 2
  SeamHidden = false
  SeamVisible = true
  SmoothHidden = false
  SmoothVisible = true
  Source = -> [BuildingPart]
  X = 600
  XDirection = (-1,0,0)
  Y = 200
FEATURE [TechDraw::DrawViewPart] View002  label="Left"
  CoarseView = true
  Direction = (-1,0,0)
  Focus = 100
  HardHidden = false
  IsoCount = 0
  IsoHidden = false
  IsoVisible = false
  LockPosition = true
  Perspective = false
  Rotation = 0
  Scale = 0.02
  ScaleType = 2
  SeamHidden = false
  SeamVisible = true
  SmoothHidden = false
  SmoothVisible = true
  Source = -> [BuildingPart]
  X = 200
  XDirection = (0,-1,0)
  Y = 400
FEATURE [TechDraw::DrawViewPart] View003  label="Front"
  CoarseView = true
  Direction = (0,-1,0)
  Focus = 100
  HardHidden = false
  IsoCount = 0
  IsoHidden = false
  IsoVisible = false
  LockPosition = true
  Perspective = false
  Rotation = 0
  Scale = 0.02
  ScaleType = 2
  SeamHidden = false
  SeamVisible = true
  SmoothHidden = false
  SmoothVisible = true
  Source = -> [BuildingPart]
  X = 600
  XDirection = (1,0,0)
  Y = 400
FEATURE [TechDraw::DrawViewDimension] Dimension022
  Arbitrary = false
  FormatSpec = %.2f
  Inverted = false
  LockPosition = true
  MeasureType = 1
  OverTolerance = 0
  References2D = -> [View002]
  Rotation = 0
  ScaleType = 0
  TheoreticalExact = false
  Type = 2
  UnderTolerance = 0
  X = -118.472
  Y = 60.7819
FEATURE [TechDraw::DrawViewDimension] Dimension023
  Arbitrary = false
  FormatSpec = %.2f
  Inverted = false
  LockPosition = true
  MeasureType = 1
  OverTolerance = 0
  References2D = -> [View002]
  Rotation = 0
  ScaleType = 0
  TheoreticalExact = false
  Type = 2
  UnderTolerance = 0
  X = -124.559
  Y = 50.0397
FEATURE [TechDraw::DrawViewDimension] Dimension024
  Arbitrary = false
  FormatSpec = %.2f
  Inverted = false
  LockPosition = true
  MeasureType = 1
  OverTolerance = 0
  References2D = -> [View002]
  Rotation = 0
  ScaleType = 0
  TheoreticalExact = false
  Type = 1
  UnderTolerance = 0
  X = -13.6355
  Y = 73.2425
FEATURE [TechDraw::DrawViewDimension] Dimension025
  Arbitrary = false
  FormatSpec = %.2f
  Inverted = false
  LockPosition = true
  MeasureType = 1
  OverTolerance = 0
  References2D = -> [View002]
  Rotation = 0
  ScaleType = 0
  TheoreticalExact = false
  Type = 1
  UnderTolerance = 0
  X = -66.0274
  Y = 58
FEATURE [TechDraw::DrawViewDimension] Dimension026
  Arbitrary = false
  FormatSpec = %.2f
  Inverted = false
  LockPosition = true
  MeasureType = 1
  OverTolerance = 0
  References2D = -> [View002]
  Rotation = 0
  ScaleType = 0
  TheoreticalExact = false
  Type = 1
  UnderTolerance = 0
  X = 35.4109
  Y = 58
FEATURE [TechDraw::DrawViewDimension] Dimension027
  Arbitrary = false
  FormatSpec = %.2f
  Inverted = false
  LockPosition = true
  MeasureType = 1
  OverTolerance = 0
  References2D = -> [View002]
  Rotation = 0
  ScaleType = 0
  TheoreticalExact = false
  Type = 2
  UnderTolerance = 0
  X = 91.908
  Y = 56.1916
FEATURE [TechDraw::DrawViewDimension] Dimension028
  Arbitrary = false
  FormatSpec = %.2f
  Inverted = false
  LockPosition = true
  MeasureType = 1
  OverTolerance = 0
  References2D = -> [View002]
  Rotation = 0
  ScaleType = 0
  TheoreticalExact = false
  Type = 1
  UnderTolerance = 0
  X = -131.352
  Y = 22.9507
FEATURE [TechDraw::DrawViewDimension] Dimension029
  Arbitrary = false
  FormatSpec = %.2f
  Inverted = false
  LockPosition = true
  MeasureType = 1
  OverTolerance = 0
  References2D = -> [View002]
  Rotation = 0
  ScaleType = 0
  TheoreticalExact = false
  Type = 1
  UnderTolerance = 0
  X = 72.3
  Y = -5
FEATURE [TechDraw::DrawViewDimension] Dimension030
  Arbitrary = false
  FormatSpec = %.2f
  Inverted = false
  LockPosition = true
  MeasureType = 1
  OverTolerance = 0
  References2D = -> [View002]
  Rotation = 0
  ScaleType = 0
  TheoreticalExact = false
  Type = 1
  UnderTolerance = 0
  X = 39.8999
  Y = -5
FEATURE [TechDraw::DrawViewDimension] Dimension031
  Arbitrary = false
  FormatSpec = %.2f
  Inverted = false
  LockPosition = true
  MeasureType = 1
  OverTolerance = 0
  References2D = -> [View002]
  Rotation = 0
  ScaleType = 0
  TheoreticalExact = false
  Type = 1
  UnderTolerance = 0
  X = -2.60012
  Y = -5
FEATURE [TechDraw::DrawViewDimension] Dimension032
  Arbitrary = false
  FormatSpec = %.2f
  Inverted = false
  LockPosition = true
  MeasureType = 1
  OverTolerance = 0
  References2D = -> [View002]
  Rotation = 0
  ScaleType = 0
  TheoreticalExact = false
  Type = 1
  UnderTolerance = 0
  X = -45.1001
  Y = -5
FEATURE [TechDraw::DrawViewDimension] Dimension033
  Arbitrary = false
  FormatSpec = %.2f
  Inverted = false
  LockPosition = true
  MeasureType = 1
  OverTolerance = 0
  References2D = -> [View002]
  Rotation = 0
  ScaleType = 0
  TheoreticalExact = false
  Type = 1
  UnderTolerance = 0
  X = -87.9001
  Y = -5
FEATURE [TechDraw::DrawViewDimension] Dimension034
  Arbitrary = false
  FormatSpec = %.2f
  Inverted = false
  LockPosition = true
  MeasureType = 1
  OverTolerance = 0
  References2D = -> [View002]
  Rotation = 0
  ScaleType = 0
  TheoreticalExact = false
  Type = 2
  UnderTolerance = 0
  X = -119.285
  Y = -11.6427
FEATURE [TechDraw::DrawViewDimension] Dimension035
  Arbitrary = false
  FormatSpec = %.2f
  Inverted = false
  LockPosition = true
  MeasureType = 1
  OverTolerance = 0
  References2D = -> [View002]
  Rotation = 0
  ScaleType = 0
  TheoreticalExact = false
  Type = 2
  UnderTolerance = 0
  X = 13
  Y = 13.1945
FEATURE [TechDraw::DrawViewDimension] Dimension036
  Arbitrary = false
  FormatSpec = %.2f
  Inverted = false
  LockPosition = true
  MeasureType = 1
  OverTolerance = 0
  References2D = -> [View002]
  Rotation = 0
  ScaleType = 0
  TheoreticalExact = false
  Type = 2
  UnderTolerance = 0
  X = 13
  Y = -10.711
FEATURE [TechDraw::DrawViewDimension] Dimension037
  Arbitrary = false
  FormatSpec = %.2f
  Inverted = false
  LockPosition = true
  MeasureType = 1
  OverTolerance = 0
  References2D = -> [View002]
  Rotation = 0
  ScaleType = 0
  TheoreticalExact = false
  Type = 2
  UnderTolerance = 0
  X = 13
  Y = 35.6
FEATURE [TechDraw::DrawViewDimension] Dimension039
  Arbitrary = false
  FormatSpec = %.2f
  Inverted = false
  LockPosition = true
  MeasureType = 1
  OverTolerance = 0
  References2D = -> [View002]
  Rotation = 0
  ScaleType = 0
  TheoreticalExact = false
  Type = 2
  UnderTolerance = 0
  X = -55.3582
  Y = 14.0835
FEATURE [TechDraw::DrawViewDimension] Dimension040
  Arbitrary = false
  FormatSpec = %.2f
  Inverted = false
  LockPosition = true
  MeasureType = 1
  OverTolerance = 0
  References2D = -> [View]
  Rotation = 0
  ScaleType = 0
  TheoreticalExact = false
  Type = 1
  UnderTolerance = 0
  X = -95.3354
  Y = -40
FEATURE [TechDraw::DrawViewDimension] Dimension041
  Arbitrary = false
  FormatSpec = %.2f
  Inverted = false
  LockPosition = true
  MeasureType = 1
  OverTolerance = 0
  References2D = -> [View]
  Rotation = 0
  ScaleType = 0
  TheoreticalExact = false
  Type = 1
  UnderTolerance = 0
  X = 6.08056
  Y = -40
FEATURE [TechDraw::DrawViewDimension] Dimension042
  Arbitrary = false
  FormatSpec = %.2f
  Inverted = false
  LockPosition = true
  MeasureType = 1
  OverTolerance = 0
  References2D = -> [View]
  Rotation = 0
  ScaleType = 0
  TheoreticalExact = false
  Type = 1
  UnderTolerance = 0
  X = 98.3266
  Y = -40
FEATURE [TechDraw::DrawViewDimension] Dimension043
  Arbitrary = true
  FormatSpec = 120
  Inverted = false
  LockPosition = true
  MeasureType = 1
  OverTolerance = 0
  References2D = -> [View]
  Rotation = 0
  ScaleType = 0
  TheoreticalExact = false
  Type = 2
  UnderTolerance = 0
  X = 79.9557
  Y = -60.3095
FEATURE [TechDraw::DrawViewDimension] Dimension044
  Arbitrary = true
  FormatSpec = 500
  Inverted = false
  LockPosition = true
  MeasureType = 1
  OverTolerance = 0
  References2D = -> [View]
  Rotation = 0
  ScaleType = 0
  TheoreticalExact = false
  Type = 2
  UnderTolerance = 0
  X = 140.337
  Y = -55.6882
FEATURE [TechDraw::DrawViewDimension] Dimension045
  Arbitrary = false
  FormatSpec = %.2f
  Inverted = false
  LockPosition = true
  MeasureType = 1
  OverTolerance = 0
  References2D = -> [View]
  Rotation = 0
  ScaleType = 0
  TheoreticalExact = false
  Type = 2
  UnderTolerance = 0
  X = 140
  Y = -37.9159
FEATURE [TechDraw::DrawViewDimension] Dimension046
  Arbitrary = false
  FormatSpec = %.2f
  Inverted = false
  LockPosition = true
  MeasureType = 1
  OverTolerance = 0
  References2D = -> [View]
  Rotation = 0
  ScaleType = 0
  TheoreticalExact = false
  Type = 2
  UnderTolerance = 0
  X = 140
  Y = 6.42037
FEATURE [TechDraw::DrawViewDimension] Dimension047
  Arbitrary = false
  FormatSpec = %.2f
  Inverted = false
  LockPosition = true
  MeasureType = 1
  OverTolerance = 0
  References2D = -> [View]
  Rotation = 0
  ScaleType = 0
  TheoreticalExact = false
  Type = 2
  UnderTolerance = 0
  X = 140
  Y = 47.1681
FEATURE [TechDraw::DrawViewDimension] Dimension048
  Arbitrary = false
  FormatSpec = %.2f
  Inverted = false
  LockPosition = true
  MeasureType = 1
  OverTolerance = 0
  References2D = -> [View]
  Rotation = 0
  ScaleType = 0
  TheoreticalExact = false
  Type = 2
  UnderTolerance = 0
  X = 140
  Y = 67.8274
FEATURE [TechDraw::DrawViewDimension] Dimension049
  Arbitrary = false
  FormatSpec = %.2f
  Inverted = false
  LockPosition = true
  MeasureType = 1
  OverTolerance = 0
  References2D = -> [View]
  Rotation = 0
  ScaleType = 0
  TheoreticalExact = false
  Type = 2
  UnderTolerance = 0
  X = 79.1689
  Y = -38.3893
FEATURE [TechDraw::DrawViewDimension] Dimension050
  Arbitrary = false
  FormatSpec = %.2f
  Inverted = false
  LockPosition = true
  MeasureType = 1
  OverTolerance = 0
  References2D = -> [View]
  Rotation = 0
  ScaleType = 0
  TheoreticalExact = false
  Type = 2
  UnderTolerance = 0
  X = 23.9595
  Y = -13.5091
FEATURE [TechDraw::DrawViewDimension] Dimension051
  Arbitrary = false
  FormatSpec = %.2f
  Inverted = false
  LockPosition = true
  MeasureType = 1
  OverTolerance = 0
  References2D = -> [View]
  Rotation = 0
  ScaleType = 0
  TheoreticalExact = false
  Type = 2
  UnderTolerance = 0
  X = 45.3391
  Y = 14.8012
FEATURE [TechDraw::DrawViewDimension] Dimension052
  Arbitrary = true
  FormatSpec = 610
  Inverted = false
  LockPosition = true
  MeasureType = 1
  OverTolerance = 0
  References2D = -> [View]
  Rotation = 0
  ScaleType = 0
  TheoreticalExact = false
  Type = 1
  UnderTolerance = 0
  X = 35.6743
  Y = -15.7339
FEATURE [TechDraw::DrawViewDimension] Dimension053
  Arbitrary = true
  FormatSpec = 610
  Inverted = false
  LockPosition = true
  MeasureType = 1
  OverTolerance = 0
  References2D = -> [View]
  Rotation = 0
  ScaleType = 0
  TheoreticalExact = false
  Type = 2
  UnderTolerance = 0
  X = 58.5694
  Y = 19.4286
FEATURE [TechDraw::DrawViewDimension] Dimension054
  Arbitrary = true
  FormatSpec = 610
  Inverted = false
  LockPosition = true
  MeasureType = 1
  OverTolerance = 0
  References2D = -> [View]
  Rotation = 0
  ScaleType = 0
  TheoreticalExact = false
  Type = 2
  UnderTolerance = 0
  X = 59.8701
  Y = 34.9376
FEATURE [TechDraw::DrawViewDimension] Dimension055
  Arbitrary = false
  FormatSpec = %.2f
  Inverted = false
  LockPosition = true
  MeasureType = 1
  OverTolerance = 0
  References2D = -> [View]
  Rotation = 0
  ScaleType = 0
  TheoreticalExact = false
  Type = 1
  UnderTolerance = 0
  X = -97.1602
  Y = -0.346683
FEATURE [TechDraw::DrawViewDimension] Dimension057
  Arbitrary = false
  FormatSpec = %.2f
  Inverted = false
  LockPosition = true
  MeasureType = 1
  OverTolerance = 0
  References2D = -> [View]
  Rotation = 0
  ScaleType = 0
  TheoreticalExact = false
  Type = 1
  UnderTolerance = 0
  X = -53.1
  Y = 1
FEATURE [TechDraw::DrawViewDimension] Dimension058
  Arbitrary = false
  FormatSpec = %.2f
  Inverted = false
  LockPosition = true
  MeasureType = 1
  OverTolerance = 0
  References2D = -> [View]
  Rotation = 0
  ScaleType = 0
  TheoreticalExact = false
  Type = 1
  UnderTolerance = 0
  X = -18.2
  Y = 1
FEATURE [TechDraw::DrawViewDimension] Dimension059
  Arbitrary = true
  FormatSpec = 1180
  Inverted = false
  LockPosition = true
  MeasureType = 1
  OverTolerance = 0
  References2D = -> [View]
  Rotation = 0
  ScaleType = 0
  TheoreticalExact = false
  Type = 1
  UnderTolerance = 0
  X = 20.0802
  Y = 5.37672
FEATURE [TechDraw::DrawViewDimension] Dimension060
  Arbitrary = true
  FormatSpec = 1150
  Inverted = false
  LockPosition = true
  MeasureType = 1
  OverTolerance = 0
  References2D = -> [View]
  Rotation = 0
  ScaleType = 0
  TheoreticalExact = false
  Type = 1
  UnderTolerance = 0
  X = 55.62
  Y = 1
FEATURE [TechDraw::DrawViewDimension] Dimension061
  Arbitrary = false
  FormatSpec = %.2f
  Inverted = false
  LockPosition = true
  MeasureType = 1
  OverTolerance = 0
  References2D = -> [View]
  Rotation = 0
  ScaleType = 0
  TheoreticalExact = false
  Type = 1
  UnderTolerance = 0
  X = 91.8
  Y = 1
FEATURE [TechDraw::DrawViewDimension] Dimension062
  Arbitrary = false
  FormatSpec = %.2f
  Inverted = false
  LockPosition = true
  MeasureType = 1
  OverTolerance = 0
  References2D = -> [View]
  Rotation = 0
  ScaleType = 0
  TheoreticalExact = false
  Type = 2
  UnderTolerance = 0
  X = 122.46
  Y = 1.76333
FEATURE [TechDraw::DrawViewDimension] Dimension063
  Arbitrary = true
  FormatSpec = 1750
  Inverted = false
  LockPosition = true
  MeasureType = 1
  OverTolerance = 0
  References2D = -> [View]
  Rotation = 0
  ScaleType = 0
  TheoreticalExact = false
  Type = 2
  UnderTolerance = 0
  X = 116.017
  Y = -5.00001
FEATURE [TechDraw::DrawViewDimension] Dimension064
  Arbitrary = false
  FormatSpec = %.2f
  Inverted = false
  LockPosition = true
  MeasureType = 1
  OverTolerance = 0
  References2D = -> [View]
  Rotation = 0
  ScaleType = 0
  TheoreticalExact = false
  Type = 1
  UnderTolerance = 0
  X = -34.8
  Y = 58
FEATURE [TechDraw::DrawViewDimension] Dimension065
  Arbitrary = false
  FormatSpec = %.2f
  Inverted = false
  LockPosition = true
  MeasureType = 1
  OverTolerance = 0
  References2D = -> [View]
  Rotation = 0
  ScaleType = 0
  TheoreticalExact = false
  Type = 1
  UnderTolerance = 0
  X = 64.5
  Y = 58
FEATURE [TechDraw::DrawViewDimension] Dimension066
  Arbitrary = false
  FormatSpec = %.2f
  Inverted = false
  LockPosition = true
  MeasureType = 1
  OverTolerance = 0
  References2D = -> [View001]
  Rotation = 0
  ScaleType = 0
  TheoreticalExact = false
  Type = 1
  UnderTolerance = 0
  X = -114.3
  Y = 58
FEATURE [TechDraw::DrawViewDimension] Dimension067
  Arbitrary = false
  FormatSpec = %.2f
  Inverted = false
  LockPosition = true
  MeasureType = 1
  OverTolerance = 0
  References2D = -> [View001]
  Rotation = 0
  ScaleType = 0
  TheoreticalExact = false
  Type = 1
  UnderTolerance = 0
  X = -8.7
  Y = 58
FEATURE [TechDraw::DrawViewDimension] Dimension069
  Arbitrary = false
  FormatSpec = %.2f
  Inverted = false
  LockPosition = true
  MeasureType = 1
  OverTolerance = 0
  References2D = -> [View001]
  Rotation = 0
  ScaleType = 0
  TheoreticalExact = false
  Type = 1
  UnderTolerance = 0
  X = 105.6
  Y = 58
FEATURE [TechDraw::DrawViewDimension] Dimension070
  Arbitrary = false
  FormatSpec = %.2f
  Inverted = false
  LockPosition = false
  MeasureType = 1
  OverTolerance = 0
  References2D = -> [View002]
  Rotation = 0
  ScaleType = 0
  TheoreticalExact = false
  Type = 2
  UnderTolerance = 0
  X = -72.3794
  Y = 10.149
FEATURE [TechDraw::DrawViewDimension] Dimension071
  Arbitrary = false
  FormatSpec = %.2f
  Inverted = false
  LockPosition = true
  MeasureType = 1
  OverTolerance = 0
  References2D = -> [View001]
  Rotation = 0
  ScaleType = 0
  TheoreticalExact = false
  Type = 1
  UnderTolerance = 0
  X = -152.293
  Y = 7
FEATURE [TechDraw::DrawViewDimension] Dimension072
  Arbitrary = false
  FormatSpec = %.2f
  Inverted = false
  LockPosition = true
  MeasureType = 1
  OverTolerance = 0
  References2D = -> [View001]
  Rotation = 0
  ScaleType = 0
  TheoreticalExact = false
  Type = 1
  UnderTolerance = 0
  X = -139.893
  Y = 7
FEATURE [TechDraw::DrawViewDimension] Dimension073
  Arbitrary = false
  FormatSpec = %.2f
  Inverted = false
  LockPosition = true
  MeasureType = 1
  OverTolerance = 0
  References2D = -> [View001]
  Rotation = 0
  ScaleType = 0
  TheoreticalExact = false
  Type = 1
  UnderTolerance = 0
  X = -111
  Y = 7
FEATURE [TechDraw::DrawViewDimension] Dimension074
  Arbitrary = false
  FormatSpec = %.2f
  Inverted = false
  LockPosition = true
  MeasureType = 1
  OverTolerance = 0
  References2D = -> [View001]
  Rotation = 0
  ScaleType = 0
  TheoreticalExact = false
  Type = 1
  UnderTolerance = 0
  X = -57.3402
  Y = 7.23666
FEATURE [TechDraw::DrawViewDimension] Dimension075
  Arbitrary = false
  FormatSpec = %.2f
  Inverted = false
  LockPosition = true
  MeasureType = 1
  OverTolerance = 0
  References2D = -> [View001]
  Rotation = 0
  ScaleType = 0
  TheoreticalExact = false
  Type = 1
  UnderTolerance = 0
  X = -29.9
  Y = 7
FEATURE [TechDraw::DrawViewDimension] Dimension076
  Arbitrary = false
  FormatSpec = %.2f
  Inverted = false
  LockPosition = true
  MeasureType = 1
  OverTolerance = 0
  References2D = -> [View001]
  Rotation = 0
  ScaleType = 0
  TheoreticalExact = false
  Type = 1
  UnderTolerance = 0
  X = -19.1256
  Y = -1.50992
FEATURE [TechDraw::DrawViewDimension] Dimension077
  Arbitrary = false
  FormatSpec = %.2f
  Inverted = false
  LockPosition = true
  MeasureType = 1
  OverTolerance = 0
  References2D = -> [View001]
  Rotation = 0
  ScaleType = 0
  TheoreticalExact = false
  Type = 1
  UnderTolerance = 0
  X = 25.9099
  Y = -1.50992
FEATURE [TechDraw::DrawViewDimension] Dimension078
  Arbitrary = false
  FormatSpec = %.2f
  Inverted = false
  LockPosition = true
  MeasureType = 1
  OverTolerance = 0
  References2D = -> [View001]
  Rotation = 0
  ScaleType = 0
  TheoreticalExact = false
  Type = 1
  UnderTolerance = 0
  X = 75.4
  Y = 7
FEATURE [TechDraw::DrawViewDimension] Dimension079
  Arbitrary = false
  FormatSpec = %.2f
  Inverted = false
  LockPosition = true
  MeasureType = 1
  OverTolerance = 0
  References2D = -> [View001]
  Rotation = 0
  ScaleType = 0
  TheoreticalExact = false
  Type = 1
  UnderTolerance = 0
  X = 140.3
  Y = 7
FEATURE [TechDraw::DrawViewDimension] Dimension080
  Arbitrary = false
  FormatSpec = %.2f
  Inverted = false
  LockPosition = true
  MeasureType = 1
  OverTolerance = 0
  References2D = -> [View001]
  Rotation = 0
  ScaleType = 0
  TheoreticalExact = false
  Type = 2
  UnderTolerance = 0
  X = -44.1188
  Y = 13.3843
FEATURE [TechDraw::DrawViewDimension] Dimension081
  Arbitrary = false
  FormatSpec = %.2f
  Inverted = false
  LockPosition = true
  MeasureType = 1
  OverTolerance = 0
  References2D = -> [View001]
  Rotation = 0
  ScaleType = 0
  TheoreticalExact = false
  Type = 2
  UnderTolerance = 0
  X = -44.1188
  Y = -5.75812
FEATURE [TechDraw::DrawViewDimension] Dimension082
  Arbitrary = false
  FormatSpec = %.2f
  Inverted = false
  LockPosition = true
  MeasureType = 1
  OverTolerance = 0
  References2D = -> [View001]
  Rotation = 0
  ScaleType = 0
  TheoreticalExact = false
  Type = 2
  UnderTolerance = 0
  X = -126.857
  Y = -7.22039
FEATURE [TechDraw::DrawViewDimension] Dimension083
  Arbitrary = false
  FormatSpec = %.2f
  Inverted = false
  LockPosition = true
  MeasureType = 1
  OverTolerance = 0
  References2D = -> [View003]
  Rotation = 0
  ScaleType = 0
  TheoreticalExact = false
  Type = 1
  UnderTolerance = 0
  X = -104.1
  Y = 69
FEATURE [TechDraw::DrawViewDimension] Dimension084
  Arbitrary = false
  FormatSpec = %.2f
  Inverted = false
  LockPosition = true
  MeasureType = 1
  OverTolerance = 0
  References2D = -> [View003]
  Rotation = 0
  ScaleType = 0
  TheoreticalExact = false
  Type = 1
  UnderTolerance = 0
  X = 8.7
  Y = 69
FEATURE [TechDraw::DrawViewDimension] Dimension085
  Arbitrary = false
  FormatSpec = %.2f
  Inverted = false
  LockPosition = true
  MeasureType = 1
  OverTolerance = 0
  References2D = -> [View003]
  Rotation = 0
  ScaleType = 0
  TheoreticalExact = false
  Type = 1
  UnderTolerance = 0
  X = 112.8
  Y = 69
FEATURE [TechDraw::DrawViewDimension] Dimension086
  Arbitrary = false
  FormatSpec = %.2f
  Inverted = false
  LockPosition = true
  MeasureType = 1
  OverTolerance = 0
  References2D = -> [View003]
  Rotation = 0
  ScaleType = 0
  TheoreticalExact = false
  Type = 2
  UnderTolerance = 0
  X = -169.007
  Y = -18.8508
FEATURE [TechDraw::DrawViewDimension] Dimension087
  Arbitrary = false
  FormatSpec = %.2f
  Inverted = false
  LockPosition = true
  MeasureType = 1
  OverTolerance = 0
  References2D = -> [View003]
  Rotation = 0
  ScaleType = 0
  TheoreticalExact = false
  Type = 2
  UnderTolerance = 0
  X = -169.05
  Y = 5.08691
FEATURE [TechDraw::DrawViewDimension] Dimension088
  Arbitrary = false
  FormatSpec = %.2f
  Inverted = false
  LockPosition = true
  MeasureType = 1
  OverTolerance = 0
  References2D = -> [View003]
  Rotation = 0
  ScaleType = 0
  TheoreticalExact = false
  Type = 2
  UnderTolerance = 0
  X = -169.05
  Y = 36.8262
FEATURE [TechDraw::DrawViewDimension] Dimension089
  Arbitrary = false
  FormatSpec = %.2f
  Inverted = false
  LockPosition = true
  MeasureType = 1
  OverTolerance = 0
  References2D = -> [View003]
  Rotation = 0
  ScaleType = 0
  TheoreticalExact = false
  Type = 1
  UnderTolerance = 0
  X = -153.3
  Y = -5.05762
FEATURE [TechDraw::DrawViewDimension] Dimension090
  Arbitrary = false
  FormatSpec = %.2f
  Inverted = false
  LockPosition = true
  MeasureType = 1
  OverTolerance = 0
  References2D = -> [View003]
  Rotation = 0
  ScaleType = 0
  TheoreticalExact = false
  Type = 1
  UnderTolerance = 0
  X = -111.813
  Y = 12.1922
FEATURE [TechDraw::DrawViewDimension] Dimension091
  Arbitrary = false
  FormatSpec = %.2f
  Inverted = false
  LockPosition = true
  MeasureType = 1
  OverTolerance = 0
  References2D = -> [View003]
  Rotation = 0
  ScaleType = 0
  TheoreticalExact = false
  Type = 1
  UnderTolerance = 0
  X = -59.5738
  Y = 12.8676
FEATURE [TechDraw::DrawViewDimension] Dimension092
  Arbitrary = false
  FormatSpec = %.2f
  Inverted = false
  LockPosition = true
  MeasureType = 1
  OverTolerance = 0
  References2D = -> [View003]
  Rotation = 0
  ScaleType = 0
  TheoreticalExact = false
  Type = 2
  UnderTolerance = 0
  X = -128.048
  Y = -1.61465
FEATURE [TechDraw::DrawViewDimension] Dimension093
  Arbitrary = false
  FormatSpec = %.2f
  Inverted = false
  LockPosition = true
  MeasureType = 1
  OverTolerance = 0
  References2D = -> [View003]
  Rotation = 0
  ScaleType = 0
  TheoreticalExact = false
  Type = 1
  UnderTolerance = 0
  X = -32.543
  Y = -40.7486
FEATURE [TechDraw::DrawViewDimension] Dimension094
  Arbitrary = false
  FormatSpec = %.2f
  Inverted = false
  LockPosition = true
  MeasureType = 1
  OverTolerance = 0
  References2D = -> [View003]
  Rotation = 0
  ScaleType = 0
  TheoreticalExact = false
  Type = 1
  UnderTolerance = 0
  X = -25.3623
  Y = -33.877
FEATURE [TechDraw::DrawViewDimension] Dimension095
  Arbitrary = false
  FormatSpec = %.2f
  Inverted = false
  LockPosition = true
  MeasureType = 1
  OverTolerance = 0
  References2D = -> [View003]
  Rotation = 0
  ScaleType = 0
  TheoreticalExact = false
  Type = 1
  UnderTolerance = 0
  X = 9.71309
  Y = -42.9947
FEATURE [TechDraw::DrawViewDimension] Dimension096
  Arbitrary = false
  FormatSpec = %.2f
  Inverted = false
  LockPosition = true
  MeasureType = 1
  OverTolerance = 0
  References2D = -> [View003]
  Rotation = 0
  ScaleType = 0
  TheoreticalExact = false
  Type = 2
  UnderTolerance = 0
  X = -112.851
  Y = 39.3146
FEATURE [TechDraw::DrawViewDimension] Dimension097
  Arbitrary = false
  FormatSpec = %.2f
  Inverted = false
  LockPosition = true
  MeasureType = 1
  OverTolerance = 0
  References2D = -> [View003]
  Rotation = 0
  ScaleType = 0
  TheoreticalExact = false
  Type = 1
  UnderTolerance = 0
  X = 137.525
  Y = -6.38106
FEATURE [TechDraw::DrawViewDimension] Dimension098
  Arbitrary = false
  FormatSpec = %.2f
  Inverted = false
  LockPosition = true
  MeasureType = 1
  OverTolerance = 0
  References2D = -> [View003]
  Rotation = 0
  ScaleType = 0
  TheoreticalExact = false
  Type = 1
  UnderTolerance = 0
  X = 106.2
  Y = -6.63086
FEATURE [TechDraw::DrawViewDimension] Dimension099
  Arbitrary = false
  FormatSpec = %.2f
  Inverted = false
  LockPosition = true
  MeasureType = 1
  OverTolerance = 0
  References2D = -> [View003]
  Rotation = 0
  ScaleType = 0
  TheoreticalExact = false
  Type = 2
  UnderTolerance = 0
  X = 88.8713
  Y = -9.3377
FEATURE [TechDraw::DrawViewDimension] Dimension100
  Arbitrary = false
  FormatSpec = %.2f
  Inverted = false
  LockPosition = true
  MeasureType = 1
  OverTolerance = 0
  References2D = -> [View003]
  Rotation = 0
  ScaleType = 0
  TheoreticalExact = false
  Type = 2
  UnderTolerance = 0
  X = 80.8801
  Y = 1.42461
FEATURE [TechDraw::DrawPage] Page  label="Plan Elevation"
  KeepUpdated = true
  NextBalloonIndex = 1
  ProjectionType = 0
  Template = -> Template
  Views = -> [View,View001,View002,View003,View004,Dimension,Dimension001,Dimension002,Dimension003,Dimension004,Dimension005,Dimension006,Dimension007,Dimension008,Dimension009,Dimension010,Dimension011,Dimension012,Dimension014,Dimension015,Dimension016,Dimension017,Dimension018,Dimension019,Dimension020,Dimension021,Dimension022,Dimension023,Dimension024,Dimension025,Dimension026,Dimension027,Dimension028,+79 more]
FEATURE [Sketcher::SketchObject] Sketch072
  MapMode = 5
  Placement = pos=(-900,0,0) rot=(0.57735,-0.57735,-0.57735;2.0944rad)
  Support = -> [Structure122]
  sketch-geometry (1):
    g0: LineSegment StartX=-856 StartY=-1744 StartZ=0 EndX=1156 EndY=-1744 EndZ=0
FEATURE [Part::FeaturePython] Rebar  label="Set_1"  # Arch/BIM 110 (typed FeaturePython)
  Amount = 11
  AmountCheck = true
  Base = -> Sketch072
  Cover = 50
  CoverAlong = Bottom Side
  Diameter = 12
  Direction = (0,0,0)
  Distance = 0
  FrontCover = 44
  HorizontalArea = 0
  Host = -> Structure122
  IfcType = 110
  LeftBottomCover = 44
  Length = 2012
  MoveBase = false
  MoveWithHost = false
  OffsetEnd = 50
  OffsetStart = 50
  Orientation = Horizontal
  PerimeterLength = 0
  Placement = pos=(0,300,0) rot=(0,0,1;0rad)
  PlacementList = 11 placements: arithmetic series from (50,0,0) step (200,0,0) to (2050,0,0)
  RightTopCover = 44
  Rounding = 0
  Spacing = 200
  TotalLength = 22132
  TrueSpacing = 11
  VerticalArea = 0
FEATURE [Sketcher::SketchObject] Sketch073
  MapMode = 5
  Placement = pos=(0,-900,0) rot=(1,0,0;1.5708rad)
  Support = -> [Structure122]
  sketch-geometry (1):
    g0: LineSegment StartX=-856 StartY=-1732 StartZ=0 EndX=1156 EndY=-1732 EndZ=0
FEATURE [Part::FeaturePython] Rebar001  label="Set_2"  # Arch/BIM 110 (typed FeaturePython)
  Amount = 11
  AmountCheck = true
  Base = -> Sketch073
  Cover = 62
  CoverAlong = Bottom Side
  Diameter = 12
  Direction = (0,0,0)
  Distance = 0
  FrontCover = 44
  HorizontalArea = 0
  Host = -> Structure122
  IfcType = 110
  LeftBottomCover = 44
  Length = 2012
  MoveBase = false
  MoveWithHost = false
  OffsetEnd = 50
  OffsetStart = 50
  Orientation = Horizontal
  PerimeterLength = 0
  PlacementList = 11 placements: arithmetic series from (0,50,-1.11022e-14) step (0,200,-4.44089e-14) to (0,2050,-4.55191e-13)
  RightTopCover = 44
  Rounding = 0
  Spacing = 200
  TotalLength = 22132
  TrueSpacing = 11
  VerticalArea = 0
FEATURE [Sketcher::SketchObject] Sketch074
  MapMode = 5
  Placement = pos=(5240,-900,0) rot=(1,0,0;1.5708rad)
  Support = -> [Structure125]
  sketch-geometry (1):
    g0: LineSegment StartX=-856 StartY=-1732 StartZ=0 EndX=1156 EndY=-1732 EndZ=0
FEATURE [Part::FeaturePython] Rebar002  label="StraightRebar"  # Arch/BIM 110 (typed FeaturePython)
  Amount = 11
  AmountCheck = true
  Base = -> Sketch074
  Cover = 62
  CoverAlong = Bottom Side
  Diameter = 12
  Direction = (0,0,0)
  Distance = 0
  FrontCover = 44
  HorizontalArea = 0
  Host = -> Structure125
  IfcType = 110
  LeftBottomCover = 44
  Length = 2012
  MoveBase = false
  MoveWithHost = false
  OffsetEnd = 50
  OffsetStart = 50
  Orientation = Horizontal
  PerimeterLength = 0
  PlacementList = 11 placements: arithmetic series from (0,50,-1.11022e-14) step (0,200,-4.44089e-14) to (0,2050,-4.55191e-13)
  RightTopCover = 44
  Rounding = 0
  Spacing = 200
  TotalLength = 22132
  TrueSpacing = 11
  VerticalArea = 0
FEATURE [Sketcher::SketchObject] Sketch075
  MapMode = 5
  Placement = pos=(4340,0,0) rot=(0.57735,-0.57735,-0.57735;2.0944rad)
  Support = -> [Structure125]
  sketch-geometry (1):
    g0: LineSegment StartX=-856 StartY=-1744 StartZ=0 EndX=1156 EndY=-1744 EndZ=0
FEATURE [Part::FeaturePython] Rebar003  label="StraightRebar001"  # Arch/BIM 110 (typed FeaturePython)
  Amount = 11
  AmountCheck = true
  Base = -> Sketch075
  Cover = 50
  CoverAlong = Bottom Side
  Diameter = 12
  Direction = (0,0,0)
  Distance = 0
  FrontCover = 44
  HorizontalArea = 0
  Host = -> Structure125
  IfcType = 110
  LeftBottomCover = 44
  Length = 2012
  MoveBase = false
  MoveWithHost = false
  OffsetEnd = 50
  OffsetStart = 50
  Orientation = Horizontal
  PerimeterLength = 0
  Placement = pos=(0,300,0) rot=(0,0,1;0rad)
  PlacementList = 11 placements: arithmetic series from (50,0,0) step (200,0,0) to (2050,0,0)
  RightTopCover = 44
  Rounding = 0
  Spacing = 200
  TotalLength = 22132
  TrueSpacing = 11
  VerticalArea = 0
FEATURE [Sketcher::SketchObject] Sketch076
  MapMode = 5
  Placement = pos=(10380,0,0) rot=(0.57735,-0.57735,-0.57735;2.0944rad)
  Support = -> [Structure127]
  sketch-geometry (1):
    g0: LineSegment StartX=-856 StartY=-1744 StartZ=0 EndX=1156 EndY=-1744 EndZ=0
FEATURE [Part::FeaturePython] Rebar004  label="StraightRebar002"  # Arch/BIM 110 (typed FeaturePython)
  Amount = 11
  AmountCheck = true
  Base = -> Sketch076
  Cover = 50
  CoverAlong = Bottom Side
  Diameter = 12
  Direction = (0,0,0)
  Distance = 0
  FrontCover = 44
  HorizontalArea = 0
  Host = -> Structure127
  IfcType = 110
  LeftBottomCover = 44
  Length = 2012
  MoveBase = false
  MoveWithHost = false
  OffsetEnd = 50
  OffsetStart = 50
  Orientation = Horizontal
  PerimeterLength = 0
  Placement = pos=(0,300,0) rot=(0,0,1;0rad)
  PlacementList = 11 placements: arithmetic series from (50,0,0) step (200,0,0) to (2050,0,0)
  RightTopCover = 44
  Rounding = 0
  Spacing = 200
  TotalLength = 22132
  TrueSpacing = 11
  VerticalArea = 0
FEATURE [Sketcher::SketchObject] Sketch077
  MapMode = 5
  Placement = pos=(11280,-900,0) rot=(1,0,0;1.5708rad)
  Support = -> [Structure127]
  sketch-geometry (1):
    g0: LineSegment StartX=-856 StartY=-1732 StartZ=0 EndX=1156 EndY=-1732 EndZ=0
FEATURE [Part::FeaturePython] Rebar005  label="StraightRebar003"  # Arch/BIM 110 (typed FeaturePython)
  Amount = 11
  AmountCheck = true
  Base = -> Sketch077
  Cover = 62
  CoverAlong = Bottom Side
  Diameter = 12
  Direction = (0,0,0)
  Distance = 0
  FrontCover = 44
  HorizontalArea = 0
  Host = -> Structure127
  IfcType = 110
  LeftBottomCover = 44
  Length = 2012
  MoveBase = false
  MoveWithHost = false
  OffsetEnd = 50
  OffsetStart = 50
  Orientation = Horizontal
  PerimeterLength = 0
  PlacementList = 11 placements: arithmetic series from (0,50,-1.11022e-14) step (0,200,-4.44089e-14) to (0,2050,-4.55191e-13)
  RightTopCover = 44
  Rounding = 0
  Spacing = 200
  TotalLength = 22132
  TrueSpacing = 11
  VerticalArea = 0
FEATURE [Sketcher::SketchObject] Sketch078
  MapMode = 5
  Placement = pos=(14750,-1.08e-12,0) rot=(0.57735,-0.57735,-0.57735;2.0944rad)
  Support = -> [Structure129]
  sketch-geometry (1):
    g0: LineSegment StartX=-856 StartY=-1744 StartZ=0 EndX=1156 EndY=-1744 EndZ=0
FEATURE [Part::FeaturePython] Rebar006  label="StraightRebar004"  # Arch/BIM 110 (typed FeaturePython)
  Amount = 11
  AmountCheck = true
  Base = -> Sketch078
  Cover = 50
  CoverAlong = Bottom Side
  Diameter = 12
  Direction = (0,0,0)
  Distance = 0
  FrontCover = 44
  HorizontalArea = 0
  Host = -> Structure129
  IfcType = 110
  LeftBottomCover = 44
  Length = 2012
  MoveBase = false
  MoveWithHost = false
  OffsetEnd = 50
  OffsetStart = 50
  Orientation = Horizontal
  PerimeterLength = 0
  Placement = pos=(0,300,0) rot=(0,0,1;0rad)
  PlacementList = 11 placements: arithmetic series from (50,0,0) step (200,0,0) to (2050,0,0)
  RightTopCover = 44
  Rounding = 0
  Spacing = 200
  TotalLength = 22132
  TrueSpacing = 11
  VerticalArea = 0
FEATURE [Sketcher::SketchObject] Sketch079
  MapMode = 5
  Placement = pos=(15650,-900,0) rot=(1,0,0;1.5708rad)
  Support = -> [Structure129]
  sketch-geometry (1):
    g0: LineSegment StartX=-856 StartY=-1732 StartZ=0 EndX=1156 EndY=-1732 EndZ=0
FEATURE [Part::FeaturePython] Rebar007  label="StraightRebar005"  # Arch/BIM 110 (typed FeaturePython)
  Amount = 11
  AmountCheck = true
  Base = -> Sketch079
  Cover = 62
  CoverAlong = Bottom Side
  Diameter = 12
  Direction = (0,0,0)
  Distance = 0
  FrontCover = 44
  HorizontalArea = 0
  Host = -> Structure129
  IfcType = 110
  LeftBottomCover = 44
  Length = 2012
  MoveBase = false
  MoveWithHost = false
  OffsetEnd = 50
  OffsetStart = 50
  Orientation = Horizontal
  PerimeterLength = 0
  PlacementList = 11 placements: arithmetic series from (0,50,-1.11022e-14) step (0,200,-4.44089e-14) to (0,2050,-4.55191e-13)
  RightTopCover = 44
  Rounding = 0
  Spacing = 200
  TotalLength = 22132
  TrueSpacing = 11
  VerticalArea = 0
FEATURE [Sketcher::SketchObject] Sketch080
  MapMode = 5
  Placement = pos=(-900,5000,1.1369e-12) rot=(0.57735,-0.57735,-0.57735;2.0944rad)
  Support = -> [Structure123]
  sketch-geometry (1):
    g0: LineSegment StartX=-856 StartY=-1744 StartZ=0 EndX=1156 EndY=-1744 EndZ=0
FEATURE [Part::FeaturePython] Rebar008  label="StraightRebar006"  # Arch/BIM 110 (typed FeaturePython)
  Amount = 11
  AmountCheck = true
  Base = -> Sketch080
  Cover = 50
  CoverAlong = Bottom Side
  Diameter = 12
  Direction = (0,0,0)
  Distance = 0
  FrontCover = 44
  HorizontalArea = 0
  Host = -> Structure123
  IfcType = 110
  LeftBottomCover = 44
  Length = 2012
  MoveBase = false
  MoveWithHost = false
  OffsetEnd = 50
  OffsetStart = 50
  Orientation = Horizontal
  PerimeterLength = 0
  Placement = pos=(0,300,0) rot=(0,0,1;0rad)
  PlacementList = 11 placements: arithmetic series from (50,0,0) step (200,0,0) to (2050,0,0)
  RightTopCover = 44
  Rounding = 0
  Spacing = 200
  TotalLength = 22132
  TrueSpacing = 11
  VerticalArea = 0
FEATURE [Sketcher::SketchObject] Sketch081
  MapMode = 5
  Placement = pos=(0,4100,1.1369e-12) rot=(1,0,0;1.5708rad)
  Support = -> [Structure123]
  sketch-geometry (1):
    g0: LineSegment StartX=-856 StartY=-1732 StartZ=0 EndX=1156 EndY=-1732 EndZ=0
FEATURE [Part::FeaturePython] Rebar009  label="StraightRebar007"  # Arch/BIM 110 (typed FeaturePython)
  Amount = 11
  AmountCheck = true
  Base = -> Sketch081
  Cover = 62
  CoverAlong = Bottom Side
  Diameter = 12
  Direction = (0,0,0)
  Distance = 0
  FrontCover = 44
  HorizontalArea = 0
  Host = -> Structure123
  IfcType = 110
  LeftBottomCover = 44
  Length = 2012
  MoveBase = false
  MoveWithHost = false
  OffsetEnd = 50
  OffsetStart = 50
  Orientation = Horizontal
  PerimeterLength = 0
  PlacementList = 11 placements: arithmetic series from (0,50,-1.11022e-14) step (0,200,-4.44089e-14) to (0,2050,-4.55191e-13)
  RightTopCover = 44
  Rounding = 0
  Spacing = 200
  TotalLength = 22132
  TrueSpacing = 11
  VerticalArea = 0
FEATURE [Sketcher::SketchObject] Sketch082
  MapMode = 5
  Placement = pos=(14750,5000,1.1369e-12) rot=(0.57735,-0.57735,-0.57735;2.0944rad)
  Support = -> [Structure130]
  sketch-geometry (1):
    g0: LineSegment StartX=-856 StartY=-1744 StartZ=0 EndX=1156 EndY=-1744 EndZ=0
FEATURE [Part::FeaturePython] Rebar010  label="StraightRebar008"  # Arch/BIM 110 (typed FeaturePython)
  Amount = 11
  AmountCheck = true
  Base = -> Sketch082
  Cover = 50
  CoverAlong = Bottom Side
  Diameter = 12
  Direction = (0,0,0)
  Distance = 0
  FrontCover = 44
  HorizontalArea = 0
  Host = -> Structure130
  IfcType = 110
  LeftBottomCover = 44
  Length = 2012
  MoveBase = false
  MoveWithHost = false
  OffsetEnd = 50
  OffsetStart = 50
  Orientation = Horizontal
  PerimeterLength = 0
  Placement = pos=(0,300,1) rot=(0,0,1;0rad)
  PlacementList = 11 placements: arithmetic series from (50,0,0) step (200,0,0) to (2050,0,0)
  RightTopCover = 44
  Rounding = 0
  Spacing = 200
  TotalLength = 22132
  TrueSpacing = 11
  VerticalArea = 0
FEATURE [Sketcher::SketchObject] Sketch083
  MapMode = 5
  Placement = pos=(15650,4100,1.1369e-12) rot=(1,0,0;1.5708rad)
  Support = -> [Structure130]
  sketch-geometry (1):
    g0: LineSegment StartX=-856 StartY=-1732 StartZ=0 EndX=1156 EndY=-1732 EndZ=0
FEATURE [Part::FeaturePython] Rebar011  label="StraightRebar009"  # Arch/BIM 110 (typed FeaturePython)
  Amount = 11
  AmountCheck = true
  Base = -> Sketch083
  Cover = 62
  CoverAlong = Bottom Side
  Diameter = 12
  Direction = (0,0,0)
  Distance = 0
  FrontCover = 44
  HorizontalArea = 0
  Host = -> Structure130
  IfcType = 110
  LeftBottomCover = 44
  Length = 2012
  MoveBase = false
  MoveWithHost = false
  OffsetEnd = 50
  OffsetStart = 50
  Orientation = Horizontal
  PerimeterLength = 0
  PlacementList = 11 placements: arithmetic series from (0,50,-1.11022e-14) step (0,200,-4.44089e-14) to (0,2050,-4.55191e-13)
  RightTopCover = 44
  Rounding = 0
  Spacing = 200
  TotalLength = 22132
  TrueSpacing = 11
  VerticalArea = 0
FEATURE [Sketcher::SketchObject] Sketch084
  MapMode = 5
  Placement = pos=(-900,9630,2.046e-12) rot=(0.57735,-0.57735,-0.57735;2.0944rad)
  Support = -> [Structure124]
  sketch-geometry (1):
    g0: LineSegment StartX=-856 StartY=-1744 StartZ=0 EndX=1156 EndY=-1744 EndZ=0
FEATURE [Part::FeaturePython] Rebar012  label="StraightRebar010"  # Arch/BIM 110 (typed FeaturePython)
  Amount = 11
  AmountCheck = true
  Base = -> Sketch084
  Cover = 50
  CoverAlong = Bottom Side
  Diameter = 12
  Direction = (0,0,0)
  Distance = 0
  FrontCover = 44
  HorizontalArea = 0
  Host = -> Structure124
  IfcType = 110
  LeftBottomCover = 44
  Length = 2012
  MoveBase = false
  MoveWithHost = false
  OffsetEnd = 50
  OffsetStart = 50
  Orientation = Horizontal
  PerimeterLength = 0
  Placement = pos=(0,300,0) rot=(0,0,1;0rad)
  PlacementList = 11 placements: arithmetic series from (50,0,0) step (200,0,0) to (2050,0,0)
  RightTopCover = 44
  Rounding = 0
  Spacing = 200
  TotalLength = 22132
  TrueSpacing = 11
  VerticalArea = 0
FEATURE [Sketcher::SketchObject] Sketch085
  MapMode = 5
  Placement = pos=(0,8730,2.046e-12) rot=(1,0,0;1.5708rad)
  Support = -> [Structure124]
  sketch-geometry (1):
    g0: LineSegment StartX=-856 StartY=-1732 StartZ=0 EndX=1156 EndY=-1732 EndZ=0
FEATURE [Part::FeaturePython] Rebar013  label="StraightRebar011"  # Arch/BIM 110 (typed FeaturePython)
  Amount = 11
  AmountCheck = true
  Base = -> Sketch085
  Cover = 62
  CoverAlong = Bottom Side
  Diameter = 12
  Direction = (0,0,0)
  Distance = 0
  FrontCover = 44
  HorizontalArea = 0
  Host = -> Structure124
  IfcType = 110
  LeftBottomCover = 44
  Length = 2012
  MoveBase = false
  MoveWithHost = false
  OffsetEnd = 50
  OffsetStart = 50
  Orientation = Horizontal
  PerimeterLength = 0
  PlacementList = 11 placements: arithmetic series from (0,50,-1.11022e-14) step (0,200,-4.44089e-14) to (0,2050,-4.55191e-13)
  RightTopCover = 44
  Rounding = 0
  Spacing = 200
  TotalLength = 22132
  TrueSpacing = 11
  VerticalArea = 0
FEATURE [Sketcher::SketchObject] Sketch088
  MapMode = 5
  Placement = pos=(4340,9630,2.046e-12) rot=(0.57735,-0.57735,-0.57735;2.0944rad)
  Support = -> [Structure126]
  sketch-geometry (1):
    g0: LineSegment StartX=-856 StartY=-1744 StartZ=0 EndX=1156 EndY=-1744 EndZ=0
FEATURE [Part::FeaturePython] Rebar014  label="StraightRebar012"  # Arch/BIM 110 (typed FeaturePython)
  Amount = 11
  AmountCheck = true
  Base = -> Sketch088
  Cover = 50
  CoverAlong = Bottom Side
  Diameter = 12
  Direction = (0,0,0)
  Distance = 0
  FrontCover = 44
  HorizontalArea = 0
  Host = -> Structure126
  IfcType = 110
  LeftBottomCover = 44
  Length = 2012
  MoveBase = false
  MoveWithHost = false
  OffsetEnd = 50
  OffsetStart = 50
  Orientation = Horizontal
  PerimeterLength = 0
  Placement = pos=(0,300,0) rot=(0,0,1;0rad)
  PlacementList = 11 placements: arithmetic series from (50,0,0) step (200,0,0) to (2050,0,0)
  RightTopCover = 44
  Rounding = 0
  Spacing = 200
  TotalLength = 22132
  TrueSpacing = 11
  VerticalArea = 0
FEATURE [Sketcher::SketchObject] Sketch089
  MapMode = 5
  Placement = pos=(5240,8730,2.046e-12) rot=(1,0,0;1.5708rad)
  Support = -> [Structure126]
  sketch-geometry (1):
    g0: LineSegment StartX=-856 StartY=-1732 StartZ=0 EndX=1156 EndY=-1732 EndZ=0
FEATURE [Part::FeaturePython] Rebar015  label="StraightRebar013"  # Arch/BIM 110 (typed FeaturePython)
  Amount = 11
  AmountCheck = true
  Base = -> Sketch089
  Cover = 62
  CoverAlong = Bottom Side
  Diameter = 12
  Direction = (0,0,0)
  Distance = 0
  FrontCover = 44
  HorizontalArea = 0
  Host = -> Structure126
  IfcType = 110
  LeftBottomCover = 44
  Length = 2012
  MoveBase = false
  MoveWithHost = false
  OffsetEnd = 50
  OffsetStart = 50
  Orientation = Horizontal
  PerimeterLength = 0
  PlacementList = 11 placements: arithmetic series from (0,50,-1.11022e-14) step (0,200,-4.44089e-14) to (0,2050,-4.55191e-13)
  RightTopCover = 44
  Rounding = 0
  Spacing = 200
  TotalLength = 22132
  TrueSpacing = 11
  VerticalArea = 0
FEATURE [Sketcher::SketchObject] Sketch090
  MapMode = 5
  Placement = pos=(10380,9630,2.046e-12) rot=(0.57735,-0.57735,-0.57735;2.0944rad)
  Support = -> [Structure128]
  sketch-geometry (1):
    g0: LineSegment StartX=-856 StartY=-1744 StartZ=0 EndX=1156 EndY=-1744 EndZ=0
FEATURE [Part::FeaturePython] Rebar016  label="StraightRebar014"  # Arch/BIM 110 (typed FeaturePython)
  Amount = 11
  AmountCheck = true
  Base = -> Sketch090
  Cover = 50
  CoverAlong = Bottom Side
  Diameter = 12
  Direction = (0,0,0)
  Distance = 0
  FrontCover = 44
  HorizontalArea = 0
  Host = -> Structure128
  IfcType = 110
  LeftBottomCover = 44
  Length = 2012
  MoveBase = false
  MoveWithHost = false
  OffsetEnd = 50
  OffsetStart = 50
  Orientation = Horizontal
  PerimeterLength = 0
  Placement = pos=(0,300,0) rot=(0,0,1;0rad)
  PlacementList = 11 placements: arithmetic series from (50,0,0) step (200,0,0) to (2050,0,0)
  RightTopCover = 44
  Rounding = 0
  Spacing = 200
  TotalLength = 22132
  TrueSpacing = 11
  VerticalArea = 0
FEATURE [Sketcher::SketchObject] Sketch091
  MapMode = 5
  Placement = pos=(11280,8730,2.046e-12) rot=(1,0,0;1.5708rad)
  Support = -> [Structure128]
  sketch-geometry (1):
    g0: LineSegment StartX=-856 StartY=-1732 StartZ=0 EndX=1156 EndY=-1732 EndZ=0
FEATURE [Part::FeaturePython] Rebar017  label="StraightRebar015"  # Arch/BIM 110 (typed FeaturePython)
  Amount = 11
  AmountCheck = true
  Base = -> Sketch091
  Cover = 62
  CoverAlong = Bottom Side
  Diameter = 12
  Direction = (0,0,0)
  Distance = 0
  FrontCover = 44
  HorizontalArea = 0
  Host = -> Structure128
  IfcType = 110
  LeftBottomCover = 44
  Length = 2012
  MoveBase = false
  MoveWithHost = false
  OffsetEnd = 50
  OffsetStart = 50
  Orientation = Horizontal
  PerimeterLength = 0
  PlacementList = 11 placements: arithmetic series from (0,50,-1.11022e-14) step (0,200,-4.44089e-14) to (0,2050,-4.55191e-13)
  RightTopCover = 44
  Rounding = 0
  Spacing = 200
  TotalLength = 22132
  TrueSpacing = 11
  VerticalArea = 0
FEATURE [Sketcher::SketchObject] Sketch092
  MapMode = 5
  Placement = pos=(14750,9630,2.046e-12) rot=(0.57735,-0.57735,-0.57735;2.0944rad)
  Support = -> [Structure131]
  sketch-geometry (1):
    g0: LineSegment StartX=-856 StartY=-1744 StartZ=0 EndX=1156 EndY=-1744 EndZ=0
FEATURE [Part::FeaturePython] Rebar018  label="StraightRebar016"  # Arch/BIM 110 (typed FeaturePython)
  Amount = 11
  AmountCheck = true
  Base = -> Sketch092
  Cover = 50
  CoverAlong = Bottom Side
  Diameter = 12
  Direction = (0,0,0)
  Distance = 0
  FrontCover = 44
  HorizontalArea = 0
  Host = -> Structure131
  IfcType = 110
  LeftBottomCover = 44
  Length = 2012
  MoveBase = false
  MoveWithHost = false
  OffsetEnd = 50
  OffsetStart = 50
  Orientation = Horizontal
  PerimeterLength = 0
  Placement = pos=(0,300,0) rot=(0,0,1;0rad)
  PlacementList = 11 placements: arithmetic series from (50,0,0) step (200,0,0) to (2050,0,0)
  RightTopCover = 44
  Rounding = 0
  Spacing = 200
  TotalLength = 22132
  TrueSpacing = 11
  VerticalArea = 0
FEATURE [Sketcher::SketchObject] Sketch094
  MapMode = 5
  Placement = pos=(15650,8730,2.046e-12) rot=(1,0,0;1.5708rad)
  Support = -> [Structure131]
  sketch-geometry (1):
    g0: LineSegment StartX=-856 StartY=-1732 StartZ=0 EndX=1156 EndY=-1732 EndZ=0
FEATURE [Part::FeaturePython] Rebar019  label="StraightRebar017"  # Arch/BIM 110 (typed FeaturePython)
  Amount = 11
  AmountCheck = true
  Base = -> Sketch094
  Cover = 62
  CoverAlong = Bottom Side
  Diameter = 12
  Direction = (0,0,0)
  Distance = 0
  FrontCover = 44
  HorizontalArea = 0
  Host = -> Structure131
  IfcType = 110
  LeftBottomCover = 44
  Length = 2012
  MoveBase = false
  MoveWithHost = false
  OffsetEnd = 50
  OffsetStart = 50
  Orientation = Horizontal
  PerimeterLength = 0
  PlacementList = 11 placements: arithmetic series from (0,50,-1.11022e-14) step (0,200,-4.44089e-14) to (0,2050,-4.55191e-13)
  RightTopCover = 44
  Rounding = 0
  Spacing = 200
  TotalLength = 22132
  TrueSpacing = 11
  VerticalArea = 0
FEATURE [Sketcher::SketchObject] Sketch095
  MapMode = 5
  Placement = pos=(4140,0,0) rot=(0.57735,-0.57735,-0.57735;2.0944rad)
  Support = -> [Structure132]
  sketch-geometry (1):
    g0: LineSegment StartX=3944 StartY=-1744 StartZ=0 EndX=6356 EndY=-1744 EndZ=0
FEATURE [Part::FeaturePython] Rebar020  label="StraightRebar018"  # Arch/BIM 110 (typed FeaturePython)
  Amount = 13
  AmountCheck = true
  Base = -> Sketch095
  Cover = 50
  CoverAlong = Bottom Side
  Diameter = 12
  Direction = (0,0,0)
  Distance = 0
  FrontCover = 44
  HorizontalArea = 0
  Host = -> Structure132
  IfcType = 110
  LeftBottomCover = 44
  Length = 2412
  MoveBase = false
  MoveWithHost = false
  OffsetEnd = 50
  OffsetStart = 50
  Orientation = Horizontal
  PerimeterLength = 0
  Placement = pos=(0,10300,0) rot=(0,0,1;0rad)
  PlacementList = 13 placements: arithmetic series from (50,0,0) step (200,0,0) to (2450,0,0)
  RightTopCover = 44
  Rounding = 0
  Spacing = 200
  TotalLength = 31356
  TrueSpacing = 13
  VerticalArea = 0
FEATURE [Sketcher::SketchObject] Sketch096
  MapMode = 5
  Placement = pos=(0,3900,0) rot=(1,0,0;1.5708rad)
  Support = -> [Structure132]
  sketch-geometry (1):
    g0: LineSegment StartX=4184 StartY=-1732 StartZ=0 EndX=6596 EndY=-1732 EndZ=0
FEATURE [Part::FeaturePython] Rebar021  label="StraightRebar019"  # Arch/BIM 110 (typed FeaturePython)
  Amount = 13
  AmountCheck = true
  Base = -> Sketch096
  Cover = 62
  CoverAlong = Bottom Side
  Diameter = 12
  Direction = (0,0,0)
  Distance = 0
  FrontCover = 44
  HorizontalArea = 0
  Host = -> Structure132
  IfcType = 110
  LeftBottomCover = 44
  Length = 2412
  MoveBase = false
  MoveWithHost = false
  OffsetEnd = 50
  OffsetStart = 50
  Orientation = Horizontal
  PerimeterLength = 0
  PlacementList = 13 placements: arithmetic series from (0,50,-1.11022e-14) step (0,200,-4.44089e-14) to (0,2450,-5.44009e-13)
  RightTopCover = 44
  Rounding = 0
  Spacing = 200
  TotalLength = 31356
  TrueSpacing = 13
  VerticalArea = 0
FEATURE [Sketcher::SketchObject] Sketch097
  MapMode = 5
  Placement = pos=(10180,0,0) rot=(0.57735,-0.57735,-0.57735;2.0944rad)
  Support = -> [Structure133]
  sketch-geometry (1):
    g0: LineSegment StartX=3944 StartY=-1744 StartZ=0 EndX=6356 EndY=-1744 EndZ=0
FEATURE [Part::FeaturePython] Rebar022  label="StraightRebar020"  # Arch/BIM 110 (typed FeaturePython)
  Amount = 13
  AmountCheck = true
  Base = -> Sketch097
  Cover = 50
  CoverAlong = Bottom Side
  Diameter = 12
  Direction = (0,0,0)
  Distance = 0
  FrontCover = 44
  HorizontalArea = 0
  Host = -> Structure133
  IfcType = 110
  LeftBottomCover = 44
  Length = 2412
  MoveBase = false
  MoveWithHost = false
  OffsetEnd = 50
  OffsetStart = 50
  Orientation = Horizontal
  PerimeterLength = 0
  Placement = pos=(0,10300,0) rot=(0,0,1;0rad)
  PlacementList = 13 placements: arithmetic series from (50,0,0) step (200,0,0) to (2450,0,0)
  RightTopCover = 44
  Rounding = 0
  Spacing = 200
  TotalLength = 31356
  TrueSpacing = 13
  VerticalArea = 0
FEATURE [Sketcher::SketchObject] Sketch098
  MapMode = 5
  Placement = pos=(6040,3900,0) rot=(1,0,0;1.5708rad)
  Support = -> [Structure133]
  sketch-geometry (1):
    g0: LineSegment StartX=4184 StartY=-1732 StartZ=0 EndX=6596 EndY=-1732 EndZ=0
FEATURE [Part::FeaturePython] Rebar023  label="StraightRebar021"  # Arch/BIM 110 (typed FeaturePython)
  Amount = 13
  AmountCheck = true
  Base = -> Sketch098
  Cover = 62
  CoverAlong = Bottom Side
  Diameter = 12
  Direction = (0,0,0)
  Distance = 0
  FrontCover = 44
  HorizontalArea = 0
  Host = -> Structure133
  IfcType = 110
  LeftBottomCover = 44
  Length = 2412
  MoveBase = false
  MoveWithHost = false
  OffsetEnd = 50
  OffsetStart = 50
  Orientation = Horizontal
  PerimeterLength = 0
  PlacementList = 13 placements: arithmetic series from (0,50,-1.11022e-14) step (0,200,-4.44089e-14) to (0,2450,-5.44009e-13)
  RightTopCover = 44
  Rounding = 0
  Spacing = 200
  TotalLength = 31356
  TrueSpacing = 13
  VerticalArea = 0
FEATURE [Spreadsheet::Sheet] RebarBillOfMaterial  label="BOM Footing"
  cells = A1=Member; B1=Mark; C1=No. of Rebars; D1=Diameter in mm; E1=Length in m/piece; F1=Total Length in m; F2=#12.0; A3=Footing001; C3=11; D3==12mm; E3==2012mm; F3==22132mm; C4=11; D4==12mm; E4==2012mm; F4==22132mm; A6=Footing004; C6=11; D6==12mm; E6==2012mm; F6==22132mm; C7=11; D7==12mm; E7==2012mm; F7==22132mm; A9=Footing006; C9=11; D9==12mm; E9==2012mm; F9==22132mm; C10=11; D10==12mm; E10==2012mm; F10==22132mm; A12=Footing008; C12=11; D12==12mm; E12==2012mm; F12==22132mm; C13=11; D13==12mm; E13==2012mm; F13==22132mm; A15=Footing002; C15=11; D15==12mm; E15==2012mm; F15==22132mm; C16=11; D16==12mm; E16==2012mm; F16==22132mm; A18=Footing009; C18=11; D18==12mm; E18==2012mm; F18==22132mm; C19=11; D19==12mm; E19==2012mm; F19==22132mm; A21=Footing003; C21=11; D21==12mm; E21==2012mm; F21==22132mm; C22=11; D22==12mm; E22==2012mm; F22==22132mm; A24=Footing005; C24=11; D24==12mm; E24==2012mm; F24==22132mm; C25=11; D25==12mm; E25==2012mm; F25==22132mm; A27=Footing007; C27=11; D27==12mm; E27==2012mm; F27==22132mm; C28=11; D28==12mm; E28==2012mm; F28==22132mm; A30=Footing010; C30=11; D30==12mm; E30==2012mm; F30==22132mm; C31=11; D31==12mm; E31==2012mm; F31==22132mm; A33=Footing011; C33=13; D33==12mm; E33==2412.0000000000009mm; F33==31356.000000000011mm; C34=13; D34==12mm; E34==2412.0000000000009mm; F34==31356.000000000011mm; A36=Footing012; C36=13; D36==12mm; E36==2412.0000000000009mm; F36==31356.000000000011mm; C37=13; D37==12mm; E37==2412.0000000000018mm; F37==31356.000000000022mm; A43=Total length in m/Diameter; F43==568064mm; A44=Weight in Kg/m; F44==0.00088800000000000001kg / mm; A45=Total Weight in Kg/Diameter; F45==504.440832kg
FEATURE [Sketcher::SketchObject] Sketch099
  ExternalGeometry = -> [Structure064]
  MapMode = 5
  Placement = pos=(0,0,0) rot=(0.57735,-0.57735,-0.57735;2.0944rad)
  Support = -> [Structure064]
  sketch-geometry (3):
    g0: LineSegment StartX=-5150 StartY=3620 StartZ=0 EndX=-3800 EndY=3620 EndZ=0
    g1: LineSegment StartX=-3800 StartY=3620 StartZ=0 EndX=-3710 EndY=3530 EndZ=0
    g2: LineSegment StartX=-3710 StartY=3530 StartZ=0 EndX=-10 EndY=3530 EndZ=0
  constraints (10):
    c: Horizontal(g0)
    c: Coincident(g0,g1)
    c: Coincident(g1,g2)
    c: Horizontal(g2)
    c: DistanceX(g-3,g0) = 0
    c: DistanceY(g0,g-3) = 30
    c: Angle(g2,g1) = 2.35619
    c: DistanceX(g2,g-4) = 10
    c: DistanceY(g-4,g2) = 30
    c: DistanceX(g-4,g1) = 1440
FEATURE [Part::FeaturePython] Rebar024  label="Rebar"  # Arch/BIM 110 (typed FeaturePython)
  Amount = 15
  Base = -> Sketch099
  Diameter = 10
  Direction = (0,0,0)
  Distance = 0
  HorizontalArea = 0
  Host = -> Structure064
  IfcType = 110
  Length = 5177.28
  MoveBase = false
  MoveWithHost = false
  OffsetEnd = 10
  OffsetStart = 10
  PerimeterLength = 0
  PlacementList = 15 placements: arithmetic series from (10,0,0) step (394.286,0,0) to (5530,0,0)
  Rounding = 0
  Spacing = 394.286
  TotalLength = 77659.2
  VerticalArea = 0
FEATURE [Sketcher::SketchObject] Sketch100
  ExternalGeometry = -> [Structure064]
  MapMode = 5
  Placement = pos=(0,0,0) rot=(0.57735,-0.57735,-0.57735;2.0944rad)
  Support = -> [Structure064]
  sketch-geometry (3):
    g0: LineSegment StartX=-5150 StartY=3530 StartZ=0 EndX=-920 EndY=3530 EndZ=0
    g1: LineSegment StartX=-920 StartY=3530 StartZ=0 EndX=-830 EndY=3620 EndZ=0
    g2: LineSegment StartX=-830 StartY=3620 StartZ=0 EndX=-10 EndY=3620 EndZ=0
  constraints (10):
    c: Horizontal(g0)
    c: Coincident(g0,g1)
    c: Coincident(g1,g2)
    c: Horizontal(g2)
    c: DistanceY(g2,g-3) = 30
    c: DistanceX(g2,g-3) = 10
    c: Angle(g1,g0) = 2.35619
    c: DistanceX(g-4,g0) = 0
    c: DistanceX(g0,g-4) = 920
    c: DistanceY(g-4,g0) = 30
FEATURE [Part::FeaturePython] Rebar025  # Arch/BIM 110 (typed FeaturePython)
  Amount = 14
  Base = -> Sketch100
  Diameter = 10
  Direction = (0,0,0)
  Distance = 0
  HorizontalArea = 0
  Host = -> Structure064
  IfcType = 110
  Length = 5177.28
  MoveBase = false
  MoveWithHost = false
  OffsetEnd = 210
  OffsetStart = 210
  PerimeterLength = 0
  PlacementList = 14 placements: arithmetic series from (210,0,0) step (393.846,0,0) to (5330,0,0)
  Rounding = 0
  Spacing = 393.846
  TotalLength = 72481.9
  VerticalArea = 0
FEATURE [Sketcher::SketchObject] Sketch101
  ExternalGeometry = -> [Structure064]
  MapMode = 5
  Placement = pos=(0,-9.095e-13,0) rot=(1,0,0;1.5708rad)
  Support = -> [Structure064]
  sketch-geometry (3):
    g0: LineSegment StartX=10 StartY=3630 StartZ=0 EndX=870 EndY=3630 EndZ=0
    g1: LineSegment StartX=870 StartY=3630 StartZ=0 EndX=960 EndY=3540 EndZ=0
    g2: LineSegment StartX=960 StartY=3540 StartZ=0 EndX=5530 EndY=3540 EndZ=0
  constraints (10):
    c: Horizontal(g0)
    c: Coincident(g0,g1)
    c: Coincident(g1,g2)
    c: Horizontal(g2)
    c: DistanceY(g-4,g2) = 40
    c: DistanceX(g2,g-4) = 10
    c: DistanceX(g-3,g0) = 10
    c: DistanceY(g0,g-3) = 20
    c: Angle(g2,g1) = 2.35619
    c: DistanceX(g-4,g1) = 960
FEATURE [Part::FeaturePython] Rebar026  # Arch/BIM 110 (typed FeaturePython)
  Amount = 14
  Base = -> Sketch101
  Diameter = 10
  Direction = (0,0,0)
  Distance = 0
  HorizontalArea = 0
  Host = -> Structure064
  IfcType = 110
  Length = 5557.28
  MoveBase = false
  MoveWithHost = false
  OffsetEnd = 10
  OffsetStart = 10
  PerimeterLength = 0
  PlacementList = 14 placements: arithmetic series from (0,10,-2.22045e-15) step (0,394.615,-8.76222e-14) to (0,5140,-1.14131e-12)
  Rounding = 0
  Spacing = 394.615
  TotalLength = 77801.9
  VerticalArea = 0
FEATURE [Sketcher::SketchObject] Sketch102
  ExternalGeometry = -> [Structure064]
  MapMode = 5
  Placement = pos=(0,-9.095e-13,0) rot=(1,0,0;1.5708rad)
  Support = -> [Structure064]
  sketch-geometry (3):
    g0: LineSegment StartX=10 StartY=3540 StartZ=0 EndX=4580 EndY=3540 EndZ=0
    g1: LineSegment StartX=4580 StartY=3540 StartZ=0 EndX=4670 EndY=3630 EndZ=0
    g2: LineSegment StartX=4670 StartY=3630 StartZ=0 EndX=5530 EndY=3630 EndZ=0
  constraints (10):
    c: Horizontal(g0)
    c: Coincident(g0,g1)
    c: Coincident(g1,g2)
    c: Horizontal(g2)
    c: DistanceY(g-4,g0) = 40
    c: DistanceX(g-4,g0) = 10
    c: Angle(g1,g0) = 2.35619
    c: DistanceY(g1,g-3) = 20
    c: DistanceX(g2,g-3) = 10
    c: DistanceX(g0,g-4) = 960
FEATURE [Part::FeaturePython] Rebar027  # Arch/BIM 110 (typed FeaturePython)
  Amount = 13
  Base = -> Sketch102
  Diameter = 10
  Direction = (0,0,0)
  Distance = 0
  HorizontalArea = 0
  Host = -> Structure064
  IfcType = 110
  Length = 5557.28
  MoveBase = false
  MoveWithHost = false
  OffsetEnd = 210
  OffsetStart = 210
  PerimeterLength = 0
  PlacementList = 13 placements: arithmetic series from (0,210,-4.66294e-14) step (0,394.167,-8.75226e-14) to (0,4940,-1.0969e-12)
  Rounding = 0
  Spacing = 394.167
  TotalLength = 72244.6
  VerticalArea = 0
FEATURE [Sketcher::SketchObject] Sketch103
  ExternalGeometry = -> [Structure062]
  MapMode = 5
  Placement = pos=(0,-3.638e-12,0) rot=(1,0,0;1.5708rad)
  Support = -> [Structure062]
  sketch-geometry (3):
    g0: LineSegment StartX=11290 StartY=3620 StartZ=0 EndX=12020 EndY=3620 EndZ=0
    g1: LineSegment StartX=12020 StartY=3620 StartZ=0 EndX=12110 EndY=3530 EndZ=0
    g2: LineSegment StartX=12110 StartY=3530 StartZ=0 EndX=15940 EndY=3530 EndZ=0
  constraints (10):
    c: Horizontal(g0)
    c: Coincident(g0,g1)
    c: Coincident(g1,g2)
    c: Horizontal(g2)
    c: DistanceX(g-3,g0) = 10
    c: Angle(g2,g1) = 2.35619
    c: DistanceX(g2,g-4) = 10
    c: DistanceX(g-4,g1) = 830
    c: DistanceY(g-4,g1) = 30
    c: DistanceY(g0,g-3) = 30
FEATURE [Part::FeaturePython] Rebar028  # Arch/BIM 110 (typed FeaturePython)
  Amount = 14
  Base = -> Sketch103
  Diameter = 10
  Direction = (0,0,0)
  Distance = 0
  HorizontalArea = 0
  Host = -> Structure062
  IfcType = 110
  Length = 4687.28
  MoveBase = false
  MoveWithHost = false
  OffsetEnd = 10
  OffsetStart = 10
  PerimeterLength = 0
  PlacementList = 14 placements: arithmetic series from (0,10,-2.22045e-15) step (0,394.615,-8.76222e-14) to (0,5140,-1.14131e-12)
  Rounding = 0
  Spacing = 394.615
  TotalLength = 65621.9
  VerticalArea = 0
FEATURE [Sketcher::SketchObject] Sketch104
  ExternalGeometry = -> [Structure062]
  MapMode = 5
  Placement = pos=(0,-3.638e-12,0) rot=(1,0,0;1.5708rad)
  Support = -> [Structure062]
  sketch-geometry (3):
    g0: LineSegment StartX=11290 StartY=3530 StartZ=0 EndX=15120 EndY=3530 EndZ=0
    g1: LineSegment StartX=15120 StartY=3530 StartZ=0 EndX=15210 EndY=3620 EndZ=0
    g2: LineSegment StartX=15210 StartY=3620 StartZ=0 EndX=15940 EndY=3620 EndZ=0
  constraints (10):
    c: Horizontal(g0)
    c: Coincident(g0,g1)
    c: Coincident(g1,g2)
    c: Horizontal(g2)
    c: DistanceX(g-4,g0) = 10
    c: Angle(g1,g0) = 2.35619
    c: DistanceX(g2,g-3) = 10
    c: DistanceX(g0,g-4) = 830
    c: DistanceY(g-4,g0) = 30
    c: DistanceY(g2,g-3) = 30
FEATURE [Part::FeaturePython] Rebar029  # Arch/BIM 110 (typed FeaturePython)
  Amount = 13
  Base = -> Sketch104
  Diameter = 10
  Direction = (0,0,0)
  Distance = 0
  HorizontalArea = 0
  Host = -> Structure062
  IfcType = 110
  Length = 4687.28
  MoveBase = false
  MoveWithHost = false
  OffsetEnd = 210
  OffsetStart = 210
  PerimeterLength = 0
  PlacementList = 13 placements: arithmetic series from (0,210,-4.66294e-14) step (0,394.167,-8.75226e-14) to (0,4940,-1.0969e-12)
  Rounding = 0
  Spacing = 394.167
  TotalLength = 60934.6
  VerticalArea = 0
FEATURE [Sketcher::SketchObject] Sketch105
  ExternalGeometry = -> [Structure062]
  MapMode = 5
  Placement = pos=(15950,0,0) rot=(0.57735,0.57735,0.57735;2.0944rad)
  Support = -> [Structure062]
  sketch-geometry (3):
    g0: LineSegment StartX=10 StartY=3539 StartZ=0 EndX=3710 EndY=3539 EndZ=0
    g1: LineSegment StartX=3710 StartY=3539 StartZ=0 EndX=3800 EndY=3629 EndZ=0
    g2: LineSegment StartX=3800 StartY=3629 StartZ=0 EndX=5150 EndY=3629 EndZ=0
  constraints (10):
    c: Horizontal(g0)
    c: Coincident(g0,g1)
    c: Coincident(g1,g2)
    c: Horizontal(g2)
    c: DistanceX(g2,g-3) = 0
    c: DistanceY(g2,g-3) = 21
    c: DistanceY(g-4,g0) = 39
    c: DistanceX(g-4,g0) = 10
    c: Angle(g1,g0) = 2.35619
    c: DistanceX(g0,g-4) = 1440
FEATURE [Part::FeaturePython] Rebar030  # Arch/BIM 110 (typed FeaturePython)
  Amount = 13
  Base = -> Sketch105
  Diameter = 8
  Direction = (0,0,0)
  Distance = 0
  HorizontalArea = 0
  Host = -> Structure062
  IfcType = 110
  Length = 5177.28
  MoveBase = false
  MoveWithHost = false
  OffsetEnd = 10
  OffsetStart = 10
  PerimeterLength = 0
  PlacementList = 13 placements: arithmetic series from (-10,0,0) step (-387.5,0,0) to (-4660,0,0)
  Rounding = 0
  Spacing = 387.5
  TotalLength = 67304.6
  VerticalArea = 0
FEATURE [Sketcher::SketchObject] Sketch106
  ExternalGeometry = -> [Structure062]
  MapMode = 5
  Placement = pos=(15950,0,0) rot=(0.57735,0.57735,0.57735;2.0944rad)
  Support = -> [Structure062]
  sketch-geometry (3):
    g0: LineSegment StartX=10 StartY=3629 StartZ=0 EndX=830 EndY=3629 EndZ=0
    g1: LineSegment StartX=830 StartY=3629 StartZ=0 EndX=920 EndY=3539 EndZ=0
    g2: LineSegment StartX=920 StartY=3539 StartZ=0 EndX=5150 EndY=3539 EndZ=0
  constraints (10):
    c: Horizontal(g0)
    c: Coincident(g0,g1)
    c: Coincident(g1,g2)
    c: Horizontal(g2)
    c: DistanceX(g-3,g0) = 10
    c: Angle(g2,g1) = 2.35619
    c: DistanceY(g0,g-3) = 21
    c: DistanceY(g-4,g1) = 39
    c: DistanceX(g2,g-4) = 0
    c: DistanceX(g-4,g1) = 920
FEATURE [Part::FeaturePython] Rebar031  # Arch/BIM 110 (typed FeaturePython)
  Amount = 12
  Base = -> Sketch106
  Diameter = 8
  Direction = (0,0,0)
  Distance = 0
  HorizontalArea = 0
  Host = -> Structure062
  IfcType = 110
  Length = 5177.28
  MoveBase = false
  MoveWithHost = false
  OffsetEnd = 210
  OffsetStart = 210
  PerimeterLength = 0
  PlacementList = 12 placements: arithmetic series from (-210,0,0) step (-386.364,0,0) to (-4460,0,0)
  Rounding = 0
  Spacing = 386.364
  TotalLength = 62127.4
  VerticalArea = 0
FEATURE [Sketcher::SketchObject] Sketch107
  ExternalGeometry = -> [Structure058]
  MapMode = 5
  Placement = pos=(-9.095e-13,0,0) rot=(0.57735,-0.57735,-0.57735;2.0944rad)
  Support = -> [Structure058]
  sketch-geometry (3):
    g0: LineSegment StartX=-5150 StartY=3620 StartZ=0 EndX=-6405 EndY=3620 EndZ=0
    g1: LineSegment StartX=-6405 StartY=3620 StartZ=0 EndX=-6495 EndY=3530 EndZ=0
    g2: LineSegment StartX=-6495 StartY=3530 StartZ=0 EndX=-9920 EndY=3530 EndZ=0
  constraints (10):
    c: Horizontal(g0)
    c: Coincident(g0,g1)
    c: Coincident(g1,g2)
    c: Horizontal(g2)
    c: DistanceY(g0,g-3) = 30
    c: DistanceY(g-4,g1) = 30
    c: DistanceX(g0,g-3) = 0
    c: DistanceX(g-4,g2) = 10
    c: DistanceX(g1,g-4) = 1345
    c: Angle(g1,g2) = 2.35619
FEATURE [Part::FeaturePython] Rebar032  # Arch/BIM 110 (typed FeaturePython)
  Amount = 14
  Base = -> Sketch107
  Diameter = 10
  Direction = (0,0,0)
  Distance = 0
  HorizontalArea = 0
  Host = -> Structure058
  IfcType = 110
  Length = 4807.28
  MoveBase = false
  MoveWithHost = false
  OffsetEnd = 254.3
  OffsetStart = 10
  PerimeterLength = 0
  PlacementList = 14 placements: arithmetic series from (10,0,0) step (394.285,0,0) to (5135.7,0,0)
  Rounding = 0
  Spacing = 394.285
  TotalLength = 67301.9
  VerticalArea = 0
FEATURE [Sketcher::SketchObject] Sketch108
  ExternalGeometry = -> [Structure058]
  MapMode = 5
  Placement = pos=(-9.095e-13,0,0) rot=(0.57735,-0.57735,-0.57735;2.0944rad)
  Support = -> [Structure058]
  sketch-geometry (3):
    g0: LineSegment StartX=-9920 StartY=3620 StartZ=0 EndX=-9150 EndY=3620 EndZ=0
    g1: LineSegment StartX=-9150 StartY=3620 StartZ=0 EndX=-9060 EndY=3530 EndZ=0
    g2: LineSegment StartX=-9060 StartY=3530 StartZ=0 EndX=-5150 EndY=3530 EndZ=0
  constraints (10):
    c: Horizontal(g0)
    c: Coincident(g0,g1)
    c: Coincident(g1,g2)
    c: Horizontal(g2)
    c: DistanceX(g-3,g0) = 10
    c: DistanceY(g0,g-3) = 30
    c: DistanceY(g-4,g1) = 30
    c: Angle(g2,g1) = 2.35619
    c: DistanceX(g-4,g1) = 870
    c: DistanceX(g2,g-4) = 0
FEATURE [Part::FeaturePython] Rebar033  # Arch/BIM 110 (typed FeaturePython)
  Amount = 14
  Base = -> Sketch108
  Diameter = 10
  Direction = (0,0,0)
  Distance = 0
  HorizontalArea = 0
  Host = -> Structure058
  IfcType = 110
  Length = 4807.28
  MoveBase = false
  MoveWithHost = false
  OffsetEnd = 60
  OffsetStart = 210
  PerimeterLength = 0
  PlacementList = 14 placements: arithmetic series from (210,0,0) step (393.846,0,0) to (5330,0,0)
  Rounding = 0
  Spacing = 393.846
  TotalLength = 67301.9
  VerticalArea = 0
FEATURE [Sketcher::SketchObject] Sketch109
  ExternalGeometry = -> [Structure058]
  MapMode = 5
  Placement = pos=(0,9930,0) rot=(0,0.707107,0.707107;3.14159rad)
  Support = -> [Structure058]
  sketch-geometry (3):
    g0: LineSegment StartX=-5390 StartY=3630 StartZ=0 EndX=-3980 EndY=3630 EndZ=0
    g1: LineSegment StartX=-3980 StartY=3630 StartZ=0 EndX=-3890 EndY=3540 EndZ=0
    g2: LineSegment StartX=-3890 StartY=3540 StartZ=0 EndX=-10 EndY=3540 EndZ=0
  constraints (10):
    c: Horizontal(g0)
    c: Coincident(g0,g1)
    c: Coincident(g1,g2)
    c: Horizontal(g2)
    c: DistanceX(g-3,g0) = 0
    c: Angle(g2,g1) = 2.35619
    c: DistanceY(g0,g-3) = 20
    c: DistanceY(g-4,g1) = 40
    c: DistanceX(g2,g-4) = 10
    c: DistanceX(g-4,g1) = 1500
FEATURE [Part::FeaturePython] Rebar034  # Arch/BIM 110 (typed FeaturePython)
  Amount = 13
  Base = -> Sketch109
  Diameter = 10
  Direction = (0,0,0)
  Distance = 0
  HorizontalArea = 0
  Host = -> Structure058
  IfcType = 110
  Length = 5417.28
  MoveBase = false
  MoveWithHost = false
  OffsetEnd = 10
  OffsetStart = 10
  PerimeterLength = 0
  PlacementList = 13 placements: arithmetic series from (0,-10,2.22045e-15) step (0,-396.667,8.80777e-14) to (0,-4770,1.05915e-12)
  Rounding = 0
  Spacing = 396.667
  TotalLength = 70424.6
  VerticalArea = 0
FEATURE [Sketcher::SketchObject] Sketch110
  ExternalGeometry = -> [Structure058]
  MapMode = 5
  Placement = pos=(0,9930,0) rot=(0,0.707107,0.707107;3.14159rad)
  Support = -> [Structure058]
  sketch-geometry (3):
    g0: LineSegment StartX=-5390 StartY=3540 StartZ=0 EndX=-960 EndY=3540 EndZ=0
    g1: LineSegment StartX=-960 StartY=3540 StartZ=0 EndX=-870 EndY=3630 EndZ=0
    g2: LineSegment StartX=-870 StartY=3630 StartZ=0 EndX=-10 EndY=3630 EndZ=0
  constraints (10):
    c: Horizontal(g0)
    c: Coincident(g0,g1)
    c: Coincident(g1,g2)
    c: Horizontal(g2)
    c: DistanceX(g-3,g0) = 0
    c: DistanceX(g2,g-3) = 10
    c: DistanceX(g0,g-4) = 960
    c: Angle(g1,g0) = 2.35619
    c: DistanceY(g-4,g0) = 40
    c: DistanceY(g2,g-3) = 20
FEATURE [Part::FeaturePython] Rebar035  # Arch/BIM 110 (typed FeaturePython)
  Amount = 12
  Base = -> Sketch110
  Diameter = 10
  Direction = (0,0,0)
  Distance = 0
  HorizontalArea = 0
  Host = -> Structure058
  IfcType = 110
  Length = 5417.28
  MoveBase = false
  MoveWithHost = false
  OffsetEnd = 210
  OffsetStart = 210
  PerimeterLength = 0
  PlacementList = 12 placements: arithmetic series from (0,-210,4.66294e-14) step (0,-396.364,8.80104e-14) to (0,-4570,1.01474e-12)
  Rounding = 0
  Spacing = 396.364
  TotalLength = 65007.4
  VerticalArea = 0
FEATURE [Sketcher::SketchObject] Sketch111
  ExternalGeometry = -> [Structure060]
  MapMode = 5
  Placement = pos=(0,9930,0) rot=(0,0.707107,0.707107;3.14159rad)
  Support = -> [Structure060]
  sketch-geometry (3):
    g0: LineSegment StartX=-11430 StartY=3540 StartZ=0 EndX=-7050 EndY=3540 EndZ=0
    g1: LineSegment StartX=-7050 StartY=3540 StartZ=0 EndX=-6960 EndY=3630 EndZ=0
    g2: LineSegment StartX=-6960 StartY=3630 StartZ=0 EndX=-5390 EndY=3630 EndZ=0
  constraints (10):
    c: Horizontal(g0)
    c: Coincident(g0,g1)
    c: Coincident(g1,g2)
    c: Horizontal(g2)
    c: DistanceY(g-4,g0) = 40
    c: DistanceY(g1,g-3) = 20
    c: Angle(g1,g0) = 2.35619
    c: DistanceX(g2,g-3) = 0
    c: DistanceX(g0,g-4) = 1660
    c: DistanceX(g-4,g0) = 0
FEATURE [Part::FeaturePython] Rebar036  # Arch/BIM 110 (typed FeaturePython)
  Amount = 13
  Base = -> Sketch111
  Diameter = 8
  Direction = (0,0,0)
  Distance = 0
  HorizontalArea = 0
  Host = -> Structure060
  IfcType = 110
  Length = 6077.28
  MoveBase = false
  MoveWithHost = false
  OffsetEnd = 10
  OffsetStart = 10
  PerimeterLength = 0
  PlacementList = 13 placements: arithmetic series from (0,-10,2.22045e-15) step (0,-396.667,8.80777e-14) to (0,-4770,1.05915e-12)
  Rounding = 0
  Spacing = 396.667
  TotalLength = 79004.6
  VerticalArea = 0
FEATURE [Sketcher::SketchObject] Sketch112
  ExternalGeometry = -> [Structure060]
  MapMode = 5
  Placement = pos=(0,9930,0) rot=(0,0.707107,0.707107;3.14159rad)
  Support = -> [Structure060]
  sketch-geometry (3):
    g0: LineSegment StartX=-11430 StartY=3630 StartZ=0 EndX=-9860 EndY=3630 EndZ=0
    g1: LineSegment StartX=-9860 StartY=3630 StartZ=0 EndX=-9770 EndY=3540 EndZ=0
    g2: LineSegment StartX=-9770 StartY=3540 StartZ=0 EndX=-5390 EndY=3540 EndZ=0
  constraints (10):
    c: Horizontal(g0)
    c: Coincident(g0,g1)
    c: Coincident(g1,g2)
    c: Horizontal(g2)
    c: Angle(g2,g1) = 2.35619
    c: DistanceX(g-3,g0) = 0
    c: DistanceX(g2,g-4) = 0
    c: DistanceX(g-4,g1) = 1660
    c: DistanceY(g-4,g1) = 40
    c: DistanceY(g0,g-3) = 20
FEATURE [Part::FeaturePython] Rebar037  # Arch/BIM 110 (typed FeaturePython)
  Amount = 12
  Base = -> Sketch112
  Diameter = 8
  Direction = (0,0,0)
  Distance = 0
  HorizontalArea = 0
  Host = -> Structure060
  IfcType = 110
  Length = 6077.28
  MoveBase = false
  MoveWithHost = false
  OffsetEnd = 210
  OffsetStart = 210
  PerimeterLength = 0
  PlacementList = 12 placements: arithmetic series from (0,-210,4.66294e-14) step (0,-396.364,8.80104e-14) to (0,-4570,1.01474e-12)
  Rounding = 0
  Spacing = 396.364
  TotalLength = 72927.4
  VerticalArea = 0
FEATURE [Sketcher::SketchObject] Sketch113
  ExternalGeometry = -> [Structure060]
  MapMode = 5
  Placement = pos=(5390,0,0) rot=(0.57735,-0.57735,-0.57735;2.0944rad)
  Support = -> [Structure060]
  sketch-geometry (3):
    g0: LineSegment StartX=-9920 StartY=3622 StartZ=0 EndX=-9150 EndY=3622 EndZ=0
    g1: LineSegment StartX=-9150 StartY=3622 StartZ=0 EndX=-9060 EndY=3532 EndZ=0
    g2: LineSegment StartX=-9060 StartY=3532 StartZ=0 EndX=-5150 EndY=3532 EndZ=0
  constraints (10):
    c: Horizontal(g0)
    c: Coincident(g0,g1)
    c: Coincident(g1,g2)
    c: Horizontal(g2)
    c: DistanceX(g-3,g0) = 10
    c: DistanceX(g2,g-4) = 0
    c: DistanceY(g0,g-3) = 28
    c: DistanceY(g-4,g1) = 32
    c: Angle(g2,g1) = 2.35619
    c: DistanceX(g-4,g1) = 870
FEATURE [Part::FeaturePython] Rebar038  # Arch/BIM 110 (typed FeaturePython)
  Amount = 15
  Base = -> Sketch113
  Diameter = 8
  Direction = (0,0,0)
  Distance = 0
  HorizontalArea = 0
  Host = -> Structure060
  IfcType = 110
  Length = 4807.28
  MoveBase = false
  MoveWithHost = false
  OffsetEnd = 210
  OffsetStart = 210
  PerimeterLength = 0
  PlacementList = 15 placements: arithmetic series from (210,0,0) step (401.429,0,0) to (5830,0,0)
  Rounding = 0
  Spacing = 401.429
  TotalLength = 72109.2
  VerticalArea = 0
FEATURE [Sketcher::SketchObject] Sketch114
  ExternalGeometry = -> [Structure060]
  MapMode = 5
  Placement = pos=(5390,0,0) rot=(0.57735,-0.57735,-0.57735;2.0944rad)
  Support = -> [Structure060]
  sketch-geometry (3):
    g0: LineSegment StartX=-9920 StartY=3532 StartZ=0 EndX=-6495 EndY=3532 EndZ=0
    g1: LineSegment StartX=-6495 StartY=3532 StartZ=0 EndX=-6405 EndY=3622 EndZ=0
    g2: LineSegment StartX=-6405 StartY=3622 StartZ=0 EndX=-5150 EndY=3622 EndZ=0
  constraints (10):
    c: Horizontal(g0)
    c: Coincident(g0,g1)
    c: Coincident(g1,g2)
    c: Horizontal(g2)
    c: DistanceY(g-4,g0) = 32
    c: DistanceX(g-4,g0) = 10
    c: Angle(g1,g0) = 2.35619
    c: DistanceX(g2,g-3) = 0
    c: DistanceY(g2,g-3) = 28
    c: DistanceX(g0,g-4) = 1345
FEATURE [Part::FeaturePython] Rebar039  # Arch/BIM 110 (typed FeaturePython)
  Amount = 16
  Base = -> Sketch114
  Diameter = 8
  Direction = (0,0,0)
  Distance = 0
  HorizontalArea = 0
  Host = -> Structure060
  IfcType = 110
  Length = 4807.28
  MoveBase = false
  MoveWithHost = false
  OffsetEnd = 10
  OffsetStart = 10
  PerimeterLength = 0
  PlacementList = 16 placements: arithmetic series from (10,0,0) step (401.333,0,0) to (6030,0,0)
  Rounding = 0
  Spacing = 401.333
  TotalLength = 76916.5
  VerticalArea = 0
FEATURE [Sketcher::SketchObject] Sketch115
  ExternalGeometry = -> [Structure063]
  MapMode = 5
  Placement = pos=(0,9930,0) rot=(0,0.707107,0.707107;3.14159rad)
  Support = -> [Structure063]
  sketch-geometry (3):
    g0: LineSegment StartX=-15940 StartY=3626 StartZ=0 EndX=-15222 EndY=3626 EndZ=0
    g1: LineSegment StartX=-15222 StartY=3626 StartZ=0 EndX=-15120 EndY=3524 EndZ=0
    g2: LineSegment StartX=-15120 StartY=3524 StartZ=0 EndX=-11430 EndY=3524 EndZ=0
  constraints (10):
    c: Horizontal(g0)
    c: Coincident(g0,g1)
    c: Coincident(g1,g2)
    c: Horizontal(g2)
    c: Angle(g2,g1) = 2.35619
    c: DistanceX(g-4,g1) = 830
    c: DistanceY(g-4,g1) = 24
    c: DistanceY(g0,g-3) = 24
    c: DistanceX(g-3,g0) = 10
    c: DistanceX(g2,g-4) = 0
FEATURE [Part::FeaturePython] Rebar040  # Arch/BIM 110 (typed FeaturePython)
  Amount = 13
  Base = -> Sketch115
  Diameter = 8
  Direction = (0,0,0)
  Distance = 0
  HorizontalArea = 0
  Host = -> Structure063
  IfcType = 110
  Length = 4552.25
  MoveBase = false
  MoveWithHost = false
  OffsetEnd = 10
  OffsetStart = 10
  PerimeterLength = 0
  PlacementList = 13 placements: arithmetic series from (0,-10,2.22045e-15) step (0,-396.667,8.80777e-14) to (0,-4770,1.05915e-12)
  Rounding = 0
  Spacing = 396.667
  TotalLength = 59179.2
  VerticalArea = 0
FEATURE [Sketcher::SketchObject] Sketch116
  ExternalGeometry = -> [Structure063]
  MapMode = 5
  Placement = pos=(0,9930,0) rot=(0,0.707107,0.707107;3.14159rad)
  Support = -> [Structure063]
  sketch-geometry (3):
    g0: LineSegment StartX=-15940 StartY=3524 StartZ=0 EndX=-12710 EndY=3524 EndZ=0
    g1: LineSegment StartX=-12710 StartY=3524 StartZ=0 EndX=-12608 EndY=3626 EndZ=0
    g2: LineSegment StartX=-12608 StartY=3626 StartZ=0 EndX=-11430 EndY=3626 EndZ=0
  constraints (10):
    c: Horizontal(g0)
    c: Coincident(g0,g1)
    c: Coincident(g1,g2)
    c: Horizontal(g2)
    c: Angle(g1,g0) = 2.35619
    c: DistanceX(g2,g-3) = 0
    c: DistanceX(g0,g-4) = 1280
    c: DistanceX(g-4,g0) = 10
    c: DistanceY(g-4,g0) = 24
    c: DistanceY(g2,g-3) = 24
FEATURE [Part::FeaturePython] Rebar041  # Arch/BIM 110 (typed FeaturePython)
  Amount = 12
  Base = -> Sketch116
  Diameter = 8
  Direction = (0,0,0)
  Distance = 0
  HorizontalArea = 0
  Host = -> Structure063
  IfcType = 110
  Length = 4552.25
  MoveBase = false
  MoveWithHost = false
  OffsetEnd = 210
  OffsetStart = 210
  PerimeterLength = 0
  PlacementList = 12 placements: arithmetic series from (0,-210,4.66294e-14) step (0,-396.364,8.80104e-14) to (0,-4570,1.01474e-12)
  Rounding = 0
  Spacing = 396.364
  TotalLength = 54627
  VerticalArea = 0
FEATURE [Sketcher::SketchObject] Sketch117
  ExternalGeometry = -> [Structure063]
  MapMode = 5
  Placement = pos=(15950,0,0) rot=(0.57735,0.57735,0.57735;2.0944rad)
  Support = -> [Structure063]
  sketch-geometry (3):
    g0: LineSegment StartX=5150 StartY=3634 StartZ=0 EndX=6393 EndY=3634 EndZ=0
    g1: LineSegment StartX=6393 StartY=3634 StartZ=0 EndX=6495 EndY=3532 EndZ=0
    g2: LineSegment StartX=6495 StartY=3532 StartZ=0 EndX=9920 EndY=3532 EndZ=0
  constraints (10):
    c: Horizontal(g0)
    c: Coincident(g0,g1)
    c: Coincident(g1,g2)
    c: Horizontal(g2)
    c: DistanceX(g-3,g0) = 0
    c: DistanceX(g-4,g1) = 1345
    c: DistanceX(g2,g-4) = 10
    c: Angle(g2,g1) = 2.35619
    c: DistanceY(g-4,g2) = 32
    c: DistanceY(g0,g-3) = 16
FEATURE [Part::FeaturePython] Rebar042  # Arch/BIM 110 (typed FeaturePython)
  Amount = 12
  Base = -> Sketch117
  Diameter = 8
  Direction = (0,0,0)
  Distance = 0
  HorizontalArea = 0
  Host = -> Structure063
  IfcType = 110
  Length = 4812.25
  MoveBase = false
  MoveWithHost = false
  OffsetEnd = 10
  OffsetStart = 10
  PerimeterLength = 0
  PlacementList = 12 placements: arithmetic series from (-10,0,0) step (-409.091,0,0) to (-4510,0,0)
  Rounding = 0
  Spacing = 409.091
  TotalLength = 57747
  VerticalArea = 0
FEATURE [Sketcher::SketchObject] Sketch118
  ExternalGeometry = -> [Structure063]
  MapMode = 5
  Placement = pos=(15950,0,0) rot=(0.57735,0.57735,0.57735;2.0944rad)
  Support = -> [Structure063]
  sketch-geometry (3):
    g0: LineSegment StartX=5150 StartY=3532 StartZ=0 EndX=9060 EndY=3532 EndZ=0
    g1: LineSegment StartX=9060 StartY=3532 StartZ=0 EndX=9162 EndY=3634 EndZ=0
    g2: LineSegment StartX=9162 StartY=3634 StartZ=0 EndX=9920 EndY=3634 EndZ=0
  constraints (10):
    c: Horizontal(g0)
    c: Coincident(g0,g1)
    c: Coincident(g1,g2)
    c: Horizontal(g2)
    c: Angle(g1,g0) = 2.35619
    c: DistanceY(g2,g-3) = 16
    c: DistanceX(g0,g-4) = 870
    c: DistanceX(g2,g-3) = 10
    c: DistanceY(g-4,g0) = 32
    c: DistanceX(g-4,g0) = 0
FEATURE [Part::FeaturePython] Rebar043  # Arch/BIM 110 (typed FeaturePython)
  Amount = 11
  Base = -> Sketch118
  Diameter = 8
  Direction = (0,0,0)
  Distance = 0
  HorizontalArea = 0
  Host = -> Structure063
  IfcType = 110
  Length = 4812.25
  MoveBase = false
  MoveWithHost = false
  OffsetEnd = 210
  OffsetStart = 210
  PerimeterLength = 0
  PlacementList = 11 placements: arithmetic series from (-210,0,0) step (-410,0,0) to (-4310,0,0)
  Rounding = 0
  Spacing = 410
  TotalLength = 52934.7
  VerticalArea = 0
FEATURE [Sketcher::SketchObject] Sketch119
  ExternalGeometry = -> [Structure065]
  MapMode = 5
  Placement = pos=(0,3650,0) rot=(1,0,0;1.5708rad)
  Support = -> [Structure065]
  sketch-geometry (1):
    g0: LineSegment StartX=5400 StartY=3533 StartZ=0 EndX=11420 EndY=3533 EndZ=0
  constraints (2):
    c: DistanceY(g-3,g0) = 33
    c: DistanceY(g-3,g0) = 33
FEATURE [Part::FeaturePython] Rebar044  label="StraightRebar022"  # Arch/BIM 110 (typed FeaturePython)
  Amount = 8
  AmountCheck = true
  Base = -> Sketch119
  Cover = 20
  CoverAlong = Bottom Side
  Diameter = 8
  Direction = (0,0,0)
  Distance = 0
  FrontCover = 10
  HorizontalArea = 0
  Host = -> Structure065
  IfcType = 110
  LeftBottomCover = 10
  Length = 6020
  MoveBase = false
  MoveWithHost = false
  OffsetEnd = 10
  OffsetStart = 10
  Orientation = Horizontal
  PerimeterLength = 0
  PlacementList = 8 placements: arithmetic series from (0,10,-2.22045e-15) step (0,211.429,-4.69466e-14) to (0,1490,-3.30846e-13)
  RightTopCover = 10
  Rounding = 0
  Spacing = 211.429
  TotalLength = 48160
  TrueSpacing = 3
  VerticalArea = 0
FEATURE [Sketcher::SketchObject] Sketch120
  ExternalGeometry = -> [Structure065]
  MapMode = 5
  Placement = pos=(5390,0,0) rot=(0.57735,-0.57735,-0.57735;2.0944rad)
  Support = -> [Structure065]
  sketch-geometry (1):
    g0: LineSegment StartX=3650 StartY=3524 StartZ=0 EndX=5140 EndY=3524 EndZ=0
  constraints (2):
    c: DistanceY(g-3,g0) = 24
    c: Horizontal(g0)
FEATURE [Part::FeaturePython] Rebar045  label="StraightRebar023"  # Arch/BIM 110 (typed FeaturePython)
  Amount = 31
  AmountCheck = true
  Base = -> Sketch120
  Cover = 20
  CoverAlong = Bottom Side
  Diameter = 10
  Direction = (0,0,0)
  Distance = 0
  FrontCover = 10
  HorizontalArea = 0
  Host = -> Structure065
  IfcType = 110
  LeftBottomCover = 0
  Length = 1490
  MoveBase = false
  MoveWithHost = false
  OffsetEnd = 10
  OffsetStart = 10
  Orientation = Horizontal
  PerimeterLength = 0
  Placement = pos=(0,8800,0) rot=(0,0,1;0rad)
  PlacementList = 31 placements: arithmetic series from (10,0,0) step (200.667,0,0) to (6030,0,0)
  RightTopCover = 10
  Rounding = 0
  Spacing = 200.667
  TotalLength = 46190
  TrueSpacing = 15
  VerticalArea = 0
FEATURE [Sketcher::SketchObject] Sketch121
  ExternalGeometry = -> [Structure064]
  MapMode = 5
  Placement = pos=(0,0,0) rot=(0.57735,-0.57735,-0.57735;2.0944rad)
  Support = -> [Structure064]
  sketch-geometry (1):
    g0: LineSegment StartX=-825 StartY=3620 StartZ=0 EndX=-10 EndY=3620 EndZ=0
  constraints (4):
    c: Horizontal(g0)
    c: DistanceX(g0,g-3) = 10
    c: DistanceY(g0,g-3) = 30
    c: DistanceX(g0,g0) = 815
FEATURE [Part::FeaturePython] Rebar046  # Arch/BIM 110 (typed FeaturePython)
  Amount = 15
  Base = -> Sketch121
  Diameter = 12
  Direction = (0,0,0)
  Distance = 0
  HorizontalArea = 0
  Host = -> Structure064
  IfcType = 110
  Length = 815
  MoveBase = false
  MoveWithHost = false
  OffsetEnd = 10
  OffsetStart = 10
  PerimeterLength = 0
  PlacementList = 15 placements: arithmetic series from (10,0,0) step (394.286,0,0) to (5530,0,0)
  Rounding = 0
  Spacing = 394.286
  TotalLength = 12225
  VerticalArea = 0
FEATURE [Sketcher::SketchObject] Sketch122
  ExternalGeometry = -> [Structure058]
  MapMode = 5
  Placement = pos=(0,0,0) rot=(0.57735,-0.57735,-0.57735;2.0944rad)
  Support = -> [Structure064]
  sketch-geometry (1):
    g0: LineSegment StartX=-6735 StartY=3620 StartZ=0 EndX=-3455 EndY=3620 EndZ=0
  constraints (4):
    c: Horizontal(g0)
    c: DistanceX(g0,g0) = 3280
    c: DistanceY(g0,g-3) = 30
    c: DistanceX(g-3,g0) = 1695
FEATURE [Part::FeaturePython] Rebar047  # Arch/BIM 110 (typed FeaturePython)
  Amount = 14
  Base = -> Sketch122
  Diameter = 12
  Direction = (0,0,0)
  Distance = 0
  HorizontalArea = 0
  Host = -> Structure064
  IfcType = 110
  Length = 3280
  MoveBase = false
  MoveWithHost = false
  OffsetEnd = 210
  OffsetStart = 210
  PerimeterLength = 0
  PlacementList = 14 placements: arithmetic series from (210,0,0) step (393.846,0,0) to (5330,0,0)
  Rounding = 0
  Spacing = 393.846
  TotalLength = 45920
  VerticalArea = 0
FEATURE [Sketcher::SketchObject] Sketch123
  ExternalGeometry = -> [Structure058]
  MapMode = 5
  Placement = pos=(-9.095e-13,0,0) rot=(0.57735,-0.57735,-0.57735;2.0944rad)
  Support = -> [Structure058]
  sketch-geometry (1):
    g0: LineSegment StartX=-9920 StartY=3620 StartZ=0 EndX=-9140 EndY=3620 EndZ=0
  constraints (4):
    c: Horizontal(g0)
    c: DistanceY(g0,g-3) = 30
    c: DistanceX(g-3,g0) = 10
    c: DistanceX(g0,g0) = 780
FEATURE [Part::FeaturePython] Rebar048  # Arch/BIM 110 (typed FeaturePython)
  Amount = 14
  Base = -> Sketch123
  Diameter = 12
  Direction = (0,0,0)
  Distance = 0
  HorizontalArea = 0
  Host = -> Structure058
  IfcType = 110
  Length = 780
  MoveBase = false
  MoveWithHost = false
  OffsetEnd = 254.3
  OffsetStart = 10
  PerimeterLength = 0
  PlacementList = 14 placements: arithmetic series from (10,0,0) step (394.285,0,0) to (5135.7,0,0)
  Rounding = 0
  Spacing = 394.285
  TotalLength = 10920
  VerticalArea = 0
FEATURE [Sketcher::SketchObject] Sketch124
  ExternalGeometry = -> [Structure064]
  MapMode = 5
  Placement = pos=(0,-9.095e-13,0) rot=(1,0,0;1.5708rad)
  Support = -> [Structure064]
  sketch-geometry (1):
    g0: LineSegment StartX=10 StartY=3630 StartZ=0 EndX=850 EndY=3630 EndZ=0
  constraints (4):
    c: Horizontal(g0)
    c: DistanceX(g-3,g0) = 10
    c: DistanceY(g0,g-3) = 20
    c: DistanceX(g0,g0) = 840
FEATURE [Part::FeaturePython] Rebar049  # Arch/BIM 110 (typed FeaturePython)
  Amount = 13
  Base = -> Sketch124
  Diameter = 8
  Direction = (0,0,0)
  Distance = 0
  HorizontalArea = 0
  Host = -> Structure064
  IfcType = 110
  Length = 840
  MoveBase = false
  MoveWithHost = false
  OffsetEnd = 210
  OffsetStart = 210
  PerimeterLength = 0
  PlacementList = 13 placements: arithmetic series from (0,210,-4.66294e-14) step (0,394.167,-8.75226e-14) to (0,4940,-1.0969e-12)
  Rounding = 0
  Spacing = 394.167
  TotalLength = 10920
  VerticalArea = 0
FEATURE [Sketcher::SketchObject] Sketch125
  ExternalGeometry = -> [Structure064]
  MapMode = 5
  Placement = pos=(0,-9.095e-13,0) rot=(1,0,0;1.5708rad)
  Support = -> [Structure064]
  sketch-geometry (1):
    g0: LineSegment StartX=4690 StartY=3630 StartZ=0 EndX=5530 EndY=3630 EndZ=0
  constraints (4):
    c: Horizontal(g0)
    c: DistanceX(g0,g-3) = 10
    c: DistanceX(g0,g0) = 840
    c: DistanceY(g0,g-3) = 20
FEATURE [Part::FeaturePython] Rebar050  # Arch/BIM 110 (typed FeaturePython)
  Amount = 14
  Base = -> Sketch125
  Diameter = 8
  Direction = (0,0,0)
  Distance = 0
  HorizontalArea = 0
  Host = -> Structure064
  IfcType = 110
  Length = 840
  MoveBase = false
  MoveWithHost = false
  OffsetEnd = 10
  OffsetStart = 10
  PerimeterLength = 0
  PlacementList = 14 placements: arithmetic series from (0,10,-2.22045e-15) step (0,394.615,-8.76222e-14) to (0,5140,-1.14131e-12)
  Rounding = 0
  Spacing = 394.615
  TotalLength = 11760
  VerticalArea = 0
FEATURE [Sketcher::SketchObject] Sketch126
  ExternalGeometry = -> [Structure058]
  MapMode = 5
  Placement = pos=(0,9930,0) rot=(0,0.707107,0.707107;3.14159rad)
  Support = -> [Structure058]
  sketch-geometry (1):
    g0: LineSegment StartX=-850 StartY=3630 StartZ=0 EndX=-10 EndY=3630 EndZ=0
  constraints (4):
    c: Horizontal(g0)
    c: DistanceY(g0,g-3) = 20
    c: DistanceX(g0,g-3) = 10
    c: DistanceX(g0,g0) = 840
FEATURE [Part::FeaturePython] Rebar051  # Arch/BIM 110 (typed FeaturePython)
  Amount = 13
  Base = -> Sketch126
  Diameter = 8
  Direction = (0,0,0)
  Distance = 0
  HorizontalArea = 0
  Host = -> Structure058
  IfcType = 110
  Length = 840
  MoveBase = false
  MoveWithHost = false
  OffsetEnd = 10
  OffsetStart = 10
  PerimeterLength = 0
  PlacementList = 13 placements: arithmetic series from (0,-10,2.22045e-15) step (0,-396.667,8.80777e-14) to (0,-4770,1.05915e-12)
  Rounding = 0
  Spacing = 396.667
  TotalLength = 10920
  VerticalArea = 0
FEATURE [Sketcher::SketchObject] Sketch127
  ExternalGeometry = -> [Structure058]
  MapMode = 5
  Placement = pos=(0,9930,0) rot=(0,0.707107,0.707107;3.14159rad)
  Support = -> [Structure058]
  sketch-geometry (1):
    g0: LineSegment StartX=-7203 StartY=3630 StartZ=0 EndX=-3623 EndY=3630 EndZ=0
  constraints (4):
    c: Horizontal(g0)
    c: DistanceX(g0,g0) = 3580
    c: DistanceX(g-3,g0) = 1767
    c: DistanceY(g0,g-3) = 20
FEATURE [Part::FeaturePython] Rebar052  # Arch/BIM 110 (typed FeaturePython)
  Amount = 12
  Base = -> Sketch127
  Diameter = 8
  Direction = (0,0,0)
  Distance = 0
  HorizontalArea = 0
  Host = -> Structure058
  IfcType = 110
  Length = 3580
  MoveBase = false
  MoveWithHost = false
  OffsetEnd = 210
  OffsetStart = 210
  PerimeterLength = 0
  PlacementList = 12 placements: arithmetic series from (0,-210,4.66294e-14) step (0,-396.364,8.80104e-14) to (0,-4570,1.01474e-12)
  Rounding = 0
  Spacing = 396.364
  TotalLength = 42960
  VerticalArea = 0
FEATURE [Sketcher::SketchObject] Sketch128
  ExternalGeometry = -> [Structure062]
  MapMode = 5
  Placement = pos=(0,-3.638e-12,0) rot=(1,0,0;1.5708rad)
  Support = -> [Structure062]
  sketch-geometry (1):
    g0: LineSegment StartX=11290 StartY=3620 StartZ=0 EndX=12040 EndY=3620 EndZ=0
  constraints (4):
    c: Horizontal(g0)
    c: DistanceY(g0,g-3) = 30
    c: DistanceX(g-3,g0) = 10
    c: DistanceX(g0,g0) = 750
FEATURE [Part::FeaturePython] Rebar053  # Arch/BIM 110 (typed FeaturePython)
  Amount = 13
  Base = -> Sketch128
  Diameter = 8
  Direction = (0,0,0)
  Distance = 0
  HorizontalArea = 0
  Host = -> Structure062
  IfcType = 110
  Length = 750
  MoveBase = false
  MoveWithHost = false
  OffsetEnd = 210
  OffsetStart = 210
  PerimeterLength = 0
  PlacementList = 13 placements: arithmetic series from (0,210,-4.66294e-14) step (0,394.167,-8.75226e-14) to (0,4940,-1.0969e-12)
  Rounding = 0
  Spacing = 394.167
  TotalLength = 9750
  VerticalArea = 0
FEATURE [Sketcher::SketchObject] Sketch129
  ExternalGeometry = -> [Structure062]
  MapMode = 5
  Placement = pos=(0,-3.638e-12,0) rot=(1,0,0;1.5708rad)
  Support = -> [Structure062]
  sketch-geometry (1):
    g0: LineSegment StartX=15940 StartY=3620 StartZ=0 EndX=15190 EndY=3620 EndZ=0
  constraints (4):
    c: Horizontal(g0)
    c: DistanceY(g0,g-3) = 30
    c: DistanceX(g0,g0) = 750
    c: DistanceX(g0,g-3) = 10
FEATURE [Part::FeaturePython] Rebar054  # Arch/BIM 110 (typed FeaturePython)
  Amount = 14
  Base = -> Sketch129
  Diameter = 8
  Direction = (0,0,0)
  Distance = 0
  HorizontalArea = 0
  Host = -> Structure062
  IfcType = 110
  Length = 750
  MoveBase = false
  MoveWithHost = false
  OffsetEnd = 10
  OffsetStart = 10
  PerimeterLength = 0
  PlacementList = 14 placements: arithmetic series from (0,10,-2.22045e-15) step (0,394.615,-8.76222e-14) to (0,5140,-1.14131e-12)
  Rounding = 0
  Spacing = 394.615
  TotalLength = 10500
  VerticalArea = 0
FEATURE [Sketcher::SketchObject] Sketch130
  ExternalGeometry = -> [Structure062]
  MapMode = 5
  Placement = pos=(15950,0,0) rot=(0.57735,0.57735,0.57735;2.0944rad)
  Support = -> [Structure062]
  sketch-geometry (1):
    g0: LineSegment StartX=10 StartY=3629 StartZ=0 EndX=825 EndY=3629 EndZ=0
  constraints (4):
    c: Horizontal(g0)
    c: DistanceY(g0,g-3) = 21
    c: DistanceX(g-3,g0) = 10
    c: DistanceX(g0,g0) = 815
FEATURE [Part::FeaturePython] Rebar055  # Arch/BIM 110 (typed FeaturePython)
  Amount = 13
  Base = -> Sketch130
  Diameter = 10
  Direction = (0,0,0)
  Distance = 0
  HorizontalArea = 0
  Host = -> Structure062
  IfcType = 110
  Length = 815
  MoveBase = false
  MoveWithHost = false
  OffsetEnd = 10
  OffsetStart = 10
  PerimeterLength = 0
  PlacementList = 13 placements: arithmetic series from (-10,0,0) step (-387.5,0,0) to (-4660,0,0)
  Rounding = 0
  Spacing = 387.5
  TotalLength = 10595
  VerticalArea = 0
FEATURE [Sketcher::SketchObject] Sketch131
  ExternalGeometry = -> [Structure062]
  MapMode = 5
  Placement = pos=(15950,0,0) rot=(0.57735,0.57735,0.57735;2.0944rad)
  Support = -> [Structure062]
  sketch-geometry (1):
    g0: LineSegment StartX=3455 StartY=3629 StartZ=0 EndX=5150 EndY=3629 EndZ=0
  constraints (4):
    c: Horizontal(g0)
    c: DistanceY(g0,g-3) = 21
    c: DistanceX(g0,g-3) = 0
    c: DistanceX(g0,g0) = 1695
FEATURE [Part::FeaturePython] Rebar056  # Arch/BIM 110 (typed FeaturePython)
  Amount = 12
  Base = -> Sketch131
  Diameter = 10
  Direction = (0,0,0)
  Distance = 0
  HorizontalArea = 0
  Host = -> Structure062
  IfcType = 110
  Length = 1695
  MoveBase = false
  MoveWithHost = false
  OffsetEnd = 210
  OffsetStart = 210
  PerimeterLength = 0
  PlacementList = 12 placements: arithmetic series from (-210,0,0) step (-386.364,0,0) to (-4460,0,0)
  Rounding = 0
  Spacing = 386.364
  TotalLength = 20340
  VerticalArea = 0
FEATURE [Sketcher::SketchObject] Sketch132
  ExternalGeometry = -> [Structure063]
  MapMode = 5
  Placement = pos=(15950,0,0) rot=(0.57735,0.57735,0.57735;2.0944rad)
  Support = -> [Structure063]
  sketch-geometry (1):
    g0: LineSegment StartX=5150 StartY=3634 StartZ=0 EndX=6735 EndY=3634 EndZ=0
  constraints (4):
    c: Horizontal(g0)
    c: DistanceX(g-3,g0) = 0
    c: DistanceY(g0,g-3) = 16
    c: DistanceX(g0,g0) = 1585
FEATURE [Part::FeaturePython] Rebar057  # Arch/BIM 110 (typed FeaturePython)
  Amount = 11
  Base = -> Sketch132
  Diameter = 10
  Direction = (0,0,0)
  Distance = 0
  HorizontalArea = 0
  Host = -> Structure063
  IfcType = 110
  Length = 1585
  MoveBase = false
  MoveWithHost = false
  OffsetEnd = 210
  OffsetStart = 210
  PerimeterLength = 0
  PlacementList = 11 placements: arithmetic series from (-210,0,0) step (-410,0,0) to (-4310,0,0)
  Rounding = 0
  Spacing = 410
  TotalLength = 17435
  VerticalArea = 0
FEATURE [Sketcher::SketchObject] Sketch133
  ExternalGeometry = -> [Structure063]
  MapMode = 5
  Placement = pos=(15950,0,0) rot=(0.57735,0.57735,0.57735;2.0944rad)
  Support = -> [Structure063]
  sketch-geometry (1):
    g0: LineSegment StartX=9920 StartY=3634 StartZ=0 EndX=9140 EndY=3634 EndZ=0
  constraints (4):
    c: Horizontal(g0)
    c: DistanceX(g0,g-3) = 10
    c: DistanceY(g0,g-3) = 16
    c: DistanceX(g0,g0) = 780
FEATURE [Part::FeaturePython] Rebar058  # Arch/BIM 110 (typed FeaturePython)
  Amount = 12
  Base = -> Sketch133
  Diameter = 10
  Direction = (0,0,0)
  Distance = 0
  HorizontalArea = 0
  Host = -> Structure063
  IfcType = 110
  Length = 780
  MoveBase = false
  MoveWithHost = false
  OffsetEnd = 10
  OffsetStart = 10
  PerimeterLength = 0
  PlacementList = 12 placements: arithmetic series from (-10,0,0) step (-409.091,0,0) to (-4510,0,0)
  Rounding = 0
  Spacing = 409.091
  TotalLength = 9360
  VerticalArea = 0
FEATURE [Sketcher::SketchObject] Sketch134
  ExternalGeometry = -> [Structure063]
  MapMode = 5
  Placement = pos=(0,9930,0) rot=(0,0.707107,0.707107;3.14159rad)
  Support = -> [Structure063]
  sketch-geometry (1):
    g0: LineSegment StartX=-15940 StartY=3626 StartZ=0 EndX=-15190 EndY=3626 EndZ=0
  constraints (4):
    c: Horizontal(g0)
    c: DistanceX(g0,g0) = 750
    c: DistanceX(g-3,g0) = 10
    c: DistanceY(g0,g-3) = 24
FEATURE [Part::FeaturePython] Rebar059  # Arch/BIM 110 (typed FeaturePython)
  Amount = 12
  Base = -> Sketch134
  Diameter = 8
  Direction = (0,0,0)
  Distance = 0
  HorizontalArea = 0
  Host = -> Structure063
  IfcType = 110
  Length = 750
  MoveBase = false
  MoveWithHost = false
  OffsetEnd = 210
  OffsetStart = 210
  PerimeterLength = 0
  PlacementList = 12 placements: arithmetic series from (0,-210,4.66294e-14) step (0,-396.364,8.80104e-14) to (0,-4570,1.01474e-12)
  Rounding = 0
  Spacing = 396.364
  TotalLength = 9000
  VerticalArea = 0
FEATURE [Sketcher::SketchObject] Sketch135
  ExternalGeometry = -> [Structure063]
  MapMode = 5
  Placement = pos=(0,9930,0) rot=(0,0.707107,0.707107;3.14159rad)
  Support = -> [Structure063]
  sketch-geometry (1):
    g0: LineSegment StartX=-11430 StartY=3626 StartZ=0 EndX=-12936 EndY=3626 EndZ=0
  constraints (4):
    c: Horizontal(g0)
    c: DistanceX(g0,g-3) = 0
    c: DistanceY(g0,g-3) = 24
    c: DistanceX(g0,g0) = 1506
FEATURE [Part::FeaturePython] Rebar060  # Arch/BIM 110 (typed FeaturePython)
  Amount = 13
  Base = -> Sketch135
  Diameter = 8
  Direction = (0,0,0)
  Distance = 0
  HorizontalArea = 0
  Host = -> Structure063
  IfcType = 110
  Length = 1506
  MoveBase = false
  MoveWithHost = false
  OffsetEnd = 10
  OffsetStart = 10
  PerimeterLength = 0
  PlacementList = 13 placements: arithmetic series from (0,-10,2.22045e-15) step (0,-396.667,8.80777e-14) to (0,-4770,1.05915e-12)
  Rounding = 0
  Spacing = 396.667
  TotalLength = 19578
  VerticalArea = 0
FEATURE [Sketcher::SketchObject] Sketch137
  ExternalGeometry = -> [Structure060]
  MapMode = 5
  Placement = pos=(5390,0,0) rot=(0.57735,-0.57735,-0.57735;2.0944rad)
  Support = -> [Structure060]
  sketch-geometry (1):
    g0: LineSegment StartX=-9920 StartY=3622 StartZ=0 EndX=-9140 EndY=3622 EndZ=0
  constraints (4):
    c: Horizontal(g0)
    c: DistanceX(g-3,g0) = 10
    c: DistanceY(g0,g-3) = 28
    c: DistanceX(g0,g0) = 780
FEATURE [Part::FeaturePython] Rebar061  # Arch/BIM 110 (typed FeaturePython)
  Amount = 16
  Base = -> Sketch137
  Diameter = 10
  Direction = (0,0,0)
  Distance = 0
  HorizontalArea = 0
  Host = -> Structure060
  IfcType = 110
  Length = 780
  MoveBase = false
  MoveWithHost = false
  OffsetEnd = 10
  OffsetStart = 10
  PerimeterLength = 0
  PlacementList = 16 placements: arithmetic series from (10,0,0) step (401.333,0,0) to (6030,0,0)
  Rounding = 0
  Spacing = 401.333
  TotalLength = 12480
  VerticalArea = 0
FEATURE [Sketcher::SketchObject] Sketch138
  ExternalGeometry = -> [Structure060]
  MapMode = 5
  Placement = pos=(5390,0,0) rot=(0.57735,-0.57735,-0.57735;2.0944rad)
  Support = -> [Structure060]
  sketch-geometry (1):
    g0: LineSegment StartX=-6735 StartY=3622 StartZ=0 EndX=-5150 EndY=3622 EndZ=0
  constraints (4):
    c: Horizontal(g0)
    c: DistanceX(g0,g-3) = 0
    c: DistanceX(g0,g0) = 1585
    c: DistanceY(g0,g-3) = 28
FEATURE [Part::FeaturePython] Rebar062  # Arch/BIM 110 (typed FeaturePython)
  Amount = 15
  Base = -> Sketch138
  Diameter = 10
  Direction = (0,0,0)
  Distance = 0
  HorizontalArea = 0
  Host = -> Structure060
  IfcType = 110
  Length = 1585
  MoveBase = false
  MoveWithHost = false
  OffsetEnd = 210
  OffsetStart = 210
  PerimeterLength = 0
  PlacementList = 15 placements: arithmetic series from (210,0,0) step (401.429,0,0) to (5830,0,0)
  Rounding = 0
  Spacing = 401.429
  TotalLength = 23775
  VerticalArea = 0
FEATURE [Sketcher::SketchObject] Sketch139
  ExternalGeometry = -> [Structure060]
  MapMode = 5
  Placement = pos=(0,9930,0) rot=(0,0.707107,0.707107;3.14159rad)
  Support = -> [Structure060]
  sketch-geometry (1):
    g0: LineSegment StartX=-11430 StartY=3630 StartZ=0 EndX=-9470 EndY=3630 EndZ=0
  constraints (4):
    c: Horizontal(g0)
    c: DistanceX(g-3,g0) = 0
    c: DistanceX(g0,g0) = 1960
    c: DistanceY(g0,g-3) = 20
FEATURE [Part::FeaturePython] Rebar063  # Arch/BIM 110 (typed FeaturePython)
  Amount = 13
  Base = -> Sketch139
  Diameter = 8
  Direction = (0,0,0)
  Distance = 0
  HorizontalArea = 0
  Host = -> Structure060
  IfcType = 110
  Length = 1960
  MoveBase = false
  MoveWithHost = false
  OffsetEnd = 10
  OffsetStart = 10
  PerimeterLength = 0
  PlacementList = 13 placements: arithmetic series from (0,-10,2.22045e-15) step (0,-396.667,8.80777e-14) to (0,-4770,1.05915e-12)
  Rounding = 0
  Spacing = 396.667
  TotalLength = 25480
  VerticalArea = 0
FEATURE [Spreadsheet::Sheet] RebarBillOfMaterial001  label="BOM Footing+RoofSlabs"
  cells = A1=Member; B1=No. of Rebars; C1=Diameter in mm; D1=Length in m/piece; E1=Total Length in m; E2=#8.0; F2=#10.0; G2=#12.0; A3=Footing001; B3=11; C3==12mm; D3==2012mm; G3==22132mm; B4=11; C4==12mm; D4==2012mm; G4==22132mm; A6=Footing004; B6=11; C6==12mm; D6==2012mm; G6==22132mm; B7=11; C7==12mm; D7==2012mm; G7==22132mm; A9=Footing006; B9=11; C9==12mm; D9==2012mm; G9==22132mm; B10=11; C10==12mm; D10==2012mm; G10==22132mm; A12=Footing008; B12=11; C12==12mm; D12==2012mm; G12==22132mm; B13=11; C13==12mm; D13==2012mm; G13==22132mm; A15=Footing002; B15=11; C15==12mm; D15==2012mm; G15==22132mm; B16=11; C16==12mm; D16==2012mm; G16==22132mm; A18=Footing009; B18=11; C18==12mm; D18==2012mm; G18==22132mm; B19=11; C19==12mm; D19==2012mm; G19==22132mm; A21=Footing003; B21=11; C21==12mm; D21==2012mm; G21==22132mm; B22=11; C22==12mm; D22==2012mm; G22==22132mm; A24=Footing005; B24=11; C24==12mm; D24==2012mm; G24==22132mm; B25=11; C25==12mm; D25==2012mm; G25==22132mm; A27=Footing007; B27=11; C27==12mm; D27==2012mm; G27==22132mm; B28=11; C28==12mm; D28==2012mm; G28==22132mm; A30=Footing010; B30=11; C30==12mm; D30==2012mm; G30==22132mm; B31=11; C31==12mm; D31==2012mm; G31==22132mm; A33=Footing011; B33=13; C33==12mm; D33==2412.0000000000009mm; G33==31356.000000000011mm; B34=13; C34==12mm; D34==2412.0000000000009mm; G34==31356.000000000011mm; A36=Footing012; B36=13; C36==12mm; D36==2412.0000000000009mm; G36==31356.000000000011mm; B37=13; C37==12mm; D37==2412.0000000000018mm; G37==31356.000000000022mm; A39=S105; B39=15; C39==10mm; D39==5177.2792206135764mm; F39==77659.188309203644mm; B40=14; C40==10mm; D40==5177.2792206135764mm; F40==72481.909088590066mm; B41=14; C41==10mm; D41==5557.2792206135873mm; F41==77801.909088590226mm; B42=13; C42==10mm; D42==5557.2792206135891mm; F42==72244.629867976662mm; B43=15; C43==12mm; D43==815mm; G43==12225mm; B44=14; C44==12mm; D44==3280mm; G44==45920mm; B45=13; C45==8mm; D45==840mm; E45==10920mm; B46=14; C46==8mm; D46==840mm; E46==11760mm; A48=S103; B48=14; C48==10mm; D48==4687.27922061358mm; F48==65621.909088590124mm; B49=13; C49==10mm; D49==4687.27922061358mm; F49==60934.629867976539mm; B50=13; C50==8mm; D50==5177.27922061358mm; E50==67304.629867976546mm; B51=12; C51==8mm; D51==5177.2792206141676mm; E51==62127.350647370011mm; B52=13; C52==8mm; D52==750mm; E52==9750mm; B53=14; C53==8mm; D53==750mm; E53==10500mm; B54=13; C54==10mm; D54==815mm; F54==10595mm; B55=12; C55==10mm; D55==1695mm; F55==20340mm; A57=S101; B57=14; C57==10mm; D57==4807.2792206135819mm; F57==67301.909088590153mm; B58=14; C58==10mm; D58==4807.2792206135809mm; F58==67301.909088590139mm; B59=13; C59==10mm; D59==5417.27922061358mm; F59==70424.629867976546mm; B60=12; C60==10mm; D60==5417.27922061358mm; F60==65007.35064736296mm; B61=14; +94 more cells
